# Revit family: CAVP
name_source: partatom
category: Mechanical Equipment
units: mm (PartAtom-declared; Revit-internal decimal feet)

## family parameters
Always vertical = Yes
Cut with Voids When Loaded = No
Part Type = Normal
Room Calculation Point = No
Round Connector Dimension = Use Radius
Shared = No
Work Plane-Based = No

## types (227) — shared parameters
0 = 0"
1" = 1"
1.5 = 1 1/2"
2" = 2"
2' = 24"
3" = 3"
4" = 4"
60 = 60.00°
85 = 85.00°
F-H = 2"
Manufacturer = Loren Cook Company
Model = CAVP
ONE EIGTH = 1/8"
Q = 1"
Q/2 = 1/2"
URL = www.lorencook.com

## per-type parameters (varying)
- 120_CAVP-9L_CLASS_1: ((M - (2 * (D - L - K - J))) / 2) + (TRANSITION / 2)=9 7/32"; (B/2)+1.5"=9 9/16"; (B/2)-.125"=7 15/16"; (D-J-K-L)*2=2 1/16"; (F-((F-H)/2))/2=8 3/4"; (M - (2 * (D - L - K - J)))/2=4 11/16"; (NOZZLE_HEIGHT - (NOZZLE_HEIGHT / 8 * 2)) / 2=10 1/2"; (NOZZLE_WB_OD - NOZZLE_TOP_OD) / 4=2 3/8"; -(F-((F-H)/2))/2=-8 3/4"; A=71"; A/2=35 1/2"; B=16 1/8"; B/2=8 1/16"; B/4=4 1/32"; C=43"; C/2=21 1/2"; CLASS=1"; D=32 13/16"; D-L-K-J=1 1/32"; D-M=21 3/8"; E=26 11/16"; E/2=13 11/32"; E/52*15=7 11/16"; F=21 1/2"; F/2=10 3/4"; H=19 1/2"; H/2=9 3/4"; HEIGHT=33 21/32"; J=6 1/2"; J+K+L=31 25/32"; K=11 7/8"; L=13 13/32"; M=11 7/16"; M-(2*(D-L-K-J))=9 3/8"; N=60"; N+(H/2)=69 3/4"; NOZZLE_BOTTOM_ID=12 13/16"; NOZZLE_BOTTOM_RAD=6 13/32"; NOZZLE_BOTTOM_RAD-3*2=13/32"; NOZZLE_HEIGHT=28"; NOZZLE_HEIGHT/7*2=7"; NOZZLE_SIZE=9"; NOZZLE_TOP_OD=13 1/2"; NOZZLE_TOP_RAD=6 3/4"; NOZZLE_WB/4=4 19/32"; NOZZLE_WB_OD=23"; NOZZLE_WB_RAD=11 1/2"; NOZZLE_WB_RAD-2"=9 1/2"; P=60"; R=22"; R*1.1=24 3/16"; R+((B/2)+1.5")=31 9/16"; R-((B/2)+1.5")=12 7/16"; TRANSITION=9 1/16"; TRANSITION/2=4 17/32"; Type Comments=Vari-Plume Laboratory Exhaust Centrifugal Airfoil Class 1 Arr 10
- 120_CAVP-9H_CLASS_1: ((M - (2 * (D - L - K - J))) / 2) + (TRANSITION / 2)=9 7/32"; (B/2)+1.5"=9 9/16"; (B/2)-.125"=7 15/16"; (D-J-K-L)*2=2 1/16"; (F-((F-H)/2))/2=8 3/4"; (M - (2 * (D - L - K - J)))/2=4 11/16"; (NOZZLE_HEIGHT - (NOZZLE_HEIGHT / 8 * 2)) / 2=10 1/2"; (NOZZLE_WB_OD - NOZZLE_TOP_OD) / 4=2 3/8"; -(F-((F-H)/2))/2=-8 3/4"; A=71"; A/2=35 1/2"; B=16 1/8"; B/2=8 1/16"; B/4=4 1/32"; C=43"; C/2=21 1/2"; CLASS=1"; D=32 13/16"; D-L-K-J=1 1/32"; D-M=21 3/8"; E=26 11/16"; E/2=13 11/32"; E/52*15=7 11/16"; F=21 1/2"; F/2=10 3/4"; H=19 1/2"; H/2=9 3/4"; HEIGHT=33 21/32"; J=6 1/2"; J+K+L=31 25/32"; K=11 7/8"; L=13 13/32"; M=11 7/16"; M-(2*(D-L-K-J))=9 3/8"; N=60"; N+(H/2)=69 3/4"; NOZZLE_BOTTOM_ID=12 13/16"; NOZZLE_BOTTOM_RAD=6 13/32"; NOZZLE_BOTTOM_RAD-3*2=13/32"; NOZZLE_HEIGHT=28"; NOZZLE_HEIGHT/7*2=7"; NOZZLE_SIZE=9"; NOZZLE_TOP_OD=13 1/2"; NOZZLE_TOP_RAD=6 3/4"; NOZZLE_WB/4=4 19/32"; NOZZLE_WB_OD=23"; NOZZLE_WB_RAD=11 1/2"; NOZZLE_WB_RAD-2"=9 1/2"; P=60"; R=22"; R*1.1=24 3/16"; R+((B/2)+1.5")=31 9/16"; R-((B/2)+1.5")=12 7/16"; TRANSITION=9 1/16"; TRANSITION/2=4 17/32"; Type Comments=Vari-Plume Laboratory Exhaust Centrifugal Airfoil Class 1 Arr 10
- 120_CAVP-9L_CLASS_2: ((M - (2 * (D - L - K - J))) / 2) + (TRANSITION / 2)=8 15/32"; (B/2)+1.5"=9 9/16"; (B/2)-.125"=7 15/16"; (D-J-K-L)*2=3 9/16"; (F-((F-H)/2))/2=8 3/4"; (M - (2 * (D - L - K - J)))/2=3 15/16"; (NOZZLE_HEIGHT - (NOZZLE_HEIGHT / 8 * 2)) / 2=10 1/2"; (NOZZLE_WB_OD - NOZZLE_TOP_OD) / 4=2 3/8"; -(F-((F-H)/2))/2=-8 3/4"; A=71"; A/2=35 1/2"; B=16 1/8"; B/2=8 1/16"; B/4=4 1/32"; C=43"; C/2=21 1/2"; CLASS=2"; D=36 13/16"; D-L-K-J=1 25/32"; D-M=25 3/8"; E=26 11/16"; E/2=13 11/32"; E/52*15=7 11/16"; F=21 1/2"; F/2=10 3/4"; H=19 1/2"; H/2=9 3/4"; HEIGHT=33 21/32"; J=6 1/4"; J+K+L=35 1/32"; K=15 3/8"; L=13 13/32"; M=11 7/16"; M-(2*(D-L-K-J))=7 7/8"; N=60"; N+(H/2)=69 3/4"; NOZZLE_BOTTOM_ID=12 13/16"; NOZZLE_BOTTOM_RAD=6 13/32"; NOZZLE_BOTTOM_RAD-3*2=13/32"; NOZZLE_HEIGHT=28"; NOZZLE_HEIGHT/7*2=7"; NOZZLE_SIZE=9"; NOZZLE_TOP_OD=13 1/2"; NOZZLE_TOP_RAD=6 3/4"; NOZZLE_WB/4=4 19/32"; NOZZLE_WB_OD=23"; NOZZLE_WB_RAD=11 1/2"; NOZZLE_WB_RAD-2"=9 1/2"; P=60"; R=22"; R*1.1=24 3/16"; R+((B/2)+1.5")=31 9/16"; R-((B/2)+1.5")=12 7/16"; TRANSITION=9 1/16"; TRANSITION/2=4 17/32"; Type Comments=Vari-Plume Laboratory Exhaust Centrifugal Airfoil Class 2 Arr 10
- 120_CAVP-9H_CLASS_2: ((M - (2 * (D - L - K - J))) / 2) + (TRANSITION / 2)=8 15/32"; (B/2)+1.5"=9 9/16"; (B/2)-.125"=7 15/16"; (D-J-K-L)*2=3 9/16"; (F-((F-H)/2))/2=8 3/4"; (M - (2 * (D - L - K - J)))/2=3 15/16"; (NOZZLE_HEIGHT - (NOZZLE_HEIGHT / 8 * 2)) / 2=10 1/2"; (NOZZLE_WB_OD - NOZZLE_TOP_OD) / 4=2 3/8"; -(F-((F-H)/2))/2=-8 3/4"; A=71"; A/2=35 1/2"; B=16 1/8"; B/2=8 1/16"; B/4=4 1/32"; C=43"; C/2=21 1/2"; CLASS=2"; D=36 13/16"; D-L-K-J=1 25/32"; D-M=25 3/8"; E=26 11/16"; E/2=13 11/32"; E/52*15=7 11/16"; F=21 1/2"; F/2=10 3/4"; H=19 1/2"; H/2=9 3/4"; HEIGHT=33 21/32"; J=6 1/4"; J+K+L=35 1/32"; K=15 3/8"; L=13 13/32"; M=11 7/16"; M-(2*(D-L-K-J))=7 7/8"; N=60"; N+(H/2)=69 3/4"; NOZZLE_BOTTOM_ID=12 13/16"; NOZZLE_BOTTOM_RAD=6 13/32"; NOZZLE_BOTTOM_RAD-3*2=13/32"; NOZZLE_HEIGHT=28"; NOZZLE_HEIGHT/7*2=7"; NOZZLE_SIZE=9"; NOZZLE_TOP_OD=13 1/2"; NOZZLE_TOP_RAD=6 3/4"; NOZZLE_WB/4=4 19/32"; NOZZLE_WB_OD=23"; NOZZLE_WB_RAD=11 1/2"; NOZZLE_WB_RAD-2"=9 1/2"; P=60"; R=22"; R*1.1=24 3/16"; R+((B/2)+1.5")=31 9/16"; R-((B/2)+1.5")=12 7/16"; TRANSITION=9 1/16"; TRANSITION/2=4 17/32"; Type Comments=Vari-Plume Laboratory Exhaust Centrifugal Airfoil Class 2 Arr 10
- 135_CAVP-9L_CLASS_1: ((M - (2 * (D - L - K - J))) / 2) + (TRANSITION / 2)=9 25/32"; (B/2)+1.5"=10 5/16"; (B/2)-.125"=8 11/16"; (D-J-K-L)*2=2 1/16"; (F-((F-H)/2))/2=8 3/4"; (M - (2 * (D - L - K - J)))/2=5 1/4"; (NOZZLE_HEIGHT - (NOZZLE_HEIGHT / 8 * 2)) / 2=10 1/2"; (NOZZLE_WB_OD - NOZZLE_TOP_OD) / 4=2 3/8"; -(F-((F-H)/2))/2=-8 3/4"; A=73 11/16"; A/2=36 27/32"; B=17 5/8"; B/2=8 13/16"; B/4=4 13/32"; C=45 11/16"; C/2=22 27/32"; CLASS=1"; D=34 5/16"; D-L-K-J=1 1/32"; D-M=21 3/4"; E=29 13/16"; E/2=14 29/32"; E/52*15=8 19/32"; F=21 1/2"; F/2=10 3/4"; H=19 1/2"; H/2=9 3/4"; HEIGHT=35 1/32"; J=6 1/2"; J+K+L=33 9/32"; K=12 1/4"; L=14 17/32"; M=12 9/16"; M-(2*(D-L-K-J))=10 1/2"; N=60"; N+(H/2)=69 3/4"; NOZZLE_BOTTOM_ID=12 13/16"; NOZZLE_BOTTOM_RAD=6 13/32"; NOZZLE_BOTTOM_RAD-3*2=13/32"; NOZZLE_HEIGHT=28"; NOZZLE_HEIGHT/7*2=7"; NOZZLE_SIZE=9"; NOZZLE_TOP_OD=13 1/2"; NOZZLE_TOP_RAD=6 3/4"; NOZZLE_WB/4=4 19/32"; NOZZLE_WB_OD=23"; NOZZLE_WB_RAD=11 1/2"; NOZZLE_WB_RAD-2"=9 1/2"; P=60"; R=22"; R*1.1=24 3/16"; R+((B/2)+1.5")=32 5/16"; R-((B/2)+1.5")=11 11/16"; TRANSITION=9 1/16"; TRANSITION/2=4 17/32"; Type Comments=Vari-Plume Laboratory Exhaust Centrifugal Airfoil Class 1 Arr 10
- 135_CAVP-9H_CLASS_1: ((M - (2 * (D - L - K - J))) / 2) + (TRANSITION / 2)=9 25/32"; (B/2)+1.5"=10 5/16"; (B/2)-.125"=8 11/16"; (D-J-K-L)*2=2 1/16"; (F-((F-H)/2))/2=8 3/4"; (M - (2 * (D - L - K - J)))/2=5 1/4"; (NOZZLE_HEIGHT - (NOZZLE_HEIGHT / 8 * 2)) / 2=10 1/2"; (NOZZLE_WB_OD - NOZZLE_TOP_OD) / 4=2 3/8"; -(F-((F-H)/2))/2=-8 3/4"; A=73 11/16"; A/2=36 27/32"; B=17 5/8"; B/2=8 13/16"; B/4=4 13/32"; C=45 11/16"; C/2=22 27/32"; CLASS=1"; D=34 5/16"; D-L-K-J=1 1/32"; D-M=21 3/4"; E=29 13/16"; E/2=14 29/32"; E/52*15=8 19/32"; F=21 1/2"; F/2=10 3/4"; H=19 1/2"; H/2=9 3/4"; HEIGHT=35 1/32"; J=6 1/2"; J+K+L=33 9/32"; K=12 1/4"; L=14 17/32"; M=12 9/16"; M-(2*(D-L-K-J))=10 1/2"; N=60"; N+(H/2)=69 3/4"; NOZZLE_BOTTOM_ID=12 13/16"; NOZZLE_BOTTOM_RAD=6 13/32"; NOZZLE_BOTTOM_RAD-3*2=13/32"; NOZZLE_HEIGHT=28"; NOZZLE_HEIGHT/7*2=7"; NOZZLE_SIZE=9"; NOZZLE_TOP_OD=13 1/2"; NOZZLE_TOP_RAD=6 3/4"; NOZZLE_WB/4=4 19/32"; NOZZLE_WB_OD=23"; NOZZLE_WB_RAD=11 1/2"; NOZZLE_WB_RAD-2"=9 1/2"; P=60"; R=22"; R*1.1=24 3/16"; R+((B/2)+1.5")=32 5/16"; R-((B/2)+1.5")=11 11/16"; TRANSITION=9 1/16"; TRANSITION/2=4 17/32"; Type Comments=Vari-Plume Laboratory Exhaust Centrifugal Airfoil Class 1 Arr 10
- 135_CAVP-9L_CLASS_2: ((M - (2 * (D - L - K - J))) / 2) + (TRANSITION / 2)=9 25/32"; (B/2)+1.5"=10 5/16"; (B/2)-.125"=8 11/16"; (D-J-K-L)*2=2 1/16"; (F-((F-H)/2))/2=8 3/4"; (M - (2 * (D - L - K - J)))/2=5 1/4"; (NOZZLE_HEIGHT - (NOZZLE_HEIGHT / 8 * 2)) / 2=10 1/2"; (NOZZLE_WB_OD - NOZZLE_TOP_OD) / 4=2 3/8"; -(F-((F-H)/2))/2=-8 3/4"; A=73 11/16"; A/2=36 27/32"; B=17 5/8"; B/2=8 13/16"; B/4=4 13/32"; C=45 11/16"; C/2=22 27/32"; CLASS=2"; D=37 3/16"; D-L-K-J=1 1/32"; D-M=24 5/8"; E=29 13/16"; E/2=14 29/32"; E/52*15=8 19/32"; F=21 1/2"; F/2=10 3/4"; H=19 1/2"; H/2=9 3/4"; HEIGHT=35 1/32"; J=6 1/4"; J+K+L=36 5/32"; K=15 3/8"; L=14 17/32"; M=12 9/16"; M-(2*(D-L-K-J))=10 1/2"; N=60"; N+(H/2)=69 3/4"; NOZZLE_BOTTOM_ID=12 13/16"; NOZZLE_BOTTOM_RAD=6 13/32"; NOZZLE_BOTTOM_RAD-3*2=13/32"; NOZZLE_HEIGHT=28"; NOZZLE_HEIGHT/7*2=7"; NOZZLE_SIZE=9"; NOZZLE_TOP_OD=13 1/2"; NOZZLE_TOP_RAD=6 3/4"; NOZZLE_WB/4=4 19/32"; NOZZLE_WB_OD=23"; NOZZLE_WB_RAD=11 1/2"; NOZZLE_WB_RAD-2"=9 1/2"; P=60"; R=22"; R*1.1=24 3/16"; R+((B/2)+1.5")=32 5/16"; R-((B/2)+1.5")=11 11/16"; TRANSITION=9 1/16"; TRANSITION/2=4 17/32"; Type Comments=Vari-Plume Laboratory Exhaust Centrifugal Airfoil Class 2 Arr 10
- 135_CAVP-9H_CLASS_2: ((M - (2 * (D - L - K - J))) / 2) + (TRANSITION / 2)=9 25/32"; (B/2)+1.5"=10 5/16"; (B/2)-.125"=8 11/16"; (D-J-K-L)*2=2 1/16"; (F-((F-H)/2))/2=8 3/4"; (M - (2 * (D - L - K - J)))/2=5 1/4"; (NOZZLE_HEIGHT - (NOZZLE_HEIGHT / 8 * 2)) / 2=10 1/2"; (NOZZLE_WB_OD - NOZZLE_TOP_OD) / 4=2 3/8"; -(F-((F-H)/2))/2=-8 3/4"; A=73 11/16"; A/2=36 27/32"; B=17 5/8"; B/2=8 13/16"; B/4=4 13/32"; C=45 11/16"; C/2=22 27/32"; CLASS=2"; D=37 3/16"; D-L-K-J=1 1/32"; D-M=24 5/8"; E=29 13/16"; E/2=14 29/32"; E/52*15=8 19/32"; F=21 1/2"; F/2=10 3/4"; H=19 1/2"; H/2=9 3/4"; HEIGHT=35 1/32"; J=6 1/4"; J+K+L=36 5/32"; K=15 3/8"; L=14 17/32"; M=12 9/16"; M-(2*(D-L-K-J))=10 1/2"; N=60"; N+(H/2)=69 3/4"; NOZZLE_BOTTOM_ID=12 13/16"; NOZZLE_BOTTOM_RAD=6 13/32"; NOZZLE_BOTTOM_RAD-3*2=13/32"; NOZZLE_HEIGHT=28"; NOZZLE_HEIGHT/7*2=7"; NOZZLE_SIZE=9"; NOZZLE_TOP_OD=13 1/2"; NOZZLE_TOP_RAD=6 3/4"; NOZZLE_WB/4=4 19/32"; NOZZLE_WB_OD=23"; NOZZLE_WB_RAD=11 1/2"; NOZZLE_WB_RAD-2"=9 1/2"; P=60"; R=22"; R*1.1=24 3/16"; R+((B/2)+1.5")=32 5/16"; R-((B/2)+1.5")=11 11/16"; TRANSITION=9 1/16"; TRANSITION/2=4 17/32"; Type Comments=Vari-Plume Laboratory Exhaust Centrifugal Airfoil Class 2 Arr 10
- 150_CAVP-9L_CLASS_1: ((M - (2 * (D - L - K - J))) / 2) + (TRANSITION / 2)=10 11/32"; (B/2)+1.5"=11 1/16"; (B/2)-.125"=9 7/16"; (D-J-K-L)*2=2 1/16"; (F-((F-H)/2))/2=8 3/4"; (M - (2 * (D - L - K - J)))/2=5 13/16"; (NOZZLE_HEIGHT - (NOZZLE_HEIGHT / 8 * 2)) / 2=10 1/2"; (NOZZLE_WB_OD - NOZZLE_TOP_OD) / 4=2 3/8"; -(F-((F-H)/2))/2=-8 3/4"; A=78"; A/2=39"; B=19 1/8"; B/2=9 9/16"; B/4=4 25/32"; C=46 3/4"; C/2=23 3/8"; CLASS=1"; D=35 7/16"; D-L-K-J=1 1/32"; D-M=21 3/4"; E=32 7/8"; E/2=16 7/16"; E/52*15=9 15/32"; F=21 1/2"; F/2=10 3/4"; H=19 1/2"; H/2=9 3/4"; HEIGHT=36 11/32"; J=6 1/2"; J+K+L=34 13/32"; K=12 1/4"; L=15 21/32"; M=13 11/16"; M-(2*(D-L-K-J))=11 5/8"; N=60"; N+(H/2)=69 3/4"; NOZZLE_BOTTOM_ID=12 13/16"; NOZZLE_BOTTOM_RAD=6 13/32"; NOZZLE_BOTTOM_RAD-3*2=13/32"; NOZZLE_HEIGHT=28"; NOZZLE_HEIGHT/7*2=7"; NOZZLE_SIZE=9"; NOZZLE_TOP_OD=13 1/2"; NOZZLE_TOP_RAD=6 3/4"; NOZZLE_WB/4=4 19/32"; NOZZLE_WB_OD=23"; NOZZLE_WB_RAD=11 1/2"; NOZZLE_WB_RAD-2"=9 1/2"; P=60"; R=22"; R*1.1=24 3/16"; R+((B/2)+1.5")=33 1/16"; R-((B/2)+1.5")=10 15/16"; TRANSITION=9 1/16"; TRANSITION/2=4 17/32"; Type Comments=Vari-Plume Laboratory Exhaust Centrifugal Airfoil Class 1 Arr 10
- 150_CAVP-9H_CLASS_1: ((M - (2 * (D - L - K - J))) / 2) + (TRANSITION / 2)=10 11/32"; (B/2)+1.5"=11 1/16"; (B/2)-.125"=9 7/16"; (D-J-K-L)*2=2 1/16"; (F-((F-H)/2))/2=8 3/4"; (M - (2 * (D - L - K - J)))/2=5 13/16"; (NOZZLE_HEIGHT - (NOZZLE_HEIGHT / 8 * 2)) / 2=10 1/2"; (NOZZLE_WB_OD - NOZZLE_TOP_OD) / 4=2 3/8"; -(F-((F-H)/2))/2=-8 3/4"; A=78"; A/2=39"; B=19 1/8"; B/2=9 9/16"; B/4=4 25/32"; C=46 3/4"; C/2=23 3/8"; CLASS=1"; D=35 7/16"; D-L-K-J=1 1/32"; D-M=21 3/4"; E=32 7/8"; E/2=16 7/16"; E/52*15=9 15/32"; F=21 1/2"; F/2=10 3/4"; H=19 1/2"; H/2=9 3/4"; HEIGHT=36 11/32"; J=6 1/2"; J+K+L=34 13/32"; K=12 1/4"; L=15 21/32"; M=13 11/16"; M-(2*(D-L-K-J))=11 5/8"; N=60"; N+(H/2)=69 3/4"; NOZZLE_BOTTOM_ID=12 13/16"; NOZZLE_BOTTOM_RAD=6 13/32"; NOZZLE_BOTTOM_RAD-3*2=13/32"; NOZZLE_HEIGHT=28"; NOZZLE_HEIGHT/7*2=7"; NOZZLE_SIZE=9"; NOZZLE_TOP_OD=13 1/2"; NOZZLE_TOP_RAD=6 3/4"; NOZZLE_WB/4=4 19/32"; NOZZLE_WB_OD=23"; NOZZLE_WB_RAD=11 1/2"; NOZZLE_WB_RAD-2"=9 1/2"; P=60"; R=22"; R*1.1=24 3/16"; R+((B/2)+1.5")=33 1/16"; R-((B/2)+1.5")=10 15/16"; TRANSITION=9 1/16"; TRANSITION/2=4 17/32"; Type Comments=Vari-Plume Laboratory Exhaust Centrifugal Airfoil Class 1 Arr 10
- 150_CAVP-9L_CLASS_2: ((M - (2 * (D - L - K - J))) / 2) + (TRANSITION / 2)=10 11/32"; (B/2)+1.5"=11 1/16"; (B/2)-.125"=9 7/16"; (D-J-K-L)*2=2 1/16"; (F-((F-H)/2))/2=8 3/4"; (M - (2 * (D - L - K - J)))/2=5 13/16"; (NOZZLE_HEIGHT - (NOZZLE_HEIGHT / 8 * 2)) / 2=10 1/2"; (NOZZLE_WB_OD - NOZZLE_TOP_OD) / 4=2 3/8"; -(F-((F-H)/2))/2=-8 3/4"; A=78"; A/2=39"; B=19 1/8"; B/2=9 9/16"; B/4=4 25/32"; C=46 3/4"; C/2=23 3/8"; CLASS=2"; D=38 5/16"; D-L-K-J=1 1/32"; D-M=24 5/8"; E=32 7/8"; E/2=16 7/16"; E/52*15=9 15/32"; F=21 1/2"; F/2=10 3/4"; H=19 1/2"; H/2=9 3/4"; HEIGHT=36 11/32"; J=6 1/4"; J+K+L=37 9/32"; K=15 3/8"; L=15 21/32"; M=13 11/16"; M-(2*(D-L-K-J))=11 5/8"; N=60"; N+(H/2)=69 3/4"; NOZZLE_BOTTOM_ID=12 13/16"; NOZZLE_BOTTOM_RAD=6 13/32"; NOZZLE_BOTTOM_RAD-3*2=13/32"; NOZZLE_HEIGHT=28"; NOZZLE_HEIGHT/7*2=7"; NOZZLE_SIZE=9"; NOZZLE_TOP_OD=13 1/2"; NOZZLE_TOP_RAD=6 3/4"; NOZZLE_WB/4=4 19/32"; NOZZLE_WB_OD=23"; NOZZLE_WB_RAD=11 1/2"; NOZZLE_WB_RAD-2"=9 1/2"; P=60"; R=22"; R*1.1=24 3/16"; R+((B/2)+1.5")=33 1/16"; R-((B/2)+1.5")=10 15/16"; TRANSITION=9 1/16"; TRANSITION/2=4 17/32"; Type Comments=Vari-Plume Laboratory Exhaust Centrifugal Airfoil Class 2 Arr 10
- 150_CAVP-9H_CLASS_2: ((M - (2 * (D - L - K - J))) / 2) + (TRANSITION / 2)=10 11/32"; (B/2)+1.5"=11 1/16"; (B/2)-.125"=9 7/16"; (D-J-K-L)*2=2 1/16"; (F-((F-H)/2))/2=8 3/4"; (M - (2 * (D - L - K - J)))/2=5 13/16"; (NOZZLE_HEIGHT - (NOZZLE_HEIGHT / 8 * 2)) / 2=10 1/2"; (NOZZLE_WB_OD - NOZZLE_TOP_OD) / 4=2 3/8"; -(F-((F-H)/2))/2=-8 3/4"; A=78"; A/2=39"; B=19 1/8"; B/2=9 9/16"; B/4=4 25/32"; C=46 3/4"; C/2=23 3/8"; CLASS=2"; D=38 5/16"; D-L-K-J=1 1/32"; D-M=24 5/8"; E=32 7/8"; E/2=16 7/16"; E/52*15=9 15/32"; F=21 1/2"; F/2=10 3/4"; H=19 1/2"; H/2=9 3/4"; HEIGHT=36 11/32"; J=6 1/4"; J+K+L=37 9/32"; K=15 3/8"; L=15 21/32"; M=13 11/16"; M-(2*(D-L-K-J))=11 5/8"; N=60"; N+(H/2)=69 3/4"; NOZZLE_BOTTOM_ID=12 13/16"; NOZZLE_BOTTOM_RAD=6 13/32"; NOZZLE_BOTTOM_RAD-3*2=13/32"; NOZZLE_HEIGHT=28"; NOZZLE_HEIGHT/7*2=7"; NOZZLE_SIZE=9"; NOZZLE_TOP_OD=13 1/2"; NOZZLE_TOP_RAD=6 3/4"; NOZZLE_WB/4=4 19/32"; NOZZLE_WB_OD=23"; NOZZLE_WB_RAD=11 1/2"; NOZZLE_WB_RAD-2"=9 1/2"; P=60"; R=22"; R*1.1=24 3/16"; R+((B/2)+1.5")=33 1/16"; R-((B/2)+1.5")=10 15/16"; TRANSITION=9 1/16"; TRANSITION/2=4 17/32"; Type Comments=Vari-Plume Laboratory Exhaust Centrifugal Airfoil Class 2 Arr 10
- 150_CAVP-12H_CLASS_2: ((M - (2 * (D - L - K - J))) / 2) + (TRANSITION / 2)=11 27/32"; (B/2)+1.5"=11 1/16"; (B/2)-.125"=9 7/16"; (D-J-K-L)*2=2 1/16"; (F-((F-H)/2))/2=8 3/4"; (M - (2 * (D - L - K - J)))/2=5 13/16"; (NOZZLE_HEIGHT - (NOZZLE_HEIGHT / 8 * 2)) / 2=12"; (NOZZLE_WB_OD - NOZZLE_TOP_OD) / 4=2 1/8"; -(F-((F-H)/2))/2=-8 3/4"; A=78"; A/2=39"; B=19 1/8"; B/2=9 9/16"; B/4=4 25/32"; C=46 3/4"; C/2=23 3/8"; CLASS=2"; D=38 5/16"; D-L-K-J=1 1/32"; D-M=24 5/8"; E=32 7/8"; E/2=16 7/16"; E/52*15=9 15/32"; F=21 1/2"; F/2=10 3/4"; H=19 1/2"; H/2=9 3/4"; HEIGHT=36 11/32"; J=6 1/4"; J+K+L=37 9/32"; K=15 3/8"; L=15 21/32"; M=13 11/16"; M-(2*(D-L-K-J))=11 5/8"; N=60"; N+(H/2)=69 3/4"; NOZZLE_BOTTOM_ID=17 1/16"; NOZZLE_BOTTOM_RAD=8 17/32"; NOZZLE_BOTTOM_RAD-3*2=2 17/32"; NOZZLE_HEIGHT=32"; NOZZLE_HEIGHT/7*2=8"; NOZZLE_SIZE=12"; NOZZLE_TOP_OD=19 1/2"; NOZZLE_TOP_RAD=9 3/4"; NOZZLE_WB/4=5 19/32"; NOZZLE_WB_OD=28"; NOZZLE_WB_RAD=14"; NOZZLE_WB_RAD-2"=12"; P=60"; R=22"; R*1.1=24 3/16"; R+((B/2)+1.5")=33 1/16"; R-((B/2)+1.5")=10 15/16"; TRANSITION=12 1/16"; TRANSITION/2=6 1/32"; Type Comments=Vari-Plume Laboratory Exhaust Centrifugal Airfoil Class 2 Arr 10
- 150_CAVP-12L_CLASS_2: ((M - (2 * (D - L - K - J))) / 2) + (TRANSITION / 2)=11 27/32"; (B/2)+1.5"=11 1/16"; (B/2)-.125"=9 7/16"; (D-J-K-L)*2=2 1/16"; (F-((F-H)/2))/2=8 3/4"; (M - (2 * (D - L - K - J)))/2=5 13/16"; (NOZZLE_HEIGHT - (NOZZLE_HEIGHT / 8 * 2)) / 2=12"; (NOZZLE_WB_OD - NOZZLE_TOP_OD) / 4=2 1/8"; -(F-((F-H)/2))/2=-8 3/4"; A=78"; A/2=39"; B=19 1/8"; B/2=9 9/16"; B/4=4 25/32"; C=46 3/4"; C/2=23 3/8"; CLASS=2"; D=38 5/16"; D-L-K-J=1 1/32"; D-M=24 5/8"; E=32 7/8"; E/2=16 7/16"; E/52*15=9 15/32"; F=21 1/2"; F/2=10 3/4"; H=19 1/2"; H/2=9 3/4"; HEIGHT=36 11/32"; J=6 1/4"; J+K+L=37 9/32"; K=15 3/8"; L=15 21/32"; M=13 11/16"; M-(2*(D-L-K-J))=11 5/8"; N=60"; N+(H/2)=69 3/4"; NOZZLE_BOTTOM_ID=17 1/16"; NOZZLE_BOTTOM_RAD=8 17/32"; NOZZLE_BOTTOM_RAD-3*2=2 17/32"; NOZZLE_HEIGHT=32"; NOZZLE_HEIGHT/7*2=8"; NOZZLE_SIZE=12"; NOZZLE_TOP_OD=19 1/2"; NOZZLE_TOP_RAD=9 3/4"; NOZZLE_WB/4=5 19/32"; NOZZLE_WB_OD=28"; NOZZLE_WB_RAD=14"; NOZZLE_WB_RAD-2"=12"; P=60"; R=22"; R*1.1=24 3/16"; R+((B/2)+1.5")=33 1/16"; R-((B/2)+1.5")=10 15/16"; TRANSITION=12 1/16"; TRANSITION/2=6 1/32"; Type Comments=Vari-Plume Laboratory Exhaust Centrifugal Airfoil Class 2 Arr 10
- 150_CAVP-12H_CLASS_1: ((M - (2 * (D - L - K - J))) / 2) + (TRANSITION / 2)=11 27/32"; (B/2)+1.5"=11 1/16"; (B/2)-.125"=9 7/16"; (D-J-K-L)*2=2 1/16"; (F-((F-H)/2))/2=8 3/4"; (M - (2 * (D - L - K - J)))/2=5 13/16"; (NOZZLE_HEIGHT - (NOZZLE_HEIGHT / 8 * 2)) / 2=12"; (NOZZLE_WB_OD - NOZZLE_TOP_OD) / 4=2 1/8"; -(F-((F-H)/2))/2=-8 3/4"; A=78"; A/2=39"; B=19 1/8"; B/2=9 9/16"; B/4=4 25/32"; C=46 3/4"; C/2=23 3/8"; CLASS=1"; D=35 7/16"; D-L-K-J=1 1/32"; D-M=21 3/4"; E=32 7/8"; E/2=16 7/16"; E/52*15=9 15/32"; F=21 1/2"; F/2=10 3/4"; H=19 1/2"; H/2=9 3/4"; HEIGHT=36 11/32"; J=6 1/2"; J+K+L=34 13/32"; K=12 1/4"; L=15 21/32"; M=13 11/16"; M-(2*(D-L-K-J))=11 5/8"; N=60"; N+(H/2)=69 3/4"; NOZZLE_BOTTOM_ID=17 1/16"; NOZZLE_BOTTOM_RAD=8 17/32"; NOZZLE_BOTTOM_RAD-3*2=2 17/32"; NOZZLE_HEIGHT=32"; NOZZLE_HEIGHT/7*2=8"; NOZZLE_SIZE=12"; NOZZLE_TOP_OD=19 1/2"; NOZZLE_TOP_RAD=9 3/4"; NOZZLE_WB/4=5 19/32"; NOZZLE_WB_OD=28"; NOZZLE_WB_RAD=14"; NOZZLE_WB_RAD-2"=12"; P=60"; R=22"; R*1.1=24 3/16"; R+((B/2)+1.5")=33 1/16"; R-((B/2)+1.5")=10 15/16"; TRANSITION=12 1/16"; TRANSITION/2=6 1/32"; Type Comments=Vari-Plume Laboratory Exhaust Centrifugal Airfoil Class 1 Arr 10
- 150_CAVP-12L_CLASS_1: ((M - (2 * (D - L - K - J))) / 2) + (TRANSITION / 2)=11 27/32"; (B/2)+1.5"=11 1/16"; (B/2)-.125"=9 7/16"; (D-J-K-L)*2=2 1/16"; (F-((F-H)/2))/2=8 3/4"; (M - (2 * (D - L - K - J)))/2=5 13/16"; (NOZZLE_HEIGHT - (NOZZLE_HEIGHT / 8 * 2)) / 2=12"; (NOZZLE_WB_OD - NOZZLE_TOP_OD) / 4=2 1/8"; -(F-((F-H)/2))/2=-8 3/4"; A=78"; A/2=39"; B=19 1/8"; B/2=9 9/16"; B/4=4 25/32"; C=46 3/4"; C/2=23 3/8"; CLASS=1"; D=35 7/16"; D-L-K-J=1 1/32"; D-M=21 3/4"; E=32 7/8"; E/2=16 7/16"; E/52*15=9 15/32"; F=21 1/2"; F/2=10 3/4"; H=19 1/2"; H/2=9 3/4"; HEIGHT=36 11/32"; J=6 1/2"; J+K+L=34 13/32"; K=12 1/4"; L=15 21/32"; M=13 11/16"; M-(2*(D-L-K-J))=11 5/8"; N=60"; N+(H/2)=69 3/4"; NOZZLE_BOTTOM_ID=17 1/16"; NOZZLE_BOTTOM_RAD=8 17/32"; NOZZLE_BOTTOM_RAD-3*2=2 17/32"; NOZZLE_HEIGHT=32"; NOZZLE_HEIGHT/7*2=8"; NOZZLE_SIZE=12"; NOZZLE_TOP_OD=19 1/2"; NOZZLE_TOP_RAD=9 3/4"; NOZZLE_WB/4=5 19/32"; NOZZLE_WB_OD=28"; NOZZLE_WB_RAD=14"; NOZZLE_WB_RAD-2"=12"; P=60"; R=22"; R*1.1=24 3/16"; R+((B/2)+1.5")=33 1/16"; R-((B/2)+1.5")=10 15/16"; TRANSITION=12 1/16"; TRANSITION/2=6 1/32"; Type Comments=Vari-Plume Laboratory Exhaust Centrifugal Airfoil Class 1 Arr 10
- 165_CAVP-9L_CLASS_1: ((M - (2 * (D - L - K - J))) / 2) + (TRANSITION / 2)=10 15/16"; (B/2)+1.5"=12 3/32"; (B/2)-.125"=10 15/32"; (D-J-K-L)*2=2 1/16"; (F-((F-H)/2))/2=11 1/16"; (M - (2 * (D - L - K - J)))/2=6 13/32"; (NOZZLE_HEIGHT - (NOZZLE_HEIGHT / 8 * 2)) / 2=10 1/2"; (NOZZLE_WB_OD - NOZZLE_TOP_OD) / 4=2 3/8"; -(F-((F-H)/2))/2=-11 1/16"; A=82 1/16"; A/2=41 1/32"; B=21 3/16"; B/2=10 19/32"; B/4=5 5/16"; C=50 13/16"; C/2=25 13/32"; CLASS=1"; D=37 5/8"; D-L-K-J=1 1/32"; D-M=22 3/4"; E=36"; E/2=18"; E/52*15=10 3/8"; F=26 1/8"; F/2=13 1/16"; H=24 1/8"; H/2=12 1/16"; HEIGHT=39 31/32"; J=7 1/2"; J+K+L=36 19/32"; K=12 1/4"; L=16 27/32"; M=14 7/8"; M-(2*(D-L-K-J))=12 13/16"; N=60"; N+(H/2)=72 1/16"; NOZZLE_BOTTOM_ID=12 13/16"; NOZZLE_BOTTOM_RAD=6 13/32"; NOZZLE_BOTTOM_RAD-3*2=13/32"; NOZZLE_HEIGHT=28"; NOZZLE_HEIGHT/7*2=7"; NOZZLE_SIZE=9"; NOZZLE_TOP_OD=13 1/2"; NOZZLE_TOP_RAD=6 3/4"; NOZZLE_WB/4=4 19/32"; NOZZLE_WB_OD=23"; NOZZLE_WB_RAD=11 1/2"; NOZZLE_WB_RAD-2"=9 1/2"; P=60"; R=24 1/4"; R*1.1=26 11/16"; R+((B/2)+1.5")=36 11/32"; R-((B/2)+1.5")=12 5/32"; TRANSITION=9 1/16"; TRANSITION/2=4 17/32"; Type Comments=Vari-Plume Laboratory Exhaust Centrifugal Airfoil Class 1 Arr 10
- 165_CAVP-9H_CLASS_1: ((M - (2 * (D - L - K - J))) / 2) + (TRANSITION / 2)=10 15/16"; (B/2)+1.5"=12 3/32"; (B/2)-.125"=10 15/32"; (D-J-K-L)*2=2 1/16"; (F-((F-H)/2))/2=11 1/16"; (M - (2 * (D - L - K - J)))/2=6 13/32"; (NOZZLE_HEIGHT - (NOZZLE_HEIGHT / 8 * 2)) / 2=10 1/2"; (NOZZLE_WB_OD - NOZZLE_TOP_OD) / 4=2 3/8"; -(F-((F-H)/2))/2=-11 1/16"; A=82 1/16"; A/2=41 1/32"; B=21 3/16"; B/2=10 19/32"; B/4=5 5/16"; C=50 13/16"; C/2=25 13/32"; CLASS=1"; D=37 5/8"; D-L-K-J=1 1/32"; D-M=22 3/4"; E=36"; E/2=18"; E/52*15=10 3/8"; F=26 1/8"; F/2=13 1/16"; H=24 1/8"; H/2=12 1/16"; HEIGHT=39 31/32"; J=7 1/2"; J+K+L=36 19/32"; K=12 1/4"; L=16 27/32"; M=14 7/8"; M-(2*(D-L-K-J))=12 13/16"; N=60"; N+(H/2)=72 1/16"; NOZZLE_BOTTOM_ID=12 13/16"; NOZZLE_BOTTOM_RAD=6 13/32"; NOZZLE_BOTTOM_RAD-3*2=13/32"; NOZZLE_HEIGHT=28"; NOZZLE_HEIGHT/7*2=7"; NOZZLE_SIZE=9"; NOZZLE_TOP_OD=13 1/2"; NOZZLE_TOP_RAD=6 3/4"; NOZZLE_WB/4=4 19/32"; NOZZLE_WB_OD=23"; NOZZLE_WB_RAD=11 1/2"; NOZZLE_WB_RAD-2"=9 1/2"; P=60"; R=24 1/4"; R*1.1=26 11/16"; R+((B/2)+1.5")=36 11/32"; R-((B/2)+1.5")=12 5/32"; TRANSITION=9 1/16"; TRANSITION/2=4 17/32"; Type Comments=Vari-Plume Laboratory Exhaust Centrifugal Airfoil Class 1 Arr 10
- 165_CAVP-12L_CLASS_1: ((M - (2 * (D - L - K - J))) / 2) + (TRANSITION / 2)=12 7/16"; (B/2)+1.5"=12 3/32"; (B/2)-.125"=10 15/32"; (D-J-K-L)*2=2 1/16"; (F-((F-H)/2))/2=11 1/16"; (M - (2 * (D - L - K - J)))/2=6 13/32"; (NOZZLE_HEIGHT - (NOZZLE_HEIGHT / 8 * 2)) / 2=12"; (NOZZLE_WB_OD - NOZZLE_TOP_OD) / 4=2 1/8"; -(F-((F-H)/2))/2=-11 1/16"; A=82 1/16"; A/2=41 1/32"; B=21 3/16"; B/2=10 19/32"; B/4=5 5/16"; C=50 13/16"; C/2=25 13/32"; CLASS=1"; D=37 5/8"; D-L-K-J=1 1/32"; D-M=22 3/4"; E=36"; E/2=18"; E/52*15=10 3/8"; F=26 1/8"; F/2=13 1/16"; H=24 1/8"; H/2=12 1/16"; HEIGHT=39 31/32"; J=7 1/2"; J+K+L=36 19/32"; K=12 1/4"; L=16 27/32"; M=14 7/8"; M-(2*(D-L-K-J))=12 13/16"; N=60"; N+(H/2)=72 1/16"; NOZZLE_BOTTOM_ID=17 1/16"; NOZZLE_BOTTOM_RAD=8 17/32"; NOZZLE_BOTTOM_RAD-3*2=2 17/32"; NOZZLE_HEIGHT=32"; NOZZLE_HEIGHT/7*2=8"; NOZZLE_SIZE=12"; NOZZLE_TOP_OD=19 1/2"; NOZZLE_TOP_RAD=9 3/4"; NOZZLE_WB/4=5 19/32"; NOZZLE_WB_OD=28"; NOZZLE_WB_RAD=14"; NOZZLE_WB_RAD-2"=12"; P=60"; R=24 1/4"; R*1.1=26 11/16"; R+((B/2)+1.5")=36 11/32"; R-((B/2)+1.5")=12 5/32"; TRANSITION=12 1/16"; TRANSITION/2=6 1/32"; Type Comments=Vari-Plume Laboratory Exhaust Centrifugal Airfoil Class 1 Arr 10
- 165_CAVP-12H_CLASS_1: ((M - (2 * (D - L - K - J))) / 2) + (TRANSITION / 2)=12 7/16"; (B/2)+1.5"=12 3/32"; (B/2)-.125"=10 15/32"; (D-J-K-L)*2=2 1/16"; (F-((F-H)/2))/2=11 1/16"; (M - (2 * (D - L - K - J)))/2=6 13/32"; (NOZZLE_HEIGHT - (NOZZLE_HEIGHT / 8 * 2)) / 2=12"; (NOZZLE_WB_OD - NOZZLE_TOP_OD) / 4=2 1/8"; -(F-((F-H)/2))/2=-11 1/16"; A=82 1/16"; A/2=41 1/32"; B=21 3/16"; B/2=10 19/32"; B/4=5 5/16"; C=50 13/16"; C/2=25 13/32"; CLASS=1"; D=37 5/8"; D-L-K-J=1 1/32"; D-M=22 3/4"; E=36"; E/2=18"; E/52*15=10 3/8"; F=26 1/8"; F/2=13 1/16"; H=24 1/8"; H/2=12 1/16"; HEIGHT=39 31/32"; J=7 1/2"; J+K+L=36 19/32"; K=12 1/4"; L=16 27/32"; M=14 7/8"; M-(2*(D-L-K-J))=12 13/16"; N=60"; N+(H/2)=72 1/16"; NOZZLE_BOTTOM_ID=17 1/16"; NOZZLE_BOTTOM_RAD=8 17/32"; NOZZLE_BOTTOM_RAD-3*2=2 17/32"; NOZZLE_HEIGHT=32"; NOZZLE_HEIGHT/7*2=8"; NOZZLE_SIZE=12"; NOZZLE_TOP_OD=19 1/2"; NOZZLE_TOP_RAD=9 3/4"; NOZZLE_WB/4=5 19/32"; NOZZLE_WB_OD=28"; NOZZLE_WB_RAD=14"; NOZZLE_WB_RAD-2"=12"; P=60"; R=24 1/4"; R*1.1=26 11/16"; R+((B/2)+1.5")=36 11/32"; R-((B/2)+1.5")=12 5/32"; TRANSITION=12 1/16"; TRANSITION/2=6 1/32"; Type Comments=Vari-Plume Laboratory Exhaust Centrifugal Airfoil Class 1 Arr 10
- 165_CAVP-9L_CLASS_2: ((M - (2 * (D - L - K - J))) / 2) + (TRANSITION / 2)=10 15/16"; (B/2)+1.5"=12 3/32"; (B/2)-.125"=10 15/32"; (D-J-K-L)*2=2 1/16"; (F-((F-H)/2))/2=11 1/16"; (M - (2 * (D - L - K - J)))/2=6 13/32"; (NOZZLE_HEIGHT - (NOZZLE_HEIGHT / 8 * 2)) / 2=10 1/2"; (NOZZLE_WB_OD - NOZZLE_TOP_OD) / 4=2 3/8"; -(F-((F-H)/2))/2=-11 1/16"; A=82 1/16"; A/2=41 1/32"; B=21 3/16"; B/2=10 19/32"; B/4=5 5/16"; C=50 13/16"; C/2=25 13/32"; CLASS=2"; D=44 1/2"; D-L-K-J=1 1/32"; D-M=29 5/8"; E=36"; E/2=18"; E/52*15=10 3/8"; F=26 1/8"; F/2=13 1/16"; H=24 1/8"; H/2=12 1/16"; HEIGHT=39 31/32"; J=7 1/4"; J+K+L=43 15/32"; K=19 3/8"; L=16 27/32"; M=14 7/8"; M-(2*(D-L-K-J))=12 13/16"; N=60"; N+(H/2)=72 1/16"; NOZZLE_BOTTOM_ID=12 13/16"; NOZZLE_BOTTOM_RAD=6 13/32"; NOZZLE_BOTTOM_RAD-3*2=13/32"; NOZZLE_HEIGHT=28"; NOZZLE_HEIGHT/7*2=7"; NOZZLE_SIZE=9"; NOZZLE_TOP_OD=13 1/2"; NOZZLE_TOP_RAD=6 3/4"; NOZZLE_WB/4=4 19/32"; NOZZLE_WB_OD=23"; NOZZLE_WB_RAD=11 1/2"; NOZZLE_WB_RAD-2"=9 1/2"; P=60"; R=24 1/4"; R*1.1=26 11/16"; R+((B/2)+1.5")=36 11/32"; R-((B/2)+1.5")=12 5/32"; TRANSITION=9 1/16"; TRANSITION/2=4 17/32"; Type Comments=Vari-Plume Laboratory Exhaust Centrifugal Airfoil Class 2 Arr 10
- 165_CAVP-9H_CLASS_2: ((M - (2 * (D - L - K - J))) / 2) + (TRANSITION / 2)=10 15/16"; (B/2)+1.5"=12 3/32"; (B/2)-.125"=10 15/32"; (D-J-K-L)*2=2 1/16"; (F-((F-H)/2))/2=11 1/16"; (M - (2 * (D - L - K - J)))/2=6 13/32"; (NOZZLE_HEIGHT - (NOZZLE_HEIGHT / 8 * 2)) / 2=10 1/2"; (NOZZLE_WB_OD - NOZZLE_TOP_OD) / 4=2 3/8"; -(F-((F-H)/2))/2=-11 1/16"; A=82 1/16"; A/2=41 1/32"; B=21 3/16"; B/2=10 19/32"; B/4=5 5/16"; C=50 13/16"; C/2=25 13/32"; CLASS=2"; D=44 1/2"; D-L-K-J=1 1/32"; D-M=29 5/8"; E=36"; E/2=18"; E/52*15=10 3/8"; F=26 1/8"; F/2=13 1/16"; H=24 1/8"; H/2=12 1/16"; HEIGHT=39 31/32"; J=7 1/4"; J+K+L=43 15/32"; K=19 3/8"; L=16 27/32"; M=14 7/8"; M-(2*(D-L-K-J))=12 13/16"; N=60"; N+(H/2)=72 1/16"; NOZZLE_BOTTOM_ID=12 13/16"; NOZZLE_BOTTOM_RAD=6 13/32"; NOZZLE_BOTTOM_RAD-3*2=13/32"; NOZZLE_HEIGHT=28"; NOZZLE_HEIGHT/7*2=7"; NOZZLE_SIZE=9"; NOZZLE_TOP_OD=13 1/2"; NOZZLE_TOP_RAD=6 3/4"; NOZZLE_WB/4=4 19/32"; NOZZLE_WB_OD=23"; NOZZLE_WB_RAD=11 1/2"; NOZZLE_WB_RAD-2"=9 1/2"; P=60"; R=24 1/4"; R*1.1=26 11/16"; R+((B/2)+1.5")=36 11/32"; R-((B/2)+1.5")=12 5/32"; TRANSITION=9 1/16"; TRANSITION/2=4 17/32"; Type Comments=Vari-Plume Laboratory Exhaust Centrifugal Airfoil Class 2 Arr 10
- 165_CAVP-12L_CLASS_2: ((M - (2 * (D - L - K - J))) / 2) + (TRANSITION / 2)=12 7/16"; (B/2)+1.5"=12 3/32"; (B/2)-.125"=10 15/32"; (D-J-K-L)*2=2 1/16"; (F-((F-H)/2))/2=11 1/16"; (M - (2 * (D - L - K - J)))/2=6 13/32"; (NOZZLE_HEIGHT - (NOZZLE_HEIGHT / 8 * 2)) / 2=12"; (NOZZLE_WB_OD - NOZZLE_TOP_OD) / 4=2 1/8"; -(F-((F-H)/2))/2=-11 1/16"; A=82 1/16"; A/2=41 1/32"; B=21 3/16"; B/2=10 19/32"; B/4=5 5/16"; C=50 13/16"; C/2=25 13/32"; CLASS=2"; D=44 1/2"; D-L-K-J=1 1/32"; D-M=29 5/8"; E=36"; E/2=18"; E/52*15=10 3/8"; F=26 1/8"; F/2=13 1/16"; H=24 1/8"; H/2=12 1/16"; HEIGHT=39 31/32"; J=7 1/4"; J+K+L=43 15/32"; K=19 3/8"; L=16 27/32"; M=14 7/8"; M-(2*(D-L-K-J))=12 13/16"; N=60"; N+(H/2)=72 1/16"; NOZZLE_BOTTOM_ID=17 1/16"; NOZZLE_BOTTOM_RAD=8 17/32"; NOZZLE_BOTTOM_RAD-3*2=2 17/32"; NOZZLE_HEIGHT=32"; NOZZLE_HEIGHT/7*2=8"; NOZZLE_SIZE=12"; NOZZLE_TOP_OD=19 1/2"; NOZZLE_TOP_RAD=9 3/4"; NOZZLE_WB/4=5 19/32"; NOZZLE_WB_OD=28"; NOZZLE_WB_RAD=14"; NOZZLE_WB_RAD-2"=12"; P=60"; R=24 1/4"; R*1.1=26 11/16"; R+((B/2)+1.5")=36 11/32"; R-((B/2)+1.5")=12 5/32"; TRANSITION=12 1/16"; TRANSITION/2=6 1/32"; Type Comments=Vari-Plume Laboratory Exhaust Centrifugal Airfoil Class 2 Arr 10
- 165_CAVP-12H_CLASS_2: ((M - (2 * (D - L - K - J))) / 2) + (TRANSITION / 2)=12 7/16"; (B/2)+1.5"=12 3/32"; (B/2)-.125"=10 15/32"; (D-J-K-L)*2=2 1/16"; (F-((F-H)/2))/2=11 1/16"; (M - (2 * (D - L - K - J)))/2=6 13/32"; (NOZZLE_HEIGHT - (NOZZLE_HEIGHT / 8 * 2)) / 2=12"; (NOZZLE_WB_OD - NOZZLE_TOP_OD) / 4=2 1/8"; -(F-((F-H)/2))/2=-11 1/16"; A=82 1/16"; A/2=41 1/32"; B=21 3/16"; B/2=10 19/32"; B/4=5 5/16"; C=50 13/16"; C/2=25 13/32"; CLASS=2"; D=44 1/2"; D-L-K-J=1 1/32"; D-M=29 5/8"; E=36"; E/2=18"; E/52*15=10 3/8"; F=26 1/8"; F/2=13 1/16"; H=24 1/8"; H/2=12 1/16"; HEIGHT=39 31/32"; J=7 1/4"; J+K+L=43 15/32"; K=19 3/8"; L=16 27/32"; M=14 7/8"; M-(2*(D-L-K-J))=12 13/16"; N=60"; N+(H/2)=72 1/16"; NOZZLE_BOTTOM_ID=17 1/16"; NOZZLE_BOTTOM_RAD=8 17/32"; NOZZLE_BOTTOM_RAD-3*2=2 17/32"; NOZZLE_HEIGHT=32"; NOZZLE_HEIGHT/7*2=8"; NOZZLE_SIZE=12"; NOZZLE_TOP_OD=19 1/2"; NOZZLE_TOP_RAD=9 3/4"; NOZZLE_WB/4=5 19/32"; NOZZLE_WB_OD=28"; NOZZLE_WB_RAD=14"; NOZZLE_WB_RAD-2"=12"; P=60"; R=24 1/4"; R*1.1=26 11/16"; R+((B/2)+1.5")=36 11/32"; R-((B/2)+1.5")=12 5/32"; TRANSITION=12 1/16"; TRANSITION/2=6 1/32"; Type Comments=Vari-Plume Laboratory Exhaust Centrifugal Airfoil Class 2 Arr 10
- 180_CAVP-9H_CLASS_1: ((M - (2 * (D - L - K - J))) / 2) + (TRANSITION / 2)=11 1/2"; (B/2)+1.5"=12 27/32"; (B/2)-.125"=11 7/32"; (D-J-K-L)*2=2 1/16"; (F-((F-H)/2))/2=11 1/16"; (M - (2 * (D - L - K - J)))/2=6 31/32"; (NOZZLE_HEIGHT - (NOZZLE_HEIGHT / 8 * 2)) / 2=10 1/2"; (NOZZLE_WB_OD - NOZZLE_TOP_OD) / 4=2 3/8"; -(F-((F-H)/2))/2=-11 1/16"; A=84 1/16"; A/2=42 1/32"; B=22 11/16"; B/2=11 11/32"; B/4=5 11/16"; C=52 13/16"; C/2=26 13/32"; CLASS=1"; D=42 1/8"; D-L-K-J=1 1/32"; D-M=26 1/8"; E=39 1/16"; E/2=19 17/32"; E/52*15=11 9/32"; F=26 1/8"; F/2=13 1/16"; H=24 1/8"; H/2=12 1/16"; HEIGHT=41 5/16"; J=8"; J+K+L=41 3/32"; K=15 1/8"; L=17 31/32"; M=16"; M-(2*(D-L-K-J))=13 15/16"; N=60"; N+(H/2)=72 1/16"; NOZZLE_BOTTOM_ID=12 13/16"; NOZZLE_BOTTOM_RAD=6 13/32"; NOZZLE_BOTTOM_RAD-3*2=13/32"; NOZZLE_HEIGHT=28"; NOZZLE_HEIGHT/7*2=7"; NOZZLE_SIZE=9"; NOZZLE_TOP_OD=13 1/2"; NOZZLE_TOP_RAD=6 3/4"; NOZZLE_WB/4=4 19/32"; NOZZLE_WB_OD=23"; NOZZLE_WB_RAD=11 1/2"; NOZZLE_WB_RAD-2"=9 1/2"; P=60"; R=24 1/4"; R*1.1=26 11/16"; R+((B/2)+1.5")=37 3/32"; R-((B/2)+1.5")=11 13/32"; TRANSITION=9 1/16"; TRANSITION/2=4 17/32"; Type Comments=Vari-Plume Laboratory Exhaust Centrifugal Airfoil Class 1 Arr 10
- 180_CAVP-9L_CLASS_1: ((M - (2 * (D - L - K - J))) / 2) + (TRANSITION / 2)=11 1/2"; (B/2)+1.5"=12 27/32"; (B/2)-.125"=11 7/32"; (D-J-K-L)*2=2 1/16"; (F-((F-H)/2))/2=11 1/16"; (M - (2 * (D - L - K - J)))/2=6 31/32"; (NOZZLE_HEIGHT - (NOZZLE_HEIGHT / 8 * 2)) / 2=10 1/2"; (NOZZLE_WB_OD - NOZZLE_TOP_OD) / 4=2 3/8"; -(F-((F-H)/2))/2=-11 1/16"; A=84 1/16"; A/2=42 1/32"; B=22 11/16"; B/2=11 11/32"; B/4=5 11/16"; C=52 13/16"; C/2=26 13/32"; CLASS=1"; D=42 1/8"; D-L-K-J=1 1/32"; D-M=26 1/8"; E=39 1/16"; E/2=19 17/32"; E/52*15=11 9/32"; F=26 1/8"; F/2=13 1/16"; H=24 1/8"; H/2=12 1/16"; HEIGHT=41 5/16"; J=8"; J+K+L=41 3/32"; K=15 1/8"; L=17 31/32"; M=16"; M-(2*(D-L-K-J))=13 15/16"; N=60"; N+(H/2)=72 1/16"; NOZZLE_BOTTOM_ID=12 13/16"; NOZZLE_BOTTOM_RAD=6 13/32"; NOZZLE_BOTTOM_RAD-3*2=13/32"; NOZZLE_HEIGHT=28"; NOZZLE_HEIGHT/7*2=7"; NOZZLE_SIZE=9"; NOZZLE_TOP_OD=13 1/2"; NOZZLE_TOP_RAD=6 3/4"; NOZZLE_WB/4=4 19/32"; NOZZLE_WB_OD=23"; NOZZLE_WB_RAD=11 1/2"; NOZZLE_WB_RAD-2"=9 1/2"; P=60"; R=24 1/4"; R*1.1=26 11/16"; R+((B/2)+1.5")=37 3/32"; R-((B/2)+1.5")=11 13/32"; TRANSITION=9 1/16"; TRANSITION/2=4 17/32"; Type Comments=Vari-Plume Laboratory Exhaust Centrifugal Airfoil Class 1 Arr 10
- 180_CAVP-12H_CLASS_1: ((M - (2 * (D - L - K - J))) / 2) + (TRANSITION / 2)=13"; (B/2)+1.5"=12 27/32"; (B/2)-.125"=11 7/32"; (D-J-K-L)*2=2 1/16"; (F-((F-H)/2))/2=11 1/16"; (M - (2 * (D - L - K - J)))/2=6 31/32"; (NOZZLE_HEIGHT - (NOZZLE_HEIGHT / 8 * 2)) / 2=12"; (NOZZLE_WB_OD - NOZZLE_TOP_OD) / 4=2 1/8"; -(F-((F-H)/2))/2=-11 1/16"; A=84 1/16"; A/2=42 1/32"; B=22 11/16"; B/2=11 11/32"; B/4=5 11/16"; C=52 13/16"; C/2=26 13/32"; CLASS=1"; D=42 1/8"; D-L-K-J=1 1/32"; D-M=26 1/8"; E=39 1/16"; E/2=19 17/32"; E/52*15=11 9/32"; F=26 1/8"; F/2=13 1/16"; H=24 1/8"; H/2=12 1/16"; HEIGHT=41 5/16"; J=8"; J+K+L=41 3/32"; K=15 1/8"; L=17 31/32"; M=16"; M-(2*(D-L-K-J))=13 15/16"; N=60"; N+(H/2)=72 1/16"; NOZZLE_BOTTOM_ID=17 1/16"; NOZZLE_BOTTOM_RAD=8 17/32"; NOZZLE_BOTTOM_RAD-3*2=2 17/32"; NOZZLE_HEIGHT=32"; NOZZLE_HEIGHT/7*2=8"; NOZZLE_SIZE=12"; NOZZLE_TOP_OD=19 1/2"; NOZZLE_TOP_RAD=9 3/4"; NOZZLE_WB/4=5 19/32"; NOZZLE_WB_OD=28"; NOZZLE_WB_RAD=14"; NOZZLE_WB_RAD-2"=12"; P=60"; R=24 1/4"; R*1.1=26 11/16"; R+((B/2)+1.5")=37 3/32"; R-((B/2)+1.5")=11 13/32"; TRANSITION=12 1/16"; TRANSITION/2=6 1/32"; Type Comments=Vari-Plume Laboratory Exhaust Centrifugal Airfoil Class 1 Arr 10
- 180_CAVP-12L_CLASS_1: ((M - (2 * (D - L - K - J))) / 2) + (TRANSITION / 2)=13"; (B/2)+1.5"=12 27/32"; (B/2)-.125"=11 7/32"; (D-J-K-L)*2=2 1/16"; (F-((F-H)/2))/2=11 1/16"; (M - (2 * (D - L - K - J)))/2=6 31/32"; (NOZZLE_HEIGHT - (NOZZLE_HEIGHT / 8 * 2)) / 2=12"; (NOZZLE_WB_OD - NOZZLE_TOP_OD) / 4=2 1/8"; -(F-((F-H)/2))/2=-11 1/16"; A=84 1/16"; A/2=42 1/32"; B=22 11/16"; B/2=11 11/32"; B/4=5 11/16"; C=52 13/16"; C/2=26 13/32"; CLASS=1"; D=42 1/8"; D-L-K-J=1 1/32"; D-M=26 1/8"; E=39 1/16"; E/2=19 17/32"; E/52*15=11 9/32"; F=26 1/8"; F/2=13 1/16"; H=24 1/8"; H/2=12 1/16"; HEIGHT=41 5/16"; J=8"; J+K+L=41 3/32"; K=15 1/8"; L=17 31/32"; M=16"; M-(2*(D-L-K-J))=13 15/16"; N=60"; N+(H/2)=72 1/16"; NOZZLE_BOTTOM_ID=17 1/16"; NOZZLE_BOTTOM_RAD=8 17/32"; NOZZLE_BOTTOM_RAD-3*2=2 17/32"; NOZZLE_HEIGHT=32"; NOZZLE_HEIGHT/7*2=8"; NOZZLE_SIZE=12"; NOZZLE_TOP_OD=19 1/2"; NOZZLE_TOP_RAD=9 3/4"; NOZZLE_WB/4=5 19/32"; NOZZLE_WB_OD=28"; NOZZLE_WB_RAD=14"; NOZZLE_WB_RAD-2"=12"; P=60"; R=24 1/4"; R*1.1=26 11/16"; R+((B/2)+1.5")=37 3/32"; R-((B/2)+1.5")=11 13/32"; TRANSITION=12 1/16"; TRANSITION/2=6 1/32"; Type Comments=Vari-Plume Laboratory Exhaust Centrifugal Airfoil Class 1 Arr 10
- 180_CAVP-9H_CLASS_2: ((M - (2 * (D - L - K - J))) / 2) + (TRANSITION / 2)=11 1/2"; (B/2)+1.5"=12 27/32"; (B/2)-.125"=11 7/32"; (D-J-K-L)*2=2 1/16"; (F-((F-H)/2))/2=11 1/16"; (M - (2 * (D - L - K - J)))/2=6 31/32"; (NOZZLE_HEIGHT - (NOZZLE_HEIGHT / 8 * 2)) / 2=10 1/2"; (NOZZLE_WB_OD - NOZZLE_TOP_OD) / 4=2 3/8"; -(F-((F-H)/2))/2=-11 1/16"; A=84 1/16"; A/2=42 1/32"; B=22 11/16"; B/2=11 11/32"; B/4=5 11/16"; C=52 13/16"; C/2=26 13/32"; CLASS=2"; D=46 1/8"; D-L-K-J=1 1/32"; D-M=30 1/8"; E=39 1/16"; E/2=19 17/32"; E/52*15=11 9/32"; F=26 1/8"; F/2=13 1/16"; H=24 1/8"; H/2=12 1/16"; HEIGHT=41 5/16"; J=7 3/4"; J+K+L=45 3/32"; K=19 3/8"; L=17 31/32"; M=16"; M-(2*(D-L-K-J))=13 15/16"; N=60"; N+(H/2)=72 1/16"; NOZZLE_BOTTOM_ID=12 13/16"; NOZZLE_BOTTOM_RAD=6 13/32"; NOZZLE_BOTTOM_RAD-3*2=13/32"; NOZZLE_HEIGHT=28"; NOZZLE_HEIGHT/7*2=7"; NOZZLE_SIZE=9"; NOZZLE_TOP_OD=13 1/2"; NOZZLE_TOP_RAD=6 3/4"; NOZZLE_WB/4=4 19/32"; NOZZLE_WB_OD=23"; NOZZLE_WB_RAD=11 1/2"; NOZZLE_WB_RAD-2"=9 1/2"; P=60"; R=24 1/4"; R*1.1=26 11/16"; R+((B/2)+1.5")=37 3/32"; R-((B/2)+1.5")=11 13/32"; TRANSITION=9 1/16"; TRANSITION/2=4 17/32"; Type Comments=Vari-Plume Laboratory Exhaust Centrifugal Airfoil Class 2 Arr 10
- 180_CAVP-9L_CLASS_2: ((M - (2 * (D - L - K - J))) / 2) + (TRANSITION / 2)=11 1/2"; (B/2)+1.5"=12 27/32"; (B/2)-.125"=11 7/32"; (D-J-K-L)*2=2 1/16"; (F-((F-H)/2))/2=11 1/16"; (M - (2 * (D - L - K - J)))/2=6 31/32"; (NOZZLE_HEIGHT - (NOZZLE_HEIGHT / 8 * 2)) / 2=10 1/2"; (NOZZLE_WB_OD - NOZZLE_TOP_OD) / 4=2 3/8"; -(F-((F-H)/2))/2=-11 1/16"; A=84 1/16"; A/2=42 1/32"; B=22 11/16"; B/2=11 11/32"; B/4=5 11/16"; C=52 13/16"; C/2=26 13/32"; CLASS=2"; D=46 1/8"; D-L-K-J=1 1/32"; D-M=30 1/8"; E=39 1/16"; E/2=19 17/32"; E/52*15=11 9/32"; F=26 1/8"; F/2=13 1/16"; H=24 1/8"; H/2=12 1/16"; HEIGHT=41 5/16"; J=7 3/4"; J+K+L=45 3/32"; K=19 3/8"; L=17 31/32"; M=16"; M-(2*(D-L-K-J))=13 15/16"; N=60"; N+(H/2)=72 1/16"; NOZZLE_BOTTOM_ID=12 13/16"; NOZZLE_BOTTOM_RAD=6 13/32"; NOZZLE_BOTTOM_RAD-3*2=13/32"; NOZZLE_HEIGHT=28"; NOZZLE_HEIGHT/7*2=7"; NOZZLE_SIZE=9"; NOZZLE_TOP_OD=13 1/2"; NOZZLE_TOP_RAD=6 3/4"; NOZZLE_WB/4=4 19/32"; NOZZLE_WB_OD=23"; NOZZLE_WB_RAD=11 1/2"; NOZZLE_WB_RAD-2"=9 1/2"; P=60"; R=24 1/4"; R*1.1=26 11/16"; R+((B/2)+1.5")=37 3/32"; R-((B/2)+1.5")=11 13/32"; TRANSITION=9 1/16"; TRANSITION/2=4 17/32"; Type Comments=Vari-Plume Laboratory Exhaust Centrifugal Airfoil Class 2 Arr 10
- 180_CAVP-12H_CLASS_2: ((M - (2 * (D - L - K - J))) / 2) + (TRANSITION / 2)=13"; (B/2)+1.5"=12 27/32"; (B/2)-.125"=11 7/32"; (D-J-K-L)*2=2 1/16"; (F-((F-H)/2))/2=11 1/16"; (M - (2 * (D - L - K - J)))/2=6 31/32"; (NOZZLE_HEIGHT - (NOZZLE_HEIGHT / 8 * 2)) / 2=12"; (NOZZLE_WB_OD - NOZZLE_TOP_OD) / 4=2 1/8"; -(F-((F-H)/2))/2=-11 1/16"; A=84 1/16"; A/2=42 1/32"; B=22 11/16"; B/2=11 11/32"; B/4=5 11/16"; C=52 13/16"; C/2=26 13/32"; CLASS=2"; D=46 1/8"; D-L-K-J=1 1/32"; D-M=30 1/8"; E=39 1/16"; E/2=19 17/32"; E/52*15=11 9/32"; F=26 1/8"; F/2=13 1/16"; H=24 1/8"; H/2=12 1/16"; HEIGHT=41 5/16"; J=7 3/4"; J+K+L=45 3/32"; K=19 3/8"; L=17 31/32"; M=16"; M-(2*(D-L-K-J))=13 15/16"; N=60"; N+(H/2)=72 1/16"; NOZZLE_BOTTOM_ID=17 1/16"; NOZZLE_BOTTOM_RAD=8 17/32"; NOZZLE_BOTTOM_RAD-3*2=2 17/32"; NOZZLE_HEIGHT=32"; NOZZLE_HEIGHT/7*2=8"; NOZZLE_SIZE=12"; NOZZLE_TOP_OD=19 1/2"; NOZZLE_TOP_RAD=9 3/4"; NOZZLE_WB/4=5 19/32"; NOZZLE_WB_OD=28"; NOZZLE_WB_RAD=14"; NOZZLE_WB_RAD-2"=12"; P=60"; R=24 1/4"; R*1.1=26 11/16"; R+((B/2)+1.5")=37 3/32"; R-((B/2)+1.5")=11 13/32"; TRANSITION=12 1/16"; TRANSITION/2=6 1/32"; Type Comments=Vari-Plume Laboratory Exhaust Centrifugal Airfoil Class 2 Arr 10
- 180_CAVP-12L_CLASS_2: ((M - (2 * (D - L - K - J))) / 2) + (TRANSITION / 2)=13"; (B/2)+1.5"=12 27/32"; (B/2)-.125"=11 7/32"; (D-J-K-L)*2=2 1/16"; (F-((F-H)/2))/2=11 1/16"; (M - (2 * (D - L - K - J)))/2=6 31/32"; (NOZZLE_HEIGHT - (NOZZLE_HEIGHT / 8 * 2)) / 2=12"; (NOZZLE_WB_OD - NOZZLE_TOP_OD) / 4=2 1/8"; -(F-((F-H)/2))/2=-11 1/16"; A=84 1/16"; A/2=42 1/32"; B=22 11/16"; B/2=11 11/32"; B/4=5 11/16"; C=52 13/16"; C/2=26 13/32"; CLASS=2"; D=46 1/8"; D-L-K-J=1 1/32"; D-M=30 1/8"; E=39 1/16"; E/2=19 17/32"; E/52*15=11 9/32"; F=26 1/8"; F/2=13 1/16"; H=24 1/8"; H/2=12 1/16"; HEIGHT=41 5/16"; J=7 3/4"; J+K+L=45 3/32"; K=19 3/8"; L=17 31/32"; M=16"; M-(2*(D-L-K-J))=13 15/16"; N=60"; N+(H/2)=72 1/16"; NOZZLE_BOTTOM_ID=17 1/16"; NOZZLE_BOTTOM_RAD=8 17/32"; NOZZLE_BOTTOM_RAD-3*2=2 17/32"; NOZZLE_HEIGHT=32"; NOZZLE_HEIGHT/7*2=8"; NOZZLE_SIZE=12"; NOZZLE_TOP_OD=19 1/2"; NOZZLE_TOP_RAD=9 3/4"; NOZZLE_WB/4=5 19/32"; NOZZLE_WB_OD=28"; NOZZLE_WB_RAD=14"; NOZZLE_WB_RAD-2"=12"; P=60"; R=24 1/4"; R*1.1=26 11/16"; R+((B/2)+1.5")=37 3/32"; R-((B/2)+1.5")=11 13/32"; TRANSITION=12 1/16"; TRANSITION/2=6 1/32"; Type Comments=Vari-Plume Laboratory Exhaust Centrifugal Airfoil Class 2 Arr 10
- 195_CAVP-9L_CLASS_1: ((M - (2 * (D - L - K - J))) / 2) + (TRANSITION / 2)=12 1/8"; (B/2)+1.5"=13 19/32"; (B/2)-.125"=11 31/32"; (D-J-K-L)*2=2"; (F-((F-H)/2))/2=11 3/4"; (M - (2 * (D - L - K - J)))/2=7 19/32"; (NOZZLE_HEIGHT - (NOZZLE_HEIGHT / 8 * 2)) / 2=10 1/2"; (NOZZLE_WB_OD - NOZZLE_TOP_OD) / 4=2 3/8"; -(F-((F-H)/2))/2=-11 3/4"; A=96 3/4"; A/2=48 3/8"; B=24 3/16"; B/2=12 3/32"; B/4=6 1/16"; C=54 1/4"; C/2=27 1/8"; CLASS=1"; D=43 5/16"; D-L-K-J=1"; D-M=26 1/8"; E=42 3/16"; E/2=21 3/32"; E/52*15=12 5/32"; F=27 1/2"; F/2=13 3/4"; H=25 1/2"; H/2=12 3/4"; HEIGHT=42 11/16"; J=8"; J+K+L=42 5/16"; K=15 1/8"; L=19 3/16"; M=17 3/16"; M-(2*(D-L-K-J))=15 3/16"; N=6 11/32"; N+(H/2)=19 3/32"; NOZZLE_BOTTOM_ID=12 13/16"; NOZZLE_BOTTOM_RAD=6 13/32"; NOZZLE_BOTTOM_RAD-3*2=13/32"; NOZZLE_HEIGHT=28"; NOZZLE_HEIGHT/7*2=7"; NOZZLE_SIZE=9"; NOZZLE_TOP_OD=13 1/2"; NOZZLE_TOP_RAD=6 3/4"; NOZZLE_WB/4=4 19/32"; NOZZLE_WB_OD=23"; NOZZLE_WB_RAD=11 1/2"; NOZZLE_WB_RAD-2"=9 1/2"; P=60"; R=24 1/4"; R*1.1=26 11/16"; R+((B/2)+1.5")=37 27/32"; R-((B/2)+1.5")=10 21/32"; TRANSITION=9 1/16"; TRANSITION/2=4 17/32"; Type Comments=Vari-Plume Laboratory Exhaust Centrifugal Airfoil Class 1 Arr 10
- 195_CAVP-9H_CLASS_1: ((M - (2 * (D - L - K - J))) / 2) + (TRANSITION / 2)=12 1/8"; (B/2)+1.5"=13 19/32"; (B/2)-.125"=11 31/32"; (D-J-K-L)*2=2"; (F-((F-H)/2))/2=11 3/4"; (M - (2 * (D - L - K - J)))/2=7 19/32"; (NOZZLE_HEIGHT - (NOZZLE_HEIGHT / 8 * 2)) / 2=10 1/2"; (NOZZLE_WB_OD - NOZZLE_TOP_OD) / 4=2 3/8"; -(F-((F-H)/2))/2=-11 3/4"; A=96 3/4"; A/2=48 3/8"; B=24 3/16"; B/2=12 3/32"; B/4=6 1/16"; C=54 1/4"; C/2=27 1/8"; CLASS=1"; D=43 5/16"; D-L-K-J=1"; D-M=26 1/8"; E=42 3/16"; E/2=21 3/32"; E/52*15=12 5/32"; F=27 1/2"; F/2=13 3/4"; H=25 1/2"; H/2=12 3/4"; HEIGHT=42 11/16"; J=8"; J+K+L=42 5/16"; K=15 1/8"; L=19 3/16"; M=17 3/16"; M-(2*(D-L-K-J))=15 3/16"; N=6 11/32"; N+(H/2)=19 3/32"; NOZZLE_BOTTOM_ID=12 13/16"; NOZZLE_BOTTOM_RAD=6 13/32"; NOZZLE_BOTTOM_RAD-3*2=13/32"; NOZZLE_HEIGHT=28"; NOZZLE_HEIGHT/7*2=7"; NOZZLE_SIZE=9"; NOZZLE_TOP_OD=13 1/2"; NOZZLE_TOP_RAD=6 3/4"; NOZZLE_WB/4=4 19/32"; NOZZLE_WB_OD=23"; NOZZLE_WB_RAD=11 1/2"; NOZZLE_WB_RAD-2"=9 1/2"; P=60"; R=24 1/4"; R*1.1=26 11/16"; R+((B/2)+1.5")=37 27/32"; R-((B/2)+1.5")=10 21/32"; TRANSITION=9 1/16"; TRANSITION/2=4 17/32"; Type Comments=Vari-Plume Laboratory Exhaust Centrifugal Airfoil Class 1 Arr 10
- 195_CAVP-12L_CLASS_1: ((M - (2 * (D - L - K - J))) / 2) + (TRANSITION / 2)=13 5/8"; (B/2)+1.5"=13 19/32"; (B/2)-.125"=11 31/32"; (D-J-K-L)*2=2"; (F-((F-H)/2))/2=11 3/4"; (M - (2 * (D - L - K - J)))/2=7 19/32"; (NOZZLE_HEIGHT - (NOZZLE_HEIGHT / 8 * 2)) / 2=12"; (NOZZLE_WB_OD - NOZZLE_TOP_OD) / 4=2 1/8"; -(F-((F-H)/2))/2=-11 3/4"; A=96 3/4"; A/2=48 3/8"; B=24 3/16"; B/2=12 3/32"; B/4=6 1/16"; C=54 1/4"; C/2=27 1/8"; CLASS=1"; D=43 5/16"; D-L-K-J=1"; D-M=26 1/8"; E=42 3/16"; E/2=21 3/32"; E/52*15=12 5/32"; F=27 1/2"; F/2=13 3/4"; H=25 1/2"; H/2=12 3/4"; HEIGHT=42 11/16"; J=8"; J+K+L=42 5/16"; K=15 1/8"; L=19 3/16"; M=17 3/16"; M-(2*(D-L-K-J))=15 3/16"; N=6 11/32"; N+(H/2)=19 3/32"; NOZZLE_BOTTOM_ID=17 1/16"; NOZZLE_BOTTOM_RAD=8 17/32"; NOZZLE_BOTTOM_RAD-3*2=2 17/32"; NOZZLE_HEIGHT=32"; NOZZLE_HEIGHT/7*2=8"; NOZZLE_SIZE=12"; NOZZLE_TOP_OD=19 1/2"; NOZZLE_TOP_RAD=9 3/4"; NOZZLE_WB/4=5 19/32"; NOZZLE_WB_OD=28"; NOZZLE_WB_RAD=14"; NOZZLE_WB_RAD-2"=12"; P=60"; R=24 1/4"; R*1.1=26 11/16"; R+((B/2)+1.5")=37 27/32"; R-((B/2)+1.5")=10 21/32"; TRANSITION=12 1/16"; TRANSITION/2=6 1/32"; Type Comments=Vari-Plume Laboratory Exhaust Centrifugal Airfoil Class 1 Arr 10
- 195_CAVP-12H_CLASS_1: ((M - (2 * (D - L - K - J))) / 2) + (TRANSITION / 2)=13 5/8"; (B/2)+1.5"=13 19/32"; (B/2)-.125"=11 31/32"; (D-J-K-L)*2=2"; (F-((F-H)/2))/2=11 3/4"; (M - (2 * (D - L - K - J)))/2=7 19/32"; (NOZZLE_HEIGHT - (NOZZLE_HEIGHT / 8 * 2)) / 2=12"; (NOZZLE_WB_OD - NOZZLE_TOP_OD) / 4=2 1/8"; -(F-((F-H)/2))/2=-11 3/4"; A=96 3/4"; A/2=48 3/8"; B=24 3/16"; B/2=12 3/32"; B/4=6 1/16"; C=54 1/4"; C/2=27 1/8"; CLASS=1"; D=43 5/16"; D-L-K-J=1"; D-M=26 1/8"; E=42 3/16"; E/2=21 3/32"; E/52*15=12 5/32"; F=27 1/2"; F/2=13 3/4"; H=25 1/2"; H/2=12 3/4"; HEIGHT=42 11/16"; J=8"; J+K+L=42 5/16"; K=15 1/8"; L=19 3/16"; M=17 3/16"; M-(2*(D-L-K-J))=15 3/16"; N=6 11/32"; N+(H/2)=19 3/32"; NOZZLE_BOTTOM_ID=17 1/16"; NOZZLE_BOTTOM_RAD=8 17/32"; NOZZLE_BOTTOM_RAD-3*2=2 17/32"; NOZZLE_HEIGHT=32"; NOZZLE_HEIGHT/7*2=8"; NOZZLE_SIZE=12"; NOZZLE_TOP_OD=19 1/2"; NOZZLE_TOP_RAD=9 3/4"; NOZZLE_WB/4=5 19/32"; NOZZLE_WB_OD=28"; NOZZLE_WB_RAD=14"; NOZZLE_WB_RAD-2"=12"; P=60"; R=24 1/4"; R*1.1=26 11/16"; R+((B/2)+1.5")=37 27/32"; R-((B/2)+1.5")=10 21/32"; TRANSITION=12 1/16"; TRANSITION/2=6 1/32"; Type Comments=Vari-Plume Laboratory Exhaust Centrifugal Airfoil Class 1 Arr 10
- 195_CAVP-15L_CLASS_1: ((M - (2 * (D - L - K - J))) / 2) + (TRANSITION / 2)=15 5/32"; (B/2)+1.5"=13 19/32"; (B/2)-.125"=11 31/32"; (D-J-K-L)*2=2"; (F-((F-H)/2))/2=11 3/4"; (M - (2 * (D - L - K - J)))/2=7 19/32"; (NOZZLE_HEIGHT - (NOZZLE_HEIGHT / 8 * 2)) / 2=16 1/8"; (NOZZLE_WB_OD - NOZZLE_TOP_OD) / 4=3 1/4"; -(F-((F-H)/2))/2=-11 3/4"; A=96 3/4"; A/2=48 3/8"; B=24 3/16"; B/2=12 3/32"; B/4=6 1/16"; C=54 1/4"; C/2=27 1/8"; CLASS=1"; D=43 5/16"; D-L-K-J=1"; D-M=26 1/8"; E=42 3/16"; E/2=21 3/32"; E/52*15=12 5/32"; F=27 1/2"; F/2=13 3/4"; H=25 1/2"; H/2=12 3/4"; HEIGHT=42 11/16"; J=8"; J+K+L=42 5/16"; K=15 1/8"; L=19 3/16"; M=17 3/16"; M-(2*(D-L-K-J))=15 3/16"; N=6 11/32"; N+(H/2)=19 3/32"; NOZZLE_BOTTOM_ID=21 3/8"; NOZZLE_BOTTOM_RAD=10 11/16"; NOZZLE_BOTTOM_RAD-3*2=4 11/16"; NOZZLE_HEIGHT=43"; NOZZLE_HEIGHT/7*2=10 3/4"; NOZZLE_SIZE=15"; NOZZLE_TOP_OD=23"; NOZZLE_TOP_RAD=11 1/2"; NOZZLE_WB/4=7 3/16"; NOZZLE_WB_OD=36"; NOZZLE_WB_RAD=18"; NOZZLE_WB_RAD-2"=16"; P=60"; R=24 1/4"; R*1.1=26 11/16"; R+((B/2)+1.5")=37 27/32"; R-((B/2)+1.5")=10 21/32"; TRANSITION=15 1/8"; TRANSITION/2=7 9/16"; Type Comments=Vari-Plume Laboratory Exhaust Centrifugal Airfoil Class 1 Arr 10
- 195_CAVP-15H_CLASS_1: ((M - (2 * (D - L - K - J))) / 2) + (TRANSITION / 2)=15 5/32"; (B/2)+1.5"=13 19/32"; (B/2)-.125"=11 31/32"; (D-J-K-L)*2=2"; (F-((F-H)/2))/2=11 3/4"; (M - (2 * (D - L - K - J)))/2=7 19/32"; (NOZZLE_HEIGHT - (NOZZLE_HEIGHT / 8 * 2)) / 2=16 1/8"; (NOZZLE_WB_OD - NOZZLE_TOP_OD) / 4=3 1/4"; -(F-((F-H)/2))/2=-11 3/4"; A=96 3/4"; A/2=48 3/8"; B=24 3/16"; B/2=12 3/32"; B/4=6 1/16"; C=54 1/4"; C/2=27 1/8"; CLASS=1"; D=43 5/16"; D-L-K-J=1"; D-M=26 1/8"; E=42 3/16"; E/2=21 3/32"; E/52*15=12 5/32"; F=27 1/2"; F/2=13 3/4"; H=25 1/2"; H/2=12 3/4"; HEIGHT=42 11/16"; J=8"; J+K+L=42 5/16"; K=15 1/8"; L=19 3/16"; M=17 3/16"; M-(2*(D-L-K-J))=15 3/16"; N=6 11/32"; N+(H/2)=19 3/32"; NOZZLE_BOTTOM_ID=21 3/8"; NOZZLE_BOTTOM_RAD=10 11/16"; NOZZLE_BOTTOM_RAD-3*2=4 11/16"; NOZZLE_HEIGHT=43"; NOZZLE_HEIGHT/7*2=10 3/4"; NOZZLE_SIZE=15"; NOZZLE_TOP_OD=23"; NOZZLE_TOP_RAD=11 1/2"; NOZZLE_WB/4=7 3/16"; NOZZLE_WB_OD=36"; NOZZLE_WB_RAD=18"; NOZZLE_WB_RAD-2"=16"; P=60"; R=24 1/4"; R*1.1=26 11/16"; R+((B/2)+1.5")=37 27/32"; R-((B/2)+1.5")=10 21/32"; TRANSITION=15 1/8"; TRANSITION/2=7 9/16"; Type Comments=Vari-Plume Laboratory Exhaust Centrifugal Airfoil Class 1 Arr 10
- 195_CAVP-9L_CLASS_2: ((M - (2 * (D - L - K - J))) / 2) + (TRANSITION / 2)=12 1/8"; (B/2)+1.5"=13 19/32"; (B/2)-.125"=11 31/32"; (D-J-K-L)*2=2"; (F-((F-H)/2))/2=11 3/4"; (M - (2 * (D - L - K - J)))/2=7 19/32"; (NOZZLE_HEIGHT - (NOZZLE_HEIGHT / 8 * 2)) / 2=10 1/2"; (NOZZLE_WB_OD - NOZZLE_TOP_OD) / 4=2 3/8"; -(F-((F-H)/2))/2=-11 3/4"; A=96 3/4"; A/2=48 3/8"; B=24 3/16"; B/2=12 3/32"; B/4=6 1/16"; C=54 1/4"; C/2=27 1/8"; CLASS=2"; D=47 5/16"; D-L-K-J=1"; D-M=30 1/8"; E=42 3/16"; E/2=21 3/32"; E/52*15=12 5/32"; F=27 1/2"; F/2=13 3/4"; H=25 1/2"; H/2=12 3/4"; HEIGHT=42 11/16"; J=7 3/4"; J+K+L=46 5/16"; K=19 3/8"; L=19 3/16"; M=17 3/16"; M-(2*(D-L-K-J))=15 3/16"; N=6 1/2"; N+(H/2)=19 1/4"; NOZZLE_BOTTOM_ID=12 13/16"; NOZZLE_BOTTOM_RAD=6 13/32"; NOZZLE_BOTTOM_RAD-3*2=13/32"; NOZZLE_HEIGHT=28"; NOZZLE_HEIGHT/7*2=7"; NOZZLE_SIZE=9"; NOZZLE_TOP_OD=13 1/2"; NOZZLE_TOP_RAD=6 3/4"; NOZZLE_WB/4=4 19/32"; NOZZLE_WB_OD=23"; NOZZLE_WB_RAD=11 1/2"; NOZZLE_WB_RAD-2"=9 1/2"; P=60"; R=24 1/4"; R*1.1=26 11/16"; R+((B/2)+1.5")=37 27/32"; R-((B/2)+1.5")=10 21/32"; TRANSITION=9 1/16"; TRANSITION/2=4 17/32"; Type Comments=Vari-Plume Laboratory Exhaust Centrifugal Airfoil Class 2 Arr 10
- 195_CAVP-9H_CLASS_2: ((M - (2 * (D - L - K - J))) / 2) + (TRANSITION / 2)=12 1/8"; (B/2)+1.5"=13 19/32"; (B/2)-.125"=11 31/32"; (D-J-K-L)*2=2"; (F-((F-H)/2))/2=11 3/4"; (M - (2 * (D - L - K - J)))/2=7 19/32"; (NOZZLE_HEIGHT - (NOZZLE_HEIGHT / 8 * 2)) / 2=10 1/2"; (NOZZLE_WB_OD - NOZZLE_TOP_OD) / 4=2 3/8"; -(F-((F-H)/2))/2=-11 3/4"; A=96 3/4"; A/2=48 3/8"; B=24 3/16"; B/2=12 3/32"; B/4=6 1/16"; C=54 1/4"; C/2=27 1/8"; CLASS=2"; D=47 5/16"; D-L-K-J=1"; D-M=30 1/8"; E=42 3/16"; E/2=21 3/32"; E/52*15=12 5/32"; F=27 1/2"; F/2=13 3/4"; H=25 1/2"; H/2=12 3/4"; HEIGHT=42 11/16"; J=7 3/4"; J+K+L=46 5/16"; K=19 3/8"; L=19 3/16"; M=17 3/16"; M-(2*(D-L-K-J))=15 3/16"; N=6 1/2"; N+(H/2)=19 1/4"; NOZZLE_BOTTOM_ID=12 13/16"; NOZZLE_BOTTOM_RAD=6 13/32"; NOZZLE_BOTTOM_RAD-3*2=13/32"; NOZZLE_HEIGHT=28"; NOZZLE_HEIGHT/7*2=7"; NOZZLE_SIZE=9"; NOZZLE_TOP_OD=13 1/2"; NOZZLE_TOP_RAD=6 3/4"; NOZZLE_WB/4=4 19/32"; NOZZLE_WB_OD=23"; NOZZLE_WB_RAD=11 1/2"; NOZZLE_WB_RAD-2"=9 1/2"; P=60"; R=24 1/4"; R*1.1=26 11/16"; R+((B/2)+1.5")=37 27/32"; R-((B/2)+1.5")=10 21/32"; TRANSITION=9 1/16"; TRANSITION/2=4 17/32"; Type Comments=Vari-Plume Laboratory Exhaust Centrifugal Airfoil Class 2 Arr 10
- 195_CAVP-12L_CLASS_2: ((M - (2 * (D - L - K - J))) / 2) + (TRANSITION / 2)=13 5/8"; (B/2)+1.5"=13 19/32"; (B/2)-.125"=11 31/32"; (D-J-K-L)*2=2"; (F-((F-H)/2))/2=11 3/4"; (M - (2 * (D - L - K - J)))/2=7 19/32"; (NOZZLE_HEIGHT - (NOZZLE_HEIGHT / 8 * 2)) / 2=12"; (NOZZLE_WB_OD - NOZZLE_TOP_OD) / 4=2 1/8"; -(F-((F-H)/2))/2=-11 3/4"; A=96 3/4"; A/2=48 3/8"; B=24 3/16"; B/2=12 3/32"; B/4=6 1/16"; C=54 1/4"; C/2=27 1/8"; CLASS=2"; D=47 5/16"; D-L-K-J=1"; D-M=30 1/8"; E=42 3/16"; E/2=21 3/32"; E/52*15=12 5/32"; F=27 1/2"; F/2=13 3/4"; H=25 1/2"; H/2=12 3/4"; HEIGHT=42 11/16"; J=7 3/4"; J+K+L=46 5/16"; K=19 3/8"; L=19 3/16"; M=17 3/16"; M-(2*(D-L-K-J))=15 3/16"; N=6 1/2"; N+(H/2)=19 1/4"; NOZZLE_BOTTOM_ID=17 1/16"; NOZZLE_BOTTOM_RAD=8 17/32"; NOZZLE_BOTTOM_RAD-3*2=2 17/32"; NOZZLE_HEIGHT=32"; NOZZLE_HEIGHT/7*2=8"; NOZZLE_SIZE=12"; NOZZLE_TOP_OD=19 1/2"; NOZZLE_TOP_RAD=9 3/4"; NOZZLE_WB/4=5 19/32"; NOZZLE_WB_OD=28"; NOZZLE_WB_RAD=14"; NOZZLE_WB_RAD-2"=12"; P=60"; R=24 1/4"; R*1.1=26 11/16"; R+((B/2)+1.5")=37 27/32"; R-((B/2)+1.5")=10 21/32"; TRANSITION=12 1/16"; TRANSITION/2=6 1/32"; Type Comments=Vari-Plume Laboratory Exhaust Centrifugal Airfoil Class 2 Arr 10
- 195_CAVP-12H_CLASS_2: ((M - (2 * (D - L - K - J))) / 2) + (TRANSITION / 2)=13 5/8"; (B/2)+1.5"=13 19/32"; (B/2)-.125"=11 31/32"; (D-J-K-L)*2=2"; (F-((F-H)/2))/2=11 3/4"; (M - (2 * (D - L - K - J)))/2=7 19/32"; (NOZZLE_HEIGHT - (NOZZLE_HEIGHT / 8 * 2)) / 2=12"; (NOZZLE_WB_OD - NOZZLE_TOP_OD) / 4=2 1/8"; -(F-((F-H)/2))/2=-11 3/4"; A=96 3/4"; A/2=48 3/8"; B=24 3/16"; B/2=12 3/32"; B/4=6 1/16"; C=54 1/4"; C/2=27 1/8"; CLASS=2"; D=47 5/16"; D-L-K-J=1"; D-M=30 1/8"; E=42 3/16"; E/2=21 3/32"; E/52*15=12 5/32"; F=27 1/2"; F/2=13 3/4"; H=25 1/2"; H/2=12 3/4"; HEIGHT=42 11/16"; J=7 3/4"; J+K+L=46 5/16"; K=19 3/8"; L=19 3/16"; M=17 3/16"; M-(2*(D-L-K-J))=15 3/16"; N=6 1/2"; N+(H/2)=19 1/4"; NOZZLE_BOTTOM_ID=17 1/16"; NOZZLE_BOTTOM_RAD=8 17/32"; NOZZLE_BOTTOM_RAD-3*2=2 17/32"; NOZZLE_HEIGHT=32"; NOZZLE_HEIGHT/7*2=8"; NOZZLE_SIZE=12"; NOZZLE_TOP_OD=19 1/2"; NOZZLE_TOP_RAD=9 3/4"; NOZZLE_WB/4=5 19/32"; NOZZLE_WB_OD=28"; NOZZLE_WB_RAD=14"; NOZZLE_WB_RAD-2"=12"; P=60"; R=24 1/4"; R*1.1=26 11/16"; R+((B/2)+1.5")=37 27/32"; R-((B/2)+1.5")=10 21/32"; TRANSITION=12 1/16"; TRANSITION/2=6 1/32"; Type Comments=Vari-Plume Laboratory Exhaust Centrifugal Airfoil Class 2 Arr 10
- 195_CAVP-15L_CLASS_2: ((M - (2 * (D - L - K - J))) / 2) + (TRANSITION / 2)=15 5/32"; (B/2)+1.5"=13 19/32"; (B/2)-.125"=11 31/32"; (D-J-K-L)*2=2"; (F-((F-H)/2))/2=11 3/4"; (M - (2 * (D - L - K - J)))/2=7 19/32"; (NOZZLE_HEIGHT - (NOZZLE_HEIGHT / 8 * 2)) / 2=16 1/8"; (NOZZLE_WB_OD - NOZZLE_TOP_OD) / 4=3 1/4"; -(F-((F-H)/2))/2=-11 3/4"; A=96 3/4"; A/2=48 3/8"; B=24 3/16"; B/2=12 3/32"; B/4=6 1/16"; C=54 1/4"; C/2=27 1/8"; CLASS=2"; D=47 5/16"; D-L-K-J=1"; D-M=30 1/8"; E=42 3/16"; E/2=21 3/32"; E/52*15=12 5/32"; F=27 1/2"; F/2=13 3/4"; H=25 1/2"; H/2=12 3/4"; HEIGHT=42 11/16"; J=7 3/4"; J+K+L=46 5/16"; K=19 3/8"; L=19 3/16"; M=17 3/16"; M-(2*(D-L-K-J))=15 3/16"; N=6 1/2"; N+(H/2)=19 1/4"; NOZZLE_BOTTOM_ID=21 3/8"; NOZZLE_BOTTOM_RAD=10 11/16"; NOZZLE_BOTTOM_RAD-3*2=4 11/16"; NOZZLE_HEIGHT=43"; NOZZLE_HEIGHT/7*2=10 3/4"; NOZZLE_SIZE=15"; NOZZLE_TOP_OD=23"; NOZZLE_TOP_RAD=11 1/2"; NOZZLE_WB/4=7 3/16"; NOZZLE_WB_OD=36"; NOZZLE_WB_RAD=18"; NOZZLE_WB_RAD-2"=16"; P=60"; R=24 1/4"; R*1.1=26 11/16"; R+((B/2)+1.5")=37 27/32"; R-((B/2)+1.5")=10 21/32"; TRANSITION=15 1/8"; TRANSITION/2=7 9/16"; Type Comments=Vari-Plume Laboratory Exhaust Centrifugal Airfoil Class 2 Arr 10
- 195_CAVP-15H_CLASS_2: ((M - (2 * (D - L - K - J))) / 2) + (TRANSITION / 2)=15 5/32"; (B/2)+1.5"=13 19/32"; (B/2)-.125"=11 31/32"; (D-J-K-L)*2=2"; (F-((F-H)/2))/2=11 3/4"; (M - (2 * (D - L - K - J)))/2=7 19/32"; (NOZZLE_HEIGHT - (NOZZLE_HEIGHT / 8 * 2)) / 2=16 1/8"; (NOZZLE_WB_OD - NOZZLE_TOP_OD) / 4=3 1/4"; -(F-((F-H)/2))/2=-11 3/4"; A=96 3/4"; A/2=48 3/8"; B=24 3/16"; B/2=12 3/32"; B/4=6 1/16"; C=54 1/4"; C/2=27 1/8"; CLASS=2"; D=47 5/16"; D-L-K-J=1"; D-M=30 1/8"; E=42 3/16"; E/2=21 3/32"; E/52*15=12 5/32"; F=27 1/2"; F/2=13 3/4"; H=25 1/2"; H/2=12 3/4"; HEIGHT=42 11/16"; J=7 3/4"; J+K+L=46 5/16"; K=19 3/8"; L=19 3/16"; M=17 3/16"; M-(2*(D-L-K-J))=15 3/16"; N=6 1/2"; N+(H/2)=19 1/4"; NOZZLE_BOTTOM_ID=21 3/8"; NOZZLE_BOTTOM_RAD=10 11/16"; NOZZLE_BOTTOM_RAD-3*2=4 11/16"; NOZZLE_HEIGHT=43"; NOZZLE_HEIGHT/7*2=10 3/4"; NOZZLE_SIZE=15"; NOZZLE_TOP_OD=23"; NOZZLE_TOP_RAD=11 1/2"; NOZZLE_WB/4=7 3/16"; NOZZLE_WB_OD=36"; NOZZLE_WB_RAD=18"; NOZZLE_WB_RAD-2"=16"; P=60"; R=24 1/4"; R*1.1=26 11/16"; R+((B/2)+1.5")=37 27/32"; R-((B/2)+1.5")=10 21/32"; TRANSITION=15 1/8"; TRANSITION/2=7 9/16"; Type Comments=Vari-Plume Laboratory Exhaust Centrifugal Airfoil Class 2 Arr 10
- 210_CAVP-12H_CLASS_1: ((M - (2 * (D - L - K - J))) / 2) + (TRANSITION / 2)=14 3/16"; (B/2)+1.5"=14 15/32"; (B/2)-.125"=12 27/32"; (D-J-K-L)*2=2"; (F-((F-H)/2))/2=12 1/16"; (M - (2 * (D - L - K - J)))/2=8 5/32"; (NOZZLE_HEIGHT - (NOZZLE_HEIGHT / 8 * 2)) / 2=12"; (NOZZLE_WB_OD - NOZZLE_TOP_OD) / 4=2 1/8"; -(F-((F-H)/2))/2=-12 1/16"; A=99 1/4"; A/2=49 5/8"; B=25 15/16"; B/2=12 31/32"; B/4=6 1/2"; C=56 3/4"; C/2=28 3/8"; CLASS=1"; D=44 15/16"; D-L-K-J=1"; D-M=26 5/8"; E=45 1/4"; E/2=22 5/8"; E/52*15=13 1/16"; F=28 1/8"; F/2=14 1/16"; H=26 1/8"; H/2=13 1/16"; HEIGHT=44"; J=8 1/2"; J+K+L=43 15/16"; K=15 1/8"; L=20 5/16"; M=18 5/16"; M-(2*(D-L-K-J))=16 5/16"; N=7 9/16"; N+(H/2)=20 5/8"; NOZZLE_BOTTOM_ID=17 1/16"; NOZZLE_BOTTOM_RAD=8 17/32"; NOZZLE_BOTTOM_RAD-3*2=2 17/32"; NOZZLE_HEIGHT=32"; NOZZLE_HEIGHT/7*2=8"; NOZZLE_SIZE=12"; NOZZLE_TOP_OD=19 1/2"; NOZZLE_TOP_RAD=9 3/4"; NOZZLE_WB/4=5 19/32"; NOZZLE_WB_OD=28"; NOZZLE_WB_RAD=14"; NOZZLE_WB_RAD-2"=12"; P=60"; R=24 1/4"; R*1.1=26 11/16"; R+((B/2)+1.5")=38 23/32"; R-((B/2)+1.5")=9 25/32"; TRANSITION=12 1/16"; TRANSITION/2=6 1/32"; Type Comments=Vari-Plume Laboratory Exhaust Centrifugal Airfoil Class 1 Arr 10
- 210_CAVP-12L_CLASS_1: ((M - (2 * (D - L - K - J))) / 2) + (TRANSITION / 2)=14 3/16"; (B/2)+1.5"=14 15/32"; (B/2)-.125"=12 27/32"; (D-J-K-L)*2=2"; (F-((F-H)/2))/2=12 1/16"; (M - (2 * (D - L - K - J)))/2=8 5/32"; (NOZZLE_HEIGHT - (NOZZLE_HEIGHT / 8 * 2)) / 2=12"; (NOZZLE_WB_OD - NOZZLE_TOP_OD) / 4=2 1/8"; -(F-((F-H)/2))/2=-12 1/16"; A=99 1/4"; A/2=49 5/8"; B=25 15/16"; B/2=12 31/32"; B/4=6 1/2"; C=56 3/4"; C/2=28 3/8"; CLASS=1"; D=44 15/16"; D-L-K-J=1"; D-M=26 5/8"; E=45 1/4"; E/2=22 5/8"; E/52*15=13 1/16"; F=28 1/8"; F/2=14 1/16"; H=26 1/8"; H/2=13 1/16"; HEIGHT=44"; J=8 1/2"; J+K+L=43 15/16"; K=15 1/8"; L=20 5/16"; M=18 5/16"; M-(2*(D-L-K-J))=16 5/16"; N=7 9/16"; N+(H/2)=20 5/8"; NOZZLE_BOTTOM_ID=17 1/16"; NOZZLE_BOTTOM_RAD=8 17/32"; NOZZLE_BOTTOM_RAD-3*2=2 17/32"; NOZZLE_HEIGHT=32"; NOZZLE_HEIGHT/7*2=8"; NOZZLE_SIZE=12"; NOZZLE_TOP_OD=19 1/2"; NOZZLE_TOP_RAD=9 3/4"; NOZZLE_WB/4=5 19/32"; NOZZLE_WB_OD=28"; NOZZLE_WB_RAD=14"; NOZZLE_WB_RAD-2"=12"; P=60"; R=24 1/4"; R*1.1=26 11/16"; R+((B/2)+1.5")=38 23/32"; R-((B/2)+1.5")=9 25/32"; TRANSITION=12 1/16"; TRANSITION/2=6 1/32"; Type Comments=Vari-Plume Laboratory Exhaust Centrifugal Airfoil Class 1 Arr 10
- 210_CAVP-15H_CLASS_1: ((M - (2 * (D - L - K - J))) / 2) + (TRANSITION / 2)=15 23/32"; (B/2)+1.5"=14 15/32"; (B/2)-.125"=12 27/32"; (D-J-K-L)*2=2"; (F-((F-H)/2))/2=12 1/16"; (M - (2 * (D - L - K - J)))/2=8 5/32"; (NOZZLE_HEIGHT - (NOZZLE_HEIGHT / 8 * 2)) / 2=16 1/8"; (NOZZLE_WB_OD - NOZZLE_TOP_OD) / 4=3 1/4"; -(F-((F-H)/2))/2=-12 1/16"; A=99 1/4"; A/2=49 5/8"; B=25 15/16"; B/2=12 31/32"; B/4=6 1/2"; C=56 3/4"; C/2=28 3/8"; CLASS=1"; D=44 15/16"; D-L-K-J=1"; D-M=26 5/8"; E=45 1/4"; E/2=22 5/8"; E/52*15=13 1/16"; F=28 1/8"; F/2=14 1/16"; H=26 1/8"; H/2=13 1/16"; HEIGHT=44"; J=8 1/2"; J+K+L=43 15/16"; K=15 1/8"; L=20 5/16"; M=18 5/16"; M-(2*(D-L-K-J))=16 5/16"; N=7 9/16"; N+(H/2)=20 5/8"; NOZZLE_BOTTOM_ID=21 3/8"; NOZZLE_BOTTOM_RAD=10 11/16"; NOZZLE_BOTTOM_RAD-3*2=4 11/16"; NOZZLE_HEIGHT=43"; NOZZLE_HEIGHT/7*2=10 3/4"; NOZZLE_SIZE=15"; NOZZLE_TOP_OD=23"; NOZZLE_TOP_RAD=11 1/2"; NOZZLE_WB/4=7 3/16"; NOZZLE_WB_OD=36"; NOZZLE_WB_RAD=18"; NOZZLE_WB_RAD-2"=16"; P=60"; R=24 1/4"; R*1.1=26 11/16"; R+((B/2)+1.5")=38 23/32"; R-((B/2)+1.5")=9 25/32"; TRANSITION=15 1/8"; TRANSITION/2=7 9/16"; Type Comments=Vari-Plume Laboratory Exhaust Centrifugal Airfoil Class 1 Arr 10
- 210_CAVP-15L_CLASS_1: ((M - (2 * (D - L - K - J))) / 2) + (TRANSITION / 2)=15 23/32"; (B/2)+1.5"=14 15/32"; (B/2)-.125"=12 27/32"; (D-J-K-L)*2=2"; (F-((F-H)/2))/2=12 1/16"; (M - (2 * (D - L - K - J)))/2=8 5/32"; (NOZZLE_HEIGHT - (NOZZLE_HEIGHT / 8 * 2)) / 2=16 1/8"; (NOZZLE_WB_OD - NOZZLE_TOP_OD) / 4=3 1/4"; -(F-((F-H)/2))/2=-12 1/16"; A=99 1/4"; A/2=49 5/8"; B=25 15/16"; B/2=12 31/32"; B/4=6 1/2"; C=56 3/4"; C/2=28 3/8"; CLASS=1"; D=44 15/16"; D-L-K-J=1"; D-M=26 5/8"; E=45 1/4"; E/2=22 5/8"; E/52*15=13 1/16"; F=28 1/8"; F/2=14 1/16"; H=26 1/8"; H/2=13 1/16"; HEIGHT=44"; J=8 1/2"; J+K+L=43 15/16"; K=15 1/8"; L=20 5/16"; M=18 5/16"; M-(2*(D-L-K-J))=16 5/16"; N=7 9/16"; N+(H/2)=20 5/8"; NOZZLE_BOTTOM_ID=21 3/8"; NOZZLE_BOTTOM_RAD=10 11/16"; NOZZLE_BOTTOM_RAD-3*2=4 11/16"; NOZZLE_HEIGHT=43"; NOZZLE_HEIGHT/7*2=10 3/4"; NOZZLE_SIZE=15"; NOZZLE_TOP_OD=23"; NOZZLE_TOP_RAD=11 1/2"; NOZZLE_WB/4=7 3/16"; NOZZLE_WB_OD=36"; NOZZLE_WB_RAD=18"; NOZZLE_WB_RAD-2"=16"; P=60"; R=24 1/4"; R*1.1=26 11/16"; R+((B/2)+1.5")=38 23/32"; R-((B/2)+1.5")=9 25/32"; TRANSITION=15 1/8"; TRANSITION/2=7 9/16"; Type Comments=Vari-Plume Laboratory Exhaust Centrifugal Airfoil Class 1 Arr 10
- 210_CAVP-15L_CLASS_2: ((M - (2 * (D - L - K - J))) / 2) + (TRANSITION / 2)=15 23/32"; (B/2)+1.5"=14 15/32"; (B/2)-.125"=12 27/32"; (D-J-K-L)*2=2"; (F-((F-H)/2))/2=12 1/16"; (M - (2 * (D - L - K - J)))/2=8 5/32"; (NOZZLE_HEIGHT - (NOZZLE_HEIGHT / 8 * 2)) / 2=16 1/8"; (NOZZLE_WB_OD - NOZZLE_TOP_OD) / 4=3 1/4"; -(F-((F-H)/2))/2=-12 1/16"; A=99 1/4"; A/2=49 5/8"; B=25 15/16"; B/2=12 31/32"; B/4=6 1/2"; C=56 3/4"; C/2=28 3/8"; CLASS=2"; D=44 15/16"; D-L-K-J=1"; D-M=26 5/8"; E=45 1/4"; E/2=22 5/8"; E/52*15=13 1/16"; F=28 1/8"; F/2=14 1/16"; H=26 1/8"; H/2=13 1/16"; HEIGHT=44"; J=8 1/2"; J+K+L=43 15/16"; K=15 1/8"; L=20 5/16"; M=18 5/16"; M-(2*(D-L-K-J))=16 5/16"; N=7 9/16"; N+(H/2)=20 5/8"; NOZZLE_BOTTOM_ID=21 3/8"; NOZZLE_BOTTOM_RAD=10 11/16"; NOZZLE_BOTTOM_RAD-3*2=4 11/16"; NOZZLE_HEIGHT=43"; NOZZLE_HEIGHT/7*2=10 3/4"; NOZZLE_SIZE=15"; NOZZLE_TOP_OD=23"; NOZZLE_TOP_RAD=11 1/2"; NOZZLE_WB/4=7 3/16"; NOZZLE_WB_OD=36"; NOZZLE_WB_RAD=18"; NOZZLE_WB_RAD-2"=16"; P=60"; R=24 1/4"; R*1.1=26 11/16"; R+((B/2)+1.5")=38 23/32"; R-((B/2)+1.5")=9 25/32"; TRANSITION=15 1/8"; TRANSITION/2=7 9/16"; Type Comments=Vari-Plume Laboratory Exhaust Centrifugal Airfoil Class 2 Arr 10
- 210_CAVP-15H_CLASS_2: ((M - (2 * (D - L - K - J))) / 2) + (TRANSITION / 2)=15 23/32"; (B/2)+1.5"=14 15/32"; (B/2)-.125"=12 27/32"; (D-J-K-L)*2=2"; (F-((F-H)/2))/2=12 1/16"; (M - (2 * (D - L - K - J)))/2=8 5/32"; (NOZZLE_HEIGHT - (NOZZLE_HEIGHT / 8 * 2)) / 2=16 1/8"; (NOZZLE_WB_OD - NOZZLE_TOP_OD) / 4=3 1/4"; -(F-((F-H)/2))/2=-12 1/16"; A=99 1/4"; A/2=49 5/8"; B=25 15/16"; B/2=12 31/32"; B/4=6 1/2"; C=56 3/4"; C/2=28 3/8"; CLASS=2"; D=44 15/16"; D-L-K-J=1"; D-M=26 5/8"; E=45 1/4"; E/2=22 5/8"; E/52*15=13 1/16"; F=28 1/8"; F/2=14 1/16"; H=26 1/8"; H/2=13 1/16"; HEIGHT=44"; J=8 1/2"; J+K+L=43 15/16"; K=15 1/8"; L=20 5/16"; M=18 5/16"; M-(2*(D-L-K-J))=16 5/16"; N=7 9/16"; N+(H/2)=20 5/8"; NOZZLE_BOTTOM_ID=21 3/8"; NOZZLE_BOTTOM_RAD=10 11/16"; NOZZLE_BOTTOM_RAD-3*2=4 11/16"; NOZZLE_HEIGHT=43"; NOZZLE_HEIGHT/7*2=10 3/4"; NOZZLE_SIZE=15"; NOZZLE_TOP_OD=23"; NOZZLE_TOP_RAD=11 1/2"; NOZZLE_WB/4=7 3/16"; NOZZLE_WB_OD=36"; NOZZLE_WB_RAD=18"; NOZZLE_WB_RAD-2"=16"; P=60"; R=24 1/4"; R*1.1=26 11/16"; R+((B/2)+1.5")=38 23/32"; R-((B/2)+1.5")=9 25/32"; TRANSITION=15 1/8"; TRANSITION/2=7 9/16"; Type Comments=Vari-Plume Laboratory Exhaust Centrifugal Airfoil Class 2 Arr 10
- 210_CAVP-12L_CLASS_2: ((M - (2 * (D - L - K - J))) / 2) + (TRANSITION / 2)=14 3/16"; (B/2)+1.5"=14 15/32"; (B/2)-.125"=12 27/32"; (D-J-K-L)*2=2"; (F-((F-H)/2))/2=12 1/16"; (M - (2 * (D - L - K - J)))/2=8 5/32"; (NOZZLE_HEIGHT - (NOZZLE_HEIGHT / 8 * 2)) / 2=12"; (NOZZLE_WB_OD - NOZZLE_TOP_OD) / 4=2 1/8"; -(F-((F-H)/2))/2=-12 1/16"; A=99 1/4"; A/2=49 5/8"; B=25 15/16"; B/2=12 31/32"; B/4=6 1/2"; C=56 3/4"; C/2=28 3/8"; CLASS=2"; D=44 15/16"; D-L-K-J=1"; D-M=26 5/8"; E=45 1/4"; E/2=22 5/8"; E/52*15=13 1/16"; F=28 1/8"; F/2=14 1/16"; H=26 1/8"; H/2=13 1/16"; HEIGHT=44"; J=8 1/2"; J+K+L=43 15/16"; K=15 1/8"; L=20 5/16"; M=18 5/16"; M-(2*(D-L-K-J))=16 5/16"; N=7 9/16"; N+(H/2)=20 5/8"; NOZZLE_BOTTOM_ID=17 1/16"; NOZZLE_BOTTOM_RAD=8 17/32"; NOZZLE_BOTTOM_RAD-3*2=2 17/32"; NOZZLE_HEIGHT=32"; NOZZLE_HEIGHT/7*2=8"; NOZZLE_SIZE=12"; NOZZLE_TOP_OD=19 1/2"; NOZZLE_TOP_RAD=9 3/4"; NOZZLE_WB/4=5 19/32"; NOZZLE_WB_OD=28"; NOZZLE_WB_RAD=14"; NOZZLE_WB_RAD-2"=12"; P=60"; R=24 1/4"; R*1.1=26 11/16"; R+((B/2)+1.5")=38 23/32"; R-((B/2)+1.5")=9 25/32"; TRANSITION=12 1/16"; TRANSITION/2=6 1/32"; Type Comments=Vari-Plume Laboratory Exhaust Centrifugal Airfoil Class 2 Arr 10
- 210_CAVP-12H_CLASS_2: ((M - (2 * (D - L - K - J))) / 2) + (TRANSITION / 2)=14 3/16"; (B/2)+1.5"=14 15/32"; (B/2)-.125"=12 27/32"; (D-J-K-L)*2=2"; (F-((F-H)/2))/2=12 1/16"; (M - (2 * (D - L - K - J)))/2=8 5/32"; (NOZZLE_HEIGHT - (NOZZLE_HEIGHT / 8 * 2)) / 2=12"; (NOZZLE_WB_OD - NOZZLE_TOP_OD) / 4=2 1/8"; -(F-((F-H)/2))/2=-12 1/16"; A=99 1/4"; A/2=49 5/8"; B=25 15/16"; B/2=12 31/32"; B/4=6 1/2"; C=56 3/4"; C/2=28 3/8"; CLASS=2"; D=44 15/16"; D-L-K-J=1"; D-M=26 5/8"; E=45 1/4"; E/2=22 5/8"; E/52*15=13 1/16"; F=28 1/8"; F/2=14 1/16"; H=26 1/8"; H/2=13 1/16"; HEIGHT=44"; J=8 1/2"; J+K+L=43 15/16"; K=15 1/8"; L=20 5/16"; M=18 5/16"; M-(2*(D-L-K-J))=16 5/16"; N=7 9/16"; N+(H/2)=20 5/8"; NOZZLE_BOTTOM_ID=17 1/16"; NOZZLE_BOTTOM_RAD=8 17/32"; NOZZLE_BOTTOM_RAD-3*2=2 17/32"; NOZZLE_HEIGHT=32"; NOZZLE_HEIGHT/7*2=8"; NOZZLE_SIZE=12"; NOZZLE_TOP_OD=19 1/2"; NOZZLE_TOP_RAD=9 3/4"; NOZZLE_WB/4=5 19/32"; NOZZLE_WB_OD=28"; NOZZLE_WB_RAD=14"; NOZZLE_WB_RAD-2"=12"; P=60"; R=24 1/4"; R*1.1=26 11/16"; R+((B/2)+1.5")=38 23/32"; R-((B/2)+1.5")=9 25/32"; TRANSITION=12 1/16"; TRANSITION/2=6 1/32"; Type Comments=Vari-Plume Laboratory Exhaust Centrifugal Airfoil Class 2 Arr 10
- 225_CAVP-12H_CLASS_1: ((M - (2 * (D - L - K - J))) / 2) + (TRANSITION / 2)=14 3/4"; (B/2)+1.5"=15 7/32"; (B/2)-.125"=13 19/32"; (D-J-K-L)*2=2"; (F-((F-H)/2))/2=12 13/16"; (M - (2 * (D - L - K - J)))/2=8 23/32"; (NOZZLE_HEIGHT - (NOZZLE_HEIGHT / 8 * 2)) / 2=12"; (NOZZLE_WB_OD - NOZZLE_TOP_OD) / 4=2 1/8"; -(F-((F-H)/2))/2=-12 13/16"; A=106 11/16"; A/2=53 11/32"; B=27 7/16"; B/2=13 23/32"; B/4=6 7/8"; C=59 3/16"; C/2=29 19/32"; CLASS=1"; D=46 1/16"; D-L-K-J=1"; D-M=26 5/8"; E=48 5/16"; E/2=24 5/32"; E/52*15=13 15/16"; F=29 5/8"; F/2=14 13/16"; H=27 5/8"; H/2=13 13/16"; HEIGHT=45 11/32"; J=8 1/2"; J+K+L=45 1/16"; K=15 1/8"; L=21 7/16"; M=19 7/16"; M-(2*(D-L-K-J))=17 7/16"; N=8 11/32"; N+(H/2)=22 5/32"; NOZZLE_BOTTOM_ID=17 1/16"; NOZZLE_BOTTOM_RAD=8 17/32"; NOZZLE_BOTTOM_RAD-3*2=2 17/32"; NOZZLE_HEIGHT=32"; NOZZLE_HEIGHT/7*2=8"; NOZZLE_SIZE=12"; NOZZLE_TOP_OD=19 1/2"; NOZZLE_TOP_RAD=9 3/4"; NOZZLE_WB/4=5 19/32"; NOZZLE_WB_OD=28"; NOZZLE_WB_RAD=14"; NOZZLE_WB_RAD-2"=12"; P=60"; R=24 1/4"; R*1.1=26 11/16"; R+((B/2)+1.5")=39 15/32"; R-((B/2)+1.5")=9 1/32"; TRANSITION=12 1/16"; TRANSITION/2=6 1/32"; Type Comments=Vari-Plume Laboratory Exhaust Centrifugal Airfoil Class 1 Arr 10
- 225_CAVP-12L_CLASS_1: ((M - (2 * (D - L - K - J))) / 2) + (TRANSITION / 2)=14 3/4"; (B/2)+1.5"=15 7/32"; (B/2)-.125"=13 19/32"; (D-J-K-L)*2=2"; (F-((F-H)/2))/2=12 13/16"; (M - (2 * (D - L - K - J)))/2=8 23/32"; (NOZZLE_HEIGHT - (NOZZLE_HEIGHT / 8 * 2)) / 2=12"; (NOZZLE_WB_OD - NOZZLE_TOP_OD) / 4=2 1/8"; -(F-((F-H)/2))/2=-12 13/16"; A=106 11/16"; A/2=53 11/32"; B=27 7/16"; B/2=13 23/32"; B/4=6 7/8"; C=59 3/16"; C/2=29 19/32"; CLASS=1"; D=46 1/16"; D-L-K-J=1"; D-M=26 5/8"; E=48 5/16"; E/2=24 5/32"; E/52*15=13 15/16"; F=29 5/8"; F/2=14 13/16"; H=27 5/8"; H/2=13 13/16"; HEIGHT=45 11/32"; J=8 1/2"; J+K+L=45 1/16"; K=15 1/8"; L=21 7/16"; M=19 7/16"; M-(2*(D-L-K-J))=17 7/16"; N=8 11/32"; N+(H/2)=22 5/32"; NOZZLE_BOTTOM_ID=17 1/16"; NOZZLE_BOTTOM_RAD=8 17/32"; NOZZLE_BOTTOM_RAD-3*2=2 17/32"; NOZZLE_HEIGHT=32"; NOZZLE_HEIGHT/7*2=8"; NOZZLE_SIZE=12"; NOZZLE_TOP_OD=19 1/2"; NOZZLE_TOP_RAD=9 3/4"; NOZZLE_WB/4=5 19/32"; NOZZLE_WB_OD=28"; NOZZLE_WB_RAD=14"; NOZZLE_WB_RAD-2"=12"; P=60"; R=24 1/4"; R*1.1=26 11/16"; R+((B/2)+1.5")=39 15/32"; R-((B/2)+1.5")=9 1/32"; TRANSITION=12 1/16"; TRANSITION/2=6 1/32"; Type Comments=Vari-Plume Laboratory Exhaust Centrifugal Airfoil Class 1 Arr 10
- 225_CAVP-15L_CLASS_1: ((M - (2 * (D - L - K - J))) / 2) + (TRANSITION / 2)=16 9/32"; (B/2)+1.5"=15 7/32"; (B/2)-.125"=13 19/32"; (D-J-K-L)*2=2"; (F-((F-H)/2))/2=12 13/16"; (M - (2 * (D - L - K - J)))/2=8 23/32"; (NOZZLE_HEIGHT - (NOZZLE_HEIGHT / 8 * 2)) / 2=16 1/8"; (NOZZLE_WB_OD - NOZZLE_TOP_OD) / 4=3 1/4"; -(F-((F-H)/2))/2=-12 13/16"; A=106 11/16"; A/2=53 11/32"; B=27 7/16"; B/2=13 23/32"; B/4=6 7/8"; C=59 3/16"; C/2=29 19/32"; CLASS=1"; D=46 1/16"; D-L-K-J=1"; D-M=26 5/8"; E=48 5/16"; E/2=24 5/32"; E/52*15=13 15/16"; F=29 5/8"; F/2=14 13/16"; H=27 5/8"; H/2=13 13/16"; HEIGHT=45 11/32"; J=8 1/2"; J+K+L=45 1/16"; K=15 1/8"; L=21 7/16"; M=19 7/16"; M-(2*(D-L-K-J))=17 7/16"; N=8 11/32"; N+(H/2)=22 5/32"; NOZZLE_BOTTOM_ID=21 3/8"; NOZZLE_BOTTOM_RAD=10 11/16"; NOZZLE_BOTTOM_RAD-3*2=4 11/16"; NOZZLE_HEIGHT=43"; NOZZLE_HEIGHT/7*2=10 3/4"; NOZZLE_SIZE=15"; NOZZLE_TOP_OD=23"; NOZZLE_TOP_RAD=11 1/2"; NOZZLE_WB/4=7 3/16"; NOZZLE_WB_OD=36"; NOZZLE_WB_RAD=18"; NOZZLE_WB_RAD-2"=16"; P=60"; R=24 1/4"; R*1.1=26 11/16"; R+((B/2)+1.5")=39 15/32"; R-((B/2)+1.5")=9 1/32"; TRANSITION=15 1/8"; TRANSITION/2=7 9/16"; Type Comments=Vari-Plume Laboratory Exhaust Centrifugal Airfoil Class 1 Arr 10
- 225_CAVP-18H_CLASS_1: ((M - (2 * (D - L - K - J))) / 2) + (TRANSITION / 2)=17 25/32"; (B/2)+1.5"=15 7/32"; (B/2)-.125"=13 19/32"; (D-J-K-L)*2=2"; (F-((F-H)/2))/2=12 13/16"; (M - (2 * (D - L - K - J)))/2=8 23/32"; (NOZZLE_HEIGHT - (NOZZLE_HEIGHT / 8 * 2)) / 2=18"; (NOZZLE_WB_OD - NOZZLE_TOP_OD) / 4=3 7/8"; -(F-((F-H)/2))/2=-12 13/16"; A=106 11/16"; A/2=53 11/32"; B=27 7/16"; B/2=13 23/32"; B/4=6 7/8"; C=59 3/16"; C/2=29 19/32"; CLASS=1"; D=46 1/16"; D-L-K-J=1"; D-M=26 5/8"; E=48 5/16"; E/2=24 5/32"; E/52*15=13 15/16"; F=29 5/8"; F/2=14 13/16"; H=27 5/8"; H/2=13 13/16"; HEIGHT=45 11/32"; J=8 1/2"; J+K+L=45 1/16"; K=15 1/8"; L=21 7/16"; M=19 7/16"; M-(2*(D-L-K-J))=17 7/16"; N=8 11/32"; N+(H/2)=22 5/32"; NOZZLE_BOTTOM_ID=25 5/8"; NOZZLE_BOTTOM_RAD=12 13/16"; NOZZLE_BOTTOM_RAD-3*2=6 13/16"; NOZZLE_HEIGHT=48"; NOZZLE_HEIGHT/7*2=12"; NOZZLE_SIZE=18"; NOZZLE_TOP_OD=27 1/2"; NOZZLE_TOP_RAD=13 3/4"; NOZZLE_WB/4=8 19/32"; NOZZLE_WB_OD=43"; NOZZLE_WB_RAD=21 1/2"; NOZZLE_WB_RAD-2"=19 1/2"; P=60"; R=24 1/4"; R*1.1=26 11/16"; R+((B/2)+1.5")=39 15/32"; R-((B/2)+1.5")=9 1/32"; TRANSITION=18 1/8"; TRANSITION/2=9 1/16"; Type Comments=Vari-Plume Laboratory Exhaust Centrifugal Airfoil Class 1 Arr 10
- 225_CAVP-18L_CLASS_1: ((M - (2 * (D - L - K - J))) / 2) + (TRANSITION / 2)=17 25/32"; (B/2)+1.5"=15 7/32"; (B/2)-.125"=13 19/32"; (D-J-K-L)*2=2"; (F-((F-H)/2))/2=12 13/16"; (M - (2 * (D - L - K - J)))/2=8 23/32"; (NOZZLE_HEIGHT - (NOZZLE_HEIGHT / 8 * 2)) / 2=18"; (NOZZLE_WB_OD - NOZZLE_TOP_OD) / 4=3 7/8"; -(F-((F-H)/2))/2=-12 13/16"; A=106 11/16"; A/2=53 11/32"; B=27 7/16"; B/2=13 23/32"; B/4=6 7/8"; C=59 3/16"; C/2=29 19/32"; CLASS=1"; D=46 1/16"; D-L-K-J=1"; D-M=26 5/8"; E=48 5/16"; E/2=24 5/32"; E/52*15=13 15/16"; F=29 5/8"; F/2=14 13/16"; H=27 5/8"; H/2=13 13/16"; HEIGHT=45 11/32"; J=8 1/2"; J+K+L=45 1/16"; K=15 1/8"; L=21 7/16"; M=19 7/16"; M-(2*(D-L-K-J))=17 7/16"; N=8 11/32"; N+(H/2)=22 5/32"; NOZZLE_BOTTOM_ID=25 5/8"; NOZZLE_BOTTOM_RAD=12 13/16"; NOZZLE_BOTTOM_RAD-3*2=6 13/16"; NOZZLE_HEIGHT=48"; NOZZLE_HEIGHT/7*2=12"; NOZZLE_SIZE=18"; NOZZLE_TOP_OD=27 1/2"; NOZZLE_TOP_RAD=13 3/4"; NOZZLE_WB/4=8 19/32"; NOZZLE_WB_OD=43"; NOZZLE_WB_RAD=21 1/2"; NOZZLE_WB_RAD-2"=19 1/2"; P=60"; R=24 1/4"; R*1.1=26 11/16"; R+((B/2)+1.5")=39 15/32"; R-((B/2)+1.5")=9 1/32"; TRANSITION=18 1/8"; TRANSITION/2=9 1/16"; Type Comments=Vari-Plume Laboratory Exhaust Centrifugal Airfoil Class 1 Arr 10
- 225_CAVP-18H_CLASS_2: ((M - (2 * (D - L - K - J))) / 2) + (TRANSITION / 2)=17 25/32"; (B/2)+1.5"=15 7/32"; (B/2)-.125"=13 19/32"; (D-J-K-L)*2=2"; (F-((F-H)/2))/2=12 13/16"; (M - (2 * (D - L - K - J)))/2=8 23/32"; (NOZZLE_HEIGHT - (NOZZLE_HEIGHT / 8 * 2)) / 2=18"; (NOZZLE_WB_OD - NOZZLE_TOP_OD) / 4=3 7/8"; -(F-((F-H)/2))/2=-12 13/16"; A=106 11/16"; A/2=53 11/32"; B=27 7/16"; B/2=13 23/32"; B/4=6 7/8"; C=59 3/16"; C/2=29 19/32"; CLASS=2"; D=50 1/16"; D-L-K-J=1"; D-M=30 5/8"; E=48 5/16"; E/2=24 5/32"; E/52*15=13 15/16"; F=29 5/8"; F/2=14 13/16"; H=27 5/8"; H/2=13 13/16"; HEIGHT=45 11/32"; J=8 1/4"; J+K+L=49 1/16"; K=19 3/8"; L=21 7/16"; M=19 7/16"; M-(2*(D-L-K-J))=17 7/16"; N=8 1/2"; N+(H/2)=22 5/16"; NOZZLE_BOTTOM_ID=25 5/8"; NOZZLE_BOTTOM_RAD=12 13/16"; NOZZLE_BOTTOM_RAD-3*2=6 13/16"; NOZZLE_HEIGHT=48"; NOZZLE_HEIGHT/7*2=12"; NOZZLE_SIZE=18"; NOZZLE_TOP_OD=27 1/2"; NOZZLE_TOP_RAD=13 3/4"; NOZZLE_WB/4=8 19/32"; NOZZLE_WB_OD=43"; NOZZLE_WB_RAD=21 1/2"; NOZZLE_WB_RAD-2"=19 1/2"; P=60"; R=24 1/4"; R*1.1=26 11/16"; R+((B/2)+1.5")=39 15/32"; R-((B/2)+1.5")=9 1/32"; TRANSITION=18 1/8"; TRANSITION/2=9 1/16"; Type Comments=Vari-Plume Laboratory Exhaust Centrifugal Airfoil Class 2 Arr 10
- 225_CAVP-18L_CLASS_2: ((M - (2 * (D - L - K - J))) / 2) + (TRANSITION / 2)=17 25/32"; (B/2)+1.5"=15 7/32"; (B/2)-.125"=13 19/32"; (D-J-K-L)*2=2"; (F-((F-H)/2))/2=12 13/16"; (M - (2 * (D - L - K - J)))/2=8 23/32"; (NOZZLE_HEIGHT - (NOZZLE_HEIGHT / 8 * 2)) / 2=18"; (NOZZLE_WB_OD - NOZZLE_TOP_OD) / 4=3 7/8"; -(F-((F-H)/2))/2=-12 13/16"; A=106 11/16"; A/2=53 11/32"; B=27 7/16"; B/2=13 23/32"; B/4=6 7/8"; C=59 3/16"; C/2=29 19/32"; CLASS=2"; D=50 1/16"; D-L-K-J=1"; D-M=30 5/8"; E=48 5/16"; E/2=24 5/32"; E/52*15=13 15/16"; F=29 5/8"; F/2=14 13/16"; H=27 5/8"; H/2=13 13/16"; HEIGHT=45 11/32"; J=8 1/4"; J+K+L=49 1/16"; K=19 3/8"; L=21 7/16"; M=19 7/16"; M-(2*(D-L-K-J))=17 7/16"; N=8 1/2"; N+(H/2)=22 5/16"; NOZZLE_BOTTOM_ID=25 5/8"; NOZZLE_BOTTOM_RAD=12 13/16"; NOZZLE_BOTTOM_RAD-3*2=6 13/16"; NOZZLE_HEIGHT=48"; NOZZLE_HEIGHT/7*2=12"; NOZZLE_SIZE=18"; NOZZLE_TOP_OD=27 1/2"; NOZZLE_TOP_RAD=13 3/4"; NOZZLE_WB/4=8 19/32"; NOZZLE_WB_OD=43"; NOZZLE_WB_RAD=21 1/2"; NOZZLE_WB_RAD-2"=19 1/2"; P=60"; R=24 1/4"; R*1.1=26 11/16"; R+((B/2)+1.5")=39 15/32"; R-((B/2)+1.5")=9 1/32"; TRANSITION=18 1/8"; TRANSITION/2=9 1/16"; Type Comments=Vari-Plume Laboratory Exhaust Centrifugal Airfoil Class 2 Arr 10
- 225_CAVP-15H_CLASS_2: ((M - (2 * (D - L - K - J))) / 2) + (TRANSITION / 2)=16 9/32"; (B/2)+1.5"=15 7/32"; (B/2)-.125"=13 19/32"; (D-J-K-L)*2=2"; (F-((F-H)/2))/2=12 13/16"; (M - (2 * (D - L - K - J)))/2=8 23/32"; (NOZZLE_HEIGHT - (NOZZLE_HEIGHT / 8 * 2)) / 2=16 1/8"; (NOZZLE_WB_OD - NOZZLE_TOP_OD) / 4=3 1/4"; -(F-((F-H)/2))/2=-12 13/16"; A=106 11/16"; A/2=53 11/32"; B=27 7/16"; B/2=13 23/32"; B/4=6 7/8"; C=59 3/16"; C/2=29 19/32"; CLASS=2"; D=50 1/16"; D-L-K-J=1"; D-M=30 5/8"; E=48 5/16"; E/2=24 5/32"; E/52*15=13 15/16"; F=29 5/8"; F/2=14 13/16"; H=27 5/8"; H/2=13 13/16"; HEIGHT=45 11/32"; J=8 1/4"; J+K+L=49 1/16"; K=19 3/8"; L=21 7/16"; M=19 7/16"; M-(2*(D-L-K-J))=17 7/16"; N=8 1/2"; N+(H/2)=22 5/16"; NOZZLE_BOTTOM_ID=21 3/8"; NOZZLE_BOTTOM_RAD=10 11/16"; NOZZLE_BOTTOM_RAD-3*2=4 11/16"; NOZZLE_HEIGHT=43"; NOZZLE_HEIGHT/7*2=10 3/4"; NOZZLE_SIZE=15"; NOZZLE_TOP_OD=23"; NOZZLE_TOP_RAD=11 1/2"; NOZZLE_WB/4=7 3/16"; NOZZLE_WB_OD=36"; NOZZLE_WB_RAD=18"; NOZZLE_WB_RAD-2"=16"; P=60"; R=24 1/4"; R*1.1=26 11/16"; R+((B/2)+1.5")=39 15/32"; R-((B/2)+1.5")=9 1/32"; TRANSITION=15 1/8"; TRANSITION/2=7 9/16"; Type Comments=Vari-Plume Laboratory Exhaust Centrifugal Airfoil Class 2 Arr 10
- 225_CAVP-15L_CLASS_2: ((M - (2 * (D - L - K - J))) / 2) + (TRANSITION / 2)=16 9/32"; (B/2)+1.5"=15 7/32"; (B/2)-.125"=13 19/32"; (D-J-K-L)*2=2"; (F-((F-H)/2))/2=12 13/16"; (M - (2 * (D - L - K - J)))/2=8 23/32"; (NOZZLE_HEIGHT - (NOZZLE_HEIGHT / 8 * 2)) / 2=16 1/8"; (NOZZLE_WB_OD - NOZZLE_TOP_OD) / 4=3 1/4"; -(F-((F-H)/2))/2=-12 13/16"; A=106 11/16"; A/2=53 11/32"; B=27 7/16"; B/2=13 23/32"; B/4=6 7/8"; C=59 3/16"; C/2=29 19/32"; CLASS=2"; D=50 1/16"; D-L-K-J=1"; D-M=30 5/8"; E=48 5/16"; E/2=24 5/32"; E/52*15=13 15/16"; F=29 5/8"; F/2=14 13/16"; H=27 5/8"; H/2=13 13/16"; HEIGHT=45 11/32"; J=8 1/4"; J+K+L=49 1/16"; K=19 3/8"; L=21 7/16"; M=19 7/16"; M-(2*(D-L-K-J))=17 7/16"; N=8 1/2"; N+(H/2)=22 5/16"; NOZZLE_BOTTOM_ID=21 3/8"; NOZZLE_BOTTOM_RAD=10 11/16"; NOZZLE_BOTTOM_RAD-3*2=4 11/16"; NOZZLE_HEIGHT=43"; NOZZLE_HEIGHT/7*2=10 3/4"; NOZZLE_SIZE=15"; NOZZLE_TOP_OD=23"; NOZZLE_TOP_RAD=11 1/2"; NOZZLE_WB/4=7 3/16"; NOZZLE_WB_OD=36"; NOZZLE_WB_RAD=18"; NOZZLE_WB_RAD-2"=16"; P=60"; R=24 1/4"; R*1.1=26 11/16"; R+((B/2)+1.5")=39 15/32"; R-((B/2)+1.5")=9 1/32"; TRANSITION=15 1/8"; TRANSITION/2=7 9/16"; Type Comments=Vari-Plume Laboratory Exhaust Centrifugal Airfoil Class 2 Arr 10
- 225_CAVP-12H_CLASS_2: ((M - (2 * (D - L - K - J))) / 2) + (TRANSITION / 2)=14 3/4"; (B/2)+1.5"=15 7/32"; (B/2)-.125"=13 19/32"; (D-J-K-L)*2=2"; (F-((F-H)/2))/2=12 13/16"; (M - (2 * (D - L - K - J)))/2=8 23/32"; (NOZZLE_HEIGHT - (NOZZLE_HEIGHT / 8 * 2)) / 2=12"; (NOZZLE_WB_OD - NOZZLE_TOP_OD) / 4=2 1/8"; -(F-((F-H)/2))/2=-12 13/16"; A=106 11/16"; A/2=53 11/32"; B=27 7/16"; B/2=13 23/32"; B/4=6 7/8"; C=59 3/16"; C/2=29 19/32"; CLASS=2"; D=50 1/16"; D-L-K-J=1"; D-M=30 5/8"; E=48 5/16"; E/2=24 5/32"; E/52*15=13 15/16"; F=29 5/8"; F/2=14 13/16"; H=27 5/8"; H/2=13 13/16"; HEIGHT=45 11/32"; J=8 1/4"; J+K+L=49 1/16"; K=19 3/8"; L=21 7/16"; M=19 7/16"; M-(2*(D-L-K-J))=17 7/16"; N=8 1/2"; N+(H/2)=22 5/16"; NOZZLE_BOTTOM_ID=17 1/16"; NOZZLE_BOTTOM_RAD=8 17/32"; NOZZLE_BOTTOM_RAD-3*2=2 17/32"; NOZZLE_HEIGHT=32"; NOZZLE_HEIGHT/7*2=8"; NOZZLE_SIZE=12"; NOZZLE_TOP_OD=19 1/2"; NOZZLE_TOP_RAD=9 3/4"; NOZZLE_WB/4=5 19/32"; NOZZLE_WB_OD=28"; NOZZLE_WB_RAD=14"; NOZZLE_WB_RAD-2"=12"; P=60"; R=24 1/4"; R*1.1=26 11/16"; R+((B/2)+1.5")=39 15/32"; R-((B/2)+1.5")=9 1/32"; TRANSITION=12 1/16"; TRANSITION/2=6 1/32"; Type Comments=Vari-Plume Laboratory Exhaust Centrifugal Airfoil Class 2 Arr 10
- 225_CAVP-12L_CLASS_2: ((M - (2 * (D - L - K - J))) / 2) + (TRANSITION / 2)=14 3/4"; (B/2)+1.5"=15 7/32"; (B/2)-.125"=13 19/32"; (D-J-K-L)*2=2"; (F-((F-H)/2))/2=12 13/16"; (M - (2 * (D - L - K - J)))/2=8 23/32"; (NOZZLE_HEIGHT - (NOZZLE_HEIGHT / 8 * 2)) / 2=12"; (NOZZLE_WB_OD - NOZZLE_TOP_OD) / 4=2 1/8"; -(F-((F-H)/2))/2=-12 13/16"; A=106 11/16"; A/2=53 11/32"; B=27 7/16"; B/2=13 23/32"; B/4=6 7/8"; C=59 3/16"; C/2=29 19/32"; CLASS=2"; D=50 1/16"; D-L-K-J=1"; D-M=30 5/8"; E=48 5/16"; E/2=24 5/32"; E/52*15=13 15/16"; F=29 5/8"; F/2=14 13/16"; H=27 5/8"; H/2=13 13/16"; HEIGHT=45 11/32"; J=8 1/4"; J+K+L=49 1/16"; K=19 3/8"; L=21 7/16"; M=19 7/16"; M-(2*(D-L-K-J))=17 7/16"; N=8 1/2"; N+(H/2)=22 5/16"; NOZZLE_BOTTOM_ID=17 1/16"; NOZZLE_BOTTOM_RAD=8 17/32"; NOZZLE_BOTTOM_RAD-3*2=2 17/32"; NOZZLE_HEIGHT=32"; NOZZLE_HEIGHT/7*2=8"; NOZZLE_SIZE=12"; NOZZLE_TOP_OD=19 1/2"; NOZZLE_TOP_RAD=9 3/4"; NOZZLE_WB/4=5 19/32"; NOZZLE_WB_OD=28"; NOZZLE_WB_RAD=14"; NOZZLE_WB_RAD-2"=12"; P=60"; R=24 1/4"; R*1.1=26 11/16"; R+((B/2)+1.5")=39 15/32"; R-((B/2)+1.5")=9 1/32"; TRANSITION=12 1/16"; TRANSITION/2=6 1/32"; Type Comments=Vari-Plume Laboratory Exhaust Centrifugal Airfoil Class 2 Arr 10
- 245_CAVP-12L_CLASS_1: ((M - (2 * (D - L - K - J))) / 2) + (TRANSITION / 2)=15 17/32"; (B/2)+1.5"=16 7/32"; (B/2)-.125"=14 19/32"; (D-J-K-L)*2=2"; (F-((F-H)/2))/2=13 13/16"; (M - (2 * (D - L - K - J)))/2=9 1/2"; (NOZZLE_HEIGHT - (NOZZLE_HEIGHT / 8 * 2)) / 2=12"; (NOZZLE_WB_OD - NOZZLE_TOP_OD) / 4=2 1/8"; -(F-((F-H)/2))/2=-13 13/16"; A=112 1/4"; A/2=56 1/8"; B=29 7/16"; B/2=14 23/32"; B/4=7 3/8"; C=64 3/4"; C/2=32 3/8"; CLASS=1"; D=49 7/8"; D-L-K-J=1"; D-M=28 7/8"; E=52 7/16"; E/2=26 7/32"; E/52*15=15 1/8"; F=31 5/8"; F/2=15 13/16"; H=29 5/8"; H/2=14 13/16"; HEIGHT=49 29/32"; J=9"; J+K+L=48 7/8"; K=16 7/8"; L=23"; M=21"; M-(2*(D-L-K-J))=19"; N=9 13/32"; N+(H/2)=24 7/32"; NOZZLE_BOTTOM_ID=17 1/16"; NOZZLE_BOTTOM_RAD=8 17/32"; NOZZLE_BOTTOM_RAD-3*2=2 17/32"; NOZZLE_HEIGHT=32"; NOZZLE_HEIGHT/7*2=8"; NOZZLE_SIZE=12"; NOZZLE_TOP_OD=19 1/2"; NOZZLE_TOP_RAD=9 3/4"; NOZZLE_WB/4=5 19/32"; NOZZLE_WB_OD=28"; NOZZLE_WB_RAD=14"; NOZZLE_WB_RAD-2"=12"; P=60"; R=27"; R*1.1=29 11/16"; R+((B/2)+1.5")=43 7/32"; R-((B/2)+1.5")=10 25/32"; TRANSITION=12 1/16"; TRANSITION/2=6 1/32"; Type Comments=Vari-Plume Laboratory Exhaust Centrifugal Airfoil Class 1 Arr 10
- 245_CAVP-12H_CLASS_1: ((M - (2 * (D - L - K - J))) / 2) + (TRANSITION / 2)=15 17/32"; (B/2)+1.5"=16 7/32"; (B/2)-.125"=14 19/32"; (D-J-K-L)*2=2"; (F-((F-H)/2))/2=13 13/16"; (M - (2 * (D - L - K - J)))/2=9 1/2"; (NOZZLE_HEIGHT - (NOZZLE_HEIGHT / 8 * 2)) / 2=12"; (NOZZLE_WB_OD - NOZZLE_TOP_OD) / 4=2 1/8"; -(F-((F-H)/2))/2=-13 13/16"; A=112 1/4"; A/2=56 1/8"; B=29 7/16"; B/2=14 23/32"; B/4=7 3/8"; C=64 3/4"; C/2=32 3/8"; CLASS=1"; D=49 7/8"; D-L-K-J=1"; D-M=28 7/8"; E=52 7/16"; E/2=26 7/32"; E/52*15=15 1/8"; F=31 5/8"; F/2=15 13/16"; H=29 5/8"; H/2=14 13/16"; HEIGHT=49 29/32"; J=9"; J+K+L=48 7/8"; K=16 7/8"; L=23"; M=21"; M-(2*(D-L-K-J))=19"; N=9 13/32"; N+(H/2)=24 7/32"; NOZZLE_BOTTOM_ID=17 1/16"; NOZZLE_BOTTOM_RAD=8 17/32"; NOZZLE_BOTTOM_RAD-3*2=2 17/32"; NOZZLE_HEIGHT=32"; NOZZLE_HEIGHT/7*2=8"; NOZZLE_SIZE=12"; NOZZLE_TOP_OD=19 1/2"; NOZZLE_TOP_RAD=9 3/4"; NOZZLE_WB/4=5 19/32"; NOZZLE_WB_OD=28"; NOZZLE_WB_RAD=14"; NOZZLE_WB_RAD-2"=12"; P=60"; R=27"; R*1.1=29 11/16"; R+((B/2)+1.5")=43 7/32"; R-((B/2)+1.5")=10 25/32"; TRANSITION=12 1/16"; TRANSITION/2=6 1/32"; Type Comments=Vari-Plume Laboratory Exhaust Centrifugal Airfoil Class 1 Arr 10
- 245_CAVP-15L_CLASS_1: ((M - (2 * (D - L - K - J))) / 2) + (TRANSITION / 2)=17 1/16"; (B/2)+1.5"=16 7/32"; (B/2)-.125"=14 19/32"; (D-J-K-L)*2=2"; (F-((F-H)/2))/2=13 13/16"; (M - (2 * (D - L - K - J)))/2=9 1/2"; (NOZZLE_HEIGHT - (NOZZLE_HEIGHT / 8 * 2)) / 2=16 1/8"; (NOZZLE_WB_OD - NOZZLE_TOP_OD) / 4=3 1/4"; -(F-((F-H)/2))/2=-13 13/16"; A=112 1/4"; A/2=56 1/8"; B=29 7/16"; B/2=14 23/32"; B/4=7 3/8"; C=64 3/4"; C/2=32 3/8"; CLASS=1"; D=49 7/8"; D-L-K-J=1"; D-M=28 7/8"; E=52 7/16"; E/2=26 7/32"; E/52*15=15 1/8"; F=31 5/8"; F/2=15 13/16"; H=29 5/8"; H/2=14 13/16"; HEIGHT=49 29/32"; J=9"; J+K+L=48 7/8"; K=16 7/8"; L=23"; M=21"; M-(2*(D-L-K-J))=19"; N=9 13/32"; N+(H/2)=24 7/32"; NOZZLE_BOTTOM_ID=21 3/8"; NOZZLE_BOTTOM_RAD=10 11/16"; NOZZLE_BOTTOM_RAD-3*2=4 11/16"; NOZZLE_HEIGHT=43"; NOZZLE_HEIGHT/7*2=10 3/4"; NOZZLE_SIZE=15"; NOZZLE_TOP_OD=23"; NOZZLE_TOP_RAD=11 1/2"; NOZZLE_WB/4=7 3/16"; NOZZLE_WB_OD=36"; NOZZLE_WB_RAD=18"; NOZZLE_WB_RAD-2"=16"; P=60"; R=27"; R*1.1=29 11/16"; R+((B/2)+1.5")=43 7/32"; R-((B/2)+1.5")=10 25/32"; TRANSITION=15 1/8"; TRANSITION/2=7 9/16"; Type Comments=Vari-Plume Laboratory Exhaust Centrifugal Airfoil Class 1 Arr 10
- 245_CAVP-15H_CLASS_1: ((M - (2 * (D - L - K - J))) / 2) + (TRANSITION / 2)=17 1/16"; (B/2)+1.5"=16 7/32"; (B/2)-.125"=14 19/32"; (D-J-K-L)*2=2"; (F-((F-H)/2))/2=13 13/16"; (M - (2 * (D - L - K - J)))/2=9 1/2"; (NOZZLE_HEIGHT - (NOZZLE_HEIGHT / 8 * 2)) / 2=16 1/8"; (NOZZLE_WB_OD - NOZZLE_TOP_OD) / 4=3 1/4"; -(F-((F-H)/2))/2=-13 13/16"; A=112 1/4"; A/2=56 1/8"; B=29 7/16"; B/2=14 23/32"; B/4=7 3/8"; C=64 3/4"; C/2=32 3/8"; CLASS=1"; D=49 7/8"; D-L-K-J=1"; D-M=28 7/8"; E=52 7/16"; E/2=26 7/32"; E/52*15=15 1/8"; F=31 5/8"; F/2=15 13/16"; H=29 5/8"; H/2=14 13/16"; HEIGHT=49 29/32"; J=9"; J+K+L=48 7/8"; K=16 7/8"; L=23"; M=21"; M-(2*(D-L-K-J))=19"; N=9 13/32"; N+(H/2)=24 7/32"; NOZZLE_BOTTOM_ID=21 3/8"; NOZZLE_BOTTOM_RAD=10 11/16"; NOZZLE_BOTTOM_RAD-3*2=4 11/16"; NOZZLE_HEIGHT=43"; NOZZLE_HEIGHT/7*2=10 3/4"; NOZZLE_SIZE=15"; NOZZLE_TOP_OD=23"; NOZZLE_TOP_RAD=11 1/2"; NOZZLE_WB/4=7 3/16"; NOZZLE_WB_OD=36"; NOZZLE_WB_RAD=18"; NOZZLE_WB_RAD-2"=16"; P=60"; R=27"; R*1.1=29 11/16"; R+((B/2)+1.5")=43 7/32"; R-((B/2)+1.5")=10 25/32"; TRANSITION=15 1/8"; TRANSITION/2=7 9/16"; Type Comments=Vari-Plume Laboratory Exhaust Centrifugal Airfoil Class 1 Arr 10
- 245_CAVP-18L_CLASS_1: ((M - (2 * (D - L - K - J))) / 2) + (TRANSITION / 2)=18 9/16"; (B/2)+1.5"=16 7/32"; (B/2)-.125"=14 19/32"; (D-J-K-L)*2=2"; (F-((F-H)/2))/2=13 13/16"; (M - (2 * (D - L - K - J)))/2=9 1/2"; (NOZZLE_HEIGHT - (NOZZLE_HEIGHT / 8 * 2)) / 2=18"; (NOZZLE_WB_OD - NOZZLE_TOP_OD) / 4=3 7/8"; -(F-((F-H)/2))/2=-13 13/16"; A=112 1/4"; A/2=56 1/8"; B=29 7/16"; B/2=14 23/32"; B/4=7 3/8"; C=64 3/4"; C/2=32 3/8"; CLASS=1"; D=49 7/8"; D-L-K-J=1"; D-M=28 7/8"; E=52 7/16"; E/2=26 7/32"; E/52*15=15 1/8"; F=31 5/8"; F/2=15 13/16"; H=29 5/8"; H/2=14 13/16"; HEIGHT=49 29/32"; J=9"; J+K+L=48 7/8"; K=16 7/8"; L=23"; M=21"; M-(2*(D-L-K-J))=19"; N=9 13/32"; N+(H/2)=24 7/32"; NOZZLE_BOTTOM_ID=25 5/8"; NOZZLE_BOTTOM_RAD=12 13/16"; NOZZLE_BOTTOM_RAD-3*2=6 13/16"; NOZZLE_HEIGHT=48"; NOZZLE_HEIGHT/7*2=12"; NOZZLE_SIZE=18"; NOZZLE_TOP_OD=27 1/2"; NOZZLE_TOP_RAD=13 3/4"; NOZZLE_WB/4=8 19/32"; NOZZLE_WB_OD=43"; NOZZLE_WB_RAD=21 1/2"; NOZZLE_WB_RAD-2"=19 1/2"; P=60"; R=27"; R*1.1=29 11/16"; R+((B/2)+1.5")=43 7/32"; R-((B/2)+1.5")=10 25/32"; TRANSITION=18 1/8"; TRANSITION/2=9 1/16"; Type Comments=Vari-Plume Laboratory Exhaust Centrifugal Airfoil Class 1 Arr 10
- 245_CAVP-18H_CLASS_1: ((M - (2 * (D - L - K - J))) / 2) + (TRANSITION / 2)=18 9/16"; (B/2)+1.5"=16 7/32"; (B/2)-.125"=14 19/32"; (D-J-K-L)*2=2"; (F-((F-H)/2))/2=13 13/16"; (M - (2 * (D - L - K - J)))/2=9 1/2"; (NOZZLE_HEIGHT - (NOZZLE_HEIGHT / 8 * 2)) / 2=18"; (NOZZLE_WB_OD - NOZZLE_TOP_OD) / 4=3 7/8"; -(F-((F-H)/2))/2=-13 13/16"; A=112 1/4"; A/2=56 1/8"; B=29 7/16"; B/2=14 23/32"; B/4=7 3/8"; C=64 3/4"; C/2=32 3/8"; CLASS=1"; D=49 7/8"; D-L-K-J=1"; D-M=28 7/8"; E=52 7/16"; E/2=26 7/32"; E/52*15=15 1/8"; F=31 5/8"; F/2=15 13/16"; H=29 5/8"; H/2=14 13/16"; HEIGHT=49 29/32"; J=9"; J+K+L=48 7/8"; K=16 7/8"; L=23"; M=21"; M-(2*(D-L-K-J))=19"; N=9 13/32"; N+(H/2)=24 7/32"; NOZZLE_BOTTOM_ID=25 5/8"; NOZZLE_BOTTOM_RAD=12 13/16"; NOZZLE_BOTTOM_RAD-3*2=6 13/16"; NOZZLE_HEIGHT=48"; NOZZLE_HEIGHT/7*2=12"; NOZZLE_SIZE=18"; NOZZLE_TOP_OD=27 1/2"; NOZZLE_TOP_RAD=13 3/4"; NOZZLE_WB/4=8 19/32"; NOZZLE_WB_OD=43"; NOZZLE_WB_RAD=21 1/2"; NOZZLE_WB_RAD-2"=19 1/2"; P=60"; R=27"; R*1.1=29 11/16"; R+((B/2)+1.5")=43 7/32"; R-((B/2)+1.5")=10 25/32"; TRANSITION=18 1/8"; TRANSITION/2=9 1/16"; Type Comments=Vari-Plume Laboratory Exhaust Centrifugal Airfoil Class 1 Arr 10
- 245_CAVP-12L_CLASS_2: ((M - (2 * (D - L - K - J))) / 2) + (TRANSITION / 2)=15 17/32"; (B/2)+1.5"=16 7/32"; (B/2)-.125"=14 19/32"; (D-J-K-L)*2=2"; (F-((F-H)/2))/2=13 13/16"; (M - (2 * (D - L - K - J)))/2=9 1/2"; (NOZZLE_HEIGHT - (NOZZLE_HEIGHT / 8 * 2)) / 2=12"; (NOZZLE_WB_OD - NOZZLE_TOP_OD) / 4=2 1/8"; -(F-((F-H)/2))/2=-13 13/16"; A=112 1/4"; A/2=56 1/8"; B=29 7/16"; B/2=14 23/32"; B/4=7 3/8"; C=64 3/4"; C/2=32 3/8"; CLASS=2"; D=54 1/8"; D-L-K-J=1"; D-M=33 1/8"; E=52 7/16"; E/2=26 7/32"; E/52*15=15 1/8"; F=31 5/8"; F/2=15 13/16"; H=29 5/8"; H/2=14 13/16"; HEIGHT=49 29/32"; J=9"; J+K+L=53 1/8"; K=21 1/8"; L=23"; M=21"; M-(2*(D-L-K-J))=19"; N=9 13/32"; N+(H/2)=24 7/32"; NOZZLE_BOTTOM_ID=17 1/16"; NOZZLE_BOTTOM_RAD=8 17/32"; NOZZLE_BOTTOM_RAD-3*2=2 17/32"; NOZZLE_HEIGHT=32"; NOZZLE_HEIGHT/7*2=8"; NOZZLE_SIZE=12"; NOZZLE_TOP_OD=19 1/2"; NOZZLE_TOP_RAD=9 3/4"; NOZZLE_WB/4=5 19/32"; NOZZLE_WB_OD=28"; NOZZLE_WB_RAD=14"; NOZZLE_WB_RAD-2"=12"; P=60"; R=27"; R*1.1=29 11/16"; R+((B/2)+1.5")=43 7/32"; R-((B/2)+1.5")=10 25/32"; TRANSITION=12 1/16"; TRANSITION/2=6 1/32"; Type Comments=Vari-Plume Laboratory Exhaust Centrifugal Airfoil Class 2 Arr 10
- 245_CAVP-12H_CLASS_2: ((M - (2 * (D - L - K - J))) / 2) + (TRANSITION / 2)=15 17/32"; (B/2)+1.5"=16 7/32"; (B/2)-.125"=14 19/32"; (D-J-K-L)*2=2"; (F-((F-H)/2))/2=13 13/16"; (M - (2 * (D - L - K - J)))/2=9 1/2"; (NOZZLE_HEIGHT - (NOZZLE_HEIGHT / 8 * 2)) / 2=12"; (NOZZLE_WB_OD - NOZZLE_TOP_OD) / 4=2 1/8"; -(F-((F-H)/2))/2=-13 13/16"; A=112 1/4"; A/2=56 1/8"; B=29 7/16"; B/2=14 23/32"; B/4=7 3/8"; C=64 3/4"; C/2=32 3/8"; CLASS=2"; D=54 1/8"; D-L-K-J=1"; D-M=33 1/8"; E=52 7/16"; E/2=26 7/32"; E/52*15=15 1/8"; F=31 5/8"; F/2=15 13/16"; H=29 5/8"; H/2=14 13/16"; HEIGHT=49 29/32"; J=9"; J+K+L=53 1/8"; K=21 1/8"; L=23"; M=21"; M-(2*(D-L-K-J))=19"; N=9 13/32"; N+(H/2)=24 7/32"; NOZZLE_BOTTOM_ID=17 1/16"; NOZZLE_BOTTOM_RAD=8 17/32"; NOZZLE_BOTTOM_RAD-3*2=2 17/32"; NOZZLE_HEIGHT=32"; NOZZLE_HEIGHT/7*2=8"; NOZZLE_SIZE=12"; NOZZLE_TOP_OD=19 1/2"; NOZZLE_TOP_RAD=9 3/4"; NOZZLE_WB/4=5 19/32"; NOZZLE_WB_OD=28"; NOZZLE_WB_RAD=14"; NOZZLE_WB_RAD-2"=12"; P=60"; R=27"; R*1.1=29 11/16"; R+((B/2)+1.5")=43 7/32"; R-((B/2)+1.5")=10 25/32"; TRANSITION=12 1/16"; TRANSITION/2=6 1/32"; Type Comments=Vari-Plume Laboratory Exhaust Centrifugal Airfoil Class 2 Arr 10
- 245_CAVP-15L_CLASS_2: ((M - (2 * (D - L - K - J))) / 2) + (TRANSITION / 2)=17 1/16"; (B/2)+1.5"=16 7/32"; (B/2)-.125"=14 19/32"; (D-J-K-L)*2=2"; (F-((F-H)/2))/2=13 13/16"; (M - (2 * (D - L - K - J)))/2=9 1/2"; (NOZZLE_HEIGHT - (NOZZLE_HEIGHT / 8 * 2)) / 2=16 1/8"; (NOZZLE_WB_OD - NOZZLE_TOP_OD) / 4=3 1/4"; -(F-((F-H)/2))/2=-13 13/16"; A=112 1/4"; A/2=56 1/8"; B=29 7/16"; B/2=14 23/32"; B/4=7 3/8"; C=64 3/4"; C/2=32 3/8"; CLASS=2"; D=54 1/8"; D-L-K-J=1"; D-M=33 1/8"; E=52 7/16"; E/2=26 7/32"; E/52*15=15 1/8"; F=31 5/8"; F/2=15 13/16"; H=29 5/8"; H/2=14 13/16"; HEIGHT=49 29/32"; J=9"; J+K+L=53 1/8"; K=21 1/8"; L=23"; M=21"; M-(2*(D-L-K-J))=19"; N=9 13/32"; N+(H/2)=24 7/32"; NOZZLE_BOTTOM_ID=21 3/8"; NOZZLE_BOTTOM_RAD=10 11/16"; NOZZLE_BOTTOM_RAD-3*2=4 11/16"; NOZZLE_HEIGHT=43"; NOZZLE_HEIGHT/7*2=10 3/4"; NOZZLE_SIZE=15"; NOZZLE_TOP_OD=23"; NOZZLE_TOP_RAD=11 1/2"; NOZZLE_WB/4=7 3/16"; NOZZLE_WB_OD=36"; NOZZLE_WB_RAD=18"; NOZZLE_WB_RAD-2"=16"; P=60"; R=27"; R*1.1=29 11/16"; R+((B/2)+1.5")=43 7/32"; R-((B/2)+1.5")=10 25/32"; TRANSITION=15 1/8"; TRANSITION/2=7 9/16"; Type Comments=Vari-Plume Laboratory Exhaust Centrifugal Airfoil Class 2 Arr 10
- 245_CAVP-15H_CLASS_2: ((M - (2 * (D - L - K - J))) / 2) + (TRANSITION / 2)=17 1/16"; (B/2)+1.5"=16 7/32"; (B/2)-.125"=14 19/32"; (D-J-K-L)*2=2"; (F-((F-H)/2))/2=13 13/16"; (M - (2 * (D - L - K - J)))/2=9 1/2"; (NOZZLE_HEIGHT - (NOZZLE_HEIGHT / 8 * 2)) / 2=16 1/8"; (NOZZLE_WB_OD - NOZZLE_TOP_OD) / 4=3 1/4"; -(F-((F-H)/2))/2=-13 13/16"; A=112 1/4"; A/2=56 1/8"; B=29 7/16"; B/2=14 23/32"; B/4=7 3/8"; C=64 3/4"; C/2=32 3/8"; CLASS=2"; D=54 1/8"; D-L-K-J=1"; D-M=33 1/8"; E=52 7/16"; E/2=26 7/32"; E/52*15=15 1/8"; F=31 5/8"; F/2=15 13/16"; H=29 5/8"; H/2=14 13/16"; HEIGHT=49 29/32"; J=9"; J+K+L=53 1/8"; K=21 1/8"; L=23"; M=21"; M-(2*(D-L-K-J))=19"; N=9 13/32"; N+(H/2)=24 7/32"; NOZZLE_BOTTOM_ID=21 3/8"; NOZZLE_BOTTOM_RAD=10 11/16"; NOZZLE_BOTTOM_RAD-3*2=4 11/16"; NOZZLE_HEIGHT=43"; NOZZLE_HEIGHT/7*2=10 3/4"; NOZZLE_SIZE=15"; NOZZLE_TOP_OD=23"; NOZZLE_TOP_RAD=11 1/2"; NOZZLE_WB/4=7 3/16"; NOZZLE_WB_OD=36"; NOZZLE_WB_RAD=18"; NOZZLE_WB_RAD-2"=16"; P=60"; R=27"; R*1.1=29 11/16"; R+((B/2)+1.5")=43 7/32"; R-((B/2)+1.5")=10 25/32"; TRANSITION=15 1/8"; TRANSITION/2=7 9/16"; Type Comments=Vari-Plume Laboratory Exhaust Centrifugal Airfoil Class 2 Arr 10
- 245_CAVP-18L_CLASS_2: ((M - (2 * (D - L - K - J))) / 2) + (TRANSITION / 2)=18 9/16"; (B/2)+1.5"=16 7/32"; (B/2)-.125"=14 19/32"; (D-J-K-L)*2=2"; (F-((F-H)/2))/2=13 13/16"; (M - (2 * (D - L - K - J)))/2=9 1/2"; (NOZZLE_HEIGHT - (NOZZLE_HEIGHT / 8 * 2)) / 2=18"; (NOZZLE_WB_OD - NOZZLE_TOP_OD) / 4=3 7/8"; -(F-((F-H)/2))/2=-13 13/16"; A=112 1/4"; A/2=56 1/8"; B=29 7/16"; B/2=14 23/32"; B/4=7 3/8"; C=64 3/4"; C/2=32 3/8"; CLASS=2"; D=54 1/8"; D-L-K-J=1"; D-M=33 1/8"; E=52 7/16"; E/2=26 7/32"; E/52*15=15 1/8"; F=31 5/8"; F/2=15 13/16"; H=29 5/8"; H/2=14 13/16"; HEIGHT=49 29/32"; J=9"; J+K+L=53 1/8"; K=21 1/8"; L=23"; M=21"; M-(2*(D-L-K-J))=19"; N=9 13/32"; N+(H/2)=24 7/32"; NOZZLE_BOTTOM_ID=25 5/8"; NOZZLE_BOTTOM_RAD=12 13/16"; NOZZLE_BOTTOM_RAD-3*2=6 13/16"; NOZZLE_HEIGHT=48"; NOZZLE_HEIGHT/7*2=12"; NOZZLE_SIZE=18"; NOZZLE_TOP_OD=27 1/2"; NOZZLE_TOP_RAD=13 3/4"; NOZZLE_WB/4=8 19/32"; NOZZLE_WB_OD=43"; NOZZLE_WB_RAD=21 1/2"; NOZZLE_WB_RAD-2"=19 1/2"; P=60"; R=27"; R*1.1=29 11/16"; R+((B/2)+1.5")=43 7/32"; R-((B/2)+1.5")=10 25/32"; TRANSITION=18 1/8"; TRANSITION/2=9 1/16"; Type Comments=Vari-Plume Laboratory Exhaust Centrifugal Airfoil Class 2 Arr 10
- 245_CAVP-18H_CLASS_2: ((M - (2 * (D - L - K - J))) / 2) + (TRANSITION / 2)=18 9/16"; (B/2)+1.5"=16 7/32"; (B/2)-.125"=14 19/32"; (D-J-K-L)*2=2"; (F-((F-H)/2))/2=13 13/16"; (M - (2 * (D - L - K - J)))/2=9 1/2"; (NOZZLE_HEIGHT - (NOZZLE_HEIGHT / 8 * 2)) / 2=18"; (NOZZLE_WB_OD - NOZZLE_TOP_OD) / 4=3 7/8"; -(F-((F-H)/2))/2=-13 13/16"; A=112 1/4"; A/2=56 1/8"; B=29 7/16"; B/2=14 23/32"; B/4=7 3/8"; C=64 3/4"; C/2=32 3/8"; CLASS=2"; D=54 1/8"; D-L-K-J=1"; D-M=33 1/8"; E=52 7/16"; E/2=26 7/32"; E/52*15=15 1/8"; F=31 5/8"; F/2=15 13/16"; H=29 5/8"; H/2=14 13/16"; HEIGHT=49 29/32"; J=9"; J+K+L=53 1/8"; K=21 1/8"; L=23"; M=21"; M-(2*(D-L-K-J))=19"; N=9 13/32"; N+(H/2)=24 7/32"; NOZZLE_BOTTOM_ID=25 5/8"; NOZZLE_BOTTOM_RAD=12 13/16"; NOZZLE_BOTTOM_RAD-3*2=6 13/16"; NOZZLE_HEIGHT=48"; NOZZLE_HEIGHT/7*2=12"; NOZZLE_SIZE=18"; NOZZLE_TOP_OD=27 1/2"; NOZZLE_TOP_RAD=13 3/4"; NOZZLE_WB/4=8 19/32"; NOZZLE_WB_OD=43"; NOZZLE_WB_RAD=21 1/2"; NOZZLE_WB_RAD-2"=19 1/2"; P=60"; R=27"; R*1.1=29 11/16"; R+((B/2)+1.5")=43 7/32"; R-((B/2)+1.5")=10 25/32"; TRANSITION=18 1/8"; TRANSITION/2=9 1/16"; Type Comments=Vari-Plume Laboratory Exhaust Centrifugal Airfoil Class 2 Arr 10
- 270_CAVP-12L_CLASS_1: ((M - (2 * (D - L - K - J))) / 2) + (TRANSITION / 2)=16 15/32"; (B/2)+1.5"=17 15/32"; (B/2)-.125"=15 27/32"; (D-J-K-L)*2=2"; (F-((F-H)/2))/2=15 3/16"; (M - (2 * (D - L - K - J)))/2=10 7/16"; (NOZZLE_HEIGHT - (NOZZLE_HEIGHT / 8 * 2)) / 2=12"; (NOZZLE_WB_OD - NOZZLE_TOP_OD) / 4=2 1/8"; -(F-((F-H)/2))/2=-15 3/16"; A=116 7/16"; A/2=58 7/32"; B=31 15/16"; B/2=15 31/32"; B/4=8"; C=68 15/16"; C/2=34 15/32"; CLASS=1"; D=54 1/2"; D-L-K-J=1"; D-M=31 5/8"; E=57 9/16"; E/2=28 25/32"; E/52*15=16 19/32"; F=34 3/8"; F/2=17 3/16"; H=32 3/8"; H/2=16 3/16"; HEIGHT=52 1/8"; J=9 1/2"; J+K+L=53 1/2"; K=19 1/8"; L=24 7/8"; M=22 7/8"; M-(2*(D-L-K-J))=20 7/8"; N=10 19/32"; N+(H/2)=26 25/32"; NOZZLE_BOTTOM_ID=17 1/16"; NOZZLE_BOTTOM_RAD=8 17/32"; NOZZLE_BOTTOM_RAD-3*2=2 17/32"; NOZZLE_HEIGHT=32"; NOZZLE_HEIGHT/7*2=8"; NOZZLE_SIZE=12"; NOZZLE_TOP_OD=19 1/2"; NOZZLE_TOP_RAD=9 3/4"; NOZZLE_WB/4=5 19/32"; NOZZLE_WB_OD=28"; NOZZLE_WB_RAD=14"; NOZZLE_WB_RAD-2"=12"; P=60"; R=27"; R*1.1=29 11/16"; R+((B/2)+1.5")=44 15/32"; R-((B/2)+1.5")=9 17/32"; TRANSITION=12 1/16"; TRANSITION/2=6 1/32"; Type Comments=Vari-Plume Laboratory Exhaust Centrifugal Airfoil Class 1 Arr 10
- 270_CAVP-12H_CLASS_1: ((M - (2 * (D - L - K - J))) / 2) + (TRANSITION / 2)=16 15/32"; (B/2)+1.5"=17 15/32"; (B/2)-.125"=15 27/32"; (D-J-K-L)*2=2"; (F-((F-H)/2))/2=15 3/16"; (M - (2 * (D - L - K - J)))/2=10 7/16"; (NOZZLE_HEIGHT - (NOZZLE_HEIGHT / 8 * 2)) / 2=12"; (NOZZLE_WB_OD - NOZZLE_TOP_OD) / 4=2 1/8"; -(F-((F-H)/2))/2=-15 3/16"; A=116 7/16"; A/2=58 7/32"; B=31 15/16"; B/2=15 31/32"; B/4=8"; C=68 15/16"; C/2=34 15/32"; CLASS=1"; D=54 1/2"; D-L-K-J=1"; D-M=31 5/8"; E=57 9/16"; E/2=28 25/32"; E/52*15=16 19/32"; F=34 3/8"; F/2=17 3/16"; H=32 3/8"; H/2=16 3/16"; HEIGHT=52 1/8"; J=9 1/2"; J+K+L=53 1/2"; K=19 1/8"; L=24 7/8"; M=22 7/8"; M-(2*(D-L-K-J))=20 7/8"; N=10 19/32"; N+(H/2)=26 25/32"; NOZZLE_BOTTOM_ID=17 1/16"; NOZZLE_BOTTOM_RAD=8 17/32"; NOZZLE_BOTTOM_RAD-3*2=2 17/32"; NOZZLE_HEIGHT=32"; NOZZLE_HEIGHT/7*2=8"; NOZZLE_SIZE=12"; NOZZLE_TOP_OD=19 1/2"; NOZZLE_TOP_RAD=9 3/4"; NOZZLE_WB/4=5 19/32"; NOZZLE_WB_OD=28"; NOZZLE_WB_RAD=14"; NOZZLE_WB_RAD-2"=12"; P=60"; R=27"; R*1.1=29 11/16"; R+((B/2)+1.5")=44 15/32"; R-((B/2)+1.5")=9 17/32"; TRANSITION=12 1/16"; TRANSITION/2=6 1/32"; Type Comments=Vari-Plume Laboratory Exhaust Centrifugal Airfoil Class 1 Arr 10
- 270_CAVP-15L_CLASS_1: ((M - (2 * (D - L - K - J))) / 2) + (TRANSITION / 2)=18"; (B/2)+1.5"=17 15/32"; (B/2)-.125"=15 27/32"; (D-J-K-L)*2=2"; (F-((F-H)/2))/2=15 3/16"; (M - (2 * (D - L - K - J)))/2=10 7/16"; (NOZZLE_HEIGHT - (NOZZLE_HEIGHT / 8 * 2)) / 2=16 1/8"; (NOZZLE_WB_OD - NOZZLE_TOP_OD) / 4=3 1/4"; -(F-((F-H)/2))/2=-15 3/16"; A=116 7/16"; A/2=58 7/32"; B=31 15/16"; B/2=15 31/32"; B/4=8"; C=68 15/16"; C/2=34 15/32"; CLASS=1"; D=54 1/2"; D-L-K-J=1"; D-M=31 5/8"; E=57 9/16"; E/2=28 25/32"; E/52*15=16 19/32"; F=34 3/8"; F/2=17 3/16"; H=32 3/8"; H/2=16 3/16"; HEIGHT=52 1/8"; J=9 1/2"; J+K+L=53 1/2"; K=19 1/8"; L=24 7/8"; M=22 7/8"; M-(2*(D-L-K-J))=20 7/8"; N=10 19/32"; N+(H/2)=26 25/32"; NOZZLE_BOTTOM_ID=21 3/8"; NOZZLE_BOTTOM_RAD=10 11/16"; NOZZLE_BOTTOM_RAD-3*2=4 11/16"; NOZZLE_HEIGHT=43"; NOZZLE_HEIGHT/7*2=10 3/4"; NOZZLE_SIZE=15"; NOZZLE_TOP_OD=23"; NOZZLE_TOP_RAD=11 1/2"; NOZZLE_WB/4=7 3/16"; NOZZLE_WB_OD=36"; NOZZLE_WB_RAD=18"; NOZZLE_WB_RAD-2"=16"; P=60"; R=27"; R*1.1=29 11/16"; R+((B/2)+1.5")=44 15/32"; R-((B/2)+1.5")=9 17/32"; TRANSITION=15 1/8"; TRANSITION/2=7 9/16"; Type Comments=Vari-Plume Laboratory Exhaust Centrifugal Airfoil Class 1 Arr 10
- 270_CAVP-15H_CLASS_1: ((M - (2 * (D - L - K - J))) / 2) + (TRANSITION / 2)=18"; (B/2)+1.5"=17 15/32"; (B/2)-.125"=15 27/32"; (D-J-K-L)*2=2"; (F-((F-H)/2))/2=15 3/16"; (M - (2 * (D - L - K - J)))/2=10 7/16"; (NOZZLE_HEIGHT - (NOZZLE_HEIGHT / 8 * 2)) / 2=16 1/8"; (NOZZLE_WB_OD - NOZZLE_TOP_OD) / 4=3 1/4"; -(F-((F-H)/2))/2=-15 3/16"; A=116 7/16"; A/2=58 7/32"; B=31 15/16"; B/2=15 31/32"; B/4=8"; C=68 15/16"; C/2=34 15/32"; CLASS=1"; D=54 1/2"; D-L-K-J=1"; D-M=31 5/8"; E=57 9/16"; E/2=28 25/32"; E/52*15=16 19/32"; F=34 3/8"; F/2=17 3/16"; H=32 3/8"; H/2=16 3/16"; HEIGHT=52 1/8"; J=9 1/2"; J+K+L=53 1/2"; K=19 1/8"; L=24 7/8"; M=22 7/8"; M-(2*(D-L-K-J))=20 7/8"; N=10 19/32"; N+(H/2)=26 25/32"; NOZZLE_BOTTOM_ID=21 3/8"; NOZZLE_BOTTOM_RAD=10 11/16"; NOZZLE_BOTTOM_RAD-3*2=4 11/16"; NOZZLE_HEIGHT=43"; NOZZLE_HEIGHT/7*2=10 3/4"; NOZZLE_SIZE=15"; NOZZLE_TOP_OD=23"; NOZZLE_TOP_RAD=11 1/2"; NOZZLE_WB/4=7 3/16"; NOZZLE_WB_OD=36"; NOZZLE_WB_RAD=18"; NOZZLE_WB_RAD-2"=16"; P=60"; R=27"; R*1.1=29 11/16"; R+((B/2)+1.5")=44 15/32"; R-((B/2)+1.5")=9 17/32"; TRANSITION=15 1/8"; TRANSITION/2=7 9/16"; Type Comments=Vari-Plume Laboratory Exhaust Centrifugal Airfoil Class 1 Arr 10
- 270_CAVP-18L_CLASS_1: ((M - (2 * (D - L - K - J))) / 2) + (TRANSITION / 2)=19 1/2"; (B/2)+1.5"=17 15/32"; (B/2)-.125"=15 27/32"; (D-J-K-L)*2=2"; (F-((F-H)/2))/2=15 3/16"; (M - (2 * (D - L - K - J)))/2=10 7/16"; (NOZZLE_HEIGHT - (NOZZLE_HEIGHT / 8 * 2)) / 2=18"; (NOZZLE_WB_OD - NOZZLE_TOP_OD) / 4=3 7/8"; -(F-((F-H)/2))/2=-15 3/16"; A=116 7/16"; A/2=58 7/32"; B=31 15/16"; B/2=15 31/32"; B/4=8"; C=68 15/16"; C/2=34 15/32"; CLASS=1"; D=54 1/2"; D-L-K-J=1"; D-M=31 5/8"; E=57 9/16"; E/2=28 25/32"; E/52*15=16 19/32"; F=34 3/8"; F/2=17 3/16"; H=32 3/8"; H/2=16 3/16"; HEIGHT=52 1/8"; J=9 1/2"; J+K+L=53 1/2"; K=19 1/8"; L=24 7/8"; M=22 7/8"; M-(2*(D-L-K-J))=20 7/8"; N=10 19/32"; N+(H/2)=26 25/32"; NOZZLE_BOTTOM_ID=25 5/8"; NOZZLE_BOTTOM_RAD=12 13/16"; NOZZLE_BOTTOM_RAD-3*2=6 13/16"; NOZZLE_HEIGHT=48"; NOZZLE_HEIGHT/7*2=12"; NOZZLE_SIZE=18"; NOZZLE_TOP_OD=27 1/2"; NOZZLE_TOP_RAD=13 3/4"; NOZZLE_WB/4=8 19/32"; NOZZLE_WB_OD=43"; NOZZLE_WB_RAD=21 1/2"; NOZZLE_WB_RAD-2"=19 1/2"; P=60"; R=27"; R*1.1=29 11/16"; R+((B/2)+1.5")=44 15/32"; R-((B/2)+1.5")=9 17/32"; TRANSITION=18 1/8"; TRANSITION/2=9 1/16"; Type Comments=Vari-Plume Laboratory Exhaust Centrifugal Airfoil Class 1 Arr 10
- 270_CAVP-18H_CLASS_1: ((M - (2 * (D - L - K - J))) / 2) + (TRANSITION / 2)=19 1/2"; (B/2)+1.5"=17 15/32"; (B/2)-.125"=15 27/32"; (D-J-K-L)*2=2"; (F-((F-H)/2))/2=15 3/16"; (M - (2 * (D - L - K - J)))/2=10 7/16"; (NOZZLE_HEIGHT - (NOZZLE_HEIGHT / 8 * 2)) / 2=18"; (NOZZLE_WB_OD - NOZZLE_TOP_OD) / 4=3 7/8"; -(F-((F-H)/2))/2=-15 3/16"; A=116 7/16"; A/2=58 7/32"; B=31 15/16"; B/2=15 31/32"; B/4=8"; C=68 15/16"; C/2=34 15/32"; CLASS=1"; D=54 1/2"; D-L-K-J=1"; D-M=31 5/8"; E=57 9/16"; E/2=28 25/32"; E/52*15=16 19/32"; F=34 3/8"; F/2=17 3/16"; H=32 3/8"; H/2=16 3/16"; HEIGHT=52 1/8"; J=9 1/2"; J+K+L=53 1/2"; K=19 1/8"; L=24 7/8"; M=22 7/8"; M-(2*(D-L-K-J))=20 7/8"; N=10 19/32"; N+(H/2)=26 25/32"; NOZZLE_BOTTOM_ID=25 5/8"; NOZZLE_BOTTOM_RAD=12 13/16"; NOZZLE_BOTTOM_RAD-3*2=6 13/16"; NOZZLE_HEIGHT=48"; NOZZLE_HEIGHT/7*2=12"; NOZZLE_SIZE=18"; NOZZLE_TOP_OD=27 1/2"; NOZZLE_TOP_RAD=13 3/4"; NOZZLE_WB/4=8 19/32"; NOZZLE_WB_OD=43"; NOZZLE_WB_RAD=21 1/2"; NOZZLE_WB_RAD-2"=19 1/2"; P=60"; R=27"; R*1.1=29 11/16"; R+((B/2)+1.5")=44 15/32"; R-((B/2)+1.5")=9 17/32"; TRANSITION=18 1/8"; TRANSITION/2=9 1/16"; Type Comments=Vari-Plume Laboratory Exhaust Centrifugal Airfoil Class 1 Arr 10
- 270_CAVP-12L_CLASS_2: ((M - (2 * (D - L - K - J))) / 2) + (TRANSITION / 2)=16 15/32"; (B/2)+1.5"=17 15/32"; (B/2)-.125"=15 27/32"; (D-J-K-L)*2=2"; (F-((F-H)/2))/2=15 3/16"; (M - (2 * (D - L - K - J)))/2=10 7/16"; (NOZZLE_HEIGHT - (NOZZLE_HEIGHT / 8 * 2)) / 2=12"; (NOZZLE_WB_OD - NOZZLE_TOP_OD) / 4=2 1/8"; -(F-((F-H)/2))/2=-15 3/16"; A=116 7/16"; A/2=58 7/32"; B=31 15/16"; B/2=15 31/32"; B/4=8"; C=68 15/16"; C/2=34 15/32"; CLASS=2"; D=56 1/2"; D-L-K-J=1"; D-M=33 5/8"; E=57 9/16"; E/2=28 25/32"; E/52*15=16 19/32"; F=34 3/8"; F/2=17 3/16"; H=32 3/8"; H/2=16 3/16"; HEIGHT=52 1/8"; J=9 1/4"; J+K+L=55 1/2"; K=21 3/8"; L=24 7/8"; M=22 7/8"; M-(2*(D-L-K-J))=20 7/8"; N=10"; N+(H/2)=26 3/16"; NOZZLE_BOTTOM_ID=17 1/16"; NOZZLE_BOTTOM_RAD=8 17/32"; NOZZLE_BOTTOM_RAD-3*2=2 17/32"; NOZZLE_HEIGHT=32"; NOZZLE_HEIGHT/7*2=8"; NOZZLE_SIZE=12"; NOZZLE_TOP_OD=19 1/2"; NOZZLE_TOP_RAD=9 3/4"; NOZZLE_WB/4=5 19/32"; NOZZLE_WB_OD=28"; NOZZLE_WB_RAD=14"; NOZZLE_WB_RAD-2"=12"; P=60"; R=27"; R*1.1=29 11/16"; R+((B/2)+1.5")=44 15/32"; R-((B/2)+1.5")=9 17/32"; TRANSITION=12 1/16"; TRANSITION/2=6 1/32"; Type Comments=Vari-Plume Laboratory Exhaust Centrifugal Airfoil Class 2 Arr 10
- 270_CAVP-12H_CLASS_2: ((M - (2 * (D - L - K - J))) / 2) + (TRANSITION / 2)=16 15/32"; (B/2)+1.5"=17 15/32"; (B/2)-.125"=15 27/32"; (D-J-K-L)*2=2"; (F-((F-H)/2))/2=15 3/16"; (M - (2 * (D - L - K - J)))/2=10 7/16"; (NOZZLE_HEIGHT - (NOZZLE_HEIGHT / 8 * 2)) / 2=12"; (NOZZLE_WB_OD - NOZZLE_TOP_OD) / 4=2 1/8"; -(F-((F-H)/2))/2=-15 3/16"; A=116 7/16"; A/2=58 7/32"; B=31 15/16"; B/2=15 31/32"; B/4=8"; C=68 15/16"; C/2=34 15/32"; CLASS=2"; D=56 1/2"; D-L-K-J=1"; D-M=33 5/8"; E=57 9/16"; E/2=28 25/32"; E/52*15=16 19/32"; F=34 3/8"; F/2=17 3/16"; H=32 3/8"; H/2=16 3/16"; HEIGHT=52 1/8"; J=9 1/4"; J+K+L=55 1/2"; K=21 3/8"; L=24 7/8"; M=22 7/8"; M-(2*(D-L-K-J))=20 7/8"; N=10"; N+(H/2)=26 3/16"; NOZZLE_BOTTOM_ID=17 1/16"; NOZZLE_BOTTOM_RAD=8 17/32"; NOZZLE_BOTTOM_RAD-3*2=2 17/32"; NOZZLE_HEIGHT=32"; NOZZLE_HEIGHT/7*2=8"; NOZZLE_SIZE=12"; NOZZLE_TOP_OD=19 1/2"; NOZZLE_TOP_RAD=9 3/4"; NOZZLE_WB/4=5 19/32"; NOZZLE_WB_OD=28"; NOZZLE_WB_RAD=14"; NOZZLE_WB_RAD-2"=12"; P=60"; R=27"; R*1.1=29 11/16"; R+((B/2)+1.5")=44 15/32"; R-((B/2)+1.5")=9 17/32"; TRANSITION=12 1/16"; TRANSITION/2=6 1/32"; Type Comments=Vari-Plume Laboratory Exhaust Centrifugal Airfoil Class 2 Arr 10
- 270_CAVP-15L_CLASS_2: ((M - (2 * (D - L - K - J))) / 2) + (TRANSITION / 2)=18"; (B/2)+1.5"=17 15/32"; (B/2)-.125"=15 27/32"; (D-J-K-L)*2=2"; (F-((F-H)/2))/2=15 3/16"; (M - (2 * (D - L - K - J)))/2=10 7/16"; (NOZZLE_HEIGHT - (NOZZLE_HEIGHT / 8 * 2)) / 2=16 1/8"; (NOZZLE_WB_OD - NOZZLE_TOP_OD) / 4=3 1/4"; -(F-((F-H)/2))/2=-15 3/16"; A=116 7/16"; A/2=58 7/32"; B=31 15/16"; B/2=15 31/32"; B/4=8"; C=68 15/16"; C/2=34 15/32"; CLASS=2"; D=56 1/2"; D-L-K-J=1"; D-M=33 5/8"; E=57 9/16"; E/2=28 25/32"; E/52*15=16 19/32"; F=34 3/8"; F/2=17 3/16"; H=32 3/8"; H/2=16 3/16"; HEIGHT=52 1/8"; J=9 1/4"; J+K+L=55 1/2"; K=21 3/8"; L=24 7/8"; M=22 7/8"; M-(2*(D-L-K-J))=20 7/8"; N=10"; N+(H/2)=26 3/16"; NOZZLE_BOTTOM_ID=21 3/8"; NOZZLE_BOTTOM_RAD=10 11/16"; NOZZLE_BOTTOM_RAD-3*2=4 11/16"; NOZZLE_HEIGHT=43"; NOZZLE_HEIGHT/7*2=10 3/4"; NOZZLE_SIZE=15"; NOZZLE_TOP_OD=23"; NOZZLE_TOP_RAD=11 1/2"; NOZZLE_WB/4=7 3/16"; NOZZLE_WB_OD=36"; NOZZLE_WB_RAD=18"; NOZZLE_WB_RAD-2"=16"; P=60"; R=27"; R*1.1=29 11/16"; R+((B/2)+1.5")=44 15/32"; R-((B/2)+1.5")=9 17/32"; TRANSITION=15 1/8"; TRANSITION/2=7 9/16"; Type Comments=Vari-Plume Laboratory Exhaust Centrifugal Airfoil Class 2 Arr 10
- 270_CAVP-15H_CLASS_2: ((M - (2 * (D - L - K - J))) / 2) + (TRANSITION / 2)=18"; (B/2)+1.5"=17 15/32"; (B/2)-.125"=15 27/32"; (D-J-K-L)*2=2"; (F-((F-H)/2))/2=15 3/16"; (M - (2 * (D - L - K - J)))/2=10 7/16"; (NOZZLE_HEIGHT - (NOZZLE_HEIGHT / 8 * 2)) / 2=16 1/8"; (NOZZLE_WB_OD - NOZZLE_TOP_OD) / 4=3 1/4"; -(F-((F-H)/2))/2=-15 3/16"; A=116 7/16"; A/2=58 7/32"; B=31 15/16"; B/2=15 31/32"; B/4=8"; C=68 15/16"; C/2=34 15/32"; CLASS=2"; D=56 1/2"; D-L-K-J=1"; D-M=33 5/8"; E=57 9/16"; E/2=28 25/32"; E/52*15=16 19/32"; F=34 3/8"; F/2=17 3/16"; H=32 3/8"; H/2=16 3/16"; HEIGHT=52 1/8"; J=9 1/4"; J+K+L=55 1/2"; K=21 3/8"; L=24 7/8"; M=22 7/8"; M-(2*(D-L-K-J))=20 7/8"; N=10"; N+(H/2)=26 3/16"; NOZZLE_BOTTOM_ID=21 3/8"; NOZZLE_BOTTOM_RAD=10 11/16"; NOZZLE_BOTTOM_RAD-3*2=4 11/16"; NOZZLE_HEIGHT=43"; NOZZLE_HEIGHT/7*2=10 3/4"; NOZZLE_SIZE=15"; NOZZLE_TOP_OD=23"; NOZZLE_TOP_RAD=11 1/2"; NOZZLE_WB/4=7 3/16"; NOZZLE_WB_OD=36"; NOZZLE_WB_RAD=18"; NOZZLE_WB_RAD-2"=16"; P=60"; R=27"; R*1.1=29 11/16"; R+((B/2)+1.5")=44 15/32"; R-((B/2)+1.5")=9 17/32"; TRANSITION=15 1/8"; TRANSITION/2=7 9/16"; Type Comments=Vari-Plume Laboratory Exhaust Centrifugal Airfoil Class 2 Arr 10
- 270_CAVP-18L_CLASS_2: ((M - (2 * (D - L - K - J))) / 2) + (TRANSITION / 2)=19 1/2"; (B/2)+1.5"=17 15/32"; (B/2)-.125"=15 27/32"; (D-J-K-L)*2=2"; (F-((F-H)/2))/2=15 3/16"; (M - (2 * (D - L - K - J)))/2=10 7/16"; (NOZZLE_HEIGHT - (NOZZLE_HEIGHT / 8 * 2)) / 2=18"; (NOZZLE_WB_OD - NOZZLE_TOP_OD) / 4=3 7/8"; -(F-((F-H)/2))/2=-15 3/16"; A=116 7/16"; A/2=58 7/32"; B=31 15/16"; B/2=15 31/32"; B/4=8"; C=68 15/16"; C/2=34 15/32"; CLASS=2"; D=56 1/2"; D-L-K-J=1"; D-M=33 5/8"; E=57 9/16"; E/2=28 25/32"; E/52*15=16 19/32"; F=34 3/8"; F/2=17 3/16"; H=32 3/8"; H/2=16 3/16"; HEIGHT=52 1/8"; J=9 1/4"; J+K+L=55 1/2"; K=21 3/8"; L=24 7/8"; M=22 7/8"; M-(2*(D-L-K-J))=20 7/8"; N=10"; N+(H/2)=26 3/16"; NOZZLE_BOTTOM_ID=25 5/8"; NOZZLE_BOTTOM_RAD=12 13/16"; NOZZLE_BOTTOM_RAD-3*2=6 13/16"; NOZZLE_HEIGHT=48"; NOZZLE_HEIGHT/7*2=12"; NOZZLE_SIZE=18"; NOZZLE_TOP_OD=27 1/2"; NOZZLE_TOP_RAD=13 3/4"; NOZZLE_WB/4=8 19/32"; NOZZLE_WB_OD=43"; NOZZLE_WB_RAD=21 1/2"; NOZZLE_WB_RAD-2"=19 1/2"; P=60"; R=27"; R*1.1=29 11/16"; R+((B/2)+1.5")=44 15/32"; R-((B/2)+1.5")=9 17/32"; TRANSITION=18 1/8"; TRANSITION/2=9 1/16"; Type Comments=Vari-Plume Laboratory Exhaust Centrifugal Airfoil Class 2 Arr 10
- 270_CAVP-18H_CLASS_2: ((M - (2 * (D - L - K - J))) / 2) + (TRANSITION / 2)=19 1/2"; (B/2)+1.5"=17 15/32"; (B/2)-.125"=15 27/32"; (D-J-K-L)*2=2"; (F-((F-H)/2))/2=15 3/16"; (M - (2 * (D - L - K - J)))/2=10 7/16"; (NOZZLE_HEIGHT - (NOZZLE_HEIGHT / 8 * 2)) / 2=18"; (NOZZLE_WB_OD - NOZZLE_TOP_OD) / 4=3 7/8"; -(F-((F-H)/2))/2=-15 3/16"; A=116 7/16"; A/2=58 7/32"; B=31 15/16"; B/2=15 31/32"; B/4=8"; C=68 15/16"; C/2=34 15/32"; CLASS=2"; D=56 1/2"; D-L-K-J=1"; D-M=33 5/8"; E=57 9/16"; E/2=28 25/32"; E/52*15=16 19/32"; F=34 3/8"; F/2=17 3/16"; H=32 3/8"; H/2=16 3/16"; HEIGHT=52 1/8"; J=9 1/4"; J+K+L=55 1/2"; K=21 3/8"; L=24 7/8"; M=22 7/8"; M-(2*(D-L-K-J))=20 7/8"; N=10"; N+(H/2)=26 3/16"; NOZZLE_BOTTOM_ID=25 5/8"; NOZZLE_BOTTOM_RAD=12 13/16"; NOZZLE_BOTTOM_RAD-3*2=6 13/16"; NOZZLE_HEIGHT=48"; NOZZLE_HEIGHT/7*2=12"; NOZZLE_SIZE=18"; NOZZLE_TOP_OD=27 1/2"; NOZZLE_TOP_RAD=13 3/4"; NOZZLE_WB/4=8 19/32"; NOZZLE_WB_OD=43"; NOZZLE_WB_RAD=21 1/2"; NOZZLE_WB_RAD-2"=19 1/2"; P=60"; R=27"; R*1.1=29 11/16"; R+((B/2)+1.5")=44 15/32"; R-((B/2)+1.5")=9 17/32"; TRANSITION=18 1/8"; TRANSITION/2=9 1/16"; Type Comments=Vari-Plume Laboratory Exhaust Centrifugal Airfoil Class 2 Arr 10
- 300_CAVP-12L_CLASS_1: ((M - (2 * (D - L - K - J))) / 2) + (TRANSITION / 2)=17 5/8"; (B/2)+1.5"=18 31/32"; (B/2)-.125"=17 11/32"; (D-J-K-L)*2=2"; (F-((F-H)/2))/2=16 11/16"; (M - (2 * (D - L - K - J)))/2=11 19/32"; (NOZZLE_HEIGHT - (NOZZLE_HEIGHT / 8 * 2)) / 2=12"; (NOZZLE_WB_OD - NOZZLE_TOP_OD) / 4=2 1/8"; -(F-((F-H)/2))/2=-16 11/16"; A=122 7/16"; A/2=61 7/32"; B=34 15/16"; B/2=17 15/32"; B/4=8 3/4"; C=74 15/16"; C/2=37 15/32"; CLASS=1"; D=57 5/16"; D-L-K-J=1"; D-M=32 1/8"; E=63 3/4"; E/2=31 7/8"; E/52*15=18 3/8"; F=37 3/8"; F/2=18 11/16"; H=35 3/8"; H/2=17 11/16"; HEIGHT=57 27/32"; J=10"; J+K+L=56 5/16"; K=19 1/8"; L=27 3/16"; M=25 3/16"; M-(2*(D-L-K-J))=23 3/16"; N=12 3/16"; N+(H/2)=29 7/8"; NOZZLE_BOTTOM_ID=17 1/16"; NOZZLE_BOTTOM_RAD=8 17/32"; NOZZLE_BOTTOM_RAD-3*2=2 17/32"; NOZZLE_HEIGHT=32"; NOZZLE_HEIGHT/7*2=8"; NOZZLE_SIZE=12"; NOZZLE_TOP_OD=19 1/2"; NOZZLE_TOP_RAD=9 3/4"; NOZZLE_WB/4=5 19/32"; NOZZLE_WB_OD=28"; NOZZLE_WB_RAD=14"; NOZZLE_WB_RAD-2"=12"; P=60"; R=30"; R*1.1=33"; R+((B/2)+1.5")=48 31/32"; R-((B/2)+1.5")=11 1/32"; TRANSITION=12 1/16"; TRANSITION/2=6 1/32"; Type Comments=Vari-Plume Laboratory Exhaust Centrifugal Airfoil Class 1 Arr 10
- 300_CAVP-12H_CLASS_1: ((M - (2 * (D - L - K - J))) / 2) + (TRANSITION / 2)=17 5/8"; (B/2)+1.5"=18 31/32"; (B/2)-.125"=17 11/32"; (D-J-K-L)*2=2"; (F-((F-H)/2))/2=16 11/16"; (M - (2 * (D - L - K - J)))/2=11 19/32"; (NOZZLE_HEIGHT - (NOZZLE_HEIGHT / 8 * 2)) / 2=12"; (NOZZLE_WB_OD - NOZZLE_TOP_OD) / 4=2 1/8"; -(F-((F-H)/2))/2=-16 11/16"; A=122 7/16"; A/2=61 7/32"; B=34 15/16"; B/2=17 15/32"; B/4=8 3/4"; C=74 15/16"; C/2=37 15/32"; CLASS=1"; D=57 5/16"; D-L-K-J=1"; D-M=32 1/8"; E=63 3/4"; E/2=31 7/8"; E/52*15=18 3/8"; F=37 3/8"; F/2=18 11/16"; H=35 3/8"; H/2=17 11/16"; HEIGHT=57 27/32"; J=10"; J+K+L=56 5/16"; K=19 1/8"; L=27 3/16"; M=25 3/16"; M-(2*(D-L-K-J))=23 3/16"; N=12 3/16"; N+(H/2)=29 7/8"; NOZZLE_BOTTOM_ID=17 1/16"; NOZZLE_BOTTOM_RAD=8 17/32"; NOZZLE_BOTTOM_RAD-3*2=2 17/32"; NOZZLE_HEIGHT=32"; NOZZLE_HEIGHT/7*2=8"; NOZZLE_SIZE=12"; NOZZLE_TOP_OD=19 1/2"; NOZZLE_TOP_RAD=9 3/4"; NOZZLE_WB/4=5 19/32"; NOZZLE_WB_OD=28"; NOZZLE_WB_RAD=14"; NOZZLE_WB_RAD-2"=12"; P=60"; R=30"; R*1.1=33"; R+((B/2)+1.5")=48 31/32"; R-((B/2)+1.5")=11 1/32"; TRANSITION=12 1/16"; TRANSITION/2=6 1/32"; Type Comments=Vari-Plume Laboratory Exhaust Centrifugal Airfoil Class 1 Arr 10
- 300_CAVP-15L_CLASS_1: ((M - (2 * (D - L - K - J))) / 2) + (TRANSITION / 2)=19 5/32"; (B/2)+1.5"=18 31/32"; (B/2)-.125"=17 11/32"; (D-J-K-L)*2=2"; (F-((F-H)/2))/2=16 11/16"; (M - (2 * (D - L - K - J)))/2=11 19/32"; (NOZZLE_HEIGHT - (NOZZLE_HEIGHT / 8 * 2)) / 2=16 1/8"; (NOZZLE_WB_OD - NOZZLE_TOP_OD) / 4=3 1/4"; -(F-((F-H)/2))/2=-16 11/16"; A=122 7/16"; A/2=61 7/32"; B=34 15/16"; B/2=17 15/32"; B/4=8 3/4"; C=74 15/16"; C/2=37 15/32"; CLASS=1"; D=57 5/16"; D-L-K-J=1"; D-M=32 1/8"; E=63 3/4"; E/2=31 7/8"; E/52*15=18 3/8"; F=37 3/8"; F/2=18 11/16"; H=35 3/8"; H/2=17 11/16"; HEIGHT=57 27/32"; J=10"; J+K+L=56 5/16"; K=19 1/8"; L=27 3/16"; M=25 3/16"; M-(2*(D-L-K-J))=23 3/16"; N=12 3/16"; N+(H/2)=29 7/8"; NOZZLE_BOTTOM_ID=21 3/8"; NOZZLE_BOTTOM_RAD=10 11/16"; NOZZLE_BOTTOM_RAD-3*2=4 11/16"; NOZZLE_HEIGHT=43"; NOZZLE_HEIGHT/7*2=10 3/4"; NOZZLE_SIZE=15"; NOZZLE_TOP_OD=23"; NOZZLE_TOP_RAD=11 1/2"; NOZZLE_WB/4=7 3/16"; NOZZLE_WB_OD=36"; NOZZLE_WB_RAD=18"; NOZZLE_WB_RAD-2"=16"; P=60"; R=30"; R*1.1=33"; R+((B/2)+1.5")=48 31/32"; R-((B/2)+1.5")=11 1/32"; TRANSITION=15 1/8"; TRANSITION/2=7 9/16"; Type Comments=Vari-Plume Laboratory Exhaust Centrifugal Airfoil Class 1 Arr 10
- 300_CAVP-15H_CLASS_1: ((M - (2 * (D - L - K - J))) / 2) + (TRANSITION / 2)=19 5/32"; (B/2)+1.5"=18 31/32"; (B/2)-.125"=17 11/32"; (D-J-K-L)*2=2"; (F-((F-H)/2))/2=16 11/16"; (M - (2 * (D - L - K - J)))/2=11 19/32"; (NOZZLE_HEIGHT - (NOZZLE_HEIGHT / 8 * 2)) / 2=16 1/8"; (NOZZLE_WB_OD - NOZZLE_TOP_OD) / 4=3 1/4"; -(F-((F-H)/2))/2=-16 11/16"; A=122 7/16"; A/2=61 7/32"; B=34 15/16"; B/2=17 15/32"; B/4=8 3/4"; C=74 15/16"; C/2=37 15/32"; CLASS=1"; D=57 5/16"; D-L-K-J=1"; D-M=32 1/8"; E=63 3/4"; E/2=31 7/8"; E/52*15=18 3/8"; F=37 3/8"; F/2=18 11/16"; H=35 3/8"; H/2=17 11/16"; HEIGHT=57 27/32"; J=10"; J+K+L=56 5/16"; K=19 1/8"; L=27 3/16"; M=25 3/16"; M-(2*(D-L-K-J))=23 3/16"; N=12 3/16"; N+(H/2)=29 7/8"; NOZZLE_BOTTOM_ID=21 3/8"; NOZZLE_BOTTOM_RAD=10 11/16"; NOZZLE_BOTTOM_RAD-3*2=4 11/16"; NOZZLE_HEIGHT=43"; NOZZLE_HEIGHT/7*2=10 3/4"; NOZZLE_SIZE=15"; NOZZLE_TOP_OD=23"; NOZZLE_TOP_RAD=11 1/2"; NOZZLE_WB/4=7 3/16"; NOZZLE_WB_OD=36"; NOZZLE_WB_RAD=18"; NOZZLE_WB_RAD-2"=16"; P=60"; R=30"; R*1.1=33"; R+((B/2)+1.5")=48 31/32"; R-((B/2)+1.5")=11 1/32"; TRANSITION=15 1/8"; TRANSITION/2=7 9/16"; Type Comments=Vari-Plume Laboratory Exhaust Centrifugal Airfoil Class 1 Arr 10
- 300_CAVP-18L_CLASS_1: ((M - (2 * (D - L - K - J))) / 2) + (TRANSITION / 2)=20 21/32"; (B/2)+1.5"=18 31/32"; (B/2)-.125"=17 11/32"; (D-J-K-L)*2=2"; (F-((F-H)/2))/2=16 11/16"; (M - (2 * (D - L - K - J)))/2=11 19/32"; (NOZZLE_HEIGHT - (NOZZLE_HEIGHT / 8 * 2)) / 2=18"; (NOZZLE_WB_OD - NOZZLE_TOP_OD) / 4=3 7/8"; -(F-((F-H)/2))/2=-16 11/16"; A=122 7/16"; A/2=61 7/32"; B=34 15/16"; B/2=17 15/32"; B/4=8 3/4"; C=74 15/16"; C/2=37 15/32"; CLASS=1"; D=57 5/16"; D-L-K-J=1"; D-M=32 1/8"; E=63 3/4"; E/2=31 7/8"; E/52*15=18 3/8"; F=37 3/8"; F/2=18 11/16"; H=35 3/8"; H/2=17 11/16"; HEIGHT=57 27/32"; J=10"; J+K+L=56 5/16"; K=19 1/8"; L=27 3/16"; M=25 3/16"; M-(2*(D-L-K-J))=23 3/16"; N=12 3/16"; N+(H/2)=29 7/8"; NOZZLE_BOTTOM_ID=25 5/8"; NOZZLE_BOTTOM_RAD=12 13/16"; NOZZLE_BOTTOM_RAD-3*2=6 13/16"; NOZZLE_HEIGHT=48"; NOZZLE_HEIGHT/7*2=12"; NOZZLE_SIZE=18"; NOZZLE_TOP_OD=27 1/2"; NOZZLE_TOP_RAD=13 3/4"; NOZZLE_WB/4=8 19/32"; NOZZLE_WB_OD=43"; NOZZLE_WB_RAD=21 1/2"; NOZZLE_WB_RAD-2"=19 1/2"; P=60"; R=30"; R*1.1=33"; R+((B/2)+1.5")=48 31/32"; R-((B/2)+1.5")=11 1/32"; TRANSITION=18 1/8"; TRANSITION/2=9 1/16"; Type Comments=Vari-Plume Laboratory Exhaust Centrifugal Airfoil Class 1 Arr 10
- 300_CAVP-18H_CLASS_1: ((M - (2 * (D - L - K - J))) / 2) + (TRANSITION / 2)=20 21/32"; (B/2)+1.5"=18 31/32"; (B/2)-.125"=17 11/32"; (D-J-K-L)*2=2"; (F-((F-H)/2))/2=16 11/16"; (M - (2 * (D - L - K - J)))/2=11 19/32"; (NOZZLE_HEIGHT - (NOZZLE_HEIGHT / 8 * 2)) / 2=18"; (NOZZLE_WB_OD - NOZZLE_TOP_OD) / 4=3 7/8"; -(F-((F-H)/2))/2=-16 11/16"; A=122 7/16"; A/2=61 7/32"; B=34 15/16"; B/2=17 15/32"; B/4=8 3/4"; C=74 15/16"; C/2=37 15/32"; CLASS=1"; D=57 5/16"; D-L-K-J=1"; D-M=32 1/8"; E=63 3/4"; E/2=31 7/8"; E/52*15=18 3/8"; F=37 3/8"; F/2=18 11/16"; H=35 3/8"; H/2=17 11/16"; HEIGHT=57 27/32"; J=10"; J+K+L=56 5/16"; K=19 1/8"; L=27 3/16"; M=25 3/16"; M-(2*(D-L-K-J))=23 3/16"; N=12 3/16"; N+(H/2)=29 7/8"; NOZZLE_BOTTOM_ID=25 5/8"; NOZZLE_BOTTOM_RAD=12 13/16"; NOZZLE_BOTTOM_RAD-3*2=6 13/16"; NOZZLE_HEIGHT=48"; NOZZLE_HEIGHT/7*2=12"; NOZZLE_SIZE=18"; NOZZLE_TOP_OD=27 1/2"; NOZZLE_TOP_RAD=13 3/4"; NOZZLE_WB/4=8 19/32"; NOZZLE_WB_OD=43"; NOZZLE_WB_RAD=21 1/2"; NOZZLE_WB_RAD-2"=19 1/2"; P=60"; R=30"; R*1.1=33"; R+((B/2)+1.5")=48 31/32"; R-((B/2)+1.5")=11 1/32"; TRANSITION=18 1/8"; TRANSITION/2=9 1/16"; Type Comments=Vari-Plume Laboratory Exhaust Centrifugal Airfoil Class 1 Arr 10
- 300_CAVP-12L_CLASS_2: ((M - (2 * (D - L - K - J))) / 2) + (TRANSITION / 2)=17 5/8"; (B/2)+1.5"=18 31/32"; (B/2)-.125"=17 11/32"; (D-J-K-L)*2=2"; (F-((F-H)/2))/2=16 11/16"; (M - (2 * (D - L - K - J)))/2=11 19/32"; (NOZZLE_HEIGHT - (NOZZLE_HEIGHT / 8 * 2)) / 2=12"; (NOZZLE_WB_OD - NOZZLE_TOP_OD) / 4=2 1/8"; -(F-((F-H)/2))/2=-16 11/16"; A=122 7/16"; A/2=61 7/32"; B=34 15/16"; B/2=17 15/32"; B/4=8 3/4"; C=74 15/16"; C/2=37 15/32"; CLASS=2"; D=61 3/16"; D-L-K-J=1"; D-M=36"; E=63 3/4"; E/2=31 7/8"; E/52*15=18 3/8"; F=37 3/8"; F/2=18 11/16"; H=35 3/8"; H/2=17 11/16"; HEIGHT=57 27/32"; J=10"; J+K+L=60 3/16"; K=23"; L=27 3/16"; M=25 3/16"; M-(2*(D-L-K-J))=23 3/16"; N=12 3/16"; N+(H/2)=29 7/8"; NOZZLE_BOTTOM_ID=17 1/16"; NOZZLE_BOTTOM_RAD=8 17/32"; NOZZLE_BOTTOM_RAD-3*2=2 17/32"; NOZZLE_HEIGHT=32"; NOZZLE_HEIGHT/7*2=8"; NOZZLE_SIZE=12"; NOZZLE_TOP_OD=19 1/2"; NOZZLE_TOP_RAD=9 3/4"; NOZZLE_WB/4=5 19/32"; NOZZLE_WB_OD=28"; NOZZLE_WB_RAD=14"; NOZZLE_WB_RAD-2"=12"; P=18 1/4"; R=30"; R*1.1=33"; R+((B/2)+1.5")=48 31/32"; R-((B/2)+1.5")=11 1/32"; TRANSITION=12 1/16"; TRANSITION/2=6 1/32"; Type Comments=Vari-Plume Laboratory Exhaust Centrifugal Airfoil Class 2 Arr 10
- 300_CAVP-12H_CLASS_2: ((M - (2 * (D - L - K - J))) / 2) + (TRANSITION / 2)=17 5/8"; (B/2)+1.5"=18 31/32"; (B/2)-.125"=17 11/32"; (D-J-K-L)*2=2"; (F-((F-H)/2))/2=16 11/16"; (M - (2 * (D - L - K - J)))/2=11 19/32"; (NOZZLE_HEIGHT - (NOZZLE_HEIGHT / 8 * 2)) / 2=12"; (NOZZLE_WB_OD - NOZZLE_TOP_OD) / 4=2 1/8"; -(F-((F-H)/2))/2=-16 11/16"; A=122 7/16"; A/2=61 7/32"; B=34 15/16"; B/2=17 15/32"; B/4=8 3/4"; C=74 15/16"; C/2=37 15/32"; CLASS=2"; D=61 3/16"; D-L-K-J=1"; D-M=36"; E=63 3/4"; E/2=31 7/8"; E/52*15=18 3/8"; F=37 3/8"; F/2=18 11/16"; H=35 3/8"; H/2=17 11/16"; HEIGHT=57 27/32"; J=10"; J+K+L=60 3/16"; K=23"; L=27 3/16"; M=25 3/16"; M-(2*(D-L-K-J))=23 3/16"; N=12 3/16"; N+(H/2)=29 7/8"; NOZZLE_BOTTOM_ID=17 1/16"; NOZZLE_BOTTOM_RAD=8 17/32"; NOZZLE_BOTTOM_RAD-3*2=2 17/32"; NOZZLE_HEIGHT=32"; NOZZLE_HEIGHT/7*2=8"; NOZZLE_SIZE=12"; NOZZLE_TOP_OD=19 1/2"; NOZZLE_TOP_RAD=9 3/4"; NOZZLE_WB/4=5 19/32"; NOZZLE_WB_OD=28"; NOZZLE_WB_RAD=14"; NOZZLE_WB_RAD-2"=12"; P=18 1/4"; R=30"; R*1.1=33"; R+((B/2)+1.5")=48 31/32"; R-((B/2)+1.5")=11 1/32"; TRANSITION=12 1/16"; TRANSITION/2=6 1/32"; Type Comments=Vari-Plume Laboratory Exhaust Centrifugal Airfoil Class 2 Arr 10
- 300_CAVP-15L_CLASS_2: ((M - (2 * (D - L - K - J))) / 2) + (TRANSITION / 2)=19 5/32"; (B/2)+1.5"=18 31/32"; (B/2)-.125"=17 11/32"; (D-J-K-L)*2=2"; (F-((F-H)/2))/2=16 11/16"; (M - (2 * (D - L - K - J)))/2=11 19/32"; (NOZZLE_HEIGHT - (NOZZLE_HEIGHT / 8 * 2)) / 2=16 1/8"; (NOZZLE_WB_OD - NOZZLE_TOP_OD) / 4=3 1/4"; -(F-((F-H)/2))/2=-16 11/16"; A=122 7/16"; A/2=61 7/32"; B=34 15/16"; B/2=17 15/32"; B/4=8 3/4"; C=74 15/16"; C/2=37 15/32"; CLASS=2"; D=61 3/16"; D-L-K-J=1"; D-M=36"; E=63 3/4"; E/2=31 7/8"; E/52*15=18 3/8"; F=37 3/8"; F/2=18 11/16"; H=35 3/8"; H/2=17 11/16"; HEIGHT=57 27/32"; J=10"; J+K+L=60 3/16"; K=23"; L=27 3/16"; M=25 3/16"; M-(2*(D-L-K-J))=23 3/16"; N=12 3/16"; N+(H/2)=29 7/8"; NOZZLE_BOTTOM_ID=21 3/8"; NOZZLE_BOTTOM_RAD=10 11/16"; NOZZLE_BOTTOM_RAD-3*2=4 11/16"; NOZZLE_HEIGHT=43"; NOZZLE_HEIGHT/7*2=10 3/4"; NOZZLE_SIZE=15"; NOZZLE_TOP_OD=23"; NOZZLE_TOP_RAD=11 1/2"; NOZZLE_WB/4=7 3/16"; NOZZLE_WB_OD=36"; NOZZLE_WB_RAD=18"; NOZZLE_WB_RAD-2"=16"; P=18 1/4"; R=30"; R*1.1=33"; R+((B/2)+1.5")=48 31/32"; R-((B/2)+1.5")=11 1/32"; TRANSITION=15 1/8"; TRANSITION/2=7 9/16"; Type Comments=Vari-Plume Laboratory Exhaust Centrifugal Airfoil Class 2 Arr 10
- 300_CAVP-15H_CLASS_2: ((M - (2 * (D - L - K - J))) / 2) + (TRANSITION / 2)=19 5/32"; (B/2)+1.5"=18 31/32"; (B/2)-.125"=17 11/32"; (D-J-K-L)*2=2"; (F-((F-H)/2))/2=16 11/16"; (M - (2 * (D - L - K - J)))/2=11 19/32"; (NOZZLE_HEIGHT - (NOZZLE_HEIGHT / 8 * 2)) / 2=16 1/8"; (NOZZLE_WB_OD - NOZZLE_TOP_OD) / 4=3 1/4"; -(F-((F-H)/2))/2=-16 11/16"; A=122 7/16"; A/2=61 7/32"; B=34 15/16"; B/2=17 15/32"; B/4=8 3/4"; C=74 15/16"; C/2=37 15/32"; CLASS=2"; D=61 3/16"; D-L-K-J=1"; D-M=36"; E=63 3/4"; E/2=31 7/8"; E/52*15=18 3/8"; F=37 3/8"; F/2=18 11/16"; H=35 3/8"; H/2=17 11/16"; HEIGHT=57 27/32"; J=10"; J+K+L=60 3/16"; K=23"; L=27 3/16"; M=25 3/16"; M-(2*(D-L-K-J))=23 3/16"; N=12 3/16"; N+(H/2)=29 7/8"; NOZZLE_BOTTOM_ID=21 3/8"; NOZZLE_BOTTOM_RAD=10 11/16"; NOZZLE_BOTTOM_RAD-3*2=4 11/16"; NOZZLE_HEIGHT=43"; NOZZLE_HEIGHT/7*2=10 3/4"; NOZZLE_SIZE=15"; NOZZLE_TOP_OD=23"; NOZZLE_TOP_RAD=11 1/2"; NOZZLE_WB/4=7 3/16"; NOZZLE_WB_OD=36"; NOZZLE_WB_RAD=18"; NOZZLE_WB_RAD-2"=16"; P=18 1/4"; R=30"; R*1.1=33"; R+((B/2)+1.5")=48 31/32"; R-((B/2)+1.5")=11 1/32"; TRANSITION=15 1/8"; TRANSITION/2=7 9/16"; Type Comments=Vari-Plume Laboratory Exhaust Centrifugal Airfoil Class 2 Arr 10
- 300_CAVP-18L_CLASS_2: ((M - (2 * (D - L - K - J))) / 2) + (TRANSITION / 2)=20 21/32"; (B/2)+1.5"=18 31/32"; (B/2)-.125"=17 11/32"; (D-J-K-L)*2=2"; (F-((F-H)/2))/2=16 11/16"; (M - (2 * (D - L - K - J)))/2=11 19/32"; (NOZZLE_HEIGHT - (NOZZLE_HEIGHT / 8 * 2)) / 2=18"; (NOZZLE_WB_OD - NOZZLE_TOP_OD) / 4=3 7/8"; -(F-((F-H)/2))/2=-16 11/16"; A=122 7/16"; A/2=61 7/32"; B=34 15/16"; B/2=17 15/32"; B/4=8 3/4"; C=74 15/16"; C/2=37 15/32"; CLASS=2"; D=61 3/16"; D-L-K-J=1"; D-M=36"; E=63 3/4"; E/2=31 7/8"; E/52*15=18 3/8"; F=37 3/8"; F/2=18 11/16"; H=35 3/8"; H/2=17 11/16"; HEIGHT=57 27/32"; J=10"; J+K+L=60 3/16"; K=23"; L=27 3/16"; M=25 3/16"; M-(2*(D-L-K-J))=23 3/16"; N=12 3/16"; N+(H/2)=29 7/8"; NOZZLE_BOTTOM_ID=25 5/8"; NOZZLE_BOTTOM_RAD=12 13/16"; NOZZLE_BOTTOM_RAD-3*2=6 13/16"; NOZZLE_HEIGHT=48"; NOZZLE_HEIGHT/7*2=12"; NOZZLE_SIZE=18"; NOZZLE_TOP_OD=27 1/2"; NOZZLE_TOP_RAD=13 3/4"; NOZZLE_WB/4=8 19/32"; NOZZLE_WB_OD=43"; NOZZLE_WB_RAD=21 1/2"; NOZZLE_WB_RAD-2"=19 1/2"; P=18 1/4"; R=30"; R*1.1=33"; R+((B/2)+1.5")=48 31/32"; R-((B/2)+1.5")=11 1/32"; TRANSITION=18 1/8"; TRANSITION/2=9 1/16"; Type Comments=Vari-Plume Laboratory Exhaust Centrifugal Airfoil Class 2 Arr 10
- 300_CAVP-18H_CLASS_2: ((M - (2 * (D - L - K - J))) / 2) + (TRANSITION / 2)=20 21/32"; (B/2)+1.5"=18 31/32"; (B/2)-.125"=17 11/32"; (D-J-K-L)*2=2"; (F-((F-H)/2))/2=16 11/16"; (M - (2 * (D - L - K - J)))/2=11 19/32"; (NOZZLE_HEIGHT - (NOZZLE_HEIGHT / 8 * 2)) / 2=18"; (NOZZLE_WB_OD - NOZZLE_TOP_OD) / 4=3 7/8"; -(F-((F-H)/2))/2=-16 11/16"; A=122 7/16"; A/2=61 7/32"; B=34 15/16"; B/2=17 15/32"; B/4=8 3/4"; C=74 15/16"; C/2=37 15/32"; CLASS=2"; D=61 3/16"; D-L-K-J=1"; D-M=36"; E=63 3/4"; E/2=31 7/8"; E/52*15=18 3/8"; F=37 3/8"; F/2=18 11/16"; H=35 3/8"; H/2=17 11/16"; HEIGHT=57 27/32"; J=10"; J+K+L=60 3/16"; K=23"; L=27 3/16"; M=25 3/16"; M-(2*(D-L-K-J))=23 3/16"; N=12 3/16"; N+(H/2)=29 7/8"; NOZZLE_BOTTOM_ID=25 5/8"; NOZZLE_BOTTOM_RAD=12 13/16"; NOZZLE_BOTTOM_RAD-3*2=6 13/16"; NOZZLE_HEIGHT=48"; NOZZLE_HEIGHT/7*2=12"; NOZZLE_SIZE=18"; NOZZLE_TOP_OD=27 1/2"; NOZZLE_TOP_RAD=13 3/4"; NOZZLE_WB/4=8 19/32"; NOZZLE_WB_OD=43"; NOZZLE_WB_RAD=21 1/2"; NOZZLE_WB_RAD-2"=19 1/2"; P=18 1/4"; R=30"; R*1.1=33"; R+((B/2)+1.5")=48 31/32"; R-((B/2)+1.5")=11 1/32"; TRANSITION=18 1/8"; TRANSITION/2=9 1/16"; Type Comments=Vari-Plume Laboratory Exhaust Centrifugal Airfoil Class 2 Arr 10
- 330_CAVP-15L_CLASS_1: ((M - (2 * (D - L - K - J))) / 2) + (TRANSITION / 2)=20 5/16"; (B/2)+1.5"=20 15/32"; (B/2)-.125"=18 27/32"; (D-J-K-L)*2=2"; (F-((F-H)/2))/2=18 3/16"; (M - (2 * (D - L - K - J)))/2=12 3/4"; (NOZZLE_HEIGHT - (NOZZLE_HEIGHT / 8 * 2)) / 2=16 1/8"; (NOZZLE_WB_OD - NOZZLE_TOP_OD) / 4=3 1/4"; -(F-((F-H)/2))/2=-18 3/16"; A=144 7/16"; A/2=72 7/32"; B=37 15/16"; B/2=18 31/32"; B/4=9 1/2"; C=82 13/16"; C/2=41 13/32"; CLASS=1"; D=60 1/4"; D-L-K-J=1"; D-M=32 3/4"; E=69 15/16"; E/2=34 31/32"; E/52*15=20 3/16"; F=40 3/8"; F/2=20 3/16"; H=38 3/8"; H/2=19 3/16"; HEIGHT=63 17/32"; J=10 1/2"; J+K+L=59 1/4"; K=19 1/4"; L=29 1/2"; M=27 1/2"; M-(2*(D-L-K-J))=25 1/2"; N=13 25/32"; N+(H/2)=32 31/32"; NOZZLE_BOTTOM_ID=21 3/8"; NOZZLE_BOTTOM_RAD=10 11/16"; NOZZLE_BOTTOM_RAD-3*2=4 11/16"; NOZZLE_HEIGHT=43"; NOZZLE_HEIGHT/7*2=10 3/4"; NOZZLE_SIZE=15"; NOZZLE_TOP_OD=23"; NOZZLE_TOP_RAD=11 1/2"; NOZZLE_WB/4=7 3/16"; NOZZLE_WB_OD=36"; NOZZLE_WB_RAD=18"; NOZZLE_WB_RAD-2"=16"; P=60"; R=33"; R*1.1=36 5/16"; R+((B/2)+1.5")=53 15/32"; R-((B/2)+1.5")=12 17/32"; TRANSITION=15 1/8"; TRANSITION/2=7 9/16"; Type Comments=Vari-Plume Laboratory Exhaust Centrifugal Airfoil Class 1 Arr 10
- 330_CAVP-15H_CLASS_1: ((M - (2 * (D - L - K - J))) / 2) + (TRANSITION / 2)=20 5/16"; (B/2)+1.5"=20 15/32"; (B/2)-.125"=18 27/32"; (D-J-K-L)*2=2"; (F-((F-H)/2))/2=18 3/16"; (M - (2 * (D - L - K - J)))/2=12 3/4"; (NOZZLE_HEIGHT - (NOZZLE_HEIGHT / 8 * 2)) / 2=16 1/8"; (NOZZLE_WB_OD - NOZZLE_TOP_OD) / 4=3 1/4"; -(F-((F-H)/2))/2=-18 3/16"; A=144 7/16"; A/2=72 7/32"; B=37 15/16"; B/2=18 31/32"; B/4=9 1/2"; C=82 13/16"; C/2=41 13/32"; CLASS=1"; D=60 1/4"; D-L-K-J=1"; D-M=32 3/4"; E=69 15/16"; E/2=34 31/32"; E/52*15=20 3/16"; F=40 3/8"; F/2=20 3/16"; H=38 3/8"; H/2=19 3/16"; HEIGHT=63 17/32"; J=10 1/2"; J+K+L=59 1/4"; K=19 1/4"; L=29 1/2"; M=27 1/2"; M-(2*(D-L-K-J))=25 1/2"; N=13 25/32"; N+(H/2)=32 31/32"; NOZZLE_BOTTOM_ID=21 3/8"; NOZZLE_BOTTOM_RAD=10 11/16"; NOZZLE_BOTTOM_RAD-3*2=4 11/16"; NOZZLE_HEIGHT=43"; NOZZLE_HEIGHT/7*2=10 3/4"; NOZZLE_SIZE=15"; NOZZLE_TOP_OD=23"; NOZZLE_TOP_RAD=11 1/2"; NOZZLE_WB/4=7 3/16"; NOZZLE_WB_OD=36"; NOZZLE_WB_RAD=18"; NOZZLE_WB_RAD-2"=16"; P=60"; R=33"; R*1.1=36 5/16"; R+((B/2)+1.5")=53 15/32"; R-((B/2)+1.5")=12 17/32"; TRANSITION=15 1/8"; TRANSITION/2=7 9/16"; Type Comments=Vari-Plume Laboratory Exhaust Centrifugal Airfoil Class 1 Arr 10
- 330_CAVP-18L_CLASS_1: ((M - (2 * (D - L - K - J))) / 2) + (TRANSITION / 2)=21 13/16"; (B/2)+1.5"=20 15/32"; (B/2)-.125"=18 27/32"; (D-J-K-L)*2=2"; (F-((F-H)/2))/2=18 3/16"; (M - (2 * (D - L - K - J)))/2=12 3/4"; (NOZZLE_HEIGHT - (NOZZLE_HEIGHT / 8 * 2)) / 2=18"; (NOZZLE_WB_OD - NOZZLE_TOP_OD) / 4=3 7/8"; -(F-((F-H)/2))/2=-18 3/16"; A=144 7/16"; A/2=72 7/32"; B=37 15/16"; B/2=18 31/32"; B/4=9 1/2"; C=82 13/16"; C/2=41 13/32"; CLASS=1"; D=60 1/4"; D-L-K-J=1"; D-M=32 3/4"; E=69 15/16"; E/2=34 31/32"; E/52*15=20 3/16"; F=40 3/8"; F/2=20 3/16"; H=38 3/8"; H/2=19 3/16"; HEIGHT=63 17/32"; J=10 1/2"; J+K+L=59 1/4"; K=19 1/4"; L=29 1/2"; M=27 1/2"; M-(2*(D-L-K-J))=25 1/2"; N=13 25/32"; N+(H/2)=32 31/32"; NOZZLE_BOTTOM_ID=25 5/8"; NOZZLE_BOTTOM_RAD=12 13/16"; NOZZLE_BOTTOM_RAD-3*2=6 13/16"; NOZZLE_HEIGHT=48"; NOZZLE_HEIGHT/7*2=12"; NOZZLE_SIZE=18"; NOZZLE_TOP_OD=27 1/2"; NOZZLE_TOP_RAD=13 3/4"; NOZZLE_WB/4=8 19/32"; NOZZLE_WB_OD=43"; NOZZLE_WB_RAD=21 1/2"; NOZZLE_WB_RAD-2"=19 1/2"; P=60"; R=33"; R*1.1=36 5/16"; R+((B/2)+1.5")=53 15/32"; R-((B/2)+1.5")=12 17/32"; TRANSITION=18 1/8"; TRANSITION/2=9 1/16"; Type Comments=Vari-Plume Laboratory Exhaust Centrifugal Airfoil Class 1 Arr 10
- 330_CAVP-18H_CLASS_1: ((M - (2 * (D - L - K - J))) / 2) + (TRANSITION / 2)=21 13/16"; (B/2)+1.5"=20 15/32"; (B/2)-.125"=18 27/32"; (D-J-K-L)*2=2"; (F-((F-H)/2))/2=18 3/16"; (M - (2 * (D - L - K - J)))/2=12 3/4"; (NOZZLE_HEIGHT - (NOZZLE_HEIGHT / 8 * 2)) / 2=18"; (NOZZLE_WB_OD - NOZZLE_TOP_OD) / 4=3 7/8"; -(F-((F-H)/2))/2=-18 3/16"; A=144 7/16"; A/2=72 7/32"; B=37 15/16"; B/2=18 31/32"; B/4=9 1/2"; C=82 13/16"; C/2=41 13/32"; CLASS=1"; D=60 1/4"; D-L-K-J=1"; D-M=32 3/4"; E=69 15/16"; E/2=34 31/32"; E/52*15=20 3/16"; F=40 3/8"; F/2=20 3/16"; H=38 3/8"; H/2=19 3/16"; HEIGHT=63 17/32"; J=10 1/2"; J+K+L=59 1/4"; K=19 1/4"; L=29 1/2"; M=27 1/2"; M-(2*(D-L-K-J))=25 1/2"; N=13 25/32"; N+(H/2)=32 31/32"; NOZZLE_BOTTOM_ID=25 5/8"; NOZZLE_BOTTOM_RAD=12 13/16"; NOZZLE_BOTTOM_RAD-3*2=6 13/16"; NOZZLE_HEIGHT=48"; NOZZLE_HEIGHT/7*2=12"; NOZZLE_SIZE=18"; NOZZLE_TOP_OD=27 1/2"; NOZZLE_TOP_RAD=13 3/4"; NOZZLE_WB/4=8 19/32"; NOZZLE_WB_OD=43"; NOZZLE_WB_RAD=21 1/2"; NOZZLE_WB_RAD-2"=19 1/2"; P=60"; R=33"; R*1.1=36 5/16"; R+((B/2)+1.5")=53 15/32"; R-((B/2)+1.5")=12 17/32"; TRANSITION=18 1/8"; TRANSITION/2=9 1/16"; Type Comments=Vari-Plume Laboratory Exhaust Centrifugal Airfoil Class 1 Arr 10
- 330_CAVP-24L_CLASS_1: ((M - (2 * (D - L - K - J))) / 2) + (TRANSITION / 2)=25 1/32"; (B/2)+1.5"=20 15/32"; (B/2)-.125"=18 27/32"; (D-J-K-L)*2=2"; (F-((F-H)/2))/2=18 3/16"; (M - (2 * (D - L - K - J)))/2=12 3/4"; (NOZZLE_HEIGHT - (NOZZLE_HEIGHT / 8 * 2)) / 2=23 1/4"; (NOZZLE_WB_OD - NOZZLE_TOP_OD) / 4=6 1/8"; -(F-((F-H)/2))/2=-18 3/16"; A=144 7/16"; A/2=72 7/32"; B=37 15/16"; B/2=18 31/32"; B/4=9 1/2"; C=82 13/16"; C/2=41 13/32"; CLASS=1"; D=60 1/4"; D-L-K-J=1"; D-M=32 3/4"; E=69 15/16"; E/2=34 31/32"; E/52*15=20 3/16"; F=40 3/8"; F/2=20 3/16"; H=38 3/8"; H/2=19 3/16"; HEIGHT=63 17/32"; J=10 1/2"; J+K+L=59 1/4"; K=19 1/4"; L=29 1/2"; M=27 1/2"; M-(2*(D-L-K-J))=25 1/2"; N=13 25/32"; N+(H/2)=32 31/32"; NOZZLE_BOTTOM_ID=34 3/4"; NOZZLE_BOTTOM_RAD=17 3/8"; NOZZLE_BOTTOM_RAD-3*2=11 3/8"; NOZZLE_HEIGHT=62"; NOZZLE_HEIGHT/7*2=15 1/2"; NOZZLE_SIZE=24"; NOZZLE_TOP_OD=36 1/2"; NOZZLE_TOP_RAD=18 1/4"; NOZZLE_WB/4=12 3/16"; NOZZLE_WB_OD=61"; NOZZLE_WB_RAD=30 1/2"; NOZZLE_WB_RAD-2"=28 1/2"; P=60"; R=33"; R*1.1=36 5/16"; R+((B/2)+1.5")=53 15/32"; R-((B/2)+1.5")=12 17/32"; TRANSITION=24 9/16"; TRANSITION/2=12 9/32"; Type Comments=Vari-Plume Laboratory Exhaust Centrifugal Airfoil Class 1 Arr 10
- 330_CAVP-24H_CLASS_1: ((M - (2 * (D - L - K - J))) / 2) + (TRANSITION / 2)=25 1/32"; (B/2)+1.5"=20 15/32"; (B/2)-.125"=18 27/32"; (D-J-K-L)*2=2"; (F-((F-H)/2))/2=18 3/16"; (M - (2 * (D - L - K - J)))/2=12 3/4"; (NOZZLE_HEIGHT - (NOZZLE_HEIGHT / 8 * 2)) / 2=23 1/4"; (NOZZLE_WB_OD - NOZZLE_TOP_OD) / 4=6 1/8"; -(F-((F-H)/2))/2=-18 3/16"; A=144 7/16"; A/2=72 7/32"; B=37 15/16"; B/2=18 31/32"; B/4=9 1/2"; C=82 13/16"; C/2=41 13/32"; CLASS=1"; D=60 1/4"; D-L-K-J=1"; D-M=32 3/4"; E=69 15/16"; E/2=34 31/32"; E/52*15=20 3/16"; F=40 3/8"; F/2=20 3/16"; H=38 3/8"; H/2=19 3/16"; HEIGHT=63 17/32"; J=10 1/2"; J+K+L=59 1/4"; K=19 1/4"; L=29 1/2"; M=27 1/2"; M-(2*(D-L-K-J))=25 1/2"; N=13 25/32"; N+(H/2)=32 31/32"; NOZZLE_BOTTOM_ID=34 3/4"; NOZZLE_BOTTOM_RAD=17 3/8"; NOZZLE_BOTTOM_RAD-3*2=11 3/8"; NOZZLE_HEIGHT=62"; NOZZLE_HEIGHT/7*2=15 1/2"; NOZZLE_SIZE=24"; NOZZLE_TOP_OD=36 1/2"; NOZZLE_TOP_RAD=18 1/4"; NOZZLE_WB/4=12 3/16"; NOZZLE_WB_OD=61"; NOZZLE_WB_RAD=30 1/2"; NOZZLE_WB_RAD-2"=28 1/2"; P=60"; R=33"; R*1.1=36 5/16"; R+((B/2)+1.5")=53 15/32"; R-((B/2)+1.5")=12 17/32"; TRANSITION=24 9/16"; TRANSITION/2=12 9/32"; Type Comments=Vari-Plume Laboratory Exhaust Centrifugal Airfoil Class 1 Arr 10
- 330_CAVP-15L_CLASS_2: ((M - (2 * (D - L - K - J))) / 2) + (TRANSITION / 2)=20 5/16"; (B/2)+1.5"=20 15/32"; (B/2)-.125"=18 27/32"; (D-J-K-L)*2=2"; (F-((F-H)/2))/2=18 3/16"; (M - (2 * (D - L - K - J)))/2=12 3/4"; (NOZZLE_HEIGHT - (NOZZLE_HEIGHT / 8 * 2)) / 2=16 1/8"; (NOZZLE_WB_OD - NOZZLE_TOP_OD) / 4=3 1/4"; -(F-((F-H)/2))/2=-18 3/16"; A=144 7/16"; A/2=72 7/32"; B=37 15/16"; B/2=18 31/32"; B/4=9 1/2"; C=82 13/16"; C/2=41 13/32"; CLASS=2"; D=64"; D-L-K-J=1"; D-M=36 1/2"; E=69 15/16"; E/2=34 31/32"; E/52*15=20 3/16"; F=40 3/8"; F/2=20 3/16"; H=38 3/8"; H/2=19 3/16"; HEIGHT=63 17/32"; J=10 1/2"; J+K+L=63"; K=23"; L=29 1/2"; M=27 1/2"; M-(2*(D-L-K-J))=25 1/2"; N=13 25/32"; N+(H/2)=32 31/32"; NOZZLE_BOTTOM_ID=21 3/8"; NOZZLE_BOTTOM_RAD=10 11/16"; NOZZLE_BOTTOM_RAD-3*2=4 11/16"; NOZZLE_HEIGHT=43"; NOZZLE_HEIGHT/7*2=10 3/4"; NOZZLE_SIZE=15"; NOZZLE_TOP_OD=23"; NOZZLE_TOP_RAD=11 1/2"; NOZZLE_WB/4=7 3/16"; NOZZLE_WB_OD=36"; NOZZLE_WB_RAD=18"; NOZZLE_WB_RAD-2"=16"; P=60"; R=33"; R*1.1=36 5/16"; R+((B/2)+1.5")=53 15/32"; R-((B/2)+1.5")=12 17/32"; TRANSITION=15 1/8"; TRANSITION/2=7 9/16"; Type Comments=Vari-Plume Laboratory Exhaust Centrifugal Airfoil Class 2 Arr 10
- 330_CAVP-15H_CLASS_2: ((M - (2 * (D - L - K - J))) / 2) + (TRANSITION / 2)=20 5/16"; (B/2)+1.5"=20 15/32"; (B/2)-.125"=18 27/32"; (D-J-K-L)*2=2"; (F-((F-H)/2))/2=18 3/16"; (M - (2 * (D - L - K - J)))/2=12 3/4"; (NOZZLE_HEIGHT - (NOZZLE_HEIGHT / 8 * 2)) / 2=16 1/8"; (NOZZLE_WB_OD - NOZZLE_TOP_OD) / 4=3 1/4"; -(F-((F-H)/2))/2=-18 3/16"; A=144 7/16"; A/2=72 7/32"; B=37 15/16"; B/2=18 31/32"; B/4=9 1/2"; C=82 13/16"; C/2=41 13/32"; CLASS=2"; D=64"; D-L-K-J=1"; D-M=36 1/2"; E=69 15/16"; E/2=34 31/32"; E/52*15=20 3/16"; F=40 3/8"; F/2=20 3/16"; H=38 3/8"; H/2=19 3/16"; HEIGHT=63 17/32"; J=10 1/2"; J+K+L=63"; K=23"; L=29 1/2"; M=27 1/2"; M-(2*(D-L-K-J))=25 1/2"; N=13 25/32"; N+(H/2)=32 31/32"; NOZZLE_BOTTOM_ID=21 3/8"; NOZZLE_BOTTOM_RAD=10 11/16"; NOZZLE_BOTTOM_RAD-3*2=4 11/16"; NOZZLE_HEIGHT=43"; NOZZLE_HEIGHT/7*2=10 3/4"; NOZZLE_SIZE=15"; NOZZLE_TOP_OD=23"; NOZZLE_TOP_RAD=11 1/2"; NOZZLE_WB/4=7 3/16"; NOZZLE_WB_OD=36"; NOZZLE_WB_RAD=18"; NOZZLE_WB_RAD-2"=16"; P=60"; R=33"; R*1.1=36 5/16"; R+((B/2)+1.5")=53 15/32"; R-((B/2)+1.5")=12 17/32"; TRANSITION=15 1/8"; TRANSITION/2=7 9/16"; Type Comments=Vari-Plume Laboratory Exhaust Centrifugal Airfoil Class 2 Arr 10
- 330_CAVP-18L_CLASS_2: ((M - (2 * (D - L - K - J))) / 2) + (TRANSITION / 2)=21 13/16"; (B/2)+1.5"=20 15/32"; (B/2)-.125"=18 27/32"; (D-J-K-L)*2=2"; (F-((F-H)/2))/2=18 3/16"; (M - (2 * (D - L - K - J)))/2=12 3/4"; (NOZZLE_HEIGHT - (NOZZLE_HEIGHT / 8 * 2)) / 2=18"; (NOZZLE_WB_OD - NOZZLE_TOP_OD) / 4=3 7/8"; -(F-((F-H)/2))/2=-18 3/16"; A=144 7/16"; A/2=72 7/32"; B=37 15/16"; B/2=18 31/32"; B/4=9 1/2"; C=82 13/16"; C/2=41 13/32"; CLASS=2"; D=64"; D-L-K-J=1"; D-M=36 1/2"; E=69 15/16"; E/2=34 31/32"; E/52*15=20 3/16"; F=40 3/8"; F/2=20 3/16"; H=38 3/8"; H/2=19 3/16"; HEIGHT=63 17/32"; J=10 1/2"; J+K+L=63"; K=23"; L=29 1/2"; M=27 1/2"; M-(2*(D-L-K-J))=25 1/2"; N=13 25/32"; N+(H/2)=32 31/32"; NOZZLE_BOTTOM_ID=25 5/8"; NOZZLE_BOTTOM_RAD=12 13/16"; NOZZLE_BOTTOM_RAD-3*2=6 13/16"; NOZZLE_HEIGHT=48"; NOZZLE_HEIGHT/7*2=12"; NOZZLE_SIZE=18"; NOZZLE_TOP_OD=27 1/2"; NOZZLE_TOP_RAD=13 3/4"; NOZZLE_WB/4=8 19/32"; NOZZLE_WB_OD=43"; NOZZLE_WB_RAD=21 1/2"; NOZZLE_WB_RAD-2"=19 1/2"; P=60"; R=33"; R*1.1=36 5/16"; R+((B/2)+1.5")=53 15/32"; R-((B/2)+1.5")=12 17/32"; TRANSITION=18 1/8"; TRANSITION/2=9 1/16"; Type Comments=Vari-Plume Laboratory Exhaust Centrifugal Airfoil Class 2 Arr 10
- 330_CAVP-18H_CLASS_2: ((M - (2 * (D - L - K - J))) / 2) + (TRANSITION / 2)=21 13/16"; (B/2)+1.5"=20 15/32"; (B/2)-.125"=18 27/32"; (D-J-K-L)*2=2"; (F-((F-H)/2))/2=18 3/16"; (M - (2 * (D - L - K - J)))/2=12 3/4"; (NOZZLE_HEIGHT - (NOZZLE_HEIGHT / 8 * 2)) / 2=18"; (NOZZLE_WB_OD - NOZZLE_TOP_OD) / 4=3 7/8"; -(F-((F-H)/2))/2=-18 3/16"; A=144 7/16"; A/2=72 7/32"; B=37 15/16"; B/2=18 31/32"; B/4=9 1/2"; C=82 13/16"; C/2=41 13/32"; CLASS=2"; D=64"; D-L-K-J=1"; D-M=36 1/2"; E=69 15/16"; E/2=34 31/32"; E/52*15=20 3/16"; F=40 3/8"; F/2=20 3/16"; H=38 3/8"; H/2=19 3/16"; HEIGHT=63 17/32"; J=10 1/2"; J+K+L=63"; K=23"; L=29 1/2"; M=27 1/2"; M-(2*(D-L-K-J))=25 1/2"; N=13 25/32"; N+(H/2)=32 31/32"; NOZZLE_BOTTOM_ID=25 5/8"; NOZZLE_BOTTOM_RAD=12 13/16"; NOZZLE_BOTTOM_RAD-3*2=6 13/16"; NOZZLE_HEIGHT=48"; NOZZLE_HEIGHT/7*2=12"; NOZZLE_SIZE=18"; NOZZLE_TOP_OD=27 1/2"; NOZZLE_TOP_RAD=13 3/4"; NOZZLE_WB/4=8 19/32"; NOZZLE_WB_OD=43"; NOZZLE_WB_RAD=21 1/2"; NOZZLE_WB_RAD-2"=19 1/2"; P=60"; R=33"; R*1.1=36 5/16"; R+((B/2)+1.5")=53 15/32"; R-((B/2)+1.5")=12 17/32"; TRANSITION=18 1/8"; TRANSITION/2=9 1/16"; Type Comments=Vari-Plume Laboratory Exhaust Centrifugal Airfoil Class 2 Arr 10
- 330_CAVP-24L_CLASS_2: ((M - (2 * (D - L - K - J))) / 2) + (TRANSITION / 2)=25 1/32"; (B/2)+1.5"=20 15/32"; (B/2)-.125"=18 27/32"; (D-J-K-L)*2=2"; (F-((F-H)/2))/2=18 3/16"; (M - (2 * (D - L - K - J)))/2=12 3/4"; (NOZZLE_HEIGHT - (NOZZLE_HEIGHT / 8 * 2)) / 2=23 1/4"; (NOZZLE_WB_OD - NOZZLE_TOP_OD) / 4=6 1/8"; -(F-((F-H)/2))/2=-18 3/16"; A=144 7/16"; A/2=72 7/32"; B=37 15/16"; B/2=18 31/32"; B/4=9 1/2"; C=82 13/16"; C/2=41 13/32"; CLASS=2"; D=64"; D-L-K-J=1"; D-M=36 1/2"; E=69 15/16"; E/2=34 31/32"; E/52*15=20 3/16"; F=40 3/8"; F/2=20 3/16"; H=38 3/8"; H/2=19 3/16"; HEIGHT=63 17/32"; J=10 1/2"; J+K+L=63"; K=23"; L=29 1/2"; M=27 1/2"; M-(2*(D-L-K-J))=25 1/2"; N=13 25/32"; N+(H/2)=32 31/32"; NOZZLE_BOTTOM_ID=34 3/4"; NOZZLE_BOTTOM_RAD=17 3/8"; NOZZLE_BOTTOM_RAD-3*2=11 3/8"; NOZZLE_HEIGHT=62"; NOZZLE_HEIGHT/7*2=15 1/2"; NOZZLE_SIZE=24"; NOZZLE_TOP_OD=36 1/2"; NOZZLE_TOP_RAD=18 1/4"; NOZZLE_WB/4=12 3/16"; NOZZLE_WB_OD=61"; NOZZLE_WB_RAD=30 1/2"; NOZZLE_WB_RAD-2"=28 1/2"; P=60"; R=33"; R*1.1=36 5/16"; R+((B/2)+1.5")=53 15/32"; R-((B/2)+1.5")=12 17/32"; TRANSITION=24 9/16"; TRANSITION/2=12 9/32"; Type Comments=Vari-Plume Laboratory Exhaust Centrifugal Airfoil Class 2 Arr 10
- 330_CAVP-24H_CLASS_2: ((M - (2 * (D - L - K - J))) / 2) + (TRANSITION / 2)=25 1/32"; (B/2)+1.5"=20 15/32"; (B/2)-.125"=18 27/32"; (D-J-K-L)*2=2"; (F-((F-H)/2))/2=18 3/16"; (M - (2 * (D - L - K - J)))/2=12 3/4"; (NOZZLE_HEIGHT - (NOZZLE_HEIGHT / 8 * 2)) / 2=23 1/4"; (NOZZLE_WB_OD - NOZZLE_TOP_OD) / 4=6 1/8"; -(F-((F-H)/2))/2=-18 3/16"; A=144 7/16"; A/2=72 7/32"; B=37 15/16"; B/2=18 31/32"; B/4=9 1/2"; C=82 13/16"; C/2=41 13/32"; CLASS=2"; D=64"; D-L-K-J=1"; D-M=36 1/2"; E=69 15/16"; E/2=34 31/32"; E/52*15=20 3/16"; F=40 3/8"; F/2=20 3/16"; H=38 3/8"; H/2=19 3/16"; HEIGHT=63 17/32"; J=10 1/2"; J+K+L=63"; K=23"; L=29 1/2"; M=27 1/2"; M-(2*(D-L-K-J))=25 1/2"; N=13 25/32"; N+(H/2)=32 31/32"; NOZZLE_BOTTOM_ID=34 3/4"; NOZZLE_BOTTOM_RAD=17 3/8"; NOZZLE_BOTTOM_RAD-3*2=11 3/8"; NOZZLE_HEIGHT=62"; NOZZLE_HEIGHT/7*2=15 1/2"; NOZZLE_SIZE=24"; NOZZLE_TOP_OD=36 1/2"; NOZZLE_TOP_RAD=18 1/4"; NOZZLE_WB/4=12 3/16"; NOZZLE_WB_OD=61"; NOZZLE_WB_RAD=30 1/2"; NOZZLE_WB_RAD-2"=28 1/2"; P=60"; R=33"; R*1.1=36 5/16"; R+((B/2)+1.5")=53 15/32"; R-((B/2)+1.5")=12 17/32"; TRANSITION=24 9/16"; TRANSITION/2=12 9/32"; Type Comments=Vari-Plume Laboratory Exhaust Centrifugal Airfoil Class 2 Arr 10
- 365_CAVP-15L_CLASS_1: ((M - (2 * (D - L - K - J))) / 2) + (TRANSITION / 2)=21 5/8"; (B/2)+1.5"=22 23/32"; (B/2)-.125"=21 3/32"; (D-J-K-L)*2=2"; (F-((F-H)/2))/2=20 7/16"; (M - (2 * (D - L - K - J)))/2=14 1/16"; (NOZZLE_HEIGHT - (NOZZLE_HEIGHT / 8 * 2)) / 2=16 1/8"; (NOZZLE_WB_OD - NOZZLE_TOP_OD) / 4=3 1/4"; -(F-((F-H)/2))/2=-20 7/16"; A=153 13/16"; A/2=76 29/32"; B=42 7/16"; B/2=21 7/32"; B/4=10 5/8"; C=92 3/16"; C/2=46 3/32"; CLASS=1"; D=66 7/8"; D-L-K-J=1"; D-M=36 3/4"; E=77 5/16"; E/2=38 21/32"; E/52*15=22 5/16"; F=44 7/8"; F/2=22 7/16"; H=42 7/8"; H/2=21 7/16"; HEIGHT=69 3/4"; J=11"; J+K+L=65 7/8"; K=22 3/4"; L=32 1/8"; M=30 1/8"; M-(2*(D-L-K-J))=28 1/8"; N=15 7/32"; N+(H/2)=36 21/32"; NOZZLE_BOTTOM_ID=21 3/8"; NOZZLE_BOTTOM_RAD=10 11/16"; NOZZLE_BOTTOM_RAD-3*2=4 11/16"; NOZZLE_HEIGHT=43"; NOZZLE_HEIGHT/7*2=10 3/4"; NOZZLE_SIZE=15"; NOZZLE_TOP_OD=23"; NOZZLE_TOP_RAD=11 1/2"; NOZZLE_WB/4=7 3/16"; NOZZLE_WB_OD=36"; NOZZLE_WB_RAD=18"; NOZZLE_WB_RAD-2"=16"; P=18 1/4"; R=36"; R*1.1=39 19/32"; R+((B/2)+1.5")=58 23/32"; R-((B/2)+1.5")=13 9/32"; TRANSITION=15 1/8"; TRANSITION/2=7 9/16"; Type Comments=Vari-Plume Laboratory Exhaust Centrifugal Airfoil Class 1 Arr 10
- 365_CAVP-15H_CLASS_1: ((M - (2 * (D - L - K - J))) / 2) + (TRANSITION / 2)=21 5/8"; (B/2)+1.5"=22 23/32"; (B/2)-.125"=21 3/32"; (D-J-K-L)*2=2"; (F-((F-H)/2))/2=20 7/16"; (M - (2 * (D - L - K - J)))/2=14 1/16"; (NOZZLE_HEIGHT - (NOZZLE_HEIGHT / 8 * 2)) / 2=16 1/8"; (NOZZLE_WB_OD - NOZZLE_TOP_OD) / 4=3 1/4"; -(F-((F-H)/2))/2=-20 7/16"; A=153 13/16"; A/2=76 29/32"; B=42 7/16"; B/2=21 7/32"; B/4=10 5/8"; C=92 3/16"; C/2=46 3/32"; CLASS=1"; D=66 7/8"; D-L-K-J=1"; D-M=36 3/4"; E=77 5/16"; E/2=38 21/32"; E/52*15=22 5/16"; F=44 7/8"; F/2=22 7/16"; H=42 7/8"; H/2=21 7/16"; HEIGHT=69 3/4"; J=11"; J+K+L=65 7/8"; K=22 3/4"; L=32 1/8"; M=30 1/8"; M-(2*(D-L-K-J))=28 1/8"; N=15 7/32"; N+(H/2)=36 21/32"; NOZZLE_BOTTOM_ID=21 3/8"; NOZZLE_BOTTOM_RAD=10 11/16"; NOZZLE_BOTTOM_RAD-3*2=4 11/16"; NOZZLE_HEIGHT=43"; NOZZLE_HEIGHT/7*2=10 3/4"; NOZZLE_SIZE=15"; NOZZLE_TOP_OD=23"; NOZZLE_TOP_RAD=11 1/2"; NOZZLE_WB/4=7 3/16"; NOZZLE_WB_OD=36"; NOZZLE_WB_RAD=18"; NOZZLE_WB_RAD-2"=16"; P=18 1/4"; R=36"; R*1.1=39 19/32"; R+((B/2)+1.5")=58 23/32"; R-((B/2)+1.5")=13 9/32"; TRANSITION=15 1/8"; TRANSITION/2=7 9/16"; Type Comments=Vari-Plume Laboratory Exhaust Centrifugal Airfoil Class 1 Arr 10
- 365_CAVP-18L_CLASS_1: ((M - (2 * (D - L - K - J))) / 2) + (TRANSITION / 2)=23 1/8"; (B/2)+1.5"=22 23/32"; (B/2)-.125"=21 3/32"; (D-J-K-L)*2=2"; (F-((F-H)/2))/2=20 7/16"; (M - (2 * (D - L - K - J)))/2=14 1/16"; (NOZZLE_HEIGHT - (NOZZLE_HEIGHT / 8 * 2)) / 2=18"; (NOZZLE_WB_OD - NOZZLE_TOP_OD) / 4=3 7/8"; -(F-((F-H)/2))/2=-20 7/16"; A=153 13/16"; A/2=76 29/32"; B=42 7/16"; B/2=21 7/32"; B/4=10 5/8"; C=92 3/16"; C/2=46 3/32"; CLASS=1"; D=66 7/8"; D-L-K-J=1"; D-M=36 3/4"; E=77 5/16"; E/2=38 21/32"; E/52*15=22 5/16"; F=44 7/8"; F/2=22 7/16"; H=42 7/8"; H/2=21 7/16"; HEIGHT=69 3/4"; J=11"; J+K+L=65 7/8"; K=22 3/4"; L=32 1/8"; M=30 1/8"; M-(2*(D-L-K-J))=28 1/8"; N=15 7/32"; N+(H/2)=36 21/32"; NOZZLE_BOTTOM_ID=25 5/8"; NOZZLE_BOTTOM_RAD=12 13/16"; NOZZLE_BOTTOM_RAD-3*2=6 13/16"; NOZZLE_HEIGHT=48"; NOZZLE_HEIGHT/7*2=12"; NOZZLE_SIZE=18"; NOZZLE_TOP_OD=27 1/2"; NOZZLE_TOP_RAD=13 3/4"; NOZZLE_WB/4=8 19/32"; NOZZLE_WB_OD=43"; NOZZLE_WB_RAD=21 1/2"; NOZZLE_WB_RAD-2"=19 1/2"; P=18 1/4"; R=36"; R*1.1=39 19/32"; R+((B/2)+1.5")=58 23/32"; R-((B/2)+1.5")=13 9/32"; TRANSITION=18 1/8"; TRANSITION/2=9 1/16"; Type Comments=Vari-Plume Laboratory Exhaust Centrifugal Airfoil Class 1 Arr 10
- 365_CAVP-18H_CLASS_1: ((M - (2 * (D - L - K - J))) / 2) + (TRANSITION / 2)=23 1/8"; (B/2)+1.5"=22 23/32"; (B/2)-.125"=21 3/32"; (D-J-K-L)*2=2"; (F-((F-H)/2))/2=20 7/16"; (M - (2 * (D - L - K - J)))/2=14 1/16"; (NOZZLE_HEIGHT - (NOZZLE_HEIGHT / 8 * 2)) / 2=18"; (NOZZLE_WB_OD - NOZZLE_TOP_OD) / 4=3 7/8"; -(F-((F-H)/2))/2=-20 7/16"; A=153 13/16"; A/2=76 29/32"; B=42 7/16"; B/2=21 7/32"; B/4=10 5/8"; C=92 3/16"; C/2=46 3/32"; CLASS=1"; D=66 7/8"; D-L-K-J=1"; D-M=36 3/4"; E=77 5/16"; E/2=38 21/32"; E/52*15=22 5/16"; F=44 7/8"; F/2=22 7/16"; H=42 7/8"; H/2=21 7/16"; HEIGHT=69 3/4"; J=11"; J+K+L=65 7/8"; K=22 3/4"; L=32 1/8"; M=30 1/8"; M-(2*(D-L-K-J))=28 1/8"; N=15 7/32"; N+(H/2)=36 21/32"; NOZZLE_BOTTOM_ID=25 5/8"; NOZZLE_BOTTOM_RAD=12 13/16"; NOZZLE_BOTTOM_RAD-3*2=6 13/16"; NOZZLE_HEIGHT=48"; NOZZLE_HEIGHT/7*2=12"; NOZZLE_SIZE=18"; NOZZLE_TOP_OD=27 1/2"; NOZZLE_TOP_RAD=13 3/4"; NOZZLE_WB/4=8 19/32"; NOZZLE_WB_OD=43"; NOZZLE_WB_RAD=21 1/2"; NOZZLE_WB_RAD-2"=19 1/2"; P=18 1/4"; R=36"; R*1.1=39 19/32"; R+((B/2)+1.5")=58 23/32"; R-((B/2)+1.5")=13 9/32"; TRANSITION=18 1/8"; TRANSITION/2=9 1/16"; Type Comments=Vari-Plume Laboratory Exhaust Centrifugal Airfoil Class 1 Arr 10
- 365_CAVP-24L_CLASS_1: ((M - (2 * (D - L - K - J))) / 2) + (TRANSITION / 2)=26 11/32"; (B/2)+1.5"=22 23/32"; (B/2)-.125"=21 3/32"; (D-J-K-L)*2=2"; (F-((F-H)/2))/2=20 7/16"; (M - (2 * (D - L - K - J)))/2=14 1/16"; (NOZZLE_HEIGHT - (NOZZLE_HEIGHT / 8 * 2)) / 2=23 1/4"; (NOZZLE_WB_OD - NOZZLE_TOP_OD) / 4=6 1/8"; -(F-((F-H)/2))/2=-20 7/16"; A=153 13/16"; A/2=76 29/32"; B=42 7/16"; B/2=21 7/32"; B/4=10 5/8"; C=92 3/16"; C/2=46 3/32"; CLASS=1"; D=66 7/8"; D-L-K-J=1"; D-M=36 3/4"; E=77 5/16"; E/2=38 21/32"; E/52*15=22 5/16"; F=44 7/8"; F/2=22 7/16"; H=42 7/8"; H/2=21 7/16"; HEIGHT=69 3/4"; J=11"; J+K+L=65 7/8"; K=22 3/4"; L=32 1/8"; M=30 1/8"; M-(2*(D-L-K-J))=28 1/8"; N=15 7/32"; N+(H/2)=36 21/32"; NOZZLE_BOTTOM_ID=34 3/4"; NOZZLE_BOTTOM_RAD=17 3/8"; NOZZLE_BOTTOM_RAD-3*2=11 3/8"; NOZZLE_HEIGHT=62"; NOZZLE_HEIGHT/7*2=15 1/2"; NOZZLE_SIZE=24"; NOZZLE_TOP_OD=36 1/2"; NOZZLE_TOP_RAD=18 1/4"; NOZZLE_WB/4=12 3/16"; NOZZLE_WB_OD=61"; NOZZLE_WB_RAD=30 1/2"; NOZZLE_WB_RAD-2"=28 1/2"; P=18 1/4"; R=36"; R*1.1=39 19/32"; R+((B/2)+1.5")=58 23/32"; R-((B/2)+1.5")=13 9/32"; TRANSITION=24 9/16"; TRANSITION/2=12 9/32"; Type Comments=Vari-Plume Laboratory Exhaust Centrifugal Airfoil Class 1 Arr 10
- 365_CAVP-24H_CLASS_1: ((M - (2 * (D - L - K - J))) / 2) + (TRANSITION / 2)=26 11/32"; (B/2)+1.5"=22 23/32"; (B/2)-.125"=21 3/32"; (D-J-K-L)*2=2"; (F-((F-H)/2))/2=20 7/16"; (M - (2 * (D - L - K - J)))/2=14 1/16"; (NOZZLE_HEIGHT - (NOZZLE_HEIGHT / 8 * 2)) / 2=23 1/4"; (NOZZLE_WB_OD - NOZZLE_TOP_OD) / 4=6 1/8"; -(F-((F-H)/2))/2=-20 7/16"; A=153 13/16"; A/2=76 29/32"; B=42 7/16"; B/2=21 7/32"; B/4=10 5/8"; C=92 3/16"; C/2=46 3/32"; CLASS=1"; D=66 7/8"; D-L-K-J=1"; D-M=36 3/4"; E=77 5/16"; E/2=38 21/32"; E/52*15=22 5/16"; F=44 7/8"; F/2=22 7/16"; H=42 7/8"; H/2=21 7/16"; HEIGHT=69 3/4"; J=11"; J+K+L=65 7/8"; K=22 3/4"; L=32 1/8"; M=30 1/8"; M-(2*(D-L-K-J))=28 1/8"; N=15 7/32"; N+(H/2)=36 21/32"; NOZZLE_BOTTOM_ID=34 3/4"; NOZZLE_BOTTOM_RAD=17 3/8"; NOZZLE_BOTTOM_RAD-3*2=11 3/8"; NOZZLE_HEIGHT=62"; NOZZLE_HEIGHT/7*2=15 1/2"; NOZZLE_SIZE=24"; NOZZLE_TOP_OD=36 1/2"; NOZZLE_TOP_RAD=18 1/4"; NOZZLE_WB/4=12 3/16"; NOZZLE_WB_OD=61"; NOZZLE_WB_RAD=30 1/2"; NOZZLE_WB_RAD-2"=28 1/2"; P=18 1/4"; R=36"; R*1.1=39 19/32"; R+((B/2)+1.5")=58 23/32"; R-((B/2)+1.5")=13 9/32"; TRANSITION=24 9/16"; TRANSITION/2=12 9/32"; Type Comments=Vari-Plume Laboratory Exhaust Centrifugal Airfoil Class 1 Arr 10
- 365_CAVP-15L_CLASS_2: ((M - (2 * (D - L - K - J))) / 2) + (TRANSITION / 2)=21 5/8"; (B/2)+1.5"=22 23/32"; (B/2)-.125"=21 3/32"; (D-J-K-L)*2=2"; (F-((F-H)/2))/2=20 7/16"; (M - (2 * (D - L - K - J)))/2=14 1/16"; (NOZZLE_HEIGHT - (NOZZLE_HEIGHT / 8 * 2)) / 2=16 1/8"; (NOZZLE_WB_OD - NOZZLE_TOP_OD) / 4=3 1/4"; -(F-((F-H)/2))/2=-20 7/16"; A=153 13/16"; A/2=76 29/32"; B=42 7/16"; B/2=21 7/32"; B/4=10 5/8"; C=92 3/16"; C/2=46 3/32"; CLASS=2"; D=67 1/8"; D-L-K-J=1"; D-M=37"; E=77 5/16"; E/2=38 21/32"; E/52*15=22 5/16"; F=44 7/8"; F/2=22 7/16"; H=42 7/8"; H/2=21 7/16"; HEIGHT=69 3/4"; J=11"; J+K+L=66 1/8"; K=23"; L=32 1/8"; M=30 1/8"; M-(2*(D-L-K-J))=28 1/8"; N=15 7/32"; N+(H/2)=36 21/32"; NOZZLE_BOTTOM_ID=21 3/8"; NOZZLE_BOTTOM_RAD=10 11/16"; NOZZLE_BOTTOM_RAD-3*2=4 11/16"; NOZZLE_HEIGHT=43"; NOZZLE_HEIGHT/7*2=10 3/4"; NOZZLE_SIZE=15"; NOZZLE_TOP_OD=23"; NOZZLE_TOP_RAD=11 1/2"; NOZZLE_WB/4=7 3/16"; NOZZLE_WB_OD=36"; NOZZLE_WB_RAD=18"; NOZZLE_WB_RAD-2"=16"; P=18 1/2"; R=36"; R*1.1=39 19/32"; R+((B/2)+1.5")=58 23/32"; R-((B/2)+1.5")=13 9/32"; TRANSITION=15 1/8"; TRANSITION/2=7 9/16"; Type Comments=Vari-Plume Laboratory Exhaust Centrifugal Airfoil Class 2 Arr 10
- 365_CAVP-15H_CLASS_2: ((M - (2 * (D - L - K - J))) / 2) + (TRANSITION / 2)=21 5/8"; (B/2)+1.5"=22 23/32"; (B/2)-.125"=21 3/32"; (D-J-K-L)*2=2"; (F-((F-H)/2))/2=20 7/16"; (M - (2 * (D - L - K - J)))/2=14 1/16"; (NOZZLE_HEIGHT - (NOZZLE_HEIGHT / 8 * 2)) / 2=16 1/8"; (NOZZLE_WB_OD - NOZZLE_TOP_OD) / 4=3 1/4"; -(F-((F-H)/2))/2=-20 7/16"; A=153 13/16"; A/2=76 29/32"; B=42 7/16"; B/2=21 7/32"; B/4=10 5/8"; C=92 3/16"; C/2=46 3/32"; CLASS=2"; D=67 1/8"; D-L-K-J=1"; D-M=37"; E=77 5/16"; E/2=38 21/32"; E/52*15=22 5/16"; F=44 7/8"; F/2=22 7/16"; H=42 7/8"; H/2=21 7/16"; HEIGHT=69 3/4"; J=11"; J+K+L=66 1/8"; K=23"; L=32 1/8"; M=30 1/8"; M-(2*(D-L-K-J))=28 1/8"; N=15 7/32"; N+(H/2)=36 21/32"; NOZZLE_BOTTOM_ID=21 3/8"; NOZZLE_BOTTOM_RAD=10 11/16"; NOZZLE_BOTTOM_RAD-3*2=4 11/16"; NOZZLE_HEIGHT=43"; NOZZLE_HEIGHT/7*2=10 3/4"; NOZZLE_SIZE=15"; NOZZLE_TOP_OD=23"; NOZZLE_TOP_RAD=11 1/2"; NOZZLE_WB/4=7 3/16"; NOZZLE_WB_OD=36"; NOZZLE_WB_RAD=18"; NOZZLE_WB_RAD-2"=16"; P=18 1/2"; R=36"; R*1.1=39 19/32"; R+((B/2)+1.5")=58 23/32"; R-((B/2)+1.5")=13 9/32"; TRANSITION=15 1/8"; TRANSITION/2=7 9/16"; Type Comments=Vari-Plume Laboratory Exhaust Centrifugal Airfoil Class 2 Arr 10
- 365_CAVP-18L_CLASS_2: ((M - (2 * (D - L - K - J))) / 2) + (TRANSITION / 2)=23 1/8"; (B/2)+1.5"=22 23/32"; (B/2)-.125"=21 3/32"; (D-J-K-L)*2=2"; (F-((F-H)/2))/2=20 7/16"; (M - (2 * (D - L - K - J)))/2=14 1/16"; (NOZZLE_HEIGHT - (NOZZLE_HEIGHT / 8 * 2)) / 2=18"; (NOZZLE_WB_OD - NOZZLE_TOP_OD) / 4=3 7/8"; -(F-((F-H)/2))/2=-20 7/16"; A=153 13/16"; A/2=76 29/32"; B=42 7/16"; B/2=21 7/32"; B/4=10 5/8"; C=92 3/16"; C/2=46 3/32"; CLASS=2"; D=67 1/8"; D-L-K-J=1"; D-M=37"; E=77 5/16"; E/2=38 21/32"; E/52*15=22 5/16"; F=44 7/8"; F/2=22 7/16"; H=42 7/8"; H/2=21 7/16"; HEIGHT=69 3/4"; J=11"; J+K+L=66 1/8"; K=23"; L=32 1/8"; M=30 1/8"; M-(2*(D-L-K-J))=28 1/8"; N=15 7/32"; N+(H/2)=36 21/32"; NOZZLE_BOTTOM_ID=25 5/8"; NOZZLE_BOTTOM_RAD=12 13/16"; NOZZLE_BOTTOM_RAD-3*2=6 13/16"; NOZZLE_HEIGHT=48"; NOZZLE_HEIGHT/7*2=12"; NOZZLE_SIZE=18"; NOZZLE_TOP_OD=27 1/2"; NOZZLE_TOP_RAD=13 3/4"; NOZZLE_WB/4=8 19/32"; NOZZLE_WB_OD=43"; NOZZLE_WB_RAD=21 1/2"; NOZZLE_WB_RAD-2"=19 1/2"; P=18 1/2"; R=36"; R*1.1=39 19/32"; R+((B/2)+1.5")=58 23/32"; R-((B/2)+1.5")=13 9/32"; TRANSITION=18 1/8"; TRANSITION/2=9 1/16"; Type Comments=Vari-Plume Laboratory Exhaust Centrifugal Airfoil Class 2 Arr 10
- 365_CAVP-18H_CLASS_2: ((M - (2 * (D - L - K - J))) / 2) + (TRANSITION / 2)=23 1/8"; (B/2)+1.5"=22 23/32"; (B/2)-.125"=21 3/32"; (D-J-K-L)*2=2"; (F-((F-H)/2))/2=20 7/16"; (M - (2 * (D - L - K - J)))/2=14 1/16"; (NOZZLE_HEIGHT - (NOZZLE_HEIGHT / 8 * 2)) / 2=18"; (NOZZLE_WB_OD - NOZZLE_TOP_OD) / 4=3 7/8"; -(F-((F-H)/2))/2=-20 7/16"; A=153 13/16"; A/2=76 29/32"; B=42 7/16"; B/2=21 7/32"; B/4=10 5/8"; C=92 3/16"; C/2=46 3/32"; CLASS=2"; D=67 1/8"; D-L-K-J=1"; D-M=37"; E=77 5/16"; E/2=38 21/32"; E/52*15=22 5/16"; F=44 7/8"; F/2=22 7/16"; H=42 7/8"; H/2=21 7/16"; HEIGHT=69 3/4"; J=11"; J+K+L=66 1/8"; K=23"; L=32 1/8"; M=30 1/8"; M-(2*(D-L-K-J))=28 1/8"; N=15 7/32"; N+(H/2)=36 21/32"; NOZZLE_BOTTOM_ID=25 5/8"; NOZZLE_BOTTOM_RAD=12 13/16"; NOZZLE_BOTTOM_RAD-3*2=6 13/16"; NOZZLE_HEIGHT=48"; NOZZLE_HEIGHT/7*2=12"; NOZZLE_SIZE=18"; NOZZLE_TOP_OD=27 1/2"; NOZZLE_TOP_RAD=13 3/4"; NOZZLE_WB/4=8 19/32"; NOZZLE_WB_OD=43"; NOZZLE_WB_RAD=21 1/2"; NOZZLE_WB_RAD-2"=19 1/2"; P=18 1/2"; R=36"; R*1.1=39 19/32"; R+((B/2)+1.5")=58 23/32"; R-((B/2)+1.5")=13 9/32"; TRANSITION=18 1/8"; TRANSITION/2=9 1/16"; Type Comments=Vari-Plume Laboratory Exhaust Centrifugal Airfoil Class 2 Arr 10
- 365_CAVP-24L_CLASS_2: ((M - (2 * (D - L - K - J))) / 2) + (TRANSITION / 2)=26 11/32"; (B/2)+1.5"=22 23/32"; (B/2)-.125"=21 3/32"; (D-J-K-L)*2=2"; (F-((F-H)/2))/2=20 7/16"; (M - (2 * (D - L - K - J)))/2=14 1/16"; (NOZZLE_HEIGHT - (NOZZLE_HEIGHT / 8 * 2)) / 2=23 1/4"; (NOZZLE_WB_OD - NOZZLE_TOP_OD) / 4=6 1/8"; -(F-((F-H)/2))/2=-20 7/16"; A=153 13/16"; A/2=76 29/32"; B=42 7/16"; B/2=21 7/32"; B/4=10 5/8"; C=92 3/16"; C/2=46 3/32"; CLASS=2"; D=67 1/8"; D-L-K-J=1"; D-M=37"; E=77 5/16"; E/2=38 21/32"; E/52*15=22 5/16"; F=44 7/8"; F/2=22 7/16"; H=42 7/8"; H/2=21 7/16"; HEIGHT=69 3/4"; J=11"; J+K+L=66 1/8"; K=23"; L=32 1/8"; M=30 1/8"; M-(2*(D-L-K-J))=28 1/8"; N=15 7/32"; N+(H/2)=36 21/32"; NOZZLE_BOTTOM_ID=34 3/4"; NOZZLE_BOTTOM_RAD=17 3/8"; NOZZLE_BOTTOM_RAD-3*2=11 3/8"; NOZZLE_HEIGHT=62"; NOZZLE_HEIGHT/7*2=15 1/2"; NOZZLE_SIZE=24"; NOZZLE_TOP_OD=36 1/2"; NOZZLE_TOP_RAD=18 1/4"; NOZZLE_WB/4=12 3/16"; NOZZLE_WB_OD=61"; NOZZLE_WB_RAD=30 1/2"; NOZZLE_WB_RAD-2"=28 1/2"; P=18 1/2"; R=36"; R*1.1=39 19/32"; R+((B/2)+1.5")=58 23/32"; R-((B/2)+1.5")=13 9/32"; TRANSITION=24 9/16"; TRANSITION/2=12 9/32"; Type Comments=Vari-Plume Laboratory Exhaust Centrifugal Airfoil Class 2 Arr 10
- 365_CAVP-24H_CLASS_2: ((M - (2 * (D - L - K - J))) / 2) + (TRANSITION / 2)=26 11/32"; (B/2)+1.5"=22 23/32"; (B/2)-.125"=21 3/32"; (D-J-K-L)*2=2"; (F-((F-H)/2))/2=20 7/16"; (M - (2 * (D - L - K - J)))/2=14 1/16"; (NOZZLE_HEIGHT - (NOZZLE_HEIGHT / 8 * 2)) / 2=23 1/4"; (NOZZLE_WB_OD - NOZZLE_TOP_OD) / 4=6 1/8"; -(F-((F-H)/2))/2=-20 7/16"; A=153 13/16"; A/2=76 29/32"; B=42 7/16"; B/2=21 7/32"; B/4=10 5/8"; C=92 3/16"; C/2=46 3/32"; CLASS=2"; D=67 1/8"; D-L-K-J=1"; D-M=37"; E=77 5/16"; E/2=38 21/32"; E/52*15=22 5/16"; F=44 7/8"; F/2=22 7/16"; H=42 7/8"; H/2=21 7/16"; HEIGHT=69 3/4"; J=11"; J+K+L=66 1/8"; K=23"; L=32 1/8"; M=30 1/8"; M-(2*(D-L-K-J))=28 1/8"; N=15 7/32"; N+(H/2)=36 21/32"; NOZZLE_BOTTOM_ID=34 3/4"; NOZZLE_BOTTOM_RAD=17 3/8"; NOZZLE_BOTTOM_RAD-3*2=11 3/8"; NOZZLE_HEIGHT=62"; NOZZLE_HEIGHT/7*2=15 1/2"; NOZZLE_SIZE=24"; NOZZLE_TOP_OD=36 1/2"; NOZZLE_TOP_RAD=18 1/4"; NOZZLE_WB/4=12 3/16"; NOZZLE_WB_OD=61"; NOZZLE_WB_RAD=30 1/2"; NOZZLE_WB_RAD-2"=28 1/2"; P=18 1/2"; R=36"; R*1.1=39 19/32"; R+((B/2)+1.5")=58 23/32"; R-((B/2)+1.5")=13 9/32"; TRANSITION=24 9/16"; TRANSITION/2=12 9/32"; Type Comments=Vari-Plume Laboratory Exhaust Centrifugal Airfoil Class 2 Arr 10
- 402_CAVP-18L_CLASS_1: ((M - (2 * (D - L - K - J))) / 2) + (TRANSITION / 2)=24 13/16"; (B/2)+1.5"=24 3/32"; (B/2)-.125"=22 15/32"; (D-J-K-L)*2=2 3/4"; (F-((F-H)/2))/2=22 3/8"; (M - (2 * (D - L - K - J)))/2=15 3/4"; (NOZZLE_HEIGHT - (NOZZLE_HEIGHT / 8 * 2)) / 2=18"; (NOZZLE_WB_OD - NOZZLE_TOP_OD) / 4=3 7/8"; -(F-((F-H)/2))/2=-22 3/8"; A=178 3/4"; A/2=89 3/8"; B=45 3/16"; B/2=22 19/32"; B/4=11 5/16"; C=100 3/4"; C/2=50 3/8"; CLASS=1"; D=72 1/4"; D-L-K-J=1 3/8"; D-M=38"; E=84 15/16"; E/2=42 15/32"; E/52*15=24 1/2"; F=48 3/4"; F/2=24 3/8"; H=46 3/4"; H/2=23 3/8"; HEIGHT=77 3/32"; J=12 1/2"; J+K+L=70 7/8"; K=21 7/8"; L=36 1/2"; M=34 1/4"; M-(2*(D-L-K-J))=31 1/2"; N=17 3/32"; N+(H/2)=40 15/32"; NOZZLE_BOTTOM_ID=25 5/8"; NOZZLE_BOTTOM_RAD=12 13/16"; NOZZLE_BOTTOM_RAD-3*2=6 13/16"; NOZZLE_HEIGHT=48"; NOZZLE_HEIGHT/7*2=12"; NOZZLE_SIZE=18"; NOZZLE_TOP_OD=27 1/2"; NOZZLE_TOP_RAD=13 3/4"; NOZZLE_WB/4=8 19/32"; NOZZLE_WB_OD=43"; NOZZLE_WB_RAD=21 1/2"; NOZZLE_WB_RAD-2"=19 1/2"; P=18 1/4"; R=40"; R*1.1=44"; R+((B/2)+1.5")=64 3/32"; R-((B/2)+1.5")=15 29/32"; TRANSITION=18 1/8"; TRANSITION/2=9 1/16"; Type Comments=Vari-Plume Laboratory Exhaust Centrifugal Airfoil Class 1 Arr 10
- 402_CAVP-18H_CLASS_1: ((M - (2 * (D - L - K - J))) / 2) + (TRANSITION / 2)=24 13/16"; (B/2)+1.5"=24 3/32"; (B/2)-.125"=22 15/32"; (D-J-K-L)*2=2 3/4"; (F-((F-H)/2))/2=22 3/8"; (M - (2 * (D - L - K - J)))/2=15 3/4"; (NOZZLE_HEIGHT - (NOZZLE_HEIGHT / 8 * 2)) / 2=18"; (NOZZLE_WB_OD - NOZZLE_TOP_OD) / 4=3 7/8"; -(F-((F-H)/2))/2=-22 3/8"; A=178 3/4"; A/2=89 3/8"; B=45 3/16"; B/2=22 19/32"; B/4=11 5/16"; C=100 3/4"; C/2=50 3/8"; CLASS=1"; D=72 1/4"; D-L-K-J=1 3/8"; D-M=38"; E=84 15/16"; E/2=42 15/32"; E/52*15=24 1/2"; F=48 3/4"; F/2=24 3/8"; H=46 3/4"; H/2=23 3/8"; HEIGHT=77 3/32"; J=12 1/2"; J+K+L=70 7/8"; K=21 7/8"; L=36 1/2"; M=34 1/4"; M-(2*(D-L-K-J))=31 1/2"; N=17 3/32"; N+(H/2)=40 15/32"; NOZZLE_BOTTOM_ID=25 5/8"; NOZZLE_BOTTOM_RAD=12 13/16"; NOZZLE_BOTTOM_RAD-3*2=6 13/16"; NOZZLE_HEIGHT=48"; NOZZLE_HEIGHT/7*2=12"; NOZZLE_SIZE=18"; NOZZLE_TOP_OD=27 1/2"; NOZZLE_TOP_RAD=13 3/4"; NOZZLE_WB/4=8 19/32"; NOZZLE_WB_OD=43"; NOZZLE_WB_RAD=21 1/2"; NOZZLE_WB_RAD-2"=19 1/2"; P=18 1/4"; R=40"; R*1.1=44"; R+((B/2)+1.5")=64 3/32"; R-((B/2)+1.5")=15 29/32"; TRANSITION=18 1/8"; TRANSITION/2=9 1/16"; Type Comments=Vari-Plume Laboratory Exhaust Centrifugal Airfoil Class 1 Arr 10
- 402_CAVP-24L_CLASS_1: ((M - (2 * (D - L - K - J))) / 2) + (TRANSITION / 2)=28 1/32"; (B/2)+1.5"=24 3/32"; (B/2)-.125"=22 15/32"; (D-J-K-L)*2=2 3/4"; (F-((F-H)/2))/2=22 3/8"; (M - (2 * (D - L - K - J)))/2=15 3/4"; (NOZZLE_HEIGHT - (NOZZLE_HEIGHT / 8 * 2)) / 2=23 1/4"; (NOZZLE_WB_OD - NOZZLE_TOP_OD) / 4=6 1/8"; -(F-((F-H)/2))/2=-22 3/8"; A=178 3/4"; A/2=89 3/8"; B=45 3/16"; B/2=22 19/32"; B/4=11 5/16"; C=100 3/4"; C/2=50 3/8"; CLASS=1"; D=72 1/4"; D-L-K-J=1 3/8"; D-M=38"; E=84 15/16"; E/2=42 15/32"; E/52*15=24 1/2"; F=48 3/4"; F/2=24 3/8"; H=46 3/4"; H/2=23 3/8"; HEIGHT=77 3/32"; J=12 1/2"; J+K+L=70 7/8"; K=21 7/8"; L=36 1/2"; M=34 1/4"; M-(2*(D-L-K-J))=31 1/2"; N=17 3/32"; N+(H/2)=40 15/32"; NOZZLE_BOTTOM_ID=34 3/4"; NOZZLE_BOTTOM_RAD=17 3/8"; NOZZLE_BOTTOM_RAD-3*2=11 3/8"; NOZZLE_HEIGHT=62"; NOZZLE_HEIGHT/7*2=15 1/2"; NOZZLE_SIZE=24"; NOZZLE_TOP_OD=36 1/2"; NOZZLE_TOP_RAD=18 1/4"; NOZZLE_WB/4=12 3/16"; NOZZLE_WB_OD=61"; NOZZLE_WB_RAD=30 1/2"; NOZZLE_WB_RAD-2"=28 1/2"; P=18 1/4"; R=40"; R*1.1=44"; R+((B/2)+1.5")=64 3/32"; R-((B/2)+1.5")=15 29/32"; TRANSITION=24 9/16"; TRANSITION/2=12 9/32"; Type Comments=Vari-Plume Laboratory Exhaust Centrifugal Airfoil Class 1 Arr 10
- 402_CAVP-24H_CLASS_1: ((M - (2 * (D - L - K - J))) / 2) + (TRANSITION / 2)=28 1/32"; (B/2)+1.5"=24 3/32"; (B/2)-.125"=22 15/32"; (D-J-K-L)*2=2 3/4"; (F-((F-H)/2))/2=22 3/8"; (M - (2 * (D - L - K - J)))/2=15 3/4"; (NOZZLE_HEIGHT - (NOZZLE_HEIGHT / 8 * 2)) / 2=23 1/4"; (NOZZLE_WB_OD - NOZZLE_TOP_OD) / 4=6 1/8"; -(F-((F-H)/2))/2=-22 3/8"; A=178 3/4"; A/2=89 3/8"; B=45 3/16"; B/2=22 19/32"; B/4=11 5/16"; C=100 3/4"; C/2=50 3/8"; CLASS=1"; D=72 1/4"; D-L-K-J=1 3/8"; D-M=38"; E=84 15/16"; E/2=42 15/32"; E/52*15=24 1/2"; F=48 3/4"; F/2=24 3/8"; H=46 3/4"; H/2=23 3/8"; HEIGHT=77 3/32"; J=12 1/2"; J+K+L=70 7/8"; K=21 7/8"; L=36 1/2"; M=34 1/4"; M-(2*(D-L-K-J))=31 1/2"; N=17 3/32"; N+(H/2)=40 15/32"; NOZZLE_BOTTOM_ID=34 3/4"; NOZZLE_BOTTOM_RAD=17 3/8"; NOZZLE_BOTTOM_RAD-3*2=11 3/8"; NOZZLE_HEIGHT=62"; NOZZLE_HEIGHT/7*2=15 1/2"; NOZZLE_SIZE=24"; NOZZLE_TOP_OD=36 1/2"; NOZZLE_TOP_RAD=18 1/4"; NOZZLE_WB/4=12 3/16"; NOZZLE_WB_OD=61"; NOZZLE_WB_RAD=30 1/2"; NOZZLE_WB_RAD-2"=28 1/2"; P=18 1/4"; R=40"; R*1.1=44"; R+((B/2)+1.5")=64 3/32"; R-((B/2)+1.5")=15 29/32"; TRANSITION=24 9/16"; TRANSITION/2=12 9/32"; Type Comments=Vari-Plume Laboratory Exhaust Centrifugal Airfoil Class 1 Arr 10
- 402_CAVP-30L_CLASS_1: ((M - (2 * (D - L - K - J))) / 2) + (TRANSITION / 2)=30 25/32"; (B/2)+1.5"=24 3/32"; (B/2)-.125"=22 15/32"; (D-J-K-L)*2=2 3/4"; (F-((F-H)/2))/2=22 3/8"; (M - (2 * (D - L - K - J)))/2=15 3/4"; (NOZZLE_HEIGHT - (NOZZLE_HEIGHT / 8 * 2)) / 2=29 1/4"; (NOZZLE_WB_OD - NOZZLE_TOP_OD) / 4=7 1/8"; -(F-((F-H)/2))/2=-22 3/8"; A=178 3/4"; A/2=89 3/8"; B=45 3/16"; B/2=22 19/32"; B/4=11 5/16"; C=100 3/4"; C/2=50 3/8"; CLASS=1"; D=72 1/4"; D-L-K-J=1 3/8"; D-M=38"; E=84 15/16"; E/2=42 15/32"; E/52*15=24 1/2"; F=48 3/4"; F/2=24 3/8"; H=46 3/4"; H/2=23 3/8"; HEIGHT=77 3/32"; J=12 1/2"; J+K+L=70 7/8"; K=21 7/8"; L=36 1/2"; M=34 1/4"; M-(2*(D-L-K-J))=31 1/2"; N=17 3/32"; N+(H/2)=40 15/32"; NOZZLE_BOTTOM_ID=42 1/2"; NOZZLE_BOTTOM_RAD=21 1/4"; NOZZLE_BOTTOM_RAD-3*2=15 1/4"; NOZZLE_HEIGHT=78"; NOZZLE_HEIGHT/7*2=19 1/2"; NOZZLE_SIZE=30"; NOZZLE_TOP_OD=45 1/2"; NOZZLE_TOP_RAD=22 3/4"; NOZZLE_WB/4=14 13/16"; NOZZLE_WB_OD=74"; NOZZLE_WB_RAD=37"; NOZZLE_WB_RAD-2"=35"; P=18 1/4"; R=40"; R*1.1=44"; R+((B/2)+1.5")=64 3/32"; R-((B/2)+1.5")=15 29/32"; TRANSITION=30 1/16"; TRANSITION/2=15 1/32"; Type Comments=Vari-Plume Laboratory Exhaust Centrifugal Airfoil Class 1 Arr 10
- 402_CAVP-30H_CLASS_1: ((M - (2 * (D - L - K - J))) / 2) + (TRANSITION / 2)=30 25/32"; (B/2)+1.5"=24 3/32"; (B/2)-.125"=22 15/32"; (D-J-K-L)*2=2 3/4"; (F-((F-H)/2))/2=22 3/8"; (M - (2 * (D - L - K - J)))/2=15 3/4"; (NOZZLE_HEIGHT - (NOZZLE_HEIGHT / 8 * 2)) / 2=29 1/4"; (NOZZLE_WB_OD - NOZZLE_TOP_OD) / 4=7 1/8"; -(F-((F-H)/2))/2=-22 3/8"; A=178 3/4"; A/2=89 3/8"; B=45 3/16"; B/2=22 19/32"; B/4=11 5/16"; C=100 3/4"; C/2=50 3/8"; CLASS=1"; D=72 1/4"; D-L-K-J=1 3/8"; D-M=38"; E=84 15/16"; E/2=42 15/32"; E/52*15=24 1/2"; F=48 3/4"; F/2=24 3/8"; H=46 3/4"; H/2=23 3/8"; HEIGHT=77 3/32"; J=12 1/2"; J+K+L=70 7/8"; K=21 7/8"; L=36 1/2"; M=34 1/4"; M-(2*(D-L-K-J))=31 1/2"; N=17 3/32"; N+(H/2)=40 15/32"; NOZZLE_BOTTOM_ID=42 1/2"; NOZZLE_BOTTOM_RAD=21 1/4"; NOZZLE_BOTTOM_RAD-3*2=15 1/4"; NOZZLE_HEIGHT=78"; NOZZLE_HEIGHT/7*2=19 1/2"; NOZZLE_SIZE=30"; NOZZLE_TOP_OD=45 1/2"; NOZZLE_TOP_RAD=22 3/4"; NOZZLE_WB/4=14 13/16"; NOZZLE_WB_OD=74"; NOZZLE_WB_RAD=37"; NOZZLE_WB_RAD-2"=35"; P=18 1/4"; R=40"; R*1.1=44"; R+((B/2)+1.5")=64 3/32"; R-((B/2)+1.5")=15 29/32"; TRANSITION=30 1/16"; TRANSITION/2=15 1/32"; Type Comments=Vari-Plume Laboratory Exhaust Centrifugal Airfoil Class 1 Arr 10
- 402_CAVP-18L_CLASS_2: ((M - (2 * (D - L - K - J))) / 2) + (TRANSITION / 2)=24 13/16"; (B/2)+1.5"=24 3/32"; (B/2)-.125"=22 15/32"; (D-J-K-L)*2=2 3/4"; (F-((F-H)/2))/2=22 3/8"; (M - (2 * (D - L - K - J)))/2=15 3/4"; (NOZZLE_HEIGHT - (NOZZLE_HEIGHT / 8 * 2)) / 2=18"; (NOZZLE_WB_OD - NOZZLE_TOP_OD) / 4=3 7/8"; -(F-((F-H)/2))/2=-22 3/8"; A=178 3/4"; A/2=89 3/8"; B=45 3/16"; B/2=22 19/32"; B/4=11 5/16"; C=100 3/4"; C/2=50 3/8"; CLASS=2"; D=72 1/4"; D-L-K-J=1 3/8"; D-M=38"; E=84 15/16"; E/2=42 15/32"; E/52*15=24 1/2"; F=48 3/4"; F/2=24 3/8"; H=46 3/4"; H/2=23 3/8"; HEIGHT=77 3/32"; J=12 1/2"; J+K+L=70 7/8"; K=21 7/8"; L=36 1/2"; M=34 1/4"; M-(2*(D-L-K-J))=31 1/2"; N=17 3/32"; N+(H/2)=40 15/32"; NOZZLE_BOTTOM_ID=25 5/8"; NOZZLE_BOTTOM_RAD=12 13/16"; NOZZLE_BOTTOM_RAD-3*2=6 13/16"; NOZZLE_HEIGHT=48"; NOZZLE_HEIGHT/7*2=12"; NOZZLE_SIZE=18"; NOZZLE_TOP_OD=27 1/2"; NOZZLE_TOP_RAD=13 3/4"; NOZZLE_WB/4=8 19/32"; NOZZLE_WB_OD=43"; NOZZLE_WB_RAD=21 1/2"; NOZZLE_WB_RAD-2"=19 1/2"; P=19 1/2"; R=40"; R*1.1=44"; R+((B/2)+1.5")=64 3/32"; R-((B/2)+1.5")=15 29/32"; TRANSITION=18 1/8"; TRANSITION/2=9 1/16"; Type Comments=Vari-Plume Laboratory Exhaust Centrifugal Airfoil Class 2 Arr 10
- 402_CAVP-18H_CLASS_2: ((M - (2 * (D - L - K - J))) / 2) + (TRANSITION / 2)=24 13/16"; (B/2)+1.5"=24 3/32"; (B/2)-.125"=22 15/32"; (D-J-K-L)*2=2 3/4"; (F-((F-H)/2))/2=22 3/8"; (M - (2 * (D - L - K - J)))/2=15 3/4"; (NOZZLE_HEIGHT - (NOZZLE_HEIGHT / 8 * 2)) / 2=18"; (NOZZLE_WB_OD - NOZZLE_TOP_OD) / 4=3 7/8"; -(F-((F-H)/2))/2=-22 3/8"; A=178 3/4"; A/2=89 3/8"; B=45 3/16"; B/2=22 19/32"; B/4=11 5/16"; C=100 3/4"; C/2=50 3/8"; CLASS=2"; D=72 1/4"; D-L-K-J=1 3/8"; D-M=38"; E=84 15/16"; E/2=42 15/32"; E/52*15=24 1/2"; F=48 3/4"; F/2=24 3/8"; H=46 3/4"; H/2=23 3/8"; HEIGHT=77 3/32"; J=12 1/2"; J+K+L=70 7/8"; K=21 7/8"; L=36 1/2"; M=34 1/4"; M-(2*(D-L-K-J))=31 1/2"; N=17 3/32"; N+(H/2)=40 15/32"; NOZZLE_BOTTOM_ID=25 5/8"; NOZZLE_BOTTOM_RAD=12 13/16"; NOZZLE_BOTTOM_RAD-3*2=6 13/16"; NOZZLE_HEIGHT=48"; NOZZLE_HEIGHT/7*2=12"; NOZZLE_SIZE=18"; NOZZLE_TOP_OD=27 1/2"; NOZZLE_TOP_RAD=13 3/4"; NOZZLE_WB/4=8 19/32"; NOZZLE_WB_OD=43"; NOZZLE_WB_RAD=21 1/2"; NOZZLE_WB_RAD-2"=19 1/2"; P=19 1/2"; R=40"; R*1.1=44"; R+((B/2)+1.5")=64 3/32"; R-((B/2)+1.5")=15 29/32"; TRANSITION=18 1/8"; TRANSITION/2=9 1/16"; Type Comments=Vari-Plume Laboratory Exhaust Centrifugal Airfoil Class 2 Arr 10
- 402_CAVP-24L_CLASS_2: ((M - (2 * (D - L - K - J))) / 2) + (TRANSITION / 2)=28 1/32"; (B/2)+1.5"=24 3/32"; (B/2)-.125"=22 15/32"; (D-J-K-L)*2=2 3/4"; (F-((F-H)/2))/2=22 3/8"; (M - (2 * (D - L - K - J)))/2=15 3/4"; (NOZZLE_HEIGHT - (NOZZLE_HEIGHT / 8 * 2)) / 2=23 1/4"; (NOZZLE_WB_OD - NOZZLE_TOP_OD) / 4=6 1/8"; -(F-((F-H)/2))/2=-22 3/8"; A=178 3/4"; A/2=89 3/8"; B=45 3/16"; B/2=22 19/32"; B/4=11 5/16"; C=100 3/4"; C/2=50 3/8"; CLASS=2"; D=72 1/4"; D-L-K-J=1 3/8"; D-M=38"; E=84 15/16"; E/2=42 15/32"; E/52*15=24 1/2"; F=48 3/4"; F/2=24 3/8"; H=46 3/4"; H/2=23 3/8"; HEIGHT=77 3/32"; J=12 1/2"; J+K+L=70 7/8"; K=21 7/8"; L=36 1/2"; M=34 1/4"; M-(2*(D-L-K-J))=31 1/2"; N=17 3/32"; N+(H/2)=40 15/32"; NOZZLE_BOTTOM_ID=34 3/4"; NOZZLE_BOTTOM_RAD=17 3/8"; NOZZLE_BOTTOM_RAD-3*2=11 3/8"; NOZZLE_HEIGHT=62"; NOZZLE_HEIGHT/7*2=15 1/2"; NOZZLE_SIZE=24"; NOZZLE_TOP_OD=36 1/2"; NOZZLE_TOP_RAD=18 1/4"; NOZZLE_WB/4=12 3/16"; NOZZLE_WB_OD=61"; NOZZLE_WB_RAD=30 1/2"; NOZZLE_WB_RAD-2"=28 1/2"; P=19 1/2"; R=40"; R*1.1=44"; R+((B/2)+1.5")=64 3/32"; R-((B/2)+1.5")=15 29/32"; TRANSITION=24 9/16"; TRANSITION/2=12 9/32"; Type Comments=Vari-Plume Laboratory Exhaust Centrifugal Airfoil Class 2 Arr 10
- 402_CAVP-24H_CLASS_2: ((M - (2 * (D - L - K - J))) / 2) + (TRANSITION / 2)=28 1/32"; (B/2)+1.5"=24 3/32"; (B/2)-.125"=22 15/32"; (D-J-K-L)*2=2 3/4"; (F-((F-H)/2))/2=22 3/8"; (M - (2 * (D - L - K - J)))/2=15 3/4"; (NOZZLE_HEIGHT - (NOZZLE_HEIGHT / 8 * 2)) / 2=23 1/4"; (NOZZLE_WB_OD - NOZZLE_TOP_OD) / 4=6 1/8"; -(F-((F-H)/2))/2=-22 3/8"; A=178 3/4"; A/2=89 3/8"; B=45 3/16"; B/2=22 19/32"; B/4=11 5/16"; C=100 3/4"; C/2=50 3/8"; CLASS=2"; D=72 1/4"; D-L-K-J=1 3/8"; D-M=38"; E=84 15/16"; E/2=42 15/32"; E/52*15=24 1/2"; F=48 3/4"; F/2=24 3/8"; H=46 3/4"; H/2=23 3/8"; HEIGHT=77 3/32"; J=12 1/2"; J+K+L=70 7/8"; K=21 7/8"; L=36 1/2"; M=34 1/4"; M-(2*(D-L-K-J))=31 1/2"; N=17 3/32"; N+(H/2)=40 15/32"; NOZZLE_BOTTOM_ID=34 3/4"; NOZZLE_BOTTOM_RAD=17 3/8"; NOZZLE_BOTTOM_RAD-3*2=11 3/8"; NOZZLE_HEIGHT=62"; NOZZLE_HEIGHT/7*2=15 1/2"; NOZZLE_SIZE=24"; NOZZLE_TOP_OD=36 1/2"; NOZZLE_TOP_RAD=18 1/4"; NOZZLE_WB/4=12 3/16"; NOZZLE_WB_OD=61"; NOZZLE_WB_RAD=30 1/2"; NOZZLE_WB_RAD-2"=28 1/2"; P=19 1/2"; R=40"; R*1.1=44"; R+((B/2)+1.5")=64 3/32"; R-((B/2)+1.5")=15 29/32"; TRANSITION=24 9/16"; TRANSITION/2=12 9/32"; Type Comments=Vari-Plume Laboratory Exhaust Centrifugal Airfoil Class 2 Arr 10
- 402_CAVP-30L_CLASS_2: ((M - (2 * (D - L - K - J))) / 2) + (TRANSITION / 2)=30 25/32"; (B/2)+1.5"=24 3/32"; (B/2)-.125"=22 15/32"; (D-J-K-L)*2=2 3/4"; (F-((F-H)/2))/2=22 3/8"; (M - (2 * (D - L - K - J)))/2=15 3/4"; (NOZZLE_HEIGHT - (NOZZLE_HEIGHT / 8 * 2)) / 2=29 1/4"; (NOZZLE_WB_OD - NOZZLE_TOP_OD) / 4=7 1/8"; -(F-((F-H)/2))/2=-22 3/8"; A=178 3/4"; A/2=89 3/8"; B=45 3/16"; B/2=22 19/32"; B/4=11 5/16"; C=100 3/4"; C/2=50 3/8"; CLASS=2"; D=72 1/4"; D-L-K-J=1 3/8"; D-M=38"; E=84 15/16"; E/2=42 15/32"; E/52*15=24 1/2"; F=48 3/4"; F/2=24 3/8"; H=46 3/4"; H/2=23 3/8"; HEIGHT=77 3/32"; J=12 1/2"; J+K+L=70 7/8"; K=21 7/8"; L=36 1/2"; M=34 1/4"; M-(2*(D-L-K-J))=31 1/2"; N=17 3/32"; N+(H/2)=40 15/32"; NOZZLE_BOTTOM_ID=42 1/2"; NOZZLE_BOTTOM_RAD=21 1/4"; NOZZLE_BOTTOM_RAD-3*2=15 1/4"; NOZZLE_HEIGHT=78"; NOZZLE_HEIGHT/7*2=19 1/2"; NOZZLE_SIZE=30"; NOZZLE_TOP_OD=45 1/2"; NOZZLE_TOP_RAD=22 3/4"; NOZZLE_WB/4=14 13/16"; NOZZLE_WB_OD=74"; NOZZLE_WB_RAD=37"; NOZZLE_WB_RAD-2"=35"; P=19 1/2"; R=40"; R*1.1=44"; R+((B/2)+1.5")=64 3/32"; R-((B/2)+1.5")=15 29/32"; TRANSITION=30 1/16"; TRANSITION/2=15 1/32"; Type Comments=Vari-Plume Laboratory Exhaust Centrifugal Airfoil Class 2 Arr 10
- 402_CAVP-30H_CLASS_2: ((M - (2 * (D - L - K - J))) / 2) + (TRANSITION / 2)=30 25/32"; (B/2)+1.5"=24 3/32"; (B/2)-.125"=22 15/32"; (D-J-K-L)*2=2 3/4"; (F-((F-H)/2))/2=22 3/8"; (M - (2 * (D - L - K - J)))/2=15 3/4"; (NOZZLE_HEIGHT - (NOZZLE_HEIGHT / 8 * 2)) / 2=29 1/4"; (NOZZLE_WB_OD - NOZZLE_TOP_OD) / 4=7 1/8"; -(F-((F-H)/2))/2=-22 3/8"; A=178 3/4"; A/2=89 3/8"; B=45 3/16"; B/2=22 19/32"; B/4=11 5/16"; C=100 3/4"; C/2=50 3/8"; CLASS=2"; D=72 1/4"; D-L-K-J=1 3/8"; D-M=38"; E=84 15/16"; E/2=42 15/32"; E/52*15=24 1/2"; F=48 3/4"; F/2=24 3/8"; H=46 3/4"; H/2=23 3/8"; HEIGHT=77 3/32"; J=12 1/2"; J+K+L=70 7/8"; K=21 7/8"; L=36 1/2"; M=34 1/4"; M-(2*(D-L-K-J))=31 1/2"; N=17 3/32"; N+(H/2)=40 15/32"; NOZZLE_BOTTOM_ID=42 1/2"; NOZZLE_BOTTOM_RAD=21 1/4"; NOZZLE_BOTTOM_RAD-3*2=15 1/4"; NOZZLE_HEIGHT=78"; NOZZLE_HEIGHT/7*2=19 1/2"; NOZZLE_SIZE=30"; NOZZLE_TOP_OD=45 1/2"; NOZZLE_TOP_RAD=22 3/4"; NOZZLE_WB/4=14 13/16"; NOZZLE_WB_OD=74"; NOZZLE_WB_RAD=37"; NOZZLE_WB_RAD-2"=35"; P=19 1/2"; R=40"; R*1.1=44"; R+((B/2)+1.5")=64 3/32"; R-((B/2)+1.5")=15 29/32"; TRANSITION=30 1/16"; TRANSITION/2=15 1/32"; Type Comments=Vari-Plume Laboratory Exhaust Centrifugal Airfoil Class 2 Arr 10
- 445_CAVP-24H_CLASS_1: ((M - (2 * (D - L - K - J))) / 2) + (TRANSITION / 2)=29 21/32"; (B/2)+1.5"=26 7/32"; (B/2)-.125"=24 19/32"; (D-J-K-L)*2=2 3/4"; (F-((F-H)/2))/2=24 3/8"; (M - (2 * (D - L - K - J)))/2=17 3/8"; (NOZZLE_HEIGHT - (NOZZLE_HEIGHT / 8 * 2)) / 2=23 1/4"; (NOZZLE_WB_OD - NOZZLE_TOP_OD) / 4=6 1/8"; -(F-((F-H)/2))/2=-24 3/8"; A=190 7/8"; A/2=95 7/16"; B=49 7/16"; B/2=24 23/32"; B/4=12 3/8"; C=112 7/8"; C/2=56 7/16"; CLASS=1"; D=80"; D-L-K-J=1 3/8"; D-M=42 1/2"; E=93 11/16"; E/2=46 27/32"; E/52*15=27 1/32"; F=52 3/4"; F/2=26 3/8"; H=50 3/4"; H/2=25 3/8"; HEIGHT=84 29/32"; J=13"; J+K+L=78 5/8"; K=25 7/8"; L=39 3/4"; M=37 1/2"; M-(2*(D-L-K-J))=34 3/4"; N=19 15/32"; N+(H/2)=44 27/32"; NOZZLE_BOTTOM_ID=34 3/4"; NOZZLE_BOTTOM_RAD=17 3/8"; NOZZLE_BOTTOM_RAD-3*2=11 3/8"; NOZZLE_HEIGHT=62"; NOZZLE_HEIGHT/7*2=15 1/2"; NOZZLE_SIZE=24"; NOZZLE_TOP_OD=36 1/2"; NOZZLE_TOP_RAD=18 1/4"; NOZZLE_WB/4=12 3/16"; NOZZLE_WB_OD=61"; NOZZLE_WB_RAD=30 1/2"; NOZZLE_WB_RAD-2"=28 1/2"; P=18 1/4"; R=44"; R*1.1=48 13/32"; R+((B/2)+1.5")=70 7/32"; R-((B/2)+1.5")=17 25/32"; TRANSITION=24 9/16"; TRANSITION/2=12 9/32"; Type Comments=Vari-Plume Laboratory Exhaust Centrifugal Airfoil Class 1 Arr 10
- 445_CAVP-24L_CLASS_1: ((M - (2 * (D - L - K - J))) / 2) + (TRANSITION / 2)=29 21/32"; (B/2)+1.5"=26 7/32"; (B/2)-.125"=24 19/32"; (D-J-K-L)*2=2 3/4"; (F-((F-H)/2))/2=24 3/8"; (M - (2 * (D - L - K - J)))/2=17 3/8"; (NOZZLE_HEIGHT - (NOZZLE_HEIGHT / 8 * 2)) / 2=23 1/4"; (NOZZLE_WB_OD - NOZZLE_TOP_OD) / 4=6 1/8"; -(F-((F-H)/2))/2=-24 3/8"; A=190 7/8"; A/2=95 7/16"; B=49 7/16"; B/2=24 23/32"; B/4=12 3/8"; C=112 7/8"; C/2=56 7/16"; CLASS=1"; D=80"; D-L-K-J=1 3/8"; D-M=42 1/2"; E=93 11/16"; E/2=46 27/32"; E/52*15=27 1/32"; F=52 3/4"; F/2=26 3/8"; H=50 3/4"; H/2=25 3/8"; HEIGHT=84 29/32"; J=13"; J+K+L=78 5/8"; K=25 7/8"; L=39 3/4"; M=37 1/2"; M-(2*(D-L-K-J))=34 3/4"; N=19 15/32"; N+(H/2)=44 27/32"; NOZZLE_BOTTOM_ID=34 3/4"; NOZZLE_BOTTOM_RAD=17 3/8"; NOZZLE_BOTTOM_RAD-3*2=11 3/8"; NOZZLE_HEIGHT=62"; NOZZLE_HEIGHT/7*2=15 1/2"; NOZZLE_SIZE=24"; NOZZLE_TOP_OD=36 1/2"; NOZZLE_TOP_RAD=18 1/4"; NOZZLE_WB/4=12 3/16"; NOZZLE_WB_OD=61"; NOZZLE_WB_RAD=30 1/2"; NOZZLE_WB_RAD-2"=28 1/2"; P=18 1/4"; R=44"; R*1.1=48 13/32"; R+((B/2)+1.5")=70 7/32"; R-((B/2)+1.5")=17 25/32"; TRANSITION=24 9/16"; TRANSITION/2=12 9/32"; Type Comments=Vari-Plume Laboratory Exhaust Centrifugal Airfoil Class 1 Arr 10
- 445_CAVP-30H_CLASS_1: ((M - (2 * (D - L - K - J))) / 2) + (TRANSITION / 2)=32 13/32"; (B/2)+1.5"=26 7/32"; (B/2)-.125"=24 19/32"; (D-J-K-L)*2=2 3/4"; (F-((F-H)/2))/2=24 3/8"; (M - (2 * (D - L - K - J)))/2=17 3/8"; (NOZZLE_HEIGHT - (NOZZLE_HEIGHT / 8 * 2)) / 2=29 1/4"; (NOZZLE_WB_OD - NOZZLE_TOP_OD) / 4=7 1/8"; -(F-((F-H)/2))/2=-24 3/8"; A=190 7/8"; A/2=95 7/16"; B=49 7/16"; B/2=24 23/32"; B/4=12 3/8"; C=112 7/8"; C/2=56 7/16"; CLASS=1"; D=80"; D-L-K-J=1 3/8"; D-M=42 1/2"; E=93 11/16"; E/2=46 27/32"; E/52*15=27 1/32"; F=52 3/4"; F/2=26 3/8"; H=50 3/4"; H/2=25 3/8"; HEIGHT=84 29/32"; J=13"; J+K+L=78 5/8"; K=25 7/8"; L=39 3/4"; M=37 1/2"; M-(2*(D-L-K-J))=34 3/4"; N=19 15/32"; N+(H/2)=44 27/32"; NOZZLE_BOTTOM_ID=42 1/2"; NOZZLE_BOTTOM_RAD=21 1/4"; NOZZLE_BOTTOM_RAD-3*2=15 1/4"; NOZZLE_HEIGHT=78"; NOZZLE_HEIGHT/7*2=19 1/2"; NOZZLE_SIZE=30"; NOZZLE_TOP_OD=45 1/2"; NOZZLE_TOP_RAD=22 3/4"; NOZZLE_WB/4=14 13/16"; NOZZLE_WB_OD=74"; NOZZLE_WB_RAD=37"; NOZZLE_WB_RAD-2"=35"; P=18 1/4"; R=44"; R*1.1=48 13/32"; R+((B/2)+1.5")=70 7/32"; R-((B/2)+1.5")=17 25/32"; TRANSITION=30 1/16"; TRANSITION/2=15 1/32"; Type Comments=Vari-Plume Laboratory Exhaust Centrifugal Airfoil Class 1 Arr 10
- 445_CAVP-30L_CLASS_1: ((M - (2 * (D - L - K - J))) / 2) + (TRANSITION / 2)=32 13/32"; (B/2)+1.5"=26 7/32"; (B/2)-.125"=24 19/32"; (D-J-K-L)*2=2 3/4"; (F-((F-H)/2))/2=24 3/8"; (M - (2 * (D - L - K - J)))/2=17 3/8"; (NOZZLE_HEIGHT - (NOZZLE_HEIGHT / 8 * 2)) / 2=29 1/4"; (NOZZLE_WB_OD - NOZZLE_TOP_OD) / 4=7 1/8"; -(F-((F-H)/2))/2=-24 3/8"; A=190 7/8"; A/2=95 7/16"; B=49 7/16"; B/2=24 23/32"; B/4=12 3/8"; C=112 7/8"; C/2=56 7/16"; CLASS=1"; D=80"; D-L-K-J=1 3/8"; D-M=42 1/2"; E=93 11/16"; E/2=46 27/32"; E/52*15=27 1/32"; F=52 3/4"; F/2=26 3/8"; H=50 3/4"; H/2=25 3/8"; HEIGHT=84 29/32"; J=13"; J+K+L=78 5/8"; K=25 7/8"; L=39 3/4"; M=37 1/2"; M-(2*(D-L-K-J))=34 3/4"; N=19 15/32"; N+(H/2)=44 27/32"; NOZZLE_BOTTOM_ID=42 1/2"; NOZZLE_BOTTOM_RAD=21 1/4"; NOZZLE_BOTTOM_RAD-3*2=15 1/4"; NOZZLE_HEIGHT=78"; NOZZLE_HEIGHT/7*2=19 1/2"; NOZZLE_SIZE=30"; NOZZLE_TOP_OD=45 1/2"; NOZZLE_TOP_RAD=22 3/4"; NOZZLE_WB/4=14 13/16"; NOZZLE_WB_OD=74"; NOZZLE_WB_RAD=37"; NOZZLE_WB_RAD-2"=35"; P=18 1/4"; R=44"; R*1.1=48 13/32"; R+((B/2)+1.5")=70 7/32"; R-((B/2)+1.5")=17 25/32"; TRANSITION=30 1/16"; TRANSITION/2=15 1/32"; Type Comments=Vari-Plume Laboratory Exhaust Centrifugal Airfoil Class 1 Arr 10
- 445_CAVP-24H_CLASS_2: ((M - (2 * (D - L - K - J))) / 2) + (TRANSITION / 2)=29 21/32"; (B/2)+1.5"=26 7/32"; (B/2)-.125"=24 19/32"; (D-J-K-L)*2=2 3/4"; (F-((F-H)/2))/2=24 3/8"; (M - (2 * (D - L - K - J)))/2=17 3/8"; (NOZZLE_HEIGHT - (NOZZLE_HEIGHT / 8 * 2)) / 2=23 1/4"; (NOZZLE_WB_OD - NOZZLE_TOP_OD) / 4=6 1/8"; -(F-((F-H)/2))/2=-24 3/8"; A=190 7/8"; A/2=95 7/16"; B=49 7/16"; B/2=24 23/32"; B/4=12 3/8"; C=112 7/8"; C/2=56 7/16"; CLASS=2"; D=80"; D-L-K-J=1 3/8"; D-M=42 1/2"; E=93 11/16"; E/2=46 27/32"; E/52*15=27 1/32"; F=52 3/4"; F/2=26 3/8"; H=50 3/4"; H/2=25 3/8"; HEIGHT=84 29/32"; J=13"; J+K+L=78 5/8"; K=25 7/8"; L=39 3/4"; M=37 1/2"; M-(2*(D-L-K-J))=34 3/4"; N=19 15/32"; N+(H/2)=44 27/32"; NOZZLE_BOTTOM_ID=34 3/4"; NOZZLE_BOTTOM_RAD=17 3/8"; NOZZLE_BOTTOM_RAD-3*2=11 3/8"; NOZZLE_HEIGHT=62"; NOZZLE_HEIGHT/7*2=15 1/2"; NOZZLE_SIZE=24"; NOZZLE_TOP_OD=36 1/2"; NOZZLE_TOP_RAD=18 1/4"; NOZZLE_WB/4=12 3/16"; NOZZLE_WB_OD=61"; NOZZLE_WB_RAD=30 1/2"; NOZZLE_WB_RAD-2"=28 1/2"; P=19 1/2"; R=44"; R*1.1=48 13/32"; R+((B/2)+1.5")=70 7/32"; R-((B/2)+1.5")=17 25/32"; TRANSITION=24 9/16"; TRANSITION/2=12 9/32"; Type Comments=Vari-Plume Laboratory Exhaust Centrifugal Airfoil Class 2 Arr 10
- 445_CAVP-24L_CLASS_2: ((M - (2 * (D - L - K - J))) / 2) + (TRANSITION / 2)=29 21/32"; (B/2)+1.5"=26 7/32"; (B/2)-.125"=24 19/32"; (D-J-K-L)*2=2 3/4"; (F-((F-H)/2))/2=24 3/8"; (M - (2 * (D - L - K - J)))/2=17 3/8"; (NOZZLE_HEIGHT - (NOZZLE_HEIGHT / 8 * 2)) / 2=23 1/4"; (NOZZLE_WB_OD - NOZZLE_TOP_OD) / 4=6 1/8"; -(F-((F-H)/2))/2=-24 3/8"; A=190 7/8"; A/2=95 7/16"; B=49 7/16"; B/2=24 23/32"; B/4=12 3/8"; C=112 7/8"; C/2=56 7/16"; CLASS=2"; D=80"; D-L-K-J=1 3/8"; D-M=42 1/2"; E=93 11/16"; E/2=46 27/32"; E/52*15=27 1/32"; F=52 3/4"; F/2=26 3/8"; H=50 3/4"; H/2=25 3/8"; HEIGHT=84 29/32"; J=13"; J+K+L=78 5/8"; K=25 7/8"; L=39 3/4"; M=37 1/2"; M-(2*(D-L-K-J))=34 3/4"; N=19 15/32"; N+(H/2)=44 27/32"; NOZZLE_BOTTOM_ID=34 3/4"; NOZZLE_BOTTOM_RAD=17 3/8"; NOZZLE_BOTTOM_RAD-3*2=11 3/8"; NOZZLE_HEIGHT=62"; NOZZLE_HEIGHT/7*2=15 1/2"; NOZZLE_SIZE=24"; NOZZLE_TOP_OD=36 1/2"; NOZZLE_TOP_RAD=18 1/4"; NOZZLE_WB/4=12 3/16"; NOZZLE_WB_OD=61"; NOZZLE_WB_RAD=30 1/2"; NOZZLE_WB_RAD-2"=28 1/2"; P=19 1/2"; R=44"; R*1.1=48 13/32"; R+((B/2)+1.5")=70 7/32"; R-((B/2)+1.5")=17 25/32"; TRANSITION=24 9/16"; TRANSITION/2=12 9/32"; Type Comments=Vari-Plume Laboratory Exhaust Centrifugal Airfoil Class 2 Arr 10
- 445_CAVP-30H_CLASS_2: ((M - (2 * (D - L - K - J))) / 2) + (TRANSITION / 2)=32 13/32"; (B/2)+1.5"=26 7/32"; (B/2)-.125"=24 19/32"; (D-J-K-L)*2=2 3/4"; (F-((F-H)/2))/2=24 3/8"; (M - (2 * (D - L - K - J)))/2=17 3/8"; (NOZZLE_HEIGHT - (NOZZLE_HEIGHT / 8 * 2)) / 2=29 1/4"; (NOZZLE_WB_OD - NOZZLE_TOP_OD) / 4=7 1/8"; -(F-((F-H)/2))/2=-24 3/8"; A=190 7/8"; A/2=95 7/16"; B=49 7/16"; B/2=24 23/32"; B/4=12 3/8"; C=112 7/8"; C/2=56 7/16"; CLASS=2"; D=80"; D-L-K-J=1 3/8"; D-M=42 1/2"; E=93 11/16"; E/2=46 27/32"; E/52*15=27 1/32"; F=52 3/4"; F/2=26 3/8"; H=50 3/4"; H/2=25 3/8"; HEIGHT=84 29/32"; J=13"; J+K+L=78 5/8"; K=25 7/8"; L=39 3/4"; M=37 1/2"; M-(2*(D-L-K-J))=34 3/4"; N=19 15/32"; N+(H/2)=44 27/32"; NOZZLE_BOTTOM_ID=42 1/2"; NOZZLE_BOTTOM_RAD=21 1/4"; NOZZLE_BOTTOM_RAD-3*2=15 1/4"; NOZZLE_HEIGHT=78"; NOZZLE_HEIGHT/7*2=19 1/2"; NOZZLE_SIZE=30"; NOZZLE_TOP_OD=45 1/2"; NOZZLE_TOP_RAD=22 3/4"; NOZZLE_WB/4=14 13/16"; NOZZLE_WB_OD=74"; NOZZLE_WB_RAD=37"; NOZZLE_WB_RAD-2"=35"; P=19 1/2"; R=44"; R*1.1=48 13/32"; R+((B/2)+1.5")=70 7/32"; R-((B/2)+1.5")=17 25/32"; TRANSITION=30 1/16"; TRANSITION/2=15 1/32"; Type Comments=Vari-Plume Laboratory Exhaust Centrifugal Airfoil Class 2 Arr 10
- 445_CAVP-30L_CLASS_2: ((M - (2 * (D - L - K - J))) / 2) + (TRANSITION / 2)=32 13/32"; (B/2)+1.5"=26 7/32"; (B/2)-.125"=24 19/32"; (D-J-K-L)*2=2 3/4"; (F-((F-H)/2))/2=24 3/8"; (M - (2 * (D - L - K - J)))/2=17 3/8"; (NOZZLE_HEIGHT - (NOZZLE_HEIGHT / 8 * 2)) / 2=29 1/4"; (NOZZLE_WB_OD - NOZZLE_TOP_OD) / 4=7 1/8"; -(F-((F-H)/2))/2=-24 3/8"; A=190 7/8"; A/2=95 7/16"; B=49 7/16"; B/2=24 23/32"; B/4=12 3/8"; C=112 7/8"; C/2=56 7/16"; CLASS=2"; D=80"; D-L-K-J=1 3/8"; D-M=42 1/2"; E=93 11/16"; E/2=46 27/32"; E/52*15=27 1/32"; F=52 3/4"; F/2=26 3/8"; H=50 3/4"; H/2=25 3/8"; HEIGHT=84 29/32"; J=13"; J+K+L=78 5/8"; K=25 7/8"; L=39 3/4"; M=37 1/2"; M-(2*(D-L-K-J))=34 3/4"; N=19 15/32"; N+(H/2)=44 27/32"; NOZZLE_BOTTOM_ID=42 1/2"; NOZZLE_BOTTOM_RAD=21 1/4"; NOZZLE_BOTTOM_RAD-3*2=15 1/4"; NOZZLE_HEIGHT=78"; NOZZLE_HEIGHT/7*2=19 1/2"; NOZZLE_SIZE=30"; NOZZLE_TOP_OD=45 1/2"; NOZZLE_TOP_RAD=22 3/4"; NOZZLE_WB/4=14 13/16"; NOZZLE_WB_OD=74"; NOZZLE_WB_RAD=37"; NOZZLE_WB_RAD-2"=35"; P=19 1/2"; R=44"; R*1.1=48 13/32"; R+((B/2)+1.5")=70 7/32"; R-((B/2)+1.5")=17 25/32"; TRANSITION=30 1/16"; TRANSITION/2=15 1/32"; Type Comments=Vari-Plume Laboratory Exhaust Centrifugal Airfoil Class 2 Arr 10
- 490_CAVP-24H_CLASS_1: ((M - (2 * (D - L - K - J))) / 2) + (TRANSITION / 2)=31 3/8"; (B/2)+1.5"=29"; (B/2)-.125"=27 3/8"; (D-J-K-L)*2=2 3/4"; (F-((F-H)/2))/2=27 27/32"; (M - (2 * (D - L - K - J)))/2=19 3/32"; (NOZZLE_HEIGHT - (NOZZLE_HEIGHT / 8 * 2)) / 2=23 1/4"; (NOZZLE_WB_OD - NOZZLE_TOP_OD) / 4=6 1/8"; -(F-((F-H)/2))/2=-27 27/32"; A=217 13/16"; A/2=108 29/32"; B=55"; B/2=27 1/2"; B/4=13 3/4"; C=123 1/16"; C/2=61 17/32"; CLASS=1"; D=79 15/16"; D-L-K-J=1 3/8"; D-M=39"; E=102 15/16"; E/2=51 15/32"; E/52*15=29 11/16"; F=59 11/16"; F/2=29 27/32"; H=57 11/16"; H/2=28 27/32"; HEIGHT=92 15/16"; J=13 1/2"; J+K+L=78 9/16"; K=21 7/8"; L=43 3/16"; M=40 15/16"; M-(2*(D-L-K-J))=38 3/16"; N=20 5/8"; N+(H/2)=49 15/32"; NOZZLE_BOTTOM_ID=34 3/4"; NOZZLE_BOTTOM_RAD=17 3/8"; NOZZLE_BOTTOM_RAD-3*2=11 3/8"; NOZZLE_HEIGHT=62"; NOZZLE_HEIGHT/7*2=15 1/2"; NOZZLE_SIZE=24"; NOZZLE_TOP_OD=36 1/2"; NOZZLE_TOP_RAD=18 1/4"; NOZZLE_WB/4=12 3/16"; NOZZLE_WB_OD=61"; NOZZLE_WB_RAD=30 1/2"; NOZZLE_WB_RAD-2"=28 1/2"; P=18 1/2"; R=48"; R*1.1=52 13/16"; R+((B/2)+1.5")=77"; R-((B/2)+1.5")=19"; TRANSITION=24 9/16"; TRANSITION/2=12 9/32"; Type Comments=Vari-Plume Laboratory Exhaust Centrifugal Airfoil Class 1 Arr 10
- 490_CAVP-24L_CLASS_1: ((M - (2 * (D - L - K - J))) / 2) + (TRANSITION / 2)=31 3/8"; (B/2)+1.5"=29"; (B/2)-.125"=27 3/8"; (D-J-K-L)*2=2 3/4"; (F-((F-H)/2))/2=27 27/32"; (M - (2 * (D - L - K - J)))/2=19 3/32"; (NOZZLE_HEIGHT - (NOZZLE_HEIGHT / 8 * 2)) / 2=23 1/4"; (NOZZLE_WB_OD - NOZZLE_TOP_OD) / 4=6 1/8"; -(F-((F-H)/2))/2=-27 27/32"; A=217 13/16"; A/2=108 29/32"; B=55"; B/2=27 1/2"; B/4=13 3/4"; C=123 1/16"; C/2=61 17/32"; CLASS=1"; D=79 15/16"; D-L-K-J=1 3/8"; D-M=39"; E=102 15/16"; E/2=51 15/32"; E/52*15=29 11/16"; F=59 11/16"; F/2=29 27/32"; H=57 11/16"; H/2=28 27/32"; HEIGHT=92 15/16"; J=13 1/2"; J+K+L=78 9/16"; K=21 7/8"; L=43 3/16"; M=40 15/16"; M-(2*(D-L-K-J))=38 3/16"; N=20 5/8"; N+(H/2)=49 15/32"; NOZZLE_BOTTOM_ID=34 3/4"; NOZZLE_BOTTOM_RAD=17 3/8"; NOZZLE_BOTTOM_RAD-3*2=11 3/8"; NOZZLE_HEIGHT=62"; NOZZLE_HEIGHT/7*2=15 1/2"; NOZZLE_SIZE=24"; NOZZLE_TOP_OD=36 1/2"; NOZZLE_TOP_RAD=18 1/4"; NOZZLE_WB/4=12 3/16"; NOZZLE_WB_OD=61"; NOZZLE_WB_RAD=30 1/2"; NOZZLE_WB_RAD-2"=28 1/2"; P=18 1/2"; R=48"; R*1.1=52 13/16"; R+((B/2)+1.5")=77"; R-((B/2)+1.5")=19"; TRANSITION=24 9/16"; TRANSITION/2=12 9/32"; Type Comments=Vari-Plume Laboratory Exhaust Centrifugal Airfoil Class 1 Arr 10
- 490_CAVP-30H_CLASS_1: ((M - (2 * (D - L - K - J))) / 2) + (TRANSITION / 2)=34 1/8"; (B/2)+1.5"=29"; (B/2)-.125"=27 3/8"; (D-J-K-L)*2=2 3/4"; (F-((F-H)/2))/2=27 27/32"; (M - (2 * (D - L - K - J)))/2=19 3/32"; (NOZZLE_HEIGHT - (NOZZLE_HEIGHT / 8 * 2)) / 2=29 1/4"; (NOZZLE_WB_OD - NOZZLE_TOP_OD) / 4=7 1/8"; -(F-((F-H)/2))/2=-27 27/32"; A=217 13/16"; A/2=108 29/32"; B=55"; B/2=27 1/2"; B/4=13 3/4"; C=123 1/16"; C/2=61 17/32"; CLASS=1"; D=79 15/16"; D-L-K-J=1 3/8"; D-M=39"; E=102 15/16"; E/2=51 15/32"; E/52*15=29 11/16"; F=59 11/16"; F/2=29 27/32"; H=57 11/16"; H/2=28 27/32"; HEIGHT=92 15/16"; J=13 1/2"; J+K+L=78 9/16"; K=21 7/8"; L=43 3/16"; M=40 15/16"; M-(2*(D-L-K-J))=38 3/16"; N=20 5/8"; N+(H/2)=49 15/32"; NOZZLE_BOTTOM_ID=42 1/2"; NOZZLE_BOTTOM_RAD=21 1/4"; NOZZLE_BOTTOM_RAD-3*2=15 1/4"; NOZZLE_HEIGHT=78"; NOZZLE_HEIGHT/7*2=19 1/2"; NOZZLE_SIZE=30"; NOZZLE_TOP_OD=45 1/2"; NOZZLE_TOP_RAD=22 3/4"; NOZZLE_WB/4=14 13/16"; NOZZLE_WB_OD=74"; NOZZLE_WB_RAD=37"; NOZZLE_WB_RAD-2"=35"; P=18 1/2"; R=48"; R*1.1=52 13/16"; R+((B/2)+1.5")=77"; R-((B/2)+1.5")=19"; TRANSITION=30 1/16"; TRANSITION/2=15 1/32"; Type Comments=Vari-Plume Laboratory Exhaust Centrifugal Airfoil Class 1 Arr 10
- 490_CAVP-30L_CLASS_1: ((M - (2 * (D - L - K - J))) / 2) + (TRANSITION / 2)=34 1/8"; (B/2)+1.5"=29"; (B/2)-.125"=27 3/8"; (D-J-K-L)*2=2 3/4"; (F-((F-H)/2))/2=27 27/32"; (M - (2 * (D - L - K - J)))/2=19 3/32"; (NOZZLE_HEIGHT - (NOZZLE_HEIGHT / 8 * 2)) / 2=29 1/4"; (NOZZLE_WB_OD - NOZZLE_TOP_OD) / 4=7 1/8"; -(F-((F-H)/2))/2=-27 27/32"; A=217 13/16"; A/2=108 29/32"; B=55"; B/2=27 1/2"; B/4=13 3/4"; C=123 1/16"; C/2=61 17/32"; CLASS=1"; D=79 15/16"; D-L-K-J=1 3/8"; D-M=39"; E=102 15/16"; E/2=51 15/32"; E/52*15=29 11/16"; F=59 11/16"; F/2=29 27/32"; H=57 11/16"; H/2=28 27/32"; HEIGHT=92 15/16"; J=13 1/2"; J+K+L=78 9/16"; K=21 7/8"; L=43 3/16"; M=40 15/16"; M-(2*(D-L-K-J))=38 3/16"; N=20 5/8"; N+(H/2)=49 15/32"; NOZZLE_BOTTOM_ID=42 1/2"; NOZZLE_BOTTOM_RAD=21 1/4"; NOZZLE_BOTTOM_RAD-3*2=15 1/4"; NOZZLE_HEIGHT=78"; NOZZLE_HEIGHT/7*2=19 1/2"; NOZZLE_SIZE=30"; NOZZLE_TOP_OD=45 1/2"; NOZZLE_TOP_RAD=22 3/4"; NOZZLE_WB/4=14 13/16"; NOZZLE_WB_OD=74"; NOZZLE_WB_RAD=37"; NOZZLE_WB_RAD-2"=35"; P=18 1/2"; R=48"; R*1.1=52 13/16"; R+((B/2)+1.5")=77"; R-((B/2)+1.5")=19"; TRANSITION=30 1/16"; TRANSITION/2=15 1/32"; Type Comments=Vari-Plume Laboratory Exhaust Centrifugal Airfoil Class 1 Arr 10
- 490_CAVP-36H_CLASS_1: ((M - (2 * (D - L - K - J))) / 2) + (TRANSITION / 2)=37 3/8"; (B/2)+1.5"=29"; (B/2)-.125"=27 3/8"; (D-J-K-L)*2=2 3/4"; (F-((F-H)/2))/2=27 27/32"; (M - (2 * (D - L - K - J)))/2=19 3/32"; (NOZZLE_HEIGHT - (NOZZLE_HEIGHT / 8 * 2)) / 2=35 5/8"; (NOZZLE_WB_OD - NOZZLE_TOP_OD) / 4=8"; -(F-((F-H)/2))/2=-27 27/32"; A=217 13/16"; A/2=108 29/32"; B=55"; B/2=27 1/2"; B/4=13 3/4"; C=123 1/16"; C/2=61 17/32"; CLASS=1"; D=79 15/16"; D-L-K-J=1 3/8"; D-M=39"; E=102 15/16"; E/2=51 15/32"; E/52*15=29 11/16"; F=59 11/16"; F/2=29 27/32"; H=57 11/16"; H/2=28 27/32"; HEIGHT=92 15/16"; J=13 1/2"; J+K+L=78 9/16"; K=21 7/8"; L=43 3/16"; M=40 15/16"; M-(2*(D-L-K-J))=38 3/16"; N=20 5/8"; N+(H/2)=49 15/32"; NOZZLE_BOTTOM_ID=51 3/4"; NOZZLE_BOTTOM_RAD=25 7/8"; NOZZLE_BOTTOM_RAD-3*2=19 7/8"; NOZZLE_HEIGHT=95"; NOZZLE_HEIGHT/7*2=23 3/4"; NOZZLE_SIZE=36"; NOZZLE_TOP_OD=58"; NOZZLE_TOP_RAD=29"; NOZZLE_WB/4=18"; NOZZLE_WB_OD=90"; NOZZLE_WB_RAD=45"; NOZZLE_WB_RAD-2"=43"; P=18 1/2"; R=48"; R*1.1=52 13/16"; R+((B/2)+1.5")=77"; R-((B/2)+1.5")=19"; TRANSITION=36 19/32"; TRANSITION/2=18 9/32"; Type Comments=Vari-Plume Laboratory Exhaust Centrifugal Airfoil Class 1 Arr 10
- 490_CAVP-36L_CLASS_1: ((M - (2 * (D - L - K - J))) / 2) + (TRANSITION / 2)=37 3/8"; (B/2)+1.5"=29"; (B/2)-.125"=27 3/8"; (D-J-K-L)*2=2 3/4"; (F-((F-H)/2))/2=27 27/32"; (M - (2 * (D - L - K - J)))/2=19 3/32"; (NOZZLE_HEIGHT - (NOZZLE_HEIGHT / 8 * 2)) / 2=35 5/8"; (NOZZLE_WB_OD - NOZZLE_TOP_OD) / 4=8"; -(F-((F-H)/2))/2=-27 27/32"; A=217 13/16"; A/2=108 29/32"; B=55"; B/2=27 1/2"; B/4=13 3/4"; C=123 1/16"; C/2=61 17/32"; CLASS=1"; D=79 15/16"; D-L-K-J=1 3/8"; D-M=39"; E=102 15/16"; E/2=51 15/32"; E/52*15=29 11/16"; F=59 11/16"; F/2=29 27/32"; H=57 11/16"; H/2=28 27/32"; HEIGHT=92 15/16"; J=13 1/2"; J+K+L=78 9/16"; K=21 7/8"; L=43 3/16"; M=40 15/16"; M-(2*(D-L-K-J))=38 3/16"; N=20 5/8"; N+(H/2)=49 15/32"; NOZZLE_BOTTOM_ID=51 3/4"; NOZZLE_BOTTOM_RAD=25 7/8"; NOZZLE_BOTTOM_RAD-3*2=19 7/8"; NOZZLE_HEIGHT=95"; NOZZLE_HEIGHT/7*2=23 3/4"; NOZZLE_SIZE=36"; NOZZLE_TOP_OD=58"; NOZZLE_TOP_RAD=29"; NOZZLE_WB/4=18"; NOZZLE_WB_OD=90"; NOZZLE_WB_RAD=45"; NOZZLE_WB_RAD-2"=43"; P=18 1/2"; R=48"; R*1.1=52 13/16"; R+((B/2)+1.5")=77"; R-((B/2)+1.5")=19"; TRANSITION=36 19/32"; TRANSITION/2=18 9/32"; Type Comments=Vari-Plume Laboratory Exhaust Centrifugal Airfoil Class 1 Arr 10
- 490_CAVP-24H_CLASS_2: ((M - (2 * (D - L - K - J))) / 2) + (TRANSITION / 2)=31 3/8"; (B/2)+1.5"=29"; (B/2)-.125"=27 3/8"; (D-J-K-L)*2=2 3/4"; (F-((F-H)/2))/2=27 27/32"; (M - (2 * (D - L - K - J)))/2=19 3/32"; (NOZZLE_HEIGHT - (NOZZLE_HEIGHT / 8 * 2)) / 2=23 1/4"; (NOZZLE_WB_OD - NOZZLE_TOP_OD) / 4=6 1/8"; -(F-((F-H)/2))/2=-27 27/32"; A=217 13/16"; A/2=108 29/32"; B=55"; B/2=27 1/2"; B/4=13 3/4"; C=123 1/16"; C/2=61 17/32"; CLASS=2"; D=83 15/16"; D-L-K-J=1 3/8"; D-M=43"; E=102 15/16"; E/2=51 15/32"; E/52*15=29 11/16"; F=59 11/16"; F/2=29 27/32"; H=57 11/16"; H/2=28 27/32"; HEIGHT=92 15/16"; J=13 1/2"; J+K+L=82 9/16"; K=25 7/8"; L=43 3/16"; M=40 15/16"; M-(2*(D-L-K-J))=38 3/16"; N=20 5/8"; N+(H/2)=49 15/32"; NOZZLE_BOTTOM_ID=34 3/4"; NOZZLE_BOTTOM_RAD=17 3/8"; NOZZLE_BOTTOM_RAD-3*2=11 3/8"; NOZZLE_HEIGHT=62"; NOZZLE_HEIGHT/7*2=15 1/2"; NOZZLE_SIZE=24"; NOZZLE_TOP_OD=36 1/2"; NOZZLE_TOP_RAD=18 1/4"; NOZZLE_WB/4=12 3/16"; NOZZLE_WB_OD=61"; NOZZLE_WB_RAD=30 1/2"; NOZZLE_WB_RAD-2"=28 1/2"; P=21 7/8"; R=48"; R*1.1=52 13/16"; R+((B/2)+1.5")=77"; R-((B/2)+1.5")=19"; TRANSITION=24 9/16"; TRANSITION/2=12 9/32"; Type Comments=Vari-Plume Laboratory Exhaust Centrifugal Airfoil Class 2 Arr 10
- 490_CAVP-24L_CLASS_2: ((M - (2 * (D - L - K - J))) / 2) + (TRANSITION / 2)=31 3/8"; (B/2)+1.5"=29"; (B/2)-.125"=27 3/8"; (D-J-K-L)*2=2 3/4"; (F-((F-H)/2))/2=27 27/32"; (M - (2 * (D - L - K - J)))/2=19 3/32"; (NOZZLE_HEIGHT - (NOZZLE_HEIGHT / 8 * 2)) / 2=23 1/4"; (NOZZLE_WB_OD - NOZZLE_TOP_OD) / 4=6 1/8"; -(F-((F-H)/2))/2=-27 27/32"; A=217 13/16"; A/2=108 29/32"; B=55"; B/2=27 1/2"; B/4=13 3/4"; C=123 1/16"; C/2=61 17/32"; CLASS=2"; D=83 15/16"; D-L-K-J=1 3/8"; D-M=43"; E=102 15/16"; E/2=51 15/32"; E/52*15=29 11/16"; F=59 11/16"; F/2=29 27/32"; H=57 11/16"; H/2=28 27/32"; HEIGHT=92 15/16"; J=13 1/2"; J+K+L=82 9/16"; K=25 7/8"; L=43 3/16"; M=40 15/16"; M-(2*(D-L-K-J))=38 3/16"; N=20 5/8"; N+(H/2)=49 15/32"; NOZZLE_BOTTOM_ID=34 3/4"; NOZZLE_BOTTOM_RAD=17 3/8"; NOZZLE_BOTTOM_RAD-3*2=11 3/8"; NOZZLE_HEIGHT=62"; NOZZLE_HEIGHT/7*2=15 1/2"; NOZZLE_SIZE=24"; NOZZLE_TOP_OD=36 1/2"; NOZZLE_TOP_RAD=18 1/4"; NOZZLE_WB/4=12 3/16"; NOZZLE_WB_OD=61"; NOZZLE_WB_RAD=30 1/2"; NOZZLE_WB_RAD-2"=28 1/2"; P=21 7/8"; R=48"; R*1.1=52 13/16"; R+((B/2)+1.5")=77"; R-((B/2)+1.5")=19"; TRANSITION=24 9/16"; TRANSITION/2=12 9/32"; Type Comments=Vari-Plume Laboratory Exhaust Centrifugal Airfoil Class 2 Arr 10
- 490_CAVP-30H_CLASS_2: ((M - (2 * (D - L - K - J))) / 2) + (TRANSITION / 2)=34 1/8"; (B/2)+1.5"=29"; (B/2)-.125"=27 3/8"; (D-J-K-L)*2=2 3/4"; (F-((F-H)/2))/2=27 27/32"; (M - (2 * (D - L - K - J)))/2=19 3/32"; (NOZZLE_HEIGHT - (NOZZLE_HEIGHT / 8 * 2)) / 2=29 1/4"; (NOZZLE_WB_OD - NOZZLE_TOP_OD) / 4=7 1/8"; -(F-((F-H)/2))/2=-27 27/32"; A=217 13/16"; A/2=108 29/32"; B=55"; B/2=27 1/2"; B/4=13 3/4"; C=123 1/16"; C/2=61 17/32"; CLASS=2"; D=83 15/16"; D-L-K-J=1 3/8"; D-M=43"; E=102 15/16"; E/2=51 15/32"; E/52*15=29 11/16"; F=59 11/16"; F/2=29 27/32"; H=57 11/16"; H/2=28 27/32"; HEIGHT=92 15/16"; J=13 1/2"; J+K+L=82 9/16"; K=25 7/8"; L=43 3/16"; M=40 15/16"; M-(2*(D-L-K-J))=38 3/16"; N=20 5/8"; N+(H/2)=49 15/32"; NOZZLE_BOTTOM_ID=42 1/2"; NOZZLE_BOTTOM_RAD=21 1/4"; NOZZLE_BOTTOM_RAD-3*2=15 1/4"; NOZZLE_HEIGHT=78"; NOZZLE_HEIGHT/7*2=19 1/2"; NOZZLE_SIZE=30"; NOZZLE_TOP_OD=45 1/2"; NOZZLE_TOP_RAD=22 3/4"; NOZZLE_WB/4=14 13/16"; NOZZLE_WB_OD=74"; NOZZLE_WB_RAD=37"; NOZZLE_WB_RAD-2"=35"; P=21 7/8"; R=48"; R*1.1=52 13/16"; R+((B/2)+1.5")=77"; R-((B/2)+1.5")=19"; TRANSITION=30 1/16"; TRANSITION/2=15 1/32"; Type Comments=Vari-Plume Laboratory Exhaust Centrifugal Airfoil Class 2 Arr 10
- 490_CAVP-30L_CLASS_2: ((M - (2 * (D - L - K - J))) / 2) + (TRANSITION / 2)=34 1/8"; (B/2)+1.5"=29"; (B/2)-.125"=27 3/8"; (D-J-K-L)*2=2 3/4"; (F-((F-H)/2))/2=27 27/32"; (M - (2 * (D - L - K - J)))/2=19 3/32"; (NOZZLE_HEIGHT - (NOZZLE_HEIGHT / 8 * 2)) / 2=29 1/4"; (NOZZLE_WB_OD - NOZZLE_TOP_OD) / 4=7 1/8"; -(F-((F-H)/2))/2=-27 27/32"; A=217 13/16"; A/2=108 29/32"; B=55"; B/2=27 1/2"; B/4=13 3/4"; C=123 1/16"; C/2=61 17/32"; CLASS=2"; D=83 15/16"; D-L-K-J=1 3/8"; D-M=43"; E=102 15/16"; E/2=51 15/32"; E/52*15=29 11/16"; F=59 11/16"; F/2=29 27/32"; H=57 11/16"; H/2=28 27/32"; HEIGHT=92 15/16"; J=13 1/2"; J+K+L=82 9/16"; K=25 7/8"; L=43 3/16"; M=40 15/16"; M-(2*(D-L-K-J))=38 3/16"; N=20 5/8"; N+(H/2)=49 15/32"; NOZZLE_BOTTOM_ID=42 1/2"; NOZZLE_BOTTOM_RAD=21 1/4"; NOZZLE_BOTTOM_RAD-3*2=15 1/4"; NOZZLE_HEIGHT=78"; NOZZLE_HEIGHT/7*2=19 1/2"; NOZZLE_SIZE=30"; NOZZLE_TOP_OD=45 1/2"; NOZZLE_TOP_RAD=22 3/4"; NOZZLE_WB/4=14 13/16"; NOZZLE_WB_OD=74"; NOZZLE_WB_RAD=37"; NOZZLE_WB_RAD-2"=35"; P=21 7/8"; R=48"; R*1.1=52 13/16"; R+((B/2)+1.5")=77"; R-((B/2)+1.5")=19"; TRANSITION=30 1/16"; TRANSITION/2=15 1/32"; Type Comments=Vari-Plume Laboratory Exhaust Centrifugal Airfoil Class 2 Arr 10
- 490_CAVP-36H_CLASS_2: ((M - (2 * (D - L - K - J))) / 2) + (TRANSITION / 2)=37 3/8"; (B/2)+1.5"=29"; (B/2)-.125"=27 3/8"; (D-J-K-L)*2=2 3/4"; (F-((F-H)/2))/2=27 27/32"; (M - (2 * (D - L - K - J)))/2=19 3/32"; (NOZZLE_HEIGHT - (NOZZLE_HEIGHT / 8 * 2)) / 2=35 5/8"; (NOZZLE_WB_OD - NOZZLE_TOP_OD) / 4=8"; -(F-((F-H)/2))/2=-27 27/32"; A=217 13/16"; A/2=108 29/32"; B=55"; B/2=27 1/2"; B/4=13 3/4"; C=123 1/16"; C/2=61 17/32"; CLASS=2"; D=83 15/16"; D-L-K-J=1 3/8"; D-M=43"; E=102 15/16"; E/2=51 15/32"; E/52*15=29 11/16"; F=59 11/16"; F/2=29 27/32"; H=57 11/16"; H/2=28 27/32"; HEIGHT=92 15/16"; J=13 1/2"; J+K+L=82 9/16"; K=25 7/8"; L=43 3/16"; M=40 15/16"; M-(2*(D-L-K-J))=38 3/16"; N=20 5/8"; N+(H/2)=49 15/32"; NOZZLE_BOTTOM_ID=51 3/4"; NOZZLE_BOTTOM_RAD=25 7/8"; NOZZLE_BOTTOM_RAD-3*2=19 7/8"; NOZZLE_HEIGHT=95"; NOZZLE_HEIGHT/7*2=23 3/4"; NOZZLE_SIZE=36"; NOZZLE_TOP_OD=58"; NOZZLE_TOP_RAD=29"; NOZZLE_WB/4=18"; NOZZLE_WB_OD=90"; NOZZLE_WB_RAD=45"; NOZZLE_WB_RAD-2"=43"; P=21 7/8"; R=48"; R*1.1=52 13/16"; R+((B/2)+1.5")=77"; R-((B/2)+1.5")=19"; TRANSITION=36 19/32"; TRANSITION/2=18 9/32"; Type Comments=Vari-Plume Laboratory Exhaust Centrifugal Airfoil Class 2 Arr 10
- 490_CAVP-36L_CLASS_2: ((M - (2 * (D - L - K - J))) / 2) + (TRANSITION / 2)=37 3/8"; (B/2)+1.5"=29"; (B/2)-.125"=27 3/8"; (D-J-K-L)*2=2 3/4"; (F-((F-H)/2))/2=27 27/32"; (M - (2 * (D - L - K - J)))/2=19 3/32"; (NOZZLE_HEIGHT - (NOZZLE_HEIGHT / 8 * 2)) / 2=35 5/8"; (NOZZLE_WB_OD - NOZZLE_TOP_OD) / 4=8"; -(F-((F-H)/2))/2=-27 27/32"; A=217 13/16"; A/2=108 29/32"; B=55"; B/2=27 1/2"; B/4=13 3/4"; C=123 1/16"; C/2=61 17/32"; CLASS=2"; D=83 15/16"; D-L-K-J=1 3/8"; D-M=43"; E=102 15/16"; E/2=51 15/32"; E/52*15=29 11/16"; F=59 11/16"; F/2=29 27/32"; H=57 11/16"; H/2=28 27/32"; HEIGHT=92 15/16"; J=13 1/2"; J+K+L=82 9/16"; K=25 7/8"; L=43 3/16"; M=40 15/16"; M-(2*(D-L-K-J))=38 3/16"; N=20 5/8"; N+(H/2)=49 15/32"; NOZZLE_BOTTOM_ID=51 3/4"; NOZZLE_BOTTOM_RAD=25 7/8"; NOZZLE_BOTTOM_RAD-3*2=19 7/8"; NOZZLE_HEIGHT=95"; NOZZLE_HEIGHT/7*2=23 3/4"; NOZZLE_SIZE=36"; NOZZLE_TOP_OD=58"; NOZZLE_TOP_RAD=29"; NOZZLE_WB/4=18"; NOZZLE_WB_OD=90"; NOZZLE_WB_RAD=45"; NOZZLE_WB_RAD-2"=43"; P=21 7/8"; R=48"; R*1.1=52 13/16"; R+((B/2)+1.5")=77"; R-((B/2)+1.5")=19"; TRANSITION=36 19/32"; TRANSITION/2=18 9/32"; Type Comments=Vari-Plume Laboratory Exhaust Centrifugal Airfoil Class 2 Arr 10
- 540_CAVP-30H_CLASS_1: ((M - (2 * (D - L - K - J))) / 2) + (TRANSITION / 2)=36 1/32"; (B/2)+1.5"=31 1/2"; (B/2)-.125"=29 7/8"; (D-J-K-L)*2=2 3/4"; (F-((F-H)/2))/2=30 11/32"; (M - (2 * (D - L - K - J)))/2=21"; (NOZZLE_HEIGHT - (NOZZLE_HEIGHT / 8 * 2)) / 2=29 1/4"; (NOZZLE_WB_OD - NOZZLE_TOP_OD) / 4=7 1/8"; -(F-((F-H)/2))/2=-30 11/32"; A=231 5/16"; A/2=115 21/32"; B=60"; B/2=30"; B/4=15"; C=136 9/16"; C/2=68 9/32"; CLASS=1"; D=88 1/4"; D-L-K-J=1 3/8"; D-M=43 1/2"; E=113 3/16"; E/2=56 19/32"; E/52*15=32 21/32"; F=64 11/16"; F/2=32 11/32"; H=62 11/16"; H/2=31 11/32"; HEIGHT=102 7/16"; J=14"; J+K+L=86 7/8"; K=25 7/8"; L=47"; M=44 3/4"; M-(2*(D-L-K-J))=42"; N=23 1/4"; N+(H/2)=54 19/32"; NOZZLE_BOTTOM_ID=42 1/2"; NOZZLE_BOTTOM_RAD=21 1/4"; NOZZLE_BOTTOM_RAD-3*2=15 1/4"; NOZZLE_HEIGHT=78"; NOZZLE_HEIGHT/7*2=19 1/2"; NOZZLE_SIZE=30"; NOZZLE_TOP_OD=45 1/2"; NOZZLE_TOP_RAD=22 3/4"; NOZZLE_WB/4=14 13/16"; NOZZLE_WB_OD=74"; NOZZLE_WB_RAD=37"; NOZZLE_WB_RAD-2"=35"; P=18 1/2"; R=53"; R*1.1=58 5/16"; R+((B/2)+1.5")=84 1/2"; R-((B/2)+1.5")=21 1/2"; TRANSITION=30 1/16"; TRANSITION/2=15 1/32"; Type Comments=Vari-Plume Laboratory Exhaust Centrifugal Airfoil Class 1 Arr 10
- 540_CAVP-30L_CLASS_1: ((M - (2 * (D - L - K - J))) / 2) + (TRANSITION / 2)=36 1/32"; (B/2)+1.5"=31 1/2"; (B/2)-.125"=29 7/8"; (D-J-K-L)*2=2 3/4"; (F-((F-H)/2))/2=30 11/32"; (M - (2 * (D - L - K - J)))/2=21"; (NOZZLE_HEIGHT - (NOZZLE_HEIGHT / 8 * 2)) / 2=29 1/4"; (NOZZLE_WB_OD - NOZZLE_TOP_OD) / 4=7 1/8"; -(F-((F-H)/2))/2=-30 11/32"; A=231 5/16"; A/2=115 21/32"; B=60"; B/2=30"; B/4=15"; C=136 9/16"; C/2=68 9/32"; CLASS=1"; D=88 1/4"; D-L-K-J=1 3/8"; D-M=43 1/2"; E=113 3/16"; E/2=56 19/32"; E/52*15=32 21/32"; F=64 11/16"; F/2=32 11/32"; H=62 11/16"; H/2=31 11/32"; HEIGHT=102 7/16"; J=14"; J+K+L=86 7/8"; K=25 7/8"; L=47"; M=44 3/4"; M-(2*(D-L-K-J))=42"; N=23 1/4"; N+(H/2)=54 19/32"; NOZZLE_BOTTOM_ID=42 1/2"; NOZZLE_BOTTOM_RAD=21 1/4"; NOZZLE_BOTTOM_RAD-3*2=15 1/4"; NOZZLE_HEIGHT=78"; NOZZLE_HEIGHT/7*2=19 1/2"; NOZZLE_SIZE=30"; NOZZLE_TOP_OD=45 1/2"; NOZZLE_TOP_RAD=22 3/4"; NOZZLE_WB/4=14 13/16"; NOZZLE_WB_OD=74"; NOZZLE_WB_RAD=37"; NOZZLE_WB_RAD-2"=35"; P=18 1/2"; R=53"; R*1.1=58 5/16"; R+((B/2)+1.5")=84 1/2"; R-((B/2)+1.5")=21 1/2"; TRANSITION=30 1/16"; TRANSITION/2=15 1/32"; Type Comments=Vari-Plume Laboratory Exhaust Centrifugal Airfoil Class 1 Arr 10
- 540_CAVP-36H_CLASS_1: ((M - (2 * (D - L - K - J))) / 2) + (TRANSITION / 2)=39 9/32"; (B/2)+1.5"=31 1/2"; (B/2)-.125"=29 7/8"; (D-J-K-L)*2=2 3/4"; (F-((F-H)/2))/2=30 11/32"; (M - (2 * (D - L - K - J)))/2=21"; (NOZZLE_HEIGHT - (NOZZLE_HEIGHT / 8 * 2)) / 2=35 5/8"; (NOZZLE_WB_OD - NOZZLE_TOP_OD) / 4=8"; -(F-((F-H)/2))/2=-30 11/32"; A=231 5/16"; A/2=115 21/32"; B=60"; B/2=30"; B/4=15"; C=136 9/16"; C/2=68 9/32"; CLASS=1"; D=88 1/4"; D-L-K-J=1 3/8"; D-M=43 1/2"; E=113 3/16"; E/2=56 19/32"; E/52*15=32 21/32"; F=64 11/16"; F/2=32 11/32"; H=62 11/16"; H/2=31 11/32"; HEIGHT=102 7/16"; J=14"; J+K+L=86 7/8"; K=25 7/8"; L=47"; M=44 3/4"; M-(2*(D-L-K-J))=42"; N=23 1/4"; N+(H/2)=54 19/32"; NOZZLE_BOTTOM_ID=51 3/4"; NOZZLE_BOTTOM_RAD=25 7/8"; NOZZLE_BOTTOM_RAD-3*2=19 7/8"; NOZZLE_HEIGHT=95"; NOZZLE_HEIGHT/7*2=23 3/4"; NOZZLE_SIZE=36"; NOZZLE_TOP_OD=58"; NOZZLE_TOP_RAD=29"; NOZZLE_WB/4=18"; NOZZLE_WB_OD=90"; NOZZLE_WB_RAD=45"; NOZZLE_WB_RAD-2"=43"; P=18 1/2"; R=53"; R*1.1=58 5/16"; R+((B/2)+1.5")=84 1/2"; R-((B/2)+1.5")=21 1/2"; TRANSITION=36 19/32"; TRANSITION/2=18 9/32"; Type Comments=Vari-Plume Laboratory Exhaust Centrifugal Airfoil Class 1 Arr 10
- 540_CAVP-36L_CLASS_1: ((M - (2 * (D - L - K - J))) / 2) + (TRANSITION / 2)=39 9/32"; (B/2)+1.5"=31 1/2"; (B/2)-.125"=29 7/8"; (D-J-K-L)*2=2 3/4"; (F-((F-H)/2))/2=30 11/32"; (M - (2 * (D - L - K - J)))/2=21"; (NOZZLE_HEIGHT - (NOZZLE_HEIGHT / 8 * 2)) / 2=35 5/8"; (NOZZLE_WB_OD - NOZZLE_TOP_OD) / 4=8"; -(F-((F-H)/2))/2=-30 11/32"; A=231 5/16"; A/2=115 21/32"; B=60"; B/2=30"; B/4=15"; C=136 9/16"; C/2=68 9/32"; CLASS=1"; D=88 1/4"; D-L-K-J=1 3/8"; D-M=43 1/2"; E=113 3/16"; E/2=56 19/32"; E/52*15=32 21/32"; F=64 11/16"; F/2=32 11/32"; H=62 11/16"; H/2=31 11/32"; HEIGHT=102 7/16"; J=14"; J+K+L=86 7/8"; K=25 7/8"; L=47"; M=44 3/4"; M-(2*(D-L-K-J))=42"; N=23 1/4"; N+(H/2)=54 19/32"; NOZZLE_BOTTOM_ID=51 3/4"; NOZZLE_BOTTOM_RAD=25 7/8"; NOZZLE_BOTTOM_RAD-3*2=19 7/8"; NOZZLE_HEIGHT=95"; NOZZLE_HEIGHT/7*2=23 3/4"; NOZZLE_SIZE=36"; NOZZLE_TOP_OD=58"; NOZZLE_TOP_RAD=29"; NOZZLE_WB/4=18"; NOZZLE_WB_OD=90"; NOZZLE_WB_RAD=45"; NOZZLE_WB_RAD-2"=43"; P=18 1/2"; R=53"; R*1.1=58 5/16"; R+((B/2)+1.5")=84 1/2"; R-((B/2)+1.5")=21 1/2"; TRANSITION=36 19/32"; TRANSITION/2=18 9/32"; Type Comments=Vari-Plume Laboratory Exhaust Centrifugal Airfoil Class 1 Arr 10
- 540_CAVP-30H_CLASS_2: ((M - (2 * (D - L - K - J))) / 2) + (TRANSITION / 2)=36 1/32"; (B/2)+1.5"=31 1/2"; (B/2)-.125"=29 7/8"; (D-J-K-L)*2=2 3/4"; (F-((F-H)/2))/2=30 11/32"; (M - (2 * (D - L - K - J)))/2=21"; (NOZZLE_HEIGHT - (NOZZLE_HEIGHT / 8 * 2)) / 2=29 1/4"; (NOZZLE_WB_OD - NOZZLE_TOP_OD) / 4=7 1/8"; -(F-((F-H)/2))/2=-30 11/32"; A=231 5/16"; A/2=115 21/32"; B=60"; B/2=30"; B/4=15"; C=136 9/16"; C/2=68 9/32"; CLASS=2"; D=92 1/2"; D-L-K-J=1 3/8"; D-M=47 3/4"; E=113 3/16"; E/2=56 19/32"; E/52*15=32 21/32"; F=64 11/16"; F/2=32 11/32"; H=62 11/16"; H/2=31 11/32"; HEIGHT=102 7/16"; J=14"; J+K+L=91 1/8"; K=30 1/8"; L=47"; M=44 3/4"; M-(2*(D-L-K-J))=42"; N=23 1/4"; N+(H/2)=54 19/32"; NOZZLE_BOTTOM_ID=42 1/2"; NOZZLE_BOTTOM_RAD=21 1/4"; NOZZLE_BOTTOM_RAD-3*2=15 1/4"; NOZZLE_HEIGHT=78"; NOZZLE_HEIGHT/7*2=19 1/2"; NOZZLE_SIZE=30"; NOZZLE_TOP_OD=45 1/2"; NOZZLE_TOP_RAD=22 3/4"; NOZZLE_WB/4=14 13/16"; NOZZLE_WB_OD=74"; NOZZLE_WB_RAD=37"; NOZZLE_WB_RAD-2"=35"; P=25 3/4"; R=53"; R*1.1=58 5/16"; R+((B/2)+1.5")=84 1/2"; R-((B/2)+1.5")=21 1/2"; TRANSITION=30 1/16"; TRANSITION/2=15 1/32"; Type Comments=Vari-Plume Laboratory Exhaust Centrifugal Airfoil Class 2 Arr 10
- 540_CAVP-30L_CLASS_2: ((M - (2 * (D - L - K - J))) / 2) + (TRANSITION / 2)=36 1/32"; (B/2)+1.5"=31 1/2"; (B/2)-.125"=29 7/8"; (D-J-K-L)*2=2 3/4"; (F-((F-H)/2))/2=30 11/32"; (M - (2 * (D - L - K - J)))/2=21"; (NOZZLE_HEIGHT - (NOZZLE_HEIGHT / 8 * 2)) / 2=29 1/4"; (NOZZLE_WB_OD - NOZZLE_TOP_OD) / 4=7 1/8"; -(F-((F-H)/2))/2=-30 11/32"; A=231 5/16"; A/2=115 21/32"; B=60"; B/2=30"; B/4=15"; C=136 9/16"; C/2=68 9/32"; CLASS=2"; D=92 1/2"; D-L-K-J=1 3/8"; D-M=47 3/4"; E=113 3/16"; E/2=56 19/32"; E/52*15=32 21/32"; F=64 11/16"; F/2=32 11/32"; H=62 11/16"; H/2=31 11/32"; HEIGHT=102 7/16"; J=14"; J+K+L=91 1/8"; K=30 1/8"; L=47"; M=44 3/4"; M-(2*(D-L-K-J))=42"; N=23 1/4"; N+(H/2)=54 19/32"; NOZZLE_BOTTOM_ID=42 1/2"; NOZZLE_BOTTOM_RAD=21 1/4"; NOZZLE_BOTTOM_RAD-3*2=15 1/4"; NOZZLE_HEIGHT=78"; NOZZLE_HEIGHT/7*2=19 1/2"; NOZZLE_SIZE=30"; NOZZLE_TOP_OD=45 1/2"; NOZZLE_TOP_RAD=22 3/4"; NOZZLE_WB/4=14 13/16"; NOZZLE_WB_OD=74"; NOZZLE_WB_RAD=37"; NOZZLE_WB_RAD-2"=35"; P=25 3/4"; R=53"; R*1.1=58 5/16"; R+((B/2)+1.5")=84 1/2"; R-((B/2)+1.5")=21 1/2"; TRANSITION=30 1/16"; TRANSITION/2=15 1/32"; Type Comments=Vari-Plume Laboratory Exhaust Centrifugal Airfoil Class 2 Arr 10
- 540_CAVP-36H_CLASS_2: ((M - (2 * (D - L - K - J))) / 2) + (TRANSITION / 2)=39 9/32"; (B/2)+1.5"=31 1/2"; (B/2)-.125"=29 7/8"; (D-J-K-L)*2=2 3/4"; (F-((F-H)/2))/2=30 11/32"; (M - (2 * (D - L - K - J)))/2=21"; (NOZZLE_HEIGHT - (NOZZLE_HEIGHT / 8 * 2)) / 2=35 5/8"; (NOZZLE_WB_OD - NOZZLE_TOP_OD) / 4=8"; -(F-((F-H)/2))/2=-30 11/32"; A=231 5/16"; A/2=115 21/32"; B=60"; B/2=30"; B/4=15"; C=136 9/16"; C/2=68 9/32"; CLASS=2"; D=92 1/2"; D-L-K-J=1 3/8"; D-M=47 3/4"; E=113 3/16"; E/2=56 19/32"; E/52*15=32 21/32"; F=64 11/16"; F/2=32 11/32"; H=62 11/16"; H/2=31 11/32"; HEIGHT=102 7/16"; J=14"; J+K+L=91 1/8"; K=30 1/8"; L=47"; M=44 3/4"; M-(2*(D-L-K-J))=42"; N=23 1/4"; N+(H/2)=54 19/32"; NOZZLE_BOTTOM_ID=51 3/4"; NOZZLE_BOTTOM_RAD=25 7/8"; NOZZLE_BOTTOM_RAD-3*2=19 7/8"; NOZZLE_HEIGHT=95"; NOZZLE_HEIGHT/7*2=23 3/4"; NOZZLE_SIZE=36"; NOZZLE_TOP_OD=58"; NOZZLE_TOP_RAD=29"; NOZZLE_WB/4=18"; NOZZLE_WB_OD=90"; NOZZLE_WB_RAD=45"; NOZZLE_WB_RAD-2"=43"; P=25 3/4"; R=53"; R*1.1=58 5/16"; R+((B/2)+1.5")=84 1/2"; R-((B/2)+1.5")=21 1/2"; TRANSITION=36 19/32"; TRANSITION/2=18 9/32"; Type Comments=Vari-Plume Laboratory Exhaust Centrifugal Airfoil Class 2 Arr 10
- 540_CAVP-36L_CLASS_2: ((M - (2 * (D - L - K - J))) / 2) + (TRANSITION / 2)=39 9/32"; (B/2)+1.5"=31 1/2"; (B/2)-.125"=29 7/8"; (D-J-K-L)*2=2 3/4"; (F-((F-H)/2))/2=30 11/32"; (M - (2 * (D - L - K - J)))/2=21"; (NOZZLE_HEIGHT - (NOZZLE_HEIGHT / 8 * 2)) / 2=35 5/8"; (NOZZLE_WB_OD - NOZZLE_TOP_OD) / 4=8"; -(F-((F-H)/2))/2=-30 11/32"; A=231 5/16"; A/2=115 21/32"; B=60"; B/2=30"; B/4=15"; C=136 9/16"; C/2=68 9/32"; CLASS=2"; D=92 1/2"; D-L-K-J=1 3/8"; D-M=47 3/4"; E=113 3/16"; E/2=56 19/32"; E/52*15=32 21/32"; F=64 11/16"; F/2=32 11/32"; H=62 11/16"; H/2=31 11/32"; HEIGHT=102 7/16"; J=14"; J+K+L=91 1/8"; K=30 1/8"; L=47"; M=44 3/4"; M-(2*(D-L-K-J))=42"; N=23 1/4"; N+(H/2)=54 19/32"; NOZZLE_BOTTOM_ID=51 3/4"; NOZZLE_BOTTOM_RAD=25 7/8"; NOZZLE_BOTTOM_RAD-3*2=19 7/8"; NOZZLE_HEIGHT=95"; NOZZLE_HEIGHT/7*2=23 3/4"; NOZZLE_SIZE=36"; NOZZLE_TOP_OD=58"; NOZZLE_TOP_RAD=29"; NOZZLE_WB/4=18"; NOZZLE_WB_OD=90"; NOZZLE_WB_RAD=45"; NOZZLE_WB_RAD-2"=43"; P=25 3/4"; R=53"; R*1.1=58 5/16"; R+((B/2)+1.5")=84 1/2"; R-((B/2)+1.5")=21 1/2"; TRANSITION=36 19/32"; TRANSITION/2=18 9/32"; Type Comments=Vari-Plume Laboratory Exhaust Centrifugal Airfoil Class 2 Arr 10
- 600_CAVP-30L_CLASS_1: ((M - (2 * (D - L - K - J))) / 2) + (TRANSITION / 2)=38 5/16"; (B/2)+1.5"=34 1/2"; (B/2)-.125"=32 7/8"; (D-J-K-L)*2=2 3/4"; (F-((F-H)/2))/2=33 11/32"; (M - (2 * (D - L - K - J)))/2=23 9/32"; (NOZZLE_HEIGHT - (NOZZLE_HEIGHT / 8 * 2)) / 2=29 1/4"; (NOZZLE_WB_OD - NOZZLE_TOP_OD) / 4=7 1/8"; -(F-((F-H)/2))/2=-33 11/32"; A=239 7/16"; A/2=119 23/32"; B=66"; B/2=33"; B/4=16 1/2"; C=144 11/16"; C/2=72 11/32"; CLASS=1"; D=93 3/8"; D-L-K-J=1 3/8"; D-M=44 1/16"; E=125 9/16"; E/2=62 25/32"; E/52*15=36 7/32"; F=70 11/16"; F/2=35 11/32"; H=68 11/16"; H/2=34 11/32"; HEIGHT=113 27/32"; J=14 1/2"; J+K+L=92"; K=25 7/8"; L=51 5/8"; M=49 5/16"; M-(2*(D-L-K-J))=46 9/16"; N=26 7/16"; N+(H/2)=60 25/32"; NOZZLE_BOTTOM_ID=42 1/2"; NOZZLE_BOTTOM_RAD=21 1/4"; NOZZLE_BOTTOM_RAD-3*2=15 1/4"; NOZZLE_HEIGHT=78"; NOZZLE_HEIGHT/7*2=19 1/2"; NOZZLE_SIZE=30"; NOZZLE_TOP_OD=45 1/2"; NOZZLE_TOP_RAD=22 3/4"; NOZZLE_WB/4=14 13/16"; NOZZLE_WB_OD=74"; NOZZLE_WB_RAD=37"; NOZZLE_WB_RAD-2"=35"; P=19 1/2"; R=59"; R*1.1=64 29/32"; R+((B/2)+1.5")=93 1/2"; R-((B/2)+1.5")=24 1/2"; TRANSITION=30 1/16"; TRANSITION/2=15 1/32"; Type Comments=Vari-Plume Laboratory Exhaust Centrifugal Airfoil Class 1 Arr 10
- 600_CAVP-30H_CLASS_1: ((M - (2 * (D - L - K - J))) / 2) + (TRANSITION / 2)=38 5/16"; (B/2)+1.5"=34 1/2"; (B/2)-.125"=32 7/8"; (D-J-K-L)*2=2 3/4"; (F-((F-H)/2))/2=33 11/32"; (M - (2 * (D - L - K - J)))/2=23 9/32"; (NOZZLE_HEIGHT - (NOZZLE_HEIGHT / 8 * 2)) / 2=29 1/4"; (NOZZLE_WB_OD - NOZZLE_TOP_OD) / 4=7 1/8"; -(F-((F-H)/2))/2=-33 11/32"; A=239 7/16"; A/2=119 23/32"; B=66"; B/2=33"; B/4=16 1/2"; C=144 11/16"; C/2=72 11/32"; CLASS=1"; D=93 3/8"; D-L-K-J=1 3/8"; D-M=44 1/16"; E=125 9/16"; E/2=62 25/32"; E/52*15=36 7/32"; F=70 11/16"; F/2=35 11/32"; H=68 11/16"; H/2=34 11/32"; HEIGHT=113 27/32"; J=14 1/2"; J+K+L=92"; K=25 7/8"; L=51 5/8"; M=49 5/16"; M-(2*(D-L-K-J))=46 9/16"; N=26 7/16"; N+(H/2)=60 25/32"; NOZZLE_BOTTOM_ID=42 1/2"; NOZZLE_BOTTOM_RAD=21 1/4"; NOZZLE_BOTTOM_RAD-3*2=15 1/4"; NOZZLE_HEIGHT=78"; NOZZLE_HEIGHT/7*2=19 1/2"; NOZZLE_SIZE=30"; NOZZLE_TOP_OD=45 1/2"; NOZZLE_TOP_RAD=22 3/4"; NOZZLE_WB/4=14 13/16"; NOZZLE_WB_OD=74"; NOZZLE_WB_RAD=37"; NOZZLE_WB_RAD-2"=35"; P=19 1/2"; R=59"; R*1.1=64 29/32"; R+((B/2)+1.5")=93 1/2"; R-((B/2)+1.5")=24 1/2"; TRANSITION=30 1/16"; TRANSITION/2=15 1/32"; Type Comments=Vari-Plume Laboratory Exhaust Centrifugal Airfoil Class 1 Arr 10
- 600_CAVP-36L_CLASS_1: ((M - (2 * (D - L - K - J))) / 2) + (TRANSITION / 2)=41 9/16"; (B/2)+1.5"=34 1/2"; (B/2)-.125"=32 7/8"; (D-J-K-L)*2=2 3/4"; (F-((F-H)/2))/2=33 11/32"; (M - (2 * (D - L - K - J)))/2=23 9/32"; (NOZZLE_HEIGHT - (NOZZLE_HEIGHT / 8 * 2)) / 2=35 5/8"; (NOZZLE_WB_OD - NOZZLE_TOP_OD) / 4=8"; -(F-((F-H)/2))/2=-33 11/32"; A=239 7/16"; A/2=119 23/32"; B=66"; B/2=33"; B/4=16 1/2"; C=144 11/16"; C/2=72 11/32"; CLASS=1"; D=93 3/8"; D-L-K-J=1 3/8"; D-M=44 1/16"; E=125 9/16"; E/2=62 25/32"; E/52*15=36 7/32"; F=70 11/16"; F/2=35 11/32"; H=68 11/16"; H/2=34 11/32"; HEIGHT=113 27/32"; J=14 1/2"; J+K+L=92"; K=25 7/8"; L=51 5/8"; M=49 5/16"; M-(2*(D-L-K-J))=46 9/16"; N=26 7/16"; N+(H/2)=60 25/32"; NOZZLE_BOTTOM_ID=51 3/4"; NOZZLE_BOTTOM_RAD=25 7/8"; NOZZLE_BOTTOM_RAD-3*2=19 7/8"; NOZZLE_HEIGHT=95"; NOZZLE_HEIGHT/7*2=23 3/4"; NOZZLE_SIZE=36"; NOZZLE_TOP_OD=58"; NOZZLE_TOP_RAD=29"; NOZZLE_WB/4=18"; NOZZLE_WB_OD=90"; NOZZLE_WB_RAD=45"; NOZZLE_WB_RAD-2"=43"; P=19 1/2"; R=59"; R*1.1=64 29/32"; R+((B/2)+1.5")=93 1/2"; R-((B/2)+1.5")=24 1/2"; TRANSITION=36 19/32"; TRANSITION/2=18 9/32"; Type Comments=Vari-Plume Laboratory Exhaust Centrifugal Airfoil Class 1 Arr 10
- 600_CAVP-36H_CLASS_1: ((M - (2 * (D - L - K - J))) / 2) + (TRANSITION / 2)=41 9/16"; (B/2)+1.5"=34 1/2"; (B/2)-.125"=32 7/8"; (D-J-K-L)*2=2 3/4"; (F-((F-H)/2))/2=33 11/32"; (M - (2 * (D - L - K - J)))/2=23 9/32"; (NOZZLE_HEIGHT - (NOZZLE_HEIGHT / 8 * 2)) / 2=35 5/8"; (NOZZLE_WB_OD - NOZZLE_TOP_OD) / 4=8"; -(F-((F-H)/2))/2=-33 11/32"; A=239 7/16"; A/2=119 23/32"; B=66"; B/2=33"; B/4=16 1/2"; C=144 11/16"; C/2=72 11/32"; CLASS=1"; D=93 3/8"; D-L-K-J=1 3/8"; D-M=44 1/16"; E=125 9/16"; E/2=62 25/32"; E/52*15=36 7/32"; F=70 11/16"; F/2=35 11/32"; H=68 11/16"; H/2=34 11/32"; HEIGHT=113 27/32"; J=14 1/2"; J+K+L=92"; K=25 7/8"; L=51 5/8"; M=49 5/16"; M-(2*(D-L-K-J))=46 9/16"; N=26 7/16"; N+(H/2)=60 25/32"; NOZZLE_BOTTOM_ID=51 3/4"; NOZZLE_BOTTOM_RAD=25 7/8"; NOZZLE_BOTTOM_RAD-3*2=19 7/8"; NOZZLE_HEIGHT=95"; NOZZLE_HEIGHT/7*2=23 3/4"; NOZZLE_SIZE=36"; NOZZLE_TOP_OD=58"; NOZZLE_TOP_RAD=29"; NOZZLE_WB/4=18"; NOZZLE_WB_OD=90"; NOZZLE_WB_RAD=45"; NOZZLE_WB_RAD-2"=43"; P=19 1/2"; R=59"; R*1.1=64 29/32"; R+((B/2)+1.5")=93 1/2"; R-((B/2)+1.5")=24 1/2"; TRANSITION=36 19/32"; TRANSITION/2=18 9/32"; Type Comments=Vari-Plume Laboratory Exhaust Centrifugal Airfoil Class 1 Arr 10
- 600_CAVP-49L_CLASS_1: ((M - (2 * (D - L - K - J))) / 2) + (TRANSITION / 2)=47 13/16"; (B/2)+1.5"=34 1/2"; (B/2)-.125"=32 7/8"; (D-J-K-L)*2=2 3/4"; (F-((F-H)/2))/2=33 11/32"; (M - (2 * (D - L - K - J)))/2=23 9/32"; (NOZZLE_HEIGHT - (NOZZLE_HEIGHT / 8 * 2)) / 2=41 1/4"; (NOZZLE_WB_OD - NOZZLE_TOP_OD) / 4=6 1/4"; -(F-((F-H)/2))/2=-33 11/32"; A=239 7/16"; A/2=119 23/32"; B=66"; B/2=33"; B/4=16 1/2"; C=144 11/16"; C/2=72 11/32"; CLASS=1"; D=93 3/8"; D-L-K-J=1 3/8"; D-M=44 1/16"; E=125 9/16"; E/2=62 25/32"; E/52*15=36 7/32"; F=70 11/16"; F/2=35 11/32"; H=68 11/16"; H/2=34 11/32"; HEIGHT=113 27/32"; J=14 1/2"; J+K+L=92"; K=25 7/8"; L=51 5/8"; M=49 5/16"; M-(2*(D-L-K-J))=46 9/16"; N=26 7/16"; N+(H/2)=60 25/32"; NOZZLE_BOTTOM_ID=69 3/8"; NOZZLE_BOTTOM_RAD=34 11/16"; NOZZLE_BOTTOM_RAD-3*2=28 11/16"; NOZZLE_HEIGHT=110"; NOZZLE_HEIGHT/7*2=27 1/2"; NOZZLE_SIZE=49"; NOZZLE_TOP_OD=76"; NOZZLE_TOP_RAD=38"; NOZZLE_WB/4=20 3/16"; NOZZLE_WB_OD=101"; NOZZLE_WB_RAD=50 1/2"; NOZZLE_WB_RAD-2"=48 1/2"; P=19 1/2"; R=59"; R*1.1=64 29/32"; R+((B/2)+1.5")=93 1/2"; R-((B/2)+1.5")=24 1/2"; TRANSITION=49 1/16"; TRANSITION/2=24 17/32"; Type Comments=Vari-Plume Laboratory Exhaust Centrifugal Airfoil Class 1 Arr 10
- 600_CAVP-49H_CLASS_1: ((M - (2 * (D - L - K - J))) / 2) + (TRANSITION / 2)=47 13/16"; (B/2)+1.5"=34 1/2"; (B/2)-.125"=32 7/8"; (D-J-K-L)*2=2 3/4"; (F-((F-H)/2))/2=33 11/32"; (M - (2 * (D - L - K - J)))/2=23 9/32"; (NOZZLE_HEIGHT - (NOZZLE_HEIGHT / 8 * 2)) / 2=41 1/4"; (NOZZLE_WB_OD - NOZZLE_TOP_OD) / 4=6 1/4"; -(F-((F-H)/2))/2=-33 11/32"; A=239 7/16"; A/2=119 23/32"; B=66"; B/2=33"; B/4=16 1/2"; C=144 11/16"; C/2=72 11/32"; CLASS=1"; D=93 3/8"; D-L-K-J=1 3/8"; D-M=44 1/16"; E=125 9/16"; E/2=62 25/32"; E/52*15=36 7/32"; F=70 11/16"; F/2=35 11/32"; H=68 11/16"; H/2=34 11/32"; HEIGHT=113 27/32"; J=14 1/2"; J+K+L=92"; K=25 7/8"; L=51 5/8"; M=49 5/16"; M-(2*(D-L-K-J))=46 9/16"; N=26 7/16"; N+(H/2)=60 25/32"; NOZZLE_BOTTOM_ID=69 3/8"; NOZZLE_BOTTOM_RAD=34 11/16"; NOZZLE_BOTTOM_RAD-3*2=28 11/16"; NOZZLE_HEIGHT=110"; NOZZLE_HEIGHT/7*2=27 1/2"; NOZZLE_SIZE=49"; NOZZLE_TOP_OD=76"; NOZZLE_TOP_RAD=38"; NOZZLE_WB/4=20 3/16"; NOZZLE_WB_OD=101"; NOZZLE_WB_RAD=50 1/2"; NOZZLE_WB_RAD-2"=48 1/2"; P=19 1/2"; R=59"; R*1.1=64 29/32"; R+((B/2)+1.5")=93 1/2"; R-((B/2)+1.5")=24 1/2"; TRANSITION=49 1/16"; TRANSITION/2=24 17/32"; Type Comments=Vari-Plume Laboratory Exhaust Centrifugal Airfoil Class 1 Arr 10
- 600_CAVP-30L_CLASS_2: ((M - (2 * (D - L - K - J))) / 2) + (TRANSITION / 2)=38 5/16"; (B/2)+1.5"=34 1/2"; (B/2)-.125"=32 7/8"; (D-J-K-L)*2=2 3/4"; (F-((F-H)/2))/2=33 11/32"; (M - (2 * (D - L - K - J)))/2=23 9/32"; (NOZZLE_HEIGHT - (NOZZLE_HEIGHT / 8 * 2)) / 2=29 1/4"; (NOZZLE_WB_OD - NOZZLE_TOP_OD) / 4=7 1/8"; -(F-((F-H)/2))/2=-33 11/32"; A=239 7/16"; A/2=119 23/32"; B=66"; B/2=33"; B/4=16 1/2"; C=144 11/16"; C/2=72 11/32"; CLASS=2"; D=97 9/16"; D-L-K-J=1 3/8"; D-M=48 1/4"; E=125 9/16"; E/2=62 25/32"; E/52*15=36 7/32"; F=70 11/16"; F/2=35 11/32"; H=68 11/16"; H/2=34 11/32"; HEIGHT=113 27/32"; J=14 1/2"; J+K+L=96 3/16"; K=30 1/8"; L=51 9/16"; M=49 5/16"; M-(2*(D-L-K-J))=46 9/16"; N=26 7/16"; N+(H/2)=60 25/32"; NOZZLE_BOTTOM_ID=42 1/2"; NOZZLE_BOTTOM_RAD=21 1/4"; NOZZLE_BOTTOM_RAD-3*2=15 1/4"; NOZZLE_HEIGHT=78"; NOZZLE_HEIGHT/7*2=19 1/2"; NOZZLE_SIZE=30"; NOZZLE_TOP_OD=45 1/2"; NOZZLE_TOP_RAD=22 3/4"; NOZZLE_WB/4=14 13/16"; NOZZLE_WB_OD=74"; NOZZLE_WB_RAD=37"; NOZZLE_WB_RAD-2"=35"; P=26"; R=59"; R*1.1=64 29/32"; R+((B/2)+1.5")=93 1/2"; R-((B/2)+1.5")=24 1/2"; TRANSITION=30 1/16"; TRANSITION/2=15 1/32"; Type Comments=Vari-Plume Laboratory Exhaust Centrifugal Airfoil Class 2 Arr 10
- 600_CAVP-30H_CLASS_2: ((M - (2 * (D - L - K - J))) / 2) + (TRANSITION / 2)=38 5/16"; (B/2)+1.5"=34 1/2"; (B/2)-.125"=32 7/8"; (D-J-K-L)*2=2 3/4"; (F-((F-H)/2))/2=33 11/32"; (M - (2 * (D - L - K - J)))/2=23 9/32"; (NOZZLE_HEIGHT - (NOZZLE_HEIGHT / 8 * 2)) / 2=29 1/4"; (NOZZLE_WB_OD - NOZZLE_TOP_OD) / 4=7 1/8"; -(F-((F-H)/2))/2=-33 11/32"; A=239 7/16"; A/2=119 23/32"; B=66"; B/2=33"; B/4=16 1/2"; C=144 11/16"; C/2=72 11/32"; CLASS=2"; D=97 9/16"; D-L-K-J=1 3/8"; D-M=48 1/4"; E=125 9/16"; E/2=62 25/32"; E/52*15=36 7/32"; F=70 11/16"; F/2=35 11/32"; H=68 11/16"; H/2=34 11/32"; HEIGHT=113 27/32"; J=14 1/2"; J+K+L=96 3/16"; K=30 1/8"; L=51 9/16"; M=49 5/16"; M-(2*(D-L-K-J))=46 9/16"; N=26 7/16"; N+(H/2)=60 25/32"; NOZZLE_BOTTOM_ID=42 1/2"; NOZZLE_BOTTOM_RAD=21 1/4"; NOZZLE_BOTTOM_RAD-3*2=15 1/4"; NOZZLE_HEIGHT=78"; NOZZLE_HEIGHT/7*2=19 1/2"; NOZZLE_SIZE=30"; NOZZLE_TOP_OD=45 1/2"; NOZZLE_TOP_RAD=22 3/4"; NOZZLE_WB/4=14 13/16"; NOZZLE_WB_OD=74"; NOZZLE_WB_RAD=37"; NOZZLE_WB_RAD-2"=35"; P=26"; R=59"; R*1.1=64 29/32"; R+((B/2)+1.5")=93 1/2"; R-((B/2)+1.5")=24 1/2"; TRANSITION=30 1/16"; TRANSITION/2=15 1/32"; Type Comments=Vari-Plume Laboratory Exhaust Centrifugal Airfoil Class 2 Arr 10
- 600_CAVP-36L_CLASS_2: ((M - (2 * (D - L - K - J))) / 2) + (TRANSITION / 2)=41 9/16"; (B/2)+1.5"=34 1/2"; (B/2)-.125"=32 7/8"; (D-J-K-L)*2=2 3/4"; (F-((F-H)/2))/2=33 11/32"; (M - (2 * (D - L - K - J)))/2=23 9/32"; (NOZZLE_HEIGHT - (NOZZLE_HEIGHT / 8 * 2)) / 2=35 5/8"; (NOZZLE_WB_OD - NOZZLE_TOP_OD) / 4=8"; -(F-((F-H)/2))/2=-33 11/32"; A=239 7/16"; A/2=119 23/32"; B=66"; B/2=33"; B/4=16 1/2"; C=144 11/16"; C/2=72 11/32"; CLASS=2"; D=97 9/16"; D-L-K-J=1 3/8"; D-M=48 1/4"; E=125 9/16"; E/2=62 25/32"; E/52*15=36 7/32"; F=70 11/16"; F/2=35 11/32"; H=68 11/16"; H/2=34 11/32"; HEIGHT=113 27/32"; J=14 1/2"; J+K+L=96 3/16"; K=30 1/8"; L=51 9/16"; M=49 5/16"; M-(2*(D-L-K-J))=46 9/16"; N=26 7/16"; N+(H/2)=60 25/32"; NOZZLE_BOTTOM_ID=51 3/4"; NOZZLE_BOTTOM_RAD=25 7/8"; NOZZLE_BOTTOM_RAD-3*2=19 7/8"; NOZZLE_HEIGHT=95"; NOZZLE_HEIGHT/7*2=23 3/4"; NOZZLE_SIZE=36"; NOZZLE_TOP_OD=58"; NOZZLE_TOP_RAD=29"; NOZZLE_WB/4=18"; NOZZLE_WB_OD=90"; NOZZLE_WB_RAD=45"; NOZZLE_WB_RAD-2"=43"; P=26"; R=59"; R*1.1=64 29/32"; R+((B/2)+1.5")=93 1/2"; R-((B/2)+1.5")=24 1/2"; TRANSITION=36 19/32"; TRANSITION/2=18 9/32"; Type Comments=Vari-Plume Laboratory Exhaust Centrifugal Airfoil Class 2 Arr 10
- 600_CAVP-36H_CLASS_2: ((M - (2 * (D - L - K - J))) / 2) + (TRANSITION / 2)=41 9/16"; (B/2)+1.5"=34 1/2"; (B/2)-.125"=32 7/8"; (D-J-K-L)*2=2 3/4"; (F-((F-H)/2))/2=33 11/32"; (M - (2 * (D - L - K - J)))/2=23 9/32"; (NOZZLE_HEIGHT - (NOZZLE_HEIGHT / 8 * 2)) / 2=35 5/8"; (NOZZLE_WB_OD - NOZZLE_TOP_OD) / 4=8"; -(F-((F-H)/2))/2=-33 11/32"; A=239 7/16"; A/2=119 23/32"; B=66"; B/2=33"; B/4=16 1/2"; C=144 11/16"; C/2=72 11/32"; CLASS=2"; D=97 9/16"; D-L-K-J=1 3/8"; D-M=48 1/4"; E=125 9/16"; E/2=62 25/32"; E/52*15=36 7/32"; F=70 11/16"; F/2=35 11/32"; H=68 11/16"; H/2=34 11/32"; HEIGHT=113 27/32"; J=14 1/2"; J+K+L=96 3/16"; K=30 1/8"; L=51 9/16"; M=49 5/16"; M-(2*(D-L-K-J))=46 9/16"; N=26 7/16"; N+(H/2)=60 25/32"; NOZZLE_BOTTOM_ID=51 3/4"; NOZZLE_BOTTOM_RAD=25 7/8"; NOZZLE_BOTTOM_RAD-3*2=19 7/8"; NOZZLE_HEIGHT=95"; NOZZLE_HEIGHT/7*2=23 3/4"; NOZZLE_SIZE=36"; NOZZLE_TOP_OD=58"; NOZZLE_TOP_RAD=29"; NOZZLE_WB/4=18"; NOZZLE_WB_OD=90"; NOZZLE_WB_RAD=45"; NOZZLE_WB_RAD-2"=43"; P=26"; R=59"; R*1.1=64 29/32"; R+((B/2)+1.5")=93 1/2"; R-((B/2)+1.5")=24 1/2"; TRANSITION=36 19/32"; TRANSITION/2=18 9/32"; Type Comments=Vari-Plume Laboratory Exhaust Centrifugal Airfoil Class 2 Arr 10
- 600_CAVP-49L_CLASS_2: ((M - (2 * (D - L - K - J))) / 2) + (TRANSITION / 2)=47 13/16"; (B/2)+1.5"=34 1/2"; (B/2)-.125"=32 7/8"; (D-J-K-L)*2=2 3/4"; (F-((F-H)/2))/2=33 11/32"; (M - (2 * (D - L - K - J)))/2=23 9/32"; (NOZZLE_HEIGHT - (NOZZLE_HEIGHT / 8 * 2)) / 2=41 1/4"; (NOZZLE_WB_OD - NOZZLE_TOP_OD) / 4=6 1/4"; -(F-((F-H)/2))/2=-33 11/32"; A=239 7/16"; A/2=119 23/32"; B=66"; B/2=33"; B/4=16 1/2"; C=144 11/16"; C/2=72 11/32"; CLASS=2"; D=97 9/16"; D-L-K-J=1 3/8"; D-M=48 1/4"; E=125 9/16"; E/2=62 25/32"; E/52*15=36 7/32"; F=70 11/16"; F/2=35 11/32"; H=68 11/16"; H/2=34 11/32"; HEIGHT=113 27/32"; J=14 1/2"; J+K+L=96 3/16"; K=30 1/8"; L=51 9/16"; M=49 5/16"; M-(2*(D-L-K-J))=46 9/16"; N=26 7/16"; N+(H/2)=60 25/32"; NOZZLE_BOTTOM_ID=69 3/8"; NOZZLE_BOTTOM_RAD=34 11/16"; NOZZLE_BOTTOM_RAD-3*2=28 11/16"; NOZZLE_HEIGHT=110"; NOZZLE_HEIGHT/7*2=27 1/2"; NOZZLE_SIZE=49"; NOZZLE_TOP_OD=76"; NOZZLE_TOP_RAD=38"; NOZZLE_WB/4=20 3/16"; NOZZLE_WB_OD=101"; NOZZLE_WB_RAD=50 1/2"; NOZZLE_WB_RAD-2"=48 1/2"; P=26"; R=59"; R*1.1=64 29/32"; R+((B/2)+1.5")=93 1/2"; R-((B/2)+1.5")=24 1/2"; TRANSITION=49 1/16"; TRANSITION/2=24 17/32"; Type Comments=Vari-Plume Laboratory Exhaust Centrifugal Airfoil Class 2 Arr 10
- 600_CAVP-49H_CLASS_2: ((M - (2 * (D - L - K - J))) / 2) + (TRANSITION / 2)=47 13/16"; (B/2)+1.5"=34 1/2"; (B/2)-.125"=32 7/8"; (D-J-K-L)*2=2 3/4"; (F-((F-H)/2))/2=33 11/32"; (M - (2 * (D - L - K - J)))/2=23 9/32"; (NOZZLE_HEIGHT - (NOZZLE_HEIGHT / 8 * 2)) / 2=41 1/4"; (NOZZLE_WB_OD - NOZZLE_TOP_OD) / 4=6 1/4"; -(F-((F-H)/2))/2=-33 11/32"; A=239 7/16"; A/2=119 23/32"; B=66"; B/2=33"; B/4=16 1/2"; C=144 11/16"; C/2=72 11/32"; CLASS=2"; D=97 9/16"; D-L-K-J=1 3/8"; D-M=48 1/4"; E=125 9/16"; E/2=62 25/32"; E/52*15=36 7/32"; F=70 11/16"; F/2=35 11/32"; H=68 11/16"; H/2=34 11/32"; HEIGHT=113 27/32"; J=14 1/2"; J+K+L=96 3/16"; K=30 1/8"; L=51 9/16"; M=49 5/16"; M-(2*(D-L-K-J))=46 9/16"; N=26 7/16"; N+(H/2)=60 25/32"; NOZZLE_BOTTOM_ID=69 3/8"; NOZZLE_BOTTOM_RAD=34 11/16"; NOZZLE_BOTTOM_RAD-3*2=28 11/16"; NOZZLE_HEIGHT=110"; NOZZLE_HEIGHT/7*2=27 1/2"; NOZZLE_SIZE=49"; NOZZLE_TOP_OD=76"; NOZZLE_TOP_RAD=38"; NOZZLE_WB/4=20 3/16"; NOZZLE_WB_OD=101"; NOZZLE_WB_RAD=50 1/2"; NOZZLE_WB_RAD-2"=48 1/2"; P=26"; R=59"; R*1.1=64 29/32"; R+((B/2)+1.5")=93 1/2"; R-((B/2)+1.5")=24 1/2"; TRANSITION=49 1/16"; TRANSITION/2=24 17/32"; Type Comments=Vari-Plume Laboratory Exhaust Centrifugal Airfoil Class 2 Arr 10
- 660_CAVP-36H_CLASS_1: ((M - (2 * (D - L - K - J))) / 2) + (TRANSITION / 2)=43 7/8"; (B/2)+1.5"=37 1/2"; (B/2)-.125"=35 7/8"; (D-J-K-L)*2=2 3/4"; (F-((F-H)/2))/2=36 11/32"; (M - (2 * (D - L - K - J)))/2=25 19/32"; (NOZZLE_HEIGHT - (NOZZLE_HEIGHT / 8 * 2)) / 2=35 5/8"; (NOZZLE_WB_OD - NOZZLE_TOP_OD) / 4=8"; -(F-((F-H)/2))/2=-36 11/32"; A=270 1/4"; A/2=135 1/8"; B=72"; B/2=36"; B/4=18"; C=160 1/4"; C/2=80 1/8"; CLASS=1"; D=102 1/2"; D-L-K-J=1 3/8"; D-M=48 9/16"; E=137 15/16"; E/2=68 31/32"; E/52*15=39 25/32"; F=76 11/16"; F/2=38 11/32"; H=74 11/16"; H/2=37 11/32"; HEIGHT=125 1/4"; J=15"; J+K+L=101 1/8"; K=29 7/8"; L=56 1/4"; M=53 15/16"; M-(2*(D-L-K-J))=51 3/16"; N=29 5/8"; N+(H/2)=66 31/32"; NOZZLE_BOTTOM_ID=51 3/4"; NOZZLE_BOTTOM_RAD=25 7/8"; NOZZLE_BOTTOM_RAD-3*2=19 7/8"; NOZZLE_HEIGHT=95"; NOZZLE_HEIGHT/7*2=23 3/4"; NOZZLE_SIZE=36"; NOZZLE_TOP_OD=58"; NOZZLE_TOP_RAD=29"; NOZZLE_WB/4=18"; NOZZLE_WB_OD=90"; NOZZLE_WB_RAD=45"; NOZZLE_WB_RAD-2"=43"; P=19 1/2"; R=65"; R*1.1=71 1/2"; R+((B/2)+1.5")=102 1/2"; R-((B/2)+1.5")=27 1/2"; TRANSITION=36 19/32"; TRANSITION/2=18 9/32"; Type Comments=Vari-Plume Laboratory Exhaust Centrifugal Airfoil Class 1 Arr 10
- 660_CAVP-36L_CLASS_1: ((M - (2 * (D - L - K - J))) / 2) + (TRANSITION / 2)=43 7/8"; (B/2)+1.5"=37 1/2"; (B/2)-.125"=35 7/8"; (D-J-K-L)*2=2 3/4"; (F-((F-H)/2))/2=36 11/32"; (M - (2 * (D - L - K - J)))/2=25 19/32"; (NOZZLE_HEIGHT - (NOZZLE_HEIGHT / 8 * 2)) / 2=35 5/8"; (NOZZLE_WB_OD - NOZZLE_TOP_OD) / 4=8"; -(F-((F-H)/2))/2=-36 11/32"; A=270 1/4"; A/2=135 1/8"; B=72"; B/2=36"; B/4=18"; C=160 1/4"; C/2=80 1/8"; CLASS=1"; D=102 1/2"; D-L-K-J=1 3/8"; D-M=48 9/16"; E=137 15/16"; E/2=68 31/32"; E/52*15=39 25/32"; F=76 11/16"; F/2=38 11/32"; H=74 11/16"; H/2=37 11/32"; HEIGHT=125 1/4"; J=15"; J+K+L=101 1/8"; K=29 7/8"; L=56 1/4"; M=53 15/16"; M-(2*(D-L-K-J))=51 3/16"; N=29 5/8"; N+(H/2)=66 31/32"; NOZZLE_BOTTOM_ID=51 3/4"; NOZZLE_BOTTOM_RAD=25 7/8"; NOZZLE_BOTTOM_RAD-3*2=19 7/8"; NOZZLE_HEIGHT=95"; NOZZLE_HEIGHT/7*2=23 3/4"; NOZZLE_SIZE=36"; NOZZLE_TOP_OD=58"; NOZZLE_TOP_RAD=29"; NOZZLE_WB/4=18"; NOZZLE_WB_OD=90"; NOZZLE_WB_RAD=45"; NOZZLE_WB_RAD-2"=43"; P=19 1/2"; R=65"; R*1.1=71 1/2"; R+((B/2)+1.5")=102 1/2"; R-((B/2)+1.5")=27 1/2"; TRANSITION=36 19/32"; TRANSITION/2=18 9/32"; Type Comments=Vari-Plume Laboratory Exhaust Centrifugal Airfoil Class 1 Arr 10
- 660_CAVP-49H_CLASS_1: ((M - (2 * (D - L - K - J))) / 2) + (TRANSITION / 2)=50 1/8"; (B/2)+1.5"=37 1/2"; (B/2)-.125"=35 7/8"; (D-J-K-L)*2=2 3/4"; (F-((F-H)/2))/2=36 11/32"; (M - (2 * (D - L - K - J)))/2=25 19/32"; (NOZZLE_HEIGHT - (NOZZLE_HEIGHT / 8 * 2)) / 2=41 1/4"; (NOZZLE_WB_OD - NOZZLE_TOP_OD) / 4=6 1/4"; -(F-((F-H)/2))/2=-36 11/32"; A=270 1/4"; A/2=135 1/8"; B=72"; B/2=36"; B/4=18"; C=160 1/4"; C/2=80 1/8"; CLASS=1"; D=102 1/2"; D-L-K-J=1 3/8"; D-M=48 9/16"; E=137 15/16"; E/2=68 31/32"; E/52*15=39 25/32"; F=76 11/16"; F/2=38 11/32"; H=74 11/16"; H/2=37 11/32"; HEIGHT=125 1/4"; J=15"; J+K+L=101 1/8"; K=29 7/8"; L=56 1/4"; M=53 15/16"; M-(2*(D-L-K-J))=51 3/16"; N=29 5/8"; N+(H/2)=66 31/32"; NOZZLE_BOTTOM_ID=69 3/8"; NOZZLE_BOTTOM_RAD=34 11/16"; NOZZLE_BOTTOM_RAD-3*2=28 11/16"; NOZZLE_HEIGHT=110"; NOZZLE_HEIGHT/7*2=27 1/2"; NOZZLE_SIZE=49"; NOZZLE_TOP_OD=76"; NOZZLE_TOP_RAD=38"; NOZZLE_WB/4=20 3/16"; NOZZLE_WB_OD=101"; NOZZLE_WB_RAD=50 1/2"; NOZZLE_WB_RAD-2"=48 1/2"; P=19 1/2"; R=65"; R*1.1=71 1/2"; R+((B/2)+1.5")=102 1/2"; R-((B/2)+1.5")=27 1/2"; TRANSITION=49 1/16"; TRANSITION/2=24 17/32"; Type Comments=Vari-Plume Laboratory Exhaust Centrifugal Airfoil Class 1 Arr 10
- 660_CAVP-49L_CLASS_1: ((M - (2 * (D - L - K - J))) / 2) + (TRANSITION / 2)=50 1/8"; (B/2)+1.5"=37 1/2"; (B/2)-.125"=35 7/8"; (D-J-K-L)*2=2 3/4"; (F-((F-H)/2))/2=36 11/32"; (M - (2 * (D - L - K - J)))/2=25 19/32"; (NOZZLE_HEIGHT - (NOZZLE_HEIGHT / 8 * 2)) / 2=41 1/4"; (NOZZLE_WB_OD - NOZZLE_TOP_OD) / 4=6 1/4"; -(F-((F-H)/2))/2=-36 11/32"; A=270 1/4"; A/2=135 1/8"; B=72"; B/2=36"; B/4=18"; C=160 1/4"; C/2=80 1/8"; CLASS=1"; D=102 1/2"; D-L-K-J=1 3/8"; D-M=48 9/16"; E=137 15/16"; E/2=68 31/32"; E/52*15=39 25/32"; F=76 11/16"; F/2=38 11/32"; H=74 11/16"; H/2=37 11/32"; HEIGHT=125 1/4"; J=15"; J+K+L=101 1/8"; K=29 7/8"; L=56 1/4"; M=53 15/16"; M-(2*(D-L-K-J))=51 3/16"; N=29 5/8"; N+(H/2)=66 31/32"; NOZZLE_BOTTOM_ID=69 3/8"; NOZZLE_BOTTOM_RAD=34 11/16"; NOZZLE_BOTTOM_RAD-3*2=28 11/16"; NOZZLE_HEIGHT=110"; NOZZLE_HEIGHT/7*2=27 1/2"; NOZZLE_SIZE=49"; NOZZLE_TOP_OD=76"; NOZZLE_TOP_RAD=38"; NOZZLE_WB/4=20 3/16"; NOZZLE_WB_OD=101"; NOZZLE_WB_RAD=50 1/2"; NOZZLE_WB_RAD-2"=48 1/2"; P=19 1/2"; R=65"; R*1.1=71 1/2"; R+((B/2)+1.5")=102 1/2"; R-((B/2)+1.5")=27 1/2"; TRANSITION=49 1/16"; TRANSITION/2=24 17/32"; Type Comments=Vari-Plume Laboratory Exhaust Centrifugal Airfoil Class 1 Arr 10
- 660_CAVP-36H_CLASS_2: ((M - (2 * (D - L - K - J))) / 2) + (TRANSITION / 2)=43 7/8"; (B/2)+1.5"=37 1/2"; (B/2)-.125"=35 7/8"; (D-J-K-L)*2=2 3/4"; (F-((F-H)/2))/2=36 11/32"; (M - (2 * (D - L - K - J)))/2=25 19/32"; (NOZZLE_HEIGHT - (NOZZLE_HEIGHT / 8 * 2)) / 2=35 5/8"; (NOZZLE_WB_OD - NOZZLE_TOP_OD) / 4=8"; -(F-((F-H)/2))/2=-36 11/32"; A=270 1/4"; A/2=135 1/8"; B=72"; B/2=36"; B/4=18"; C=160 1/4"; C/2=80 1/8"; CLASS=2"; D=111 1/4"; D-L-K-J=1 3/8"; D-M=57 5/16"; E=137 15/16"; E/2=68 31/32"; E/52*15=39 25/32"; F=76 11/16"; F/2=38 11/32"; H=74 11/16"; H/2=37 11/32"; HEIGHT=125 1/4"; J=15"; J+K+L=109 7/8"; K=38 5/8"; L=56 1/4"; M=53 15/16"; M-(2*(D-L-K-J))=51 3/16"; N=29 5/8"; N+(H/2)=66 31/32"; NOZZLE_BOTTOM_ID=51 3/4"; NOZZLE_BOTTOM_RAD=25 7/8"; NOZZLE_BOTTOM_RAD-3*2=19 7/8"; NOZZLE_HEIGHT=95"; NOZZLE_HEIGHT/7*2=23 3/4"; NOZZLE_SIZE=36"; NOZZLE_TOP_OD=58"; NOZZLE_TOP_RAD=29"; NOZZLE_WB/4=18"; NOZZLE_WB_OD=90"; NOZZLE_WB_RAD=45"; NOZZLE_WB_RAD-2"=43"; P=29 1/2"; R=65"; R*1.1=71 1/2"; R+((B/2)+1.5")=102 1/2"; R-((B/2)+1.5")=27 1/2"; TRANSITION=36 19/32"; TRANSITION/2=18 9/32"; Type Comments=Vari-Plume Laboratory Exhaust Centrifugal Airfoil Class 2 Arr 10
- 660_CAVP-36L_CLASS_2: ((M - (2 * (D - L - K - J))) / 2) + (TRANSITION / 2)=43 7/8"; (B/2)+1.5"=37 1/2"; (B/2)-.125"=35 7/8"; (D-J-K-L)*2=2 3/4"; (F-((F-H)/2))/2=36 11/32"; (M - (2 * (D - L - K - J)))/2=25 19/32"; (NOZZLE_HEIGHT - (NOZZLE_HEIGHT / 8 * 2)) / 2=35 5/8"; (NOZZLE_WB_OD - NOZZLE_TOP_OD) / 4=8"; -(F-((F-H)/2))/2=-36 11/32"; A=270 1/4"; A/2=135 1/8"; B=72"; B/2=36"; B/4=18"; C=160 1/4"; C/2=80 1/8"; CLASS=2"; D=111 1/4"; D-L-K-J=1 3/8"; D-M=57 5/16"; E=137 15/16"; E/2=68 31/32"; E/52*15=39 25/32"; F=76 11/16"; F/2=38 11/32"; H=74 11/16"; H/2=37 11/32"; HEIGHT=125 1/4"; J=15"; J+K+L=109 7/8"; K=38 5/8"; L=56 1/4"; M=53 15/16"; M-(2*(D-L-K-J))=51 3/16"; N=29 5/8"; N+(H/2)=66 31/32"; NOZZLE_BOTTOM_ID=51 3/4"; NOZZLE_BOTTOM_RAD=25 7/8"; NOZZLE_BOTTOM_RAD-3*2=19 7/8"; NOZZLE_HEIGHT=95"; NOZZLE_HEIGHT/7*2=23 3/4"; NOZZLE_SIZE=36"; NOZZLE_TOP_OD=58"; NOZZLE_TOP_RAD=29"; NOZZLE_WB/4=18"; NOZZLE_WB_OD=90"; NOZZLE_WB_RAD=45"; NOZZLE_WB_RAD-2"=43"; P=29 1/2"; R=65"; R*1.1=71 1/2"; R+((B/2)+1.5")=102 1/2"; R-((B/2)+1.5")=27 1/2"; TRANSITION=36 19/32"; TRANSITION/2=18 9/32"; Type Comments=Vari-Plume Laboratory Exhaust Centrifugal Airfoil Class 2 Arr 10
- 660_CAVP-49L_CLASS_2: ((M - (2 * (D - L - K - J))) / 2) + (TRANSITION / 2)=50 1/8"; (B/2)+1.5"=37 1/2"; (B/2)-.125"=35 7/8"; (D-J-K-L)*2=2 3/4"; (F-((F-H)/2))/2=36 11/32"; (M - (2 * (D - L - K - J)))/2=25 19/32"; (NOZZLE_HEIGHT - (NOZZLE_HEIGHT / 8 * 2)) / 2=41 1/4"; (NOZZLE_WB_OD - NOZZLE_TOP_OD) / 4=6 1/4"; -(F-((F-H)/2))/2=-36 11/32"; A=270 1/4"; A/2=135 1/8"; B=72"; B/2=36"; B/4=18"; C=160 1/4"; C/2=80 1/8"; CLASS=2"; D=111 1/4"; D-L-K-J=1 3/8"; D-M=57 5/16"; E=137 15/16"; E/2=68 31/32"; E/52*15=39 25/32"; F=76 11/16"; F/2=38 11/32"; H=74 11/16"; H/2=37 11/32"; HEIGHT=125 1/4"; J=15"; J+K+L=109 7/8"; K=38 5/8"; L=56 1/4"; M=53 15/16"; M-(2*(D-L-K-J))=51 3/16"; N=29 5/8"; N+(H/2)=66 31/32"; NOZZLE_BOTTOM_ID=69 3/8"; NOZZLE_BOTTOM_RAD=34 11/16"; NOZZLE_BOTTOM_RAD-3*2=28 11/16"; NOZZLE_HEIGHT=110"; NOZZLE_HEIGHT/7*2=27 1/2"; NOZZLE_SIZE=49"; NOZZLE_TOP_OD=76"; NOZZLE_TOP_RAD=38"; NOZZLE_WB/4=20 3/16"; NOZZLE_WB_OD=101"; NOZZLE_WB_RAD=50 1/2"; NOZZLE_WB_RAD-2"=48 1/2"; P=29 1/2"; R=65"; R*1.1=71 1/2"; R+((B/2)+1.5")=102 1/2"; R-((B/2)+1.5")=27 1/2"; TRANSITION=49 1/16"; TRANSITION/2=24 17/32"; Type Comments=Vari-Plume Laboratory Exhaust Centrifugal Airfoil Class 2 Arr 10
- 730_CAVP-36H_CLASS_1: ((M - (2 * (D - L - K - J))) / 2) + (TRANSITION / 2)=46 17/32"; (B/2)+1.5"=41"; (B/2)-.125"=39 3/8"; (D-J-K-L)*2=2 3/4"; (F-((F-H)/2))/2=39 27/32"; (M - (2 * (D - L - K - J)))/2=28 1/4"; (NOZZLE_HEIGHT - (NOZZLE_HEIGHT / 8 * 2)) / 2=35 5/8"; (NOZZLE_WB_OD - NOZZLE_TOP_OD) / 4=8"; -(F-((F-H)/2))/2=-39 27/32"; A=286 3/8"; A/2=143 3/16"; B=79"; B/2=39 1/2"; B/4=19 3/4"; C=176 3/8"; C/2=88 3/16"; CLASS=1"; D=108 5/16"; D-L-K-J=1 3/8"; D-M=49 1/16"; E=152 3/8"; E/2=76 3/16"; E/52*15=43 31/32"; F=83 11/16"; F/2=41 27/32"; H=81 11/16"; H/2=40 27/32"; HEIGHT=138 17/32"; J=15 1/2"; J+K+L=106 15/16"; K=29 7/8"; L=61 9/16"; M=59 1/4"; M-(2*(D-L-K-J))=56 1/2"; N=33 11/32"; N+(H/2)=74 3/16"; NOZZLE_BOTTOM_ID=51 3/4"; NOZZLE_BOTTOM_RAD=25 7/8"; NOZZLE_BOTTOM_RAD-3*2=19 7/8"; NOZZLE_HEIGHT=95"; NOZZLE_HEIGHT/7*2=23 3/4"; NOZZLE_SIZE=36"; NOZZLE_TOP_OD=58"; NOZZLE_TOP_RAD=29"; NOZZLE_WB/4=18"; NOZZLE_WB_OD=90"; NOZZLE_WB_RAD=45"; NOZZLE_WB_RAD-2"=43"; P=22 1/8"; R=72"; R*1.1=79 3/16"; R+((B/2)+1.5")=113"; R-((B/2)+1.5")=31"; TRANSITION=36 19/32"; TRANSITION/2=18 9/32"; Type Comments=Vari-Plume Laboratory Exhaust Centrifugal Airfoil Class 1 Arr 10
- 730_CAVP-36L_CLASS_1: ((M - (2 * (D - L - K - J))) / 2) + (TRANSITION / 2)=46 17/32"; (B/2)+1.5"=41"; (B/2)-.125"=39 3/8"; (D-J-K-L)*2=2 3/4"; (F-((F-H)/2))/2=39 27/32"; (M - (2 * (D - L - K - J)))/2=28 1/4"; (NOZZLE_HEIGHT - (NOZZLE_HEIGHT / 8 * 2)) / 2=35 5/8"; (NOZZLE_WB_OD - NOZZLE_TOP_OD) / 4=8"; -(F-((F-H)/2))/2=-39 27/32"; A=286 3/8"; A/2=143 3/16"; B=79"; B/2=39 1/2"; B/4=19 3/4"; C=176 3/8"; C/2=88 3/16"; CLASS=1"; D=108 5/16"; D-L-K-J=1 3/8"; D-M=49 1/16"; E=152 3/8"; E/2=76 3/16"; E/52*15=43 31/32"; F=83 11/16"; F/2=41 27/32"; H=81 11/16"; H/2=40 27/32"; HEIGHT=138 17/32"; J=15 1/2"; J+K+L=106 15/16"; K=29 7/8"; L=61 9/16"; M=59 1/4"; M-(2*(D-L-K-J))=56 1/2"; N=33 11/32"; N+(H/2)=74 3/16"; NOZZLE_BOTTOM_ID=51 3/4"; NOZZLE_BOTTOM_RAD=25 7/8"; NOZZLE_BOTTOM_RAD-3*2=19 7/8"; NOZZLE_HEIGHT=95"; NOZZLE_HEIGHT/7*2=23 3/4"; NOZZLE_SIZE=36"; NOZZLE_TOP_OD=58"; NOZZLE_TOP_RAD=29"; NOZZLE_WB/4=18"; NOZZLE_WB_OD=90"; NOZZLE_WB_RAD=45"; NOZZLE_WB_RAD-2"=43"; P=22 1/8"; R=72"; R*1.1=79 3/16"; R+((B/2)+1.5")=113"; R-((B/2)+1.5")=31"; TRANSITION=36 19/32"; TRANSITION/2=18 9/32"; Type Comments=Vari-Plume Laboratory Exhaust Centrifugal Airfoil Class 1 Arr 10
- 730_CAVP-49H_CLASS_1: ((M - (2 * (D - L - K - J))) / 2) + (TRANSITION / 2)=52 25/32"; (B/2)+1.5"=41"; (B/2)-.125"=39 3/8"; (D-J-K-L)*2=2 3/4"; (F-((F-H)/2))/2=39 27/32"; (M - (2 * (D - L - K - J)))/2=28 1/4"; (NOZZLE_HEIGHT - (NOZZLE_HEIGHT / 8 * 2)) / 2=41 1/4"; (NOZZLE_WB_OD - NOZZLE_TOP_OD) / 4=6 1/4"; -(F-((F-H)/2))/2=-39 27/32"; A=286 3/8"; A/2=143 3/16"; B=79"; B/2=39 1/2"; B/4=19 3/4"; C=176 3/8"; C/2=88 3/16"; CLASS=1"; D=108 5/16"; D-L-K-J=1 3/8"; D-M=49 1/16"; E=152 3/8"; E/2=76 3/16"; E/52*15=43 31/32"; F=83 11/16"; F/2=41 27/32"; H=81 11/16"; H/2=40 27/32"; HEIGHT=138 17/32"; J=15 1/2"; J+K+L=106 15/16"; K=29 7/8"; L=61 9/16"; M=59 1/4"; M-(2*(D-L-K-J))=56 1/2"; N=33 11/32"; N+(H/2)=74 3/16"; NOZZLE_BOTTOM_ID=69 3/8"; NOZZLE_BOTTOM_RAD=34 11/16"; NOZZLE_BOTTOM_RAD-3*2=28 11/16"; NOZZLE_HEIGHT=110"; NOZZLE_HEIGHT/7*2=27 1/2"; NOZZLE_SIZE=49"; NOZZLE_TOP_OD=76"; NOZZLE_TOP_RAD=38"; NOZZLE_WB/4=20 3/16"; NOZZLE_WB_OD=101"; NOZZLE_WB_RAD=50 1/2"; NOZZLE_WB_RAD-2"=48 1/2"; P=22 1/8"; R=72"; R*1.1=79 3/16"; R+((B/2)+1.5")=113"; R-((B/2)+1.5")=31"; TRANSITION=49 1/16"; TRANSITION/2=24 17/32"; Type Comments=Vari-Plume Laboratory Exhaust Centrifugal Airfoil Class 1 Arr 10
- 730_CAVP-49L_CLASS_1: ((M - (2 * (D - L - K - J))) / 2) + (TRANSITION / 2)=52 25/32"; (B/2)+1.5"=41"; (B/2)-.125"=39 3/8"; (D-J-K-L)*2=2 3/4"; (F-((F-H)/2))/2=39 27/32"; (M - (2 * (D - L - K - J)))/2=28 1/4"; (NOZZLE_HEIGHT - (NOZZLE_HEIGHT / 8 * 2)) / 2=41 1/4"; (NOZZLE_WB_OD - NOZZLE_TOP_OD) / 4=6 1/4"; -(F-((F-H)/2))/2=-39 27/32"; A=286 3/8"; A/2=143 3/16"; B=79"; B/2=39 1/2"; B/4=19 3/4"; C=176 3/8"; C/2=88 3/16"; CLASS=1"; D=108 5/16"; D-L-K-J=1 3/8"; D-M=49 1/16"; E=152 3/8"; E/2=76 3/16"; E/52*15=43 31/32"; F=83 11/16"; F/2=41 27/32"; H=81 11/16"; H/2=40 27/32"; HEIGHT=138 17/32"; J=15 1/2"; J+K+L=106 15/16"; K=29 7/8"; L=61 9/16"; M=59 1/4"; M-(2*(D-L-K-J))=56 1/2"; N=33 11/32"; N+(H/2)=74 3/16"; NOZZLE_BOTTOM_ID=69 3/8"; NOZZLE_BOTTOM_RAD=34 11/16"; NOZZLE_BOTTOM_RAD-3*2=28 11/16"; NOZZLE_HEIGHT=110"; NOZZLE_HEIGHT/7*2=27 1/2"; NOZZLE_SIZE=49"; NOZZLE_TOP_OD=76"; NOZZLE_TOP_RAD=38"; NOZZLE_WB/4=20 3/16"; NOZZLE_WB_OD=101"; NOZZLE_WB_RAD=50 1/2"; NOZZLE_WB_RAD-2"=48 1/2"; P=22 1/8"; R=72"; R*1.1=79 3/16"; R+((B/2)+1.5")=113"; R-((B/2)+1.5")=31"; TRANSITION=49 1/16"; TRANSITION/2=24 17/32"; Type Comments=Vari-Plume Laboratory Exhaust Centrifugal Airfoil Class 1 Arr 10
- 730_CAVP-36H_CLASS_2: ((M - (2 * (D - L - K - J))) / 2) + (TRANSITION / 2)=46 17/32"; (B/2)+1.5"=41"; (B/2)-.125"=39 3/8"; (D-J-K-L)*2=2 3/4"; (F-((F-H)/2))/2=39 27/32"; (M - (2 * (D - L - K - J)))/2=28 1/4"; (NOZZLE_HEIGHT - (NOZZLE_HEIGHT / 8 * 2)) / 2=35 5/8"; (NOZZLE_WB_OD - NOZZLE_TOP_OD) / 4=8"; -(F-((F-H)/2))/2=-39 27/32"; A=286 3/8"; A/2=143 3/16"; B=79"; B/2=39 1/2"; B/4=19 3/4"; C=176 3/8"; C/2=88 3/16"; CLASS=2"; D=117"; D-L-K-J=1 3/8"; D-M=57 3/4"; E=152 3/8"; E/2=76 3/16"; E/52*15=43 31/32"; F=83 11/16"; F/2=41 27/32"; H=81 11/16"; H/2=40 27/32"; HEIGHT=138 17/32"; J=15 1/2"; J+K+L=115 5/8"; K=38 5/8"; L=61 1/2"; M=59 1/4"; M-(2*(D-L-K-J))=56 1/2"; N=33 11/32"; N+(H/2)=74 3/16"; NOZZLE_BOTTOM_ID=51 3/4"; NOZZLE_BOTTOM_RAD=25 7/8"; NOZZLE_BOTTOM_RAD-3*2=19 7/8"; NOZZLE_HEIGHT=95"; NOZZLE_HEIGHT/7*2=23 3/4"; NOZZLE_SIZE=36"; NOZZLE_TOP_OD=58"; NOZZLE_TOP_RAD=29"; NOZZLE_WB/4=18"; NOZZLE_WB_OD=90"; NOZZLE_WB_RAD=45"; NOZZLE_WB_RAD-2"=43"; P=29 1/2"; R=72"; R*1.1=79 3/16"; R+((B/2)+1.5")=113"; R-((B/2)+1.5")=31"; TRANSITION=36 19/32"; TRANSITION/2=18 9/32"; Type Comments=Vari-Plume Laboratory Exhaust Centrifugal Airfoil Class 2 Arr 10
- 730_CAVP-36L_CLASS_2: ((M - (2 * (D - L - K - J))) / 2) + (TRANSITION / 2)=46 17/32"; (B/2)+1.5"=41"; (B/2)-.125"=39 3/8"; (D-J-K-L)*2=2 3/4"; (F-((F-H)/2))/2=39 27/32"; (M - (2 * (D - L - K - J)))/2=28 1/4"; (NOZZLE_HEIGHT - (NOZZLE_HEIGHT / 8 * 2)) / 2=35 5/8"; (NOZZLE_WB_OD - NOZZLE_TOP_OD) / 4=8"; -(F-((F-H)/2))/2=-39 27/32"; A=286 3/8"; A/2=143 3/16"; B=79"; B/2=39 1/2"; B/4=19 3/4"; C=176 3/8"; C/2=88 3/16"; CLASS=2"; D=117"; D-L-K-J=1 3/8"; D-M=57 3/4"; E=152 3/8"; E/2=76 3/16"; E/52*15=43 31/32"; F=83 11/16"; F/2=41 27/32"; H=81 11/16"; H/2=40 27/32"; HEIGHT=138 17/32"; J=15 1/2"; J+K+L=115 5/8"; K=38 5/8"; L=61 1/2"; M=59 1/4"; M-(2*(D-L-K-J))=56 1/2"; N=33 11/32"; N+(H/2)=74 3/16"; NOZZLE_BOTTOM_ID=51 3/4"; NOZZLE_BOTTOM_RAD=25 7/8"; NOZZLE_BOTTOM_RAD-3*2=19 7/8"; NOZZLE_HEIGHT=95"; NOZZLE_HEIGHT/7*2=23 3/4"; NOZZLE_SIZE=36"; NOZZLE_TOP_OD=58"; NOZZLE_TOP_RAD=29"; NOZZLE_WB/4=18"; NOZZLE_WB_OD=90"; NOZZLE_WB_RAD=45"; NOZZLE_WB_RAD-2"=43"; P=29 1/2"; R=72"; R*1.1=79 3/16"; R+((B/2)+1.5")=113"; R-((B/2)+1.5")=31"; TRANSITION=36 19/32"; TRANSITION/2=18 9/32"; Type Comments=Vari-Plume Laboratory Exhaust Centrifugal Airfoil Class 2 Arr 10
- 730_CAVP-49H_CLASS_2: ((M - (2 * (D - L - K - J))) / 2) + (TRANSITION / 2)=52 25/32"; (B/2)+1.5"=41"; (B/2)-.125"=39 3/8"; (D-J-K-L)*2=2 3/4"; (F-((F-H)/2))/2=39 27/32"; (M - (2 * (D - L - K - J)))/2=28 1/4"; (NOZZLE_HEIGHT - (NOZZLE_HEIGHT / 8 * 2)) / 2=41 1/4"; (NOZZLE_WB_OD - NOZZLE_TOP_OD) / 4=6 1/4"; -(F-((F-H)/2))/2=-39 27/32"; A=286 3/8"; A/2=143 3/16"; B=79"; B/2=39 1/2"; B/4=19 3/4"; C=176 3/8"; C/2=88 3/16"; CLASS=2"; D=117"; D-L-K-J=1 3/8"; D-M=57 3/4"; E=152 3/8"; E/2=76 3/16"; E/52*15=43 31/32"; F=83 11/16"; F/2=41 27/32"; H=81 11/16"; H/2=40 27/32"; HEIGHT=138 17/32"; J=15 1/2"; J+K+L=115 5/8"; K=38 5/8"; L=61 1/2"; M=59 1/4"; M-(2*(D-L-K-J))=56 1/2"; N=33 11/32"; N+(H/2)=74 3/16"; NOZZLE_BOTTOM_ID=69 3/8"; NOZZLE_BOTTOM_RAD=34 11/16"; NOZZLE_BOTTOM_RAD-3*2=28 11/16"; NOZZLE_HEIGHT=110"; NOZZLE_HEIGHT/7*2=27 1/2"; NOZZLE_SIZE=49"; NOZZLE_TOP_OD=76"; NOZZLE_TOP_RAD=38"; NOZZLE_WB/4=20 3/16"; NOZZLE_WB_OD=101"; NOZZLE_WB_RAD=50 1/2"; NOZZLE_WB_RAD-2"=48 1/2"; P=29 1/2"; R=72"; R*1.1=79 3/16"; R+((B/2)+1.5")=113"; R-((B/2)+1.5")=31"; TRANSITION=49 1/16"; TRANSITION/2=24 17/32"; Type Comments=Vari-Plume Laboratory Exhaust Centrifugal Airfoil Class 2 Arr 10
- 730_CAVP-49L_CLASS_2: ((M - (2 * (D - L - K - J))) / 2) + (TRANSITION / 2)=52 25/32"; (B/2)+1.5"=41"; (B/2)-.125"=39 3/8"; (D-J-K-L)*2=2 3/4"; (F-((F-H)/2))/2=39 27/32"; (M - (2 * (D - L - K - J)))/2=28 1/4"; (NOZZLE_HEIGHT - (NOZZLE_HEIGHT / 8 * 2)) / 2=41 1/4"; (NOZZLE_WB_OD - NOZZLE_TOP_OD) / 4=6 1/4"; -(F-((F-H)/2))/2=-39 27/32"; A=286 3/8"; A/2=143 3/16"; B=79"; B/2=39 1/2"; B/4=19 3/4"; C=176 3/8"; C/2=88 3/16"; CLASS=2"; D=117"; D-L-K-J=1 3/8"; D-M=57 3/4"; E=152 3/8"; E/2=76 3/16"; E/52*15=43 31/32"; F=83 11/16"; F/2=41 27/32"; H=81 11/16"; H/2=40 27/32"; HEIGHT=138 17/32"; J=15 1/2"; J+K+L=115 5/8"; K=38 5/8"; L=61 1/2"; M=59 1/4"; M-(2*(D-L-K-J))=56 1/2"; N=33 11/32"; N+(H/2)=74 3/16"; NOZZLE_BOTTOM_ID=69 3/8"; NOZZLE_BOTTOM_RAD=34 11/16"; NOZZLE_BOTTOM_RAD-3*2=28 11/16"; NOZZLE_HEIGHT=110"; NOZZLE_HEIGHT/7*2=27 1/2"; NOZZLE_SIZE=49"; NOZZLE_TOP_OD=76"; NOZZLE_TOP_RAD=38"; NOZZLE_WB/4=20 3/16"; NOZZLE_WB_OD=101"; NOZZLE_WB_RAD=50 1/2"; NOZZLE_WB_RAD-2"=48 1/2"; P=29 1/2"; R=72"; R*1.1=79 3/16"; R+((B/2)+1.5")=113"; R-((B/2)+1.5")=31"; TRANSITION=49 1/16"; TRANSITION/2=24 17/32"; Type Comments=Vari-Plume Laboratory Exhaust Centrifugal Airfoil Class 2 Arr 10
- 225_CAVP-15H_CLASS_1: ((M - (2 * (D - L - K - J))) / 2) + (TRANSITION / 2)=16 9/32"; (B/2)+1.5"=15 7/32"; (B/2)-.125"=13 19/32"; (D-J-K-L)*2=2"; (F-((F-H)/2))/2=12 13/16"; (M - (2 * (D - L - K - J)))/2=8 23/32"; (NOZZLE_HEIGHT - (NOZZLE_HEIGHT / 8 * 2)) / 2=16 1/8"; (NOZZLE_WB_OD - NOZZLE_TOP_OD) / 4=3 1/4"; -(F-((F-H)/2))/2=-12 13/16"; A=106 11/16"; A/2=53 11/32"; B=27 7/16"; B/2=13 23/32"; B/4=6 7/8"; C=59 3/16"; C/2=29 19/32"; CLASS=1"; D=46 1/16"; D-L-K-J=1"; D-M=26 5/8"; E=48 5/16"; E/2=24 5/32"; E/52*15=13 15/16"; F=29 5/8"; F/2=14 13/16"; H=27 5/8"; H/2=13 13/16"; HEIGHT=45 11/32"; J=8 1/2"; J+K+L=45 1/16"; K=15 1/8"; L=21 7/16"; M=19 7/16"; M-(2*(D-L-K-J))=17 7/16"; N=8 11/32"; N+(H/2)=22 5/32"; NOZZLE_BOTTOM_ID=21 3/8"; NOZZLE_BOTTOM_RAD=10 11/16"; NOZZLE_BOTTOM_RAD-3*2=4 11/16"; NOZZLE_HEIGHT=43"; NOZZLE_HEIGHT/7*2=10 3/4"; NOZZLE_SIZE=15"; NOZZLE_TOP_OD=23"; NOZZLE_TOP_RAD=11 1/2"; NOZZLE_WB/4=7 3/16"; NOZZLE_WB_OD=36"; NOZZLE_WB_RAD=18"; NOZZLE_WB_RAD-2"=16"; P=60"; R=24 1/4"; R*1.1=26 11/16"; R+((B/2)+1.5")=39 15/32"; R-((B/2)+1.5")=9 1/32"; TRANSITION=15 1/8"; TRANSITION/2=7 9/16"; Type Comments=Vari-Plume Laboratory Exhaust Centrifugal Airfoil Class 1 Arr 10
- 270_CAVP-21H_CLASS_1: ((M - (2 * (D - L - K - J))) / 2) + (TRANSITION / 2)=20 19/32"; (B/2)+1.5"=17 15/32"; (B/2)-.125"=15 27/32"; (D-J-K-L)*2=2"; (F-((F-H)/2))/2=15 3/16"; (M - (2 * (D - L - K - J)))/2=10 7/16"; (NOZZLE_HEIGHT - (NOZZLE_HEIGHT / 8 * 2)) / 2=19 25/32"; (NOZZLE_WB_OD - NOZZLE_TOP_OD) / 4=4 9/16"; -(F-((F-H)/2))/2=-15 3/16"; A=116 7/16"; A/2=58 7/32"; B=31 15/16"; B/2=15 31/32"; B/4=8"; C=68 15/16"; C/2=34 15/32"; CLASS=1"; D=54 1/2"; D-L-K-J=1"; D-M=31 5/8"; E=57 9/16"; E/2=28 25/32"; E/52*15=16 19/32"; F=34 3/8"; F/2=17 3/16"; H=32 3/8"; H/2=16 3/16"; HEIGHT=52 1/8"; J=9 1/2"; J+K+L=53 1/2"; K=19 1/8"; L=24 7/8"; M=22 7/8"; M-(2*(D-L-K-J))=20 7/8"; N=10 19/32"; N+(H/2)=26 25/32"; NOZZLE_BOTTOM_ID=28 3/4"; NOZZLE_BOTTOM_RAD=14 3/8"; NOZZLE_BOTTOM_RAD-3*2=8 3/8"; NOZZLE_HEIGHT=52 3/4"; NOZZLE_HEIGHT/7*2=13 3/16"; NOZZLE_SIZE=21"; NOZZLE_TOP_OD=30 3/4"; NOZZLE_TOP_RAD=15 3/8"; NOZZLE_WB/4=9 13/16"; NOZZLE_WB_OD=49"; NOZZLE_WB_RAD=24 1/2"; NOZZLE_WB_RAD-2"=22 1/2"; P=60"; R=27"; R*1.1=29 11/16"; R+((B/2)+1.5")=44 15/32"; R-((B/2)+1.5")=9 17/32"; TRANSITION=20 11/32"; TRANSITION/2=10 5/32"; Type Comments=Vari-Plume Laboratory Exhaust Centrifugal Airfoil Class 1 Arr 10
- 270_CAVP-21L_CLASS_1: ((M - (2 * (D - L - K - J))) / 2) + (TRANSITION / 2)=20 19/32"; (B/2)+1.5"=17 15/32"; (B/2)-.125"=15 27/32"; (D-J-K-L)*2=2"; (F-((F-H)/2))/2=15 3/16"; (M - (2 * (D - L - K - J)))/2=10 7/16"; (NOZZLE_HEIGHT - (NOZZLE_HEIGHT / 8 * 2)) / 2=19 25/32"; (NOZZLE_WB_OD - NOZZLE_TOP_OD) / 4=4 9/16"; -(F-((F-H)/2))/2=-15 3/16"; A=116 7/16"; A/2=58 7/32"; B=31 15/16"; B/2=15 31/32"; B/4=8"; C=68 15/16"; C/2=34 15/32"; CLASS=1"; D=54 1/2"; D-L-K-J=1"; D-M=31 5/8"; E=57 9/16"; E/2=28 25/32"; E/52*15=16 19/32"; F=34 3/8"; F/2=17 3/16"; H=32 3/8"; H/2=16 3/16"; HEIGHT=52 1/8"; J=9 1/2"; J+K+L=53 1/2"; K=19 1/8"; L=24 7/8"; M=22 7/8"; M-(2*(D-L-K-J))=20 7/8"; N=10 19/32"; N+(H/2)=26 25/32"; NOZZLE_BOTTOM_ID=28 3/4"; NOZZLE_BOTTOM_RAD=14 3/8"; NOZZLE_BOTTOM_RAD-3*2=8 3/8"; NOZZLE_HEIGHT=52 3/4"; NOZZLE_HEIGHT/7*2=13 3/16"; NOZZLE_SIZE=21"; NOZZLE_TOP_OD=30 3/4"; NOZZLE_TOP_RAD=15 3/8"; NOZZLE_WB/4=9 13/16"; NOZZLE_WB_OD=49"; NOZZLE_WB_RAD=24 1/2"; NOZZLE_WB_RAD-2"=22 1/2"; P=60"; R=27"; R*1.1=29 11/16"; R+((B/2)+1.5")=44 15/32"; R-((B/2)+1.5")=9 17/32"; TRANSITION=20 11/32"; TRANSITION/2=10 5/32"; Type Comments=Vari-Plume Laboratory Exhaust Centrifugal Airfoil Class 1 Arr 10
- 270_CAVP-21H_CLASS_2: ((M - (2 * (D - L - K - J))) / 2) + (TRANSITION / 2)=20 19/32"; (B/2)+1.5"=17 15/32"; (B/2)-.125"=15 27/32"; (D-J-K-L)*2=2"; (F-((F-H)/2))/2=15 3/16"; (M - (2 * (D - L - K - J)))/2=10 7/16"; (NOZZLE_HEIGHT - (NOZZLE_HEIGHT / 8 * 2)) / 2=19 25/32"; (NOZZLE_WB_OD - NOZZLE_TOP_OD) / 4=4 9/16"; -(F-((F-H)/2))/2=-15 3/16"; A=116 7/16"; A/2=58 7/32"; B=31 15/16"; B/2=15 31/32"; B/4=8"; C=68 15/16"; C/2=34 15/32"; CLASS=2"; D=56 1/2"; D-L-K-J=1"; D-M=33 5/8"; E=57 9/16"; E/2=28 25/32"; E/52*15=16 19/32"; F=34 3/8"; F/2=17 3/16"; H=32 3/8"; H/2=16 3/16"; HEIGHT=52 1/8"; J=9 1/4"; J+K+L=55 1/2"; K=21 3/8"; L=24 7/8"; M=22 7/8"; M-(2*(D-L-K-J))=20 7/8"; N=10"; N+(H/2)=26 3/16"; NOZZLE_BOTTOM_ID=28 3/4"; NOZZLE_BOTTOM_RAD=14 3/8"; NOZZLE_BOTTOM_RAD-3*2=8 3/8"; NOZZLE_HEIGHT=52 3/4"; NOZZLE_HEIGHT/7*2=13 3/16"; NOZZLE_SIZE=21"; NOZZLE_TOP_OD=30 3/4"; NOZZLE_TOP_RAD=15 3/8"; NOZZLE_WB/4=9 13/16"; NOZZLE_WB_OD=49"; NOZZLE_WB_RAD=24 1/2"; NOZZLE_WB_RAD-2"=22 1/2"; P=60"; R=27"; R*1.1=29 11/16"; R+((B/2)+1.5")=44 15/32"; R-((B/2)+1.5")=9 17/32"; TRANSITION=20 11/32"; TRANSITION/2=10 5/32"; Type Comments=Vari-Plume Laboratory Exhaust Centrifugal Airfoil Class 2 Arr 10
- 270_CAVP-21L_CLASS_2: ((M - (2 * (D - L - K - J))) / 2) + (TRANSITION / 2)=20 19/32"; (B/2)+1.5"=17 15/32"; (B/2)-.125"=15 27/32"; (D-J-K-L)*2=2"; (F-((F-H)/2))/2=15 3/16"; (M - (2 * (D - L - K - J)))/2=10 7/16"; (NOZZLE_HEIGHT - (NOZZLE_HEIGHT / 8 * 2)) / 2=19 25/32"; (NOZZLE_WB_OD - NOZZLE_TOP_OD) / 4=4 9/16"; -(F-((F-H)/2))/2=-15 3/16"; A=116 7/16"; A/2=58 7/32"; B=31 15/16"; B/2=15 31/32"; B/4=8"; C=68 15/16"; C/2=34 15/32"; CLASS=2"; D=56 1/2"; D-L-K-J=1"; D-M=33 5/8"; E=57 9/16"; E/2=28 25/32"; E/52*15=16 19/32"; F=34 3/8"; F/2=17 3/16"; H=32 3/8"; H/2=16 3/16"; HEIGHT=52 1/8"; J=9 1/4"; J+K+L=55 1/2"; K=21 3/8"; L=24 7/8"; M=22 7/8"; M-(2*(D-L-K-J))=20 7/8"; N=10"; N+(H/2)=26 3/16"; NOZZLE_BOTTOM_ID=28 3/4"; NOZZLE_BOTTOM_RAD=14 3/8"; NOZZLE_BOTTOM_RAD-3*2=8 3/8"; NOZZLE_HEIGHT=52 3/4"; NOZZLE_HEIGHT/7*2=13 3/16"; NOZZLE_SIZE=21"; NOZZLE_TOP_OD=30 3/4"; NOZZLE_TOP_RAD=15 3/8"; NOZZLE_WB/4=9 13/16"; NOZZLE_WB_OD=49"; NOZZLE_WB_RAD=24 1/2"; NOZZLE_WB_RAD-2"=22 1/2"; P=60"; R=27"; R*1.1=29 11/16"; R+((B/2)+1.5")=44 15/32"; R-((B/2)+1.5")=9 17/32"; TRANSITION=20 11/32"; TRANSITION/2=10 5/32"; Type Comments=Vari-Plume Laboratory Exhaust Centrifugal Airfoil Class 2 Arr 10
- 300_CAVP-21H_CLASS_1: ((M - (2 * (D - L - K - J))) / 2) + (TRANSITION / 2)=21 3/4"; (B/2)+1.5"=18 31/32"; (B/2)-.125"=17 11/32"; (D-J-K-L)*2=2"; (F-((F-H)/2))/2=16 11/16"; (M - (2 * (D - L - K - J)))/2=11 19/32"; (NOZZLE_HEIGHT - (NOZZLE_HEIGHT / 8 * 2)) / 2=19 25/32"; (NOZZLE_WB_OD - NOZZLE_TOP_OD) / 4=4 9/16"; -(F-((F-H)/2))/2=-16 11/16"; A=122 7/16"; A/2=61 7/32"; B=34 15/16"; B/2=17 15/32"; B/4=8 3/4"; C=74 15/16"; C/2=37 15/32"; CLASS=1"; D=57 5/16"; D-L-K-J=1"; D-M=32 1/8"; E=63 3/4"; E/2=31 7/8"; E/52*15=18 3/8"; F=37 3/8"; F/2=18 11/16"; H=35 3/8"; H/2=17 11/16"; HEIGHT=57 27/32"; J=10"; J+K+L=56 5/16"; K=19 1/8"; L=27 3/16"; M=25 3/16"; M-(2*(D-L-K-J))=23 3/16"; N=12 3/16"; N+(H/2)=29 7/8"; NOZZLE_BOTTOM_ID=28 3/4"; NOZZLE_BOTTOM_RAD=14 3/8"; NOZZLE_BOTTOM_RAD-3*2=8 3/8"; NOZZLE_HEIGHT=52 3/4"; NOZZLE_HEIGHT/7*2=13 3/16"; NOZZLE_SIZE=21"; NOZZLE_TOP_OD=30 3/4"; NOZZLE_TOP_RAD=15 3/8"; NOZZLE_WB/4=9 13/16"; NOZZLE_WB_OD=49"; NOZZLE_WB_RAD=24 1/2"; NOZZLE_WB_RAD-2"=22 1/2"; P=60"; R=30"; R*1.1=33"; R+((B/2)+1.5")=48 31/32"; R-((B/2)+1.5")=11 1/32"; TRANSITION=20 11/32"; TRANSITION/2=10 5/32"; Type Comments=Vari-Plume Laboratory Exhaust Centrifugal Airfoil Class 1 Arr 10
- 300_CAVP-21L_CLASS_1: ((M - (2 * (D - L - K - J))) / 2) + (TRANSITION / 2)=21 3/4"; (B/2)+1.5"=18 31/32"; (B/2)-.125"=17 11/32"; (D-J-K-L)*2=2"; (F-((F-H)/2))/2=16 11/16"; (M - (2 * (D - L - K - J)))/2=11 19/32"; (NOZZLE_HEIGHT - (NOZZLE_HEIGHT / 8 * 2)) / 2=19 25/32"; (NOZZLE_WB_OD - NOZZLE_TOP_OD) / 4=4 9/16"; -(F-((F-H)/2))/2=-16 11/16"; A=122 7/16"; A/2=61 7/32"; B=34 15/16"; B/2=17 15/32"; B/4=8 3/4"; C=74 15/16"; C/2=37 15/32"; CLASS=1"; D=57 5/16"; D-L-K-J=1"; D-M=32 1/8"; E=63 3/4"; E/2=31 7/8"; E/52*15=18 3/8"; F=37 3/8"; F/2=18 11/16"; H=35 3/8"; H/2=17 11/16"; HEIGHT=57 27/32"; J=10"; J+K+L=56 5/16"; K=19 1/8"; L=27 3/16"; M=25 3/16"; M-(2*(D-L-K-J))=23 3/16"; N=12 3/16"; N+(H/2)=29 7/8"; NOZZLE_BOTTOM_ID=28 3/4"; NOZZLE_BOTTOM_RAD=14 3/8"; NOZZLE_BOTTOM_RAD-3*2=8 3/8"; NOZZLE_HEIGHT=52 3/4"; NOZZLE_HEIGHT/7*2=13 3/16"; NOZZLE_SIZE=21"; NOZZLE_TOP_OD=30 3/4"; NOZZLE_TOP_RAD=15 3/8"; NOZZLE_WB/4=9 13/16"; NOZZLE_WB_OD=49"; NOZZLE_WB_RAD=24 1/2"; NOZZLE_WB_RAD-2"=22 1/2"; P=60"; R=30"; R*1.1=33"; R+((B/2)+1.5")=48 31/32"; R-((B/2)+1.5")=11 1/32"; TRANSITION=20 11/32"; TRANSITION/2=10 5/32"; Type Comments=Vari-Plume Laboratory Exhaust Centrifugal Airfoil Class 1 Arr 10
- 300_CAVP-21H_CLASS_2: ((M - (2 * (D - L - K - J))) / 2) + (TRANSITION / 2)=21 3/4"; (B/2)+1.5"=18 31/32"; (B/2)-.125"=17 11/32"; (D-J-K-L)*2=2"; (F-((F-H)/2))/2=16 11/16"; (M - (2 * (D - L - K - J)))/2=11 19/32"; (NOZZLE_HEIGHT - (NOZZLE_HEIGHT / 8 * 2)) / 2=19 25/32"; (NOZZLE_WB_OD - NOZZLE_TOP_OD) / 4=4 9/16"; -(F-((F-H)/2))/2=-16 11/16"; A=122 7/16"; A/2=61 7/32"; B=34 15/16"; B/2=17 15/32"; B/4=8 3/4"; C=74 15/16"; C/2=37 15/32"; CLASS=2"; D=61 3/16"; D-L-K-J=1"; D-M=36"; E=63 3/4"; E/2=31 7/8"; E/52*15=18 3/8"; F=37 3/8"; F/2=18 11/16"; H=35 3/8"; H/2=17 11/16"; HEIGHT=57 27/32"; J=10"; J+K+L=60 3/16"; K=23"; L=27 3/16"; M=25 3/16"; M-(2*(D-L-K-J))=23 3/16"; N=12 3/16"; N+(H/2)=29 7/8"; NOZZLE_BOTTOM_ID=28 3/4"; NOZZLE_BOTTOM_RAD=14 3/8"; NOZZLE_BOTTOM_RAD-3*2=8 3/8"; NOZZLE_HEIGHT=52 3/4"; NOZZLE_HEIGHT/7*2=13 3/16"; NOZZLE_SIZE=21"; NOZZLE_TOP_OD=30 3/4"; NOZZLE_TOP_RAD=15 3/8"; NOZZLE_WB/4=9 13/16"; NOZZLE_WB_OD=49"; NOZZLE_WB_RAD=24 1/2"; NOZZLE_WB_RAD-2"=22 1/2"; P=18 1/4"; R=30"; R*1.1=33"; R+((B/2)+1.5")=48 31/32"; R-((B/2)+1.5")=11 1/32"; TRANSITION=20 11/32"; TRANSITION/2=10 5/32"; Type Comments=Vari-Plume Laboratory Exhaust Centrifugal Airfoil Class 2 Arr 10
- 300_CAVP-21L_CLASS_2: ((M - (2 * (D - L - K - J))) / 2) + (TRANSITION / 2)=21 3/4"; (B/2)+1.5"=18 31/32"; (B/2)-.125"=17 11/32"; (D-J-K-L)*2=2"; (F-((F-H)/2))/2=16 11/16"; (M - (2 * (D - L - K - J)))/2=11 19/32"; (NOZZLE_HEIGHT - (NOZZLE_HEIGHT / 8 * 2)) / 2=19 25/32"; (NOZZLE_WB_OD - NOZZLE_TOP_OD) / 4=4 9/16"; -(F-((F-H)/2))/2=-16 11/16"; A=122 7/16"; A/2=61 7/32"; B=34 15/16"; B/2=17 15/32"; B/4=8 3/4"; C=74 15/16"; C/2=37 15/32"; CLASS=2"; D=61 3/16"; D-L-K-J=1"; D-M=36"; E=63 3/4"; E/2=31 7/8"; E/52*15=18 3/8"; F=37 3/8"; F/2=18 11/16"; H=35 3/8"; H/2=17 11/16"; HEIGHT=57 27/32"; J=10"; J+K+L=60 3/16"; K=23"; L=27 3/16"; M=25 3/16"; M-(2*(D-L-K-J))=23 3/16"; N=12 3/16"; N+(H/2)=29 7/8"; NOZZLE_BOTTOM_ID=28 3/4"; NOZZLE_BOTTOM_RAD=14 3/8"; NOZZLE_BOTTOM_RAD-3*2=8 3/8"; NOZZLE_HEIGHT=52 3/4"; NOZZLE_HEIGHT/7*2=13 3/16"; NOZZLE_SIZE=21"; NOZZLE_TOP_OD=30 3/4"; NOZZLE_TOP_RAD=15 3/8"; NOZZLE_WB/4=9 13/16"; NOZZLE_WB_OD=49"; NOZZLE_WB_RAD=24 1/2"; NOZZLE_WB_RAD-2"=22 1/2"; P=18 1/4"; R=30"; R*1.1=33"; R+((B/2)+1.5")=48 31/32"; R-((B/2)+1.5")=11 1/32"; TRANSITION=20 11/32"; TRANSITION/2=10 5/32"; Type Comments=Vari-Plume Laboratory Exhaust Centrifugal Airfoil Class 2 Arr 10
- 330_CAVP-21H_CLASS_1: ((M - (2 * (D - L - K - J))) / 2) + (TRANSITION / 2)=22 29/32"; (B/2)+1.5"=20 15/32"; (B/2)-.125"=18 27/32"; (D-J-K-L)*2=2"; (F-((F-H)/2))/2=18 3/16"; (M - (2 * (D - L - K - J)))/2=12 3/4"; (NOZZLE_HEIGHT - (NOZZLE_HEIGHT / 8 * 2)) / 2=19 25/32"; (NOZZLE_WB_OD - NOZZLE_TOP_OD) / 4=4 9/16"; -(F-((F-H)/2))/2=-18 3/16"; A=144 7/16"; A/2=72 7/32"; B=37 15/16"; B/2=18 31/32"; B/4=9 1/2"; C=82 13/16"; C/2=41 13/32"; CLASS=1"; D=60 1/4"; D-L-K-J=1"; D-M=32 3/4"; E=69 15/16"; E/2=34 31/32"; E/52*15=20 3/16"; F=40 3/8"; F/2=20 3/16"; H=38 3/8"; H/2=19 3/16"; HEIGHT=63 17/32"; J=10 1/2"; J+K+L=59 1/4"; K=19 1/4"; L=29 1/2"; M=27 1/2"; M-(2*(D-L-K-J))=25 1/2"; N=13 25/32"; N+(H/2)=32 31/32"; NOZZLE_BOTTOM_ID=28 3/4"; NOZZLE_BOTTOM_RAD=14 3/8"; NOZZLE_BOTTOM_RAD-3*2=8 3/8"; NOZZLE_HEIGHT=52 3/4"; NOZZLE_HEIGHT/7*2=13 3/16"; NOZZLE_SIZE=21"; NOZZLE_TOP_OD=30 3/4"; NOZZLE_TOP_RAD=15 3/8"; NOZZLE_WB/4=9 13/16"; NOZZLE_WB_OD=49"; NOZZLE_WB_RAD=24 1/2"; NOZZLE_WB_RAD-2"=22 1/2"; P=60"; R=33"; R*1.1=36 5/16"; R+((B/2)+1.5")=53 15/32"; R-((B/2)+1.5")=12 17/32"; TRANSITION=20 11/32"; TRANSITION/2=10 5/32"; Type Comments=Vari-Plume Laboratory Exhaust Centrifugal Airfoil Class 1 Arr 10
- 330_CAVP-21L_CLASS_1: ((M - (2 * (D - L - K - J))) / 2) + (TRANSITION / 2)=22 29/32"; (B/2)+1.5"=20 15/32"; (B/2)-.125"=18 27/32"; (D-J-K-L)*2=2"; (F-((F-H)/2))/2=18 3/16"; (M - (2 * (D - L - K - J)))/2=12 3/4"; (NOZZLE_HEIGHT - (NOZZLE_HEIGHT / 8 * 2)) / 2=19 25/32"; (NOZZLE_WB_OD - NOZZLE_TOP_OD) / 4=4 9/16"; -(F-((F-H)/2))/2=-18 3/16"; A=144 7/16"; A/2=72 7/32"; B=37 15/16"; B/2=18 31/32"; B/4=9 1/2"; C=82 13/16"; C/2=41 13/32"; CLASS=1"; D=60 1/4"; D-L-K-J=1"; D-M=32 3/4"; E=69 15/16"; E/2=34 31/32"; E/52*15=20 3/16"; F=40 3/8"; F/2=20 3/16"; H=38 3/8"; H/2=19 3/16"; HEIGHT=63 17/32"; J=10 1/2"; J+K+L=59 1/4"; K=19 1/4"; L=29 1/2"; M=27 1/2"; M-(2*(D-L-K-J))=25 1/2"; N=13 25/32"; N+(H/2)=32 31/32"; NOZZLE_BOTTOM_ID=28 3/4"; NOZZLE_BOTTOM_RAD=14 3/8"; NOZZLE_BOTTOM_RAD-3*2=8 3/8"; NOZZLE_HEIGHT=52 3/4"; NOZZLE_HEIGHT/7*2=13 3/16"; NOZZLE_SIZE=21"; NOZZLE_TOP_OD=30 3/4"; NOZZLE_TOP_RAD=15 3/8"; NOZZLE_WB/4=9 13/16"; NOZZLE_WB_OD=49"; NOZZLE_WB_RAD=24 1/2"; NOZZLE_WB_RAD-2"=22 1/2"; P=60"; R=33"; R*1.1=36 5/16"; R+((B/2)+1.5")=53 15/32"; R-((B/2)+1.5")=12 17/32"; TRANSITION=20 11/32"; TRANSITION/2=10 5/32"; Type Comments=Vari-Plume Laboratory Exhaust Centrifugal Airfoil Class 1 Arr 10
- 330_CAVP-21L_CLASS_2: ((M - (2 * (D - L - K - J))) / 2) + (TRANSITION / 2)=22 29/32"; (B/2)+1.5"=20 15/32"; (B/2)-.125"=18 27/32"; (D-J-K-L)*2=2"; (F-((F-H)/2))/2=18 3/16"; (M - (2 * (D - L - K - J)))/2=12 3/4"; (NOZZLE_HEIGHT - (NOZZLE_HEIGHT / 8 * 2)) / 2=19 25/32"; (NOZZLE_WB_OD - NOZZLE_TOP_OD) / 4=4 9/16"; -(F-((F-H)/2))/2=-18 3/16"; A=144 7/16"; A/2=72 7/32"; B=37 15/16"; B/2=18 31/32"; B/4=9 1/2"; C=82 13/16"; C/2=41 13/32"; CLASS=2"; D=64"; D-L-K-J=1"; D-M=36 1/2"; E=69 15/16"; E/2=34 31/32"; E/52*15=20 3/16"; F=40 3/8"; F/2=20 3/16"; H=38 3/8"; H/2=19 3/16"; HEIGHT=63 17/32"; J=10 1/2"; J+K+L=63"; K=23"; L=29 1/2"; M=27 1/2"; M-(2*(D-L-K-J))=25 1/2"; N=13 25/32"; N+(H/2)=32 31/32"; NOZZLE_BOTTOM_ID=28 3/4"; NOZZLE_BOTTOM_RAD=14 3/8"; NOZZLE_BOTTOM_RAD-3*2=8 3/8"; NOZZLE_HEIGHT=52 3/4"; NOZZLE_HEIGHT/7*2=13 3/16"; NOZZLE_SIZE=21"; NOZZLE_TOP_OD=30 3/4"; NOZZLE_TOP_RAD=15 3/8"; NOZZLE_WB/4=9 13/16"; NOZZLE_WB_OD=49"; NOZZLE_WB_RAD=24 1/2"; NOZZLE_WB_RAD-2"=22 1/2"; P=60"; R=33"; R*1.1=36 5/16"; R+((B/2)+1.5")=53 15/32"; R-((B/2)+1.5")=12 17/32"; TRANSITION=20 11/32"; TRANSITION/2=10 5/32"; Type Comments=Vari-Plume Laboratory Exhaust Centrifugal Airfoil Class 2 Arr 10
- 330_CAVP-21H_CLASS_2: ((M - (2 * (D - L - K - J))) / 2) + (TRANSITION / 2)=22 29/32"; (B/2)+1.5"=20 15/32"; (B/2)-.125"=18 27/32"; (D-J-K-L)*2=2"; (F-((F-H)/2))/2=18 3/16"; (M - (2 * (D - L - K - J)))/2=12 3/4"; (NOZZLE_HEIGHT - (NOZZLE_HEIGHT / 8 * 2)) / 2=19 25/32"; (NOZZLE_WB_OD - NOZZLE_TOP_OD) / 4=4 9/16"; -(F-((F-H)/2))/2=-18 3/16"; A=144 7/16"; A/2=72 7/32"; B=37 15/16"; B/2=18 31/32"; B/4=9 1/2"; C=82 13/16"; C/2=41 13/32"; CLASS=2"; D=64"; D-L-K-J=1"; D-M=36 1/2"; E=69 15/16"; E/2=34 31/32"; E/52*15=20 3/16"; F=40 3/8"; F/2=20 3/16"; H=38 3/8"; H/2=19 3/16"; HEIGHT=63 17/32"; J=10 1/2"; J+K+L=63"; K=23"; L=29 1/2"; M=27 1/2"; M-(2*(D-L-K-J))=25 1/2"; N=13 25/32"; N+(H/2)=32 31/32"; NOZZLE_BOTTOM_ID=28 3/4"; NOZZLE_BOTTOM_RAD=14 3/8"; NOZZLE_BOTTOM_RAD-3*2=8 3/8"; NOZZLE_HEIGHT=52 3/4"; NOZZLE_HEIGHT/7*2=13 3/16"; NOZZLE_SIZE=21"; NOZZLE_TOP_OD=30 3/4"; NOZZLE_TOP_RAD=15 3/8"; NOZZLE_WB/4=9 13/16"; NOZZLE_WB_OD=49"; NOZZLE_WB_RAD=24 1/2"; NOZZLE_WB_RAD-2"=22 1/2"; P=60"; R=33"; R*1.1=36 5/16"; R+((B/2)+1.5")=53 15/32"; R-((B/2)+1.5")=12 17/32"; TRANSITION=20 11/32"; TRANSITION/2=10 5/32"; Type Comments=Vari-Plume Laboratory Exhaust Centrifugal Airfoil Class 2 Arr 10
- 365_CAVP-21H_CLASS_1: ((M - (2 * (D - L - K - J))) / 2) + (TRANSITION / 2)=24 7/32"; (B/2)+1.5"=22 23/32"; (B/2)-.125"=21 3/32"; (D-J-K-L)*2=2"; (F-((F-H)/2))/2=20 7/16"; (M - (2 * (D - L - K - J)))/2=14 1/16"; (NOZZLE_HEIGHT - (NOZZLE_HEIGHT / 8 * 2)) / 2=19 25/32"; (NOZZLE_WB_OD - NOZZLE_TOP_OD) / 4=4 9/16"; -(F-((F-H)/2))/2=-20 7/16"; A=153 13/16"; A/2=76 29/32"; B=42 7/16"; B/2=21 7/32"; B/4=10 5/8"; C=92 3/16"; C/2=46 3/32"; CLASS=1"; D=66 7/8"; D-L-K-J=1"; D-M=36 3/4"; E=77 5/16"; E/2=38 21/32"; E/52*15=22 5/16"; F=44 7/8"; F/2=22 7/16"; H=42 7/8"; H/2=21 7/16"; HEIGHT=69 3/4"; J=11"; J+K+L=65 7/8"; K=22 3/4"; L=32 1/8"; M=30 1/8"; M-(2*(D-L-K-J))=28 1/8"; N=15 7/32"; N+(H/2)=36 21/32"; NOZZLE_BOTTOM_ID=28 3/4"; NOZZLE_BOTTOM_RAD=14 3/8"; NOZZLE_BOTTOM_RAD-3*2=8 3/8"; NOZZLE_HEIGHT=52 3/4"; NOZZLE_HEIGHT/7*2=13 3/16"; NOZZLE_SIZE=21"; NOZZLE_TOP_OD=30 3/4"; NOZZLE_TOP_RAD=15 3/8"; NOZZLE_WB/4=9 13/16"; NOZZLE_WB_OD=49"; NOZZLE_WB_RAD=24 1/2"; NOZZLE_WB_RAD-2"=22 1/2"; P=18 1/4"; R=36"; R*1.1=39 19/32"; R+((B/2)+1.5")=58 23/32"; R-((B/2)+1.5")=13 9/32"; TRANSITION=20 11/32"; TRANSITION/2=10 5/32"; Type Comments=Vari-Plume Laboratory Exhaust Centrifugal Airfoil Class 1 Arr 10
- 365_CAVP-21L_CLASS_1: ((M - (2 * (D - L - K - J))) / 2) + (TRANSITION / 2)=24 7/32"; (B/2)+1.5"=22 23/32"; (B/2)-.125"=21 3/32"; (D-J-K-L)*2=2"; (F-((F-H)/2))/2=20 7/16"; (M - (2 * (D - L - K - J)))/2=14 1/16"; (NOZZLE_HEIGHT - (NOZZLE_HEIGHT / 8 * 2)) / 2=19 25/32"; (NOZZLE_WB_OD - NOZZLE_TOP_OD) / 4=4 9/16"; -(F-((F-H)/2))/2=-20 7/16"; A=153 13/16"; A/2=76 29/32"; B=42 7/16"; B/2=21 7/32"; B/4=10 5/8"; C=92 3/16"; C/2=46 3/32"; CLASS=1"; D=66 7/8"; D-L-K-J=1"; D-M=36 3/4"; E=77 5/16"; E/2=38 21/32"; E/52*15=22 5/16"; F=44 7/8"; F/2=22 7/16"; H=42 7/8"; H/2=21 7/16"; HEIGHT=69 3/4"; J=11"; J+K+L=65 7/8"; K=22 3/4"; L=32 1/8"; M=30 1/8"; M-(2*(D-L-K-J))=28 1/8"; N=15 7/32"; N+(H/2)=36 21/32"; NOZZLE_BOTTOM_ID=28 3/4"; NOZZLE_BOTTOM_RAD=14 3/8"; NOZZLE_BOTTOM_RAD-3*2=8 3/8"; NOZZLE_HEIGHT=52 3/4"; NOZZLE_HEIGHT/7*2=13 3/16"; NOZZLE_SIZE=21"; NOZZLE_TOP_OD=30 3/4"; NOZZLE_TOP_RAD=15 3/8"; NOZZLE_WB/4=9 13/16"; NOZZLE_WB_OD=49"; NOZZLE_WB_RAD=24 1/2"; NOZZLE_WB_RAD-2"=22 1/2"; P=18 1/4"; R=36"; R*1.1=39 19/32"; R+((B/2)+1.5")=58 23/32"; R-((B/2)+1.5")=13 9/32"; TRANSITION=20 11/32"; TRANSITION/2=10 5/32"; Type Comments=Vari-Plume Laboratory Exhaust Centrifugal Airfoil Class 1 Arr 10
- 365_CAVP-21H_CLASS_2: ((M - (2 * (D - L - K - J))) / 2) + (TRANSITION / 2)=24 7/32"; (B/2)+1.5"=22 23/32"; (B/2)-.125"=21 3/32"; (D-J-K-L)*2=2"; (F-((F-H)/2))/2=20 7/16"; (M - (2 * (D - L - K - J)))/2=14 1/16"; (NOZZLE_HEIGHT - (NOZZLE_HEIGHT / 8 * 2)) / 2=19 25/32"; (NOZZLE_WB_OD - NOZZLE_TOP_OD) / 4=4 9/16"; -(F-((F-H)/2))/2=-20 7/16"; A=153 13/16"; A/2=76 29/32"; B=42 7/16"; B/2=21 7/32"; B/4=10 5/8"; C=92 3/16"; C/2=46 3/32"; CLASS=2"; D=67 1/8"; D-L-K-J=1"; D-M=37"; E=77 5/16"; E/2=38 21/32"; E/52*15=22 5/16"; F=44 7/8"; F/2=22 7/16"; H=42 7/8"; H/2=21 7/16"; HEIGHT=69 3/4"; J=11"; J+K+L=66 1/8"; K=23"; L=32 1/8"; M=30 1/8"; M-(2*(D-L-K-J))=28 1/8"; N=15 7/32"; N+(H/2)=36 21/32"; NOZZLE_BOTTOM_ID=28 3/4"; NOZZLE_BOTTOM_RAD=14 3/8"; NOZZLE_BOTTOM_RAD-3*2=8 3/8"; NOZZLE_HEIGHT=52 3/4"; NOZZLE_HEIGHT/7*2=13 3/16"; NOZZLE_SIZE=21"; NOZZLE_TOP_OD=30 3/4"; NOZZLE_TOP_RAD=15 3/8"; NOZZLE_WB/4=9 13/16"; NOZZLE_WB_OD=49"; NOZZLE_WB_RAD=24 1/2"; NOZZLE_WB_RAD-2"=22 1/2"; P=18 1/2"; R=36"; R*1.1=39 19/32"; R+((B/2)+1.5")=58 23/32"; R-((B/2)+1.5")=13 9/32"; TRANSITION=20 11/32"; TRANSITION/2=10 5/32"; Type Comments=Vari-Plume Laboratory Exhaust Centrifugal Airfoil Class 2 Arr 10
- 365_CAVP-21L_CLASS_2: ((M - (2 * (D - L - K - J))) / 2) + (TRANSITION / 2)=24 7/32"; (B/2)+1.5"=22 23/32"; (B/2)-.125"=21 3/32"; (D-J-K-L)*2=2"; (F-((F-H)/2))/2=20 7/16"; (M - (2 * (D - L - K - J)))/2=14 1/16"; (NOZZLE_HEIGHT - (NOZZLE_HEIGHT / 8 * 2)) / 2=19 25/32"; (NOZZLE_WB_OD - NOZZLE_TOP_OD) / 4=4 9/16"; -(F-((F-H)/2))/2=-20 7/16"; A=153 13/16"; A/2=76 29/32"; B=42 7/16"; B/2=21 7/32"; B/4=10 5/8"; C=92 3/16"; C/2=46 3/32"; CLASS=2"; D=67 1/8"; D-L-K-J=1"; D-M=37"; E=77 5/16"; E/2=38 21/32"; E/52*15=22 5/16"; F=44 7/8"; F/2=22 7/16"; H=42 7/8"; H/2=21 7/16"; HEIGHT=69 3/4"; J=11"; J+K+L=66 1/8"; K=23"; L=32 1/8"; M=30 1/8"; M-(2*(D-L-K-J))=28 1/8"; N=15 7/32"; N+(H/2)=36 21/32"; NOZZLE_BOTTOM_ID=28 3/4"; NOZZLE_BOTTOM_RAD=14 3/8"; NOZZLE_BOTTOM_RAD-3*2=8 3/8"; NOZZLE_HEIGHT=52 3/4"; NOZZLE_HEIGHT/7*2=13 3/16"; NOZZLE_SIZE=21"; NOZZLE_TOP_OD=30 3/4"; NOZZLE_TOP_RAD=15 3/8"; NOZZLE_WB/4=9 13/16"; NOZZLE_WB_OD=49"; NOZZLE_WB_RAD=24 1/2"; NOZZLE_WB_RAD-2"=22 1/2"; P=18 1/2"; R=36"; R*1.1=39 19/32"; R+((B/2)+1.5")=58 23/32"; R-((B/2)+1.5")=13 9/32"; TRANSITION=20 11/32"; TRANSITION/2=10 5/32"; Type Comments=Vari-Plume Laboratory Exhaust Centrifugal Airfoil Class 2 Arr 10
- 402_CAVP-21H_CLASS_1: ((M - (2 * (D - L - K - J))) / 2) + (TRANSITION / 2)=25 29/32"; (B/2)+1.5"=24 3/32"; (B/2)-.125"=22 15/32"; (D-J-K-L)*2=2 3/4"; (F-((F-H)/2))/2=22 3/8"; (M - (2 * (D - L - K - J)))/2=15 3/4"; (NOZZLE_HEIGHT - (NOZZLE_HEIGHT / 8 * 2)) / 2=19 25/32"; (NOZZLE_WB_OD - NOZZLE_TOP_OD) / 4=4 9/16"; -(F-((F-H)/2))/2=-22 3/8"; A=178 3/4"; A/2=89 3/8"; B=45 3/16"; B/2=22 19/32"; B/4=11 5/16"; C=100 3/4"; C/2=50 3/8"; CLASS=1"; D=72 1/4"; D-L-K-J=1 3/8"; D-M=38"; E=84 15/16"; E/2=42 15/32"; E/52*15=24 1/2"; F=48 3/4"; F/2=24 3/8"; H=46 3/4"; H/2=23 3/8"; HEIGHT=77 3/32"; J=12 1/2"; J+K+L=70 7/8"; K=21 7/8"; L=36 1/2"; M=34 1/4"; M-(2*(D-L-K-J))=31 1/2"; N=17 3/32"; N+(H/2)=40 15/32"; NOZZLE_BOTTOM_ID=28 3/4"; NOZZLE_BOTTOM_RAD=14 3/8"; NOZZLE_BOTTOM_RAD-3*2=8 3/8"; NOZZLE_HEIGHT=52 3/4"; NOZZLE_HEIGHT/7*2=13 3/16"; NOZZLE_SIZE=21"; NOZZLE_TOP_OD=30 3/4"; NOZZLE_TOP_RAD=15 3/8"; NOZZLE_WB/4=9 13/16"; NOZZLE_WB_OD=49"; NOZZLE_WB_RAD=24 1/2"; NOZZLE_WB_RAD-2"=22 1/2"; P=18 1/4"; R=40"; R*1.1=44"; R+((B/2)+1.5")=64 3/32"; R-((B/2)+1.5")=15 29/32"; TRANSITION=20 11/32"; TRANSITION/2=10 5/32"; Type Comments=Vari-Plume Laboratory Exhaust Centrifugal Airfoil Class 1 Arr 10
- 402_CAVP-21L_CLASS_1: ((M - (2 * (D - L - K - J))) / 2) + (TRANSITION / 2)=25 29/32"; (B/2)+1.5"=24 3/32"; (B/2)-.125"=22 15/32"; (D-J-K-L)*2=2 3/4"; (F-((F-H)/2))/2=22 3/8"; (M - (2 * (D - L - K - J)))/2=15 3/4"; (NOZZLE_HEIGHT - (NOZZLE_HEIGHT / 8 * 2)) / 2=19 25/32"; (NOZZLE_WB_OD - NOZZLE_TOP_OD) / 4=4 9/16"; -(F-((F-H)/2))/2=-22 3/8"; A=178 3/4"; A/2=89 3/8"; B=45 3/16"; B/2=22 19/32"; B/4=11 5/16"; C=100 3/4"; C/2=50 3/8"; CLASS=1"; D=72 1/4"; D-L-K-J=1 3/8"; D-M=38"; E=84 15/16"; E/2=42 15/32"; E/52*15=24 1/2"; F=48 3/4"; F/2=24 3/8"; H=46 3/4"; H/2=23 3/8"; HEIGHT=77 3/32"; J=12 1/2"; J+K+L=70 7/8"; K=21 7/8"; L=36 1/2"; M=34 1/4"; M-(2*(D-L-K-J))=31 1/2"; N=17 3/32"; N+(H/2)=40 15/32"; NOZZLE_BOTTOM_ID=28 3/4"; NOZZLE_BOTTOM_RAD=14 3/8"; NOZZLE_BOTTOM_RAD-3*2=8 3/8"; NOZZLE_HEIGHT=52 3/4"; NOZZLE_HEIGHT/7*2=13 3/16"; NOZZLE_SIZE=21"; NOZZLE_TOP_OD=30 3/4"; NOZZLE_TOP_RAD=15 3/8"; NOZZLE_WB/4=9 13/16"; NOZZLE_WB_OD=49"; NOZZLE_WB_RAD=24 1/2"; NOZZLE_WB_RAD-2"=22 1/2"; P=18 1/4"; R=40"; R*1.1=44"; R+((B/2)+1.5")=64 3/32"; R-((B/2)+1.5")=15 29/32"; TRANSITION=20 11/32"; TRANSITION/2=10 5/32"; Type Comments=Vari-Plume Laboratory Exhaust Centrifugal Airfoil Class 1 Arr 10
- 402_CAVP-21H_CLASS_2: ((M - (2 * (D - L - K - J))) / 2) + (TRANSITION / 2)=25 29/32"; (B/2)+1.5"=24 3/32"; (B/2)-.125"=22 15/32"; (D-J-K-L)*2=2 3/4"; (F-((F-H)/2))/2=22 3/8"; (M - (2 * (D - L - K - J)))/2=15 3/4"; (NOZZLE_HEIGHT - (NOZZLE_HEIGHT / 8 * 2)) / 2=19 25/32"; (NOZZLE_WB_OD - NOZZLE_TOP_OD) / 4=4 9/16"; -(F-((F-H)/2))/2=-22 3/8"; A=178 3/4"; A/2=89 3/8"; B=45 3/16"; B/2=22 19/32"; B/4=11 5/16"; C=100 3/4"; C/2=50 3/8"; CLASS=2"; D=72 1/4"; D-L-K-J=1 3/8"; D-M=38"; E=84 15/16"; E/2=42 15/32"; E/52*15=24 1/2"; F=48 3/4"; F/2=24 3/8"; H=46 3/4"; H/2=23 3/8"; HEIGHT=77 3/32"; J=12 1/2"; J+K+L=70 7/8"; K=21 7/8"; L=36 1/2"; M=34 1/4"; M-(2*(D-L-K-J))=31 1/2"; N=17 3/32"; N+(H/2)=40 15/32"; NOZZLE_BOTTOM_ID=28 3/4"; NOZZLE_BOTTOM_RAD=14 3/8"; NOZZLE_BOTTOM_RAD-3*2=8 3/8"; NOZZLE_HEIGHT=52 3/4"; NOZZLE_HEIGHT/7*2=13 3/16"; NOZZLE_SIZE=21"; NOZZLE_TOP_OD=30 3/4"; NOZZLE_TOP_RAD=15 3/8"; NOZZLE_WB/4=9 13/16"; NOZZLE_WB_OD=49"; NOZZLE_WB_RAD=24 1/2"; NOZZLE_WB_RAD-2"=22 1/2"; P=19 1/2"; R=40"; R*1.1=44"; R+((B/2)+1.5")=64 3/32"; R-((B/2)+1.5")=15 29/32"; TRANSITION=20 11/32"; TRANSITION/2=10 5/32"; Type Comments=Vari-Plume Laboratory Exhaust Centrifugal Airfoil Class 2 Arr 10
- 402_CAVP-21L_CLASS_2: ((M - (2 * (D - L - K - J))) / 2) + (TRANSITION / 2)=25 29/32"; (B/2)+1.5"=24 3/32"; (B/2)-.125"=22 15/32"; (D-J-K-L)*2=2 3/4"; (F-((F-H)/2))/2=22 3/8"; (M - (2 * (D - L - K - J)))/2=15 3/4"; (NOZZLE_HEIGHT - (NOZZLE_HEIGHT / 8 * 2)) / 2=19 25/32"; (NOZZLE_WB_OD - NOZZLE_TOP_OD) / 4=4 9/16"; -(F-((F-H)/2))/2=-22 3/8"; A=178 3/4"; A/2=89 3/8"; B=45 3/16"; B/2=22 19/32"; B/4=11 5/16"; C=100 3/4"; C/2=50 3/8"; CLASS=2"; D=72 1/4"; D-L-K-J=1 3/8"; D-M=38"; E=84 15/16"; E/2=42 15/32"; E/52*15=24 1/2"; F=48 3/4"; F/2=24 3/8"; H=46 3/4"; H/2=23 3/8"; HEIGHT=77 3/32"; J=12 1/2"; J+K+L=70 7/8"; K=21 7/8"; L=36 1/2"; M=34 1/4"; M-(2*(D-L-K-J))=31 1/2"; N=17 3/32"; N+(H/2)=40 15/32"; NOZZLE_BOTTOM_ID=28 3/4"; NOZZLE_BOTTOM_RAD=14 3/8"; NOZZLE_BOTTOM_RAD-3*2=8 3/8"; NOZZLE_HEIGHT=52 3/4"; NOZZLE_HEIGHT/7*2=13 3/16"; NOZZLE_SIZE=21"; NOZZLE_TOP_OD=30 3/4"; NOZZLE_TOP_RAD=15 3/8"; NOZZLE_WB/4=9 13/16"; NOZZLE_WB_OD=49"; NOZZLE_WB_RAD=24 1/2"; NOZZLE_WB_RAD-2"=22 1/2"; P=19 1/2"; R=40"; R*1.1=44"; R+((B/2)+1.5")=64 3/32"; R-((B/2)+1.5")=15 29/32"; TRANSITION=20 11/32"; TRANSITION/2=10 5/32"; Type Comments=Vari-Plume Laboratory Exhaust Centrifugal Airfoil Class 2 Arr 10
- 365_CAVP-27H_CLASS_1: ((M - (2 * (D - L - K - J))) / 2) + (TRANSITION / 2)=27 19/32"; (B/2)+1.5"=22 23/32"; (B/2)-.125"=21 3/32"; (D-J-K-L)*2=2"; (F-((F-H)/2))/2=20 7/16"; (M - (2 * (D - L - K - J)))/2=14 1/16"; (NOZZLE_HEIGHT - (NOZZLE_HEIGHT / 8 * 2)) / 2=22 3/4"; (NOZZLE_WB_OD - NOZZLE_TOP_OD) / 4=5 11/32"; -(F-((F-H)/2))/2=-20 7/16"; A=153 13/16"; A/2=76 29/32"; B=42 7/16"; B/2=21 7/32"; B/4=10 5/8"; C=92 3/16"; C/2=46 3/32"; CLASS=1"; D=66 7/8"; D-L-K-J=1"; D-M=36 3/4"; E=77 5/16"; E/2=38 21/32"; E/52*15=22 5/16"; F=44 7/8"; F/2=22 7/16"; H=42 7/8"; H/2=21 7/16"; HEIGHT=69 3/4"; J=11"; J+K+L=65 7/8"; K=22 3/4"; L=32 1/8"; M=30 1/8"; M-(2*(D-L-K-J))=28 1/8"; N=15 7/32"; N+(H/2)=36 21/32"; NOZZLE_BOTTOM_ID=38 5/16"; NOZZLE_BOTTOM_RAD=19 5/32"; NOZZLE_BOTTOM_RAD-3*2=13 5/32"; NOZZLE_HEIGHT=60 5/8"; NOZZLE_HEIGHT/7*2=15 5/32"; NOZZLE_SIZE=27"; NOZZLE_TOP_OD=39 11/16"; NOZZLE_TOP_RAD=19 27/32"; NOZZLE_WB/4=12 3/16"; NOZZLE_WB_OD=61"; NOZZLE_WB_RAD=30 1/2"; NOZZLE_WB_RAD-2"=28 1/2"; P=18 1/4"; R=36"; R*1.1=39 19/32"; R+((B/2)+1.5")=58 23/32"; R-((B/2)+1.5")=13 9/32"; TRANSITION=27 3/32"; TRANSITION/2=13 17/32"; Type Comments=Vari-Plume Laboratory Exhaust Centrifugal Airfoil Class 1 Arr 10
- 365_CAVP-27L_CLASS_1: ((M - (2 * (D - L - K - J))) / 2) + (TRANSITION / 2)=27 19/32"; (B/2)+1.5"=22 23/32"; (B/2)-.125"=21 3/32"; (D-J-K-L)*2=2"; (F-((F-H)/2))/2=20 7/16"; (M - (2 * (D - L - K - J)))/2=14 1/16"; (NOZZLE_HEIGHT - (NOZZLE_HEIGHT / 8 * 2)) / 2=22 3/4"; (NOZZLE_WB_OD - NOZZLE_TOP_OD) / 4=5 11/32"; -(F-((F-H)/2))/2=-20 7/16"; A=153 13/16"; A/2=76 29/32"; B=42 7/16"; B/2=21 7/32"; B/4=10 5/8"; C=92 3/16"; C/2=46 3/32"; CLASS=1"; D=66 7/8"; D-L-K-J=1"; D-M=36 3/4"; E=77 5/16"; E/2=38 21/32"; E/52*15=22 5/16"; F=44 7/8"; F/2=22 7/16"; H=42 7/8"; H/2=21 7/16"; HEIGHT=69 3/4"; J=11"; J+K+L=65 7/8"; K=22 3/4"; L=32 1/8"; M=30 1/8"; M-(2*(D-L-K-J))=28 1/8"; N=15 7/32"; N+(H/2)=36 21/32"; NOZZLE_BOTTOM_ID=38 5/16"; NOZZLE_BOTTOM_RAD=19 5/32"; NOZZLE_BOTTOM_RAD-3*2=13 5/32"; NOZZLE_HEIGHT=60 5/8"; NOZZLE_HEIGHT/7*2=15 5/32"; NOZZLE_SIZE=27"; NOZZLE_TOP_OD=39 11/16"; NOZZLE_TOP_RAD=19 27/32"; NOZZLE_WB/4=12 3/16"; NOZZLE_WB_OD=61"; NOZZLE_WB_RAD=30 1/2"; NOZZLE_WB_RAD-2"=28 1/2"; P=18 1/4"; R=36"; R*1.1=39 19/32"; R+((B/2)+1.5")=58 23/32"; R-((B/2)+1.5")=13 9/32"; TRANSITION=27 3/32"; TRANSITION/2=13 17/32"; Type Comments=Vari-Plume Laboratory Exhaust Centrifugal Airfoil Class 1 Arr 10
- 365_CAVP-27H_CLASS_2: ((M - (2 * (D - L - K - J))) / 2) + (TRANSITION / 2)=27 19/32"; (B/2)+1.5"=22 23/32"; (B/2)-.125"=21 3/32"; (D-J-K-L)*2=2"; (F-((F-H)/2))/2=20 7/16"; (M - (2 * (D - L - K - J)))/2=14 1/16"; (NOZZLE_HEIGHT - (NOZZLE_HEIGHT / 8 * 2)) / 2=22 3/4"; (NOZZLE_WB_OD - NOZZLE_TOP_OD) / 4=5 11/32"; -(F-((F-H)/2))/2=-20 7/16"; A=153 13/16"; A/2=76 29/32"; B=42 7/16"; B/2=21 7/32"; B/4=10 5/8"; C=92 3/16"; C/2=46 3/32"; CLASS=2"; D=67 1/8"; D-L-K-J=1"; D-M=37"; E=77 5/16"; E/2=38 21/32"; E/52*15=22 5/16"; F=44 7/8"; F/2=22 7/16"; H=42 7/8"; H/2=21 7/16"; HEIGHT=69 3/4"; J=11"; J+K+L=66 1/8"; K=23"; L=32 1/8"; M=30 1/8"; M-(2*(D-L-K-J))=28 1/8"; N=15 7/32"; N+(H/2)=36 21/32"; NOZZLE_BOTTOM_ID=38 5/16"; NOZZLE_BOTTOM_RAD=19 5/32"; NOZZLE_BOTTOM_RAD-3*2=13 5/32"; NOZZLE_HEIGHT=60 5/8"; NOZZLE_HEIGHT/7*2=15 5/32"; NOZZLE_SIZE=27"; NOZZLE_TOP_OD=39 11/16"; NOZZLE_TOP_RAD=19 27/32"; NOZZLE_WB/4=12 3/16"; NOZZLE_WB_OD=61"; NOZZLE_WB_RAD=30 1/2"; NOZZLE_WB_RAD-2"=28 1/2"; P=18 1/2"; R=36"; R*1.1=39 19/32"; R+((B/2)+1.5")=58 23/32"; R-((B/2)+1.5")=13 9/32"; TRANSITION=27 3/32"; TRANSITION/2=13 17/32"; Type Comments=Vari-Plume Laboratory Exhaust Centrifugal Airfoil Class 2 Arr 10
- 365_CAVP-27L_CLASS_2: ((M - (2 * (D - L - K - J))) / 2) + (TRANSITION / 2)=27 19/32"; (B/2)+1.5"=22 23/32"; (B/2)-.125"=21 3/32"; (D-J-K-L)*2=2"; (F-((F-H)/2))/2=20 7/16"; (M - (2 * (D - L - K - J)))/2=14 1/16"; (NOZZLE_HEIGHT - (NOZZLE_HEIGHT / 8 * 2)) / 2=22 3/4"; (NOZZLE_WB_OD - NOZZLE_TOP_OD) / 4=5 11/32"; -(F-((F-H)/2))/2=-20 7/16"; A=153 13/16"; A/2=76 29/32"; B=42 7/16"; B/2=21 7/32"; B/4=10 5/8"; C=92 3/16"; C/2=46 3/32"; CLASS=2"; D=67 1/8"; D-L-K-J=1"; D-M=37"; E=77 5/16"; E/2=38 21/32"; E/52*15=22 5/16"; F=44 7/8"; F/2=22 7/16"; H=42 7/8"; H/2=21 7/16"; HEIGHT=69 3/4"; J=11"; J+K+L=66 1/8"; K=23"; L=32 1/8"; M=30 1/8"; M-(2*(D-L-K-J))=28 1/8"; N=15 7/32"; N+(H/2)=36 21/32"; NOZZLE_BOTTOM_ID=38 5/16"; NOZZLE_BOTTOM_RAD=19 5/32"; NOZZLE_BOTTOM_RAD-3*2=13 5/32"; NOZZLE_HEIGHT=60 5/8"; NOZZLE_HEIGHT/7*2=15 5/32"; NOZZLE_SIZE=27"; NOZZLE_TOP_OD=39 11/16"; NOZZLE_TOP_RAD=19 27/32"; NOZZLE_WB/4=12 3/16"; NOZZLE_WB_OD=61"; NOZZLE_WB_RAD=30 1/2"; NOZZLE_WB_RAD-2"=28 1/2"; P=18 1/2"; R=36"; R*1.1=39 19/32"; R+((B/2)+1.5")=58 23/32"; R-((B/2)+1.5")=13 9/32"; TRANSITION=27 3/32"; TRANSITION/2=13 17/32"; Type Comments=Vari-Plume Laboratory Exhaust Centrifugal Airfoil Class 2 Arr 10
- 402_CAVP-27H_CLASS_1: ((M - (2 * (D - L - K - J))) / 2) + (TRANSITION / 2)=29 9/32"; (B/2)+1.5"=24 3/32"; (B/2)-.125"=22 15/32"; (D-J-K-L)*2=2 3/4"; (F-((F-H)/2))/2=22 3/8"; (M - (2 * (D - L - K - J)))/2=15 3/4"; (NOZZLE_HEIGHT - (NOZZLE_HEIGHT / 8 * 2)) / 2=22 3/4"; (NOZZLE_WB_OD - NOZZLE_TOP_OD) / 4=5 11/32"; -(F-((F-H)/2))/2=-22 3/8"; A=178 3/4"; A/2=89 3/8"; B=45 3/16"; B/2=22 19/32"; B/4=11 5/16"; C=100 3/4"; C/2=50 3/8"; CLASS=1"; D=72 1/4"; D-L-K-J=1 3/8"; D-M=38"; E=84 15/16"; E/2=42 15/32"; E/52*15=24 1/2"; F=48 3/4"; F/2=24 3/8"; H=46 3/4"; H/2=23 3/8"; HEIGHT=77 3/32"; J=12 1/2"; J+K+L=70 7/8"; K=21 7/8"; L=36 1/2"; M=34 1/4"; M-(2*(D-L-K-J))=31 1/2"; N=17 3/32"; N+(H/2)=40 15/32"; NOZZLE_BOTTOM_ID=38 5/16"; NOZZLE_BOTTOM_RAD=19 5/32"; NOZZLE_BOTTOM_RAD-3*2=13 5/32"; NOZZLE_HEIGHT=60 5/8"; NOZZLE_HEIGHT/7*2=15 5/32"; NOZZLE_SIZE=27"; NOZZLE_TOP_OD=39 11/16"; NOZZLE_TOP_RAD=19 27/32"; NOZZLE_WB/4=12 3/16"; NOZZLE_WB_OD=61"; NOZZLE_WB_RAD=30 1/2"; NOZZLE_WB_RAD-2"=28 1/2"; P=18 1/4"; R=40"; R*1.1=44"; R+((B/2)+1.5")=64 3/32"; R-((B/2)+1.5")=15 29/32"; TRANSITION=27 3/32"; TRANSITION/2=13 17/32"; Type Comments=Vari-Plume Laboratory Exhaust Centrifugal Airfoil Class 1 Arr 10
- 402_CAVP-27L_CLASS_1: ((M - (2 * (D - L - K - J))) / 2) + (TRANSITION / 2)=29 9/32"; (B/2)+1.5"=24 3/32"; (B/2)-.125"=22 15/32"; (D-J-K-L)*2=2 3/4"; (F-((F-H)/2))/2=22 3/8"; (M - (2 * (D - L - K - J)))/2=15 3/4"; (NOZZLE_HEIGHT - (NOZZLE_HEIGHT / 8 * 2)) / 2=22 3/4"; (NOZZLE_WB_OD - NOZZLE_TOP_OD) / 4=5 11/32"; -(F-((F-H)/2))/2=-22 3/8"; A=178 3/4"; A/2=89 3/8"; B=45 3/16"; B/2=22 19/32"; B/4=11 5/16"; C=100 3/4"; C/2=50 3/8"; CLASS=1"; D=72 1/4"; D-L-K-J=1 3/8"; D-M=38"; E=84 15/16"; E/2=42 15/32"; E/52*15=24 1/2"; F=48 3/4"; F/2=24 3/8"; H=46 3/4"; H/2=23 3/8"; HEIGHT=77 3/32"; J=12 1/2"; J+K+L=70 7/8"; K=21 7/8"; L=36 1/2"; M=34 1/4"; M-(2*(D-L-K-J))=31 1/2"; N=17 3/32"; N+(H/2)=40 15/32"; NOZZLE_BOTTOM_ID=38 5/16"; NOZZLE_BOTTOM_RAD=19 5/32"; NOZZLE_BOTTOM_RAD-3*2=13 5/32"; NOZZLE_HEIGHT=60 5/8"; NOZZLE_HEIGHT/7*2=15 5/32"; NOZZLE_SIZE=27"; NOZZLE_TOP_OD=39 11/16"; NOZZLE_TOP_RAD=19 27/32"; NOZZLE_WB/4=12 3/16"; NOZZLE_WB_OD=61"; NOZZLE_WB_RAD=30 1/2"; NOZZLE_WB_RAD-2"=28 1/2"; P=18 1/4"; R=40"; R*1.1=44"; R+((B/2)+1.5")=64 3/32"; R-((B/2)+1.5")=15 29/32"; TRANSITION=27 3/32"; TRANSITION/2=13 17/32"; Type Comments=Vari-Plume Laboratory Exhaust Centrifugal Airfoil Class 1 Arr 10
- 402_CAVP-27H_CLASS_2: ((M - (2 * (D - L - K - J))) / 2) + (TRANSITION / 2)=29 9/32"; (B/2)+1.5"=24 3/32"; (B/2)-.125"=22 15/32"; (D-J-K-L)*2=2 3/4"; (F-((F-H)/2))/2=22 3/8"; (M - (2 * (D - L - K - J)))/2=15 3/4"; (NOZZLE_HEIGHT - (NOZZLE_HEIGHT / 8 * 2)) / 2=22 3/4"; (NOZZLE_WB_OD - NOZZLE_TOP_OD) / 4=5 11/32"; -(F-((F-H)/2))/2=-22 3/8"; A=178 3/4"; A/2=89 3/8"; B=45 3/16"; B/2=22 19/32"; B/4=11 5/16"; C=100 3/4"; C/2=50 3/8"; CLASS=2"; D=72 1/4"; D-L-K-J=1 3/8"; D-M=38"; E=84 15/16"; E/2=42 15/32"; E/52*15=24 1/2"; F=48 3/4"; F/2=24 3/8"; H=46 3/4"; H/2=23 3/8"; HEIGHT=77 3/32"; J=12 1/2"; J+K+L=70 7/8"; K=21 7/8"; L=36 1/2"; M=34 1/4"; M-(2*(D-L-K-J))=31 1/2"; N=17 3/32"; N+(H/2)=40 15/32"; NOZZLE_BOTTOM_ID=38 5/16"; NOZZLE_BOTTOM_RAD=19 5/32"; NOZZLE_BOTTOM_RAD-3*2=13 5/32"; NOZZLE_HEIGHT=60 5/8"; NOZZLE_HEIGHT/7*2=15 5/32"; NOZZLE_SIZE=27"; NOZZLE_TOP_OD=39 11/16"; NOZZLE_TOP_RAD=19 27/32"; NOZZLE_WB/4=12 3/16"; NOZZLE_WB_OD=61"; NOZZLE_WB_RAD=30 1/2"; NOZZLE_WB_RAD-2"=28 1/2"; P=19 1/2"; R=40"; R*1.1=44"; R+((B/2)+1.5")=64 3/32"; R-((B/2)+1.5")=15 29/32"; TRANSITION=27 3/32"; TRANSITION/2=13 17/32"; Type Comments=Vari-Plume Laboratory Exhaust Centrifugal Airfoil Class 2 Arr 10
- 402_CAVP-27L_CLASS_2: ((M - (2 * (D - L - K - J))) / 2) + (TRANSITION / 2)=29 9/32"; (B/2)+1.5"=24 3/32"; (B/2)-.125"=22 15/32"; (D-J-K-L)*2=2 3/4"; (F-((F-H)/2))/2=22 3/8"; (M - (2 * (D - L - K - J)))/2=15 3/4"; (NOZZLE_HEIGHT - (NOZZLE_HEIGHT / 8 * 2)) / 2=22 3/4"; (NOZZLE_WB_OD - NOZZLE_TOP_OD) / 4=5 11/32"; -(F-((F-H)/2))/2=-22 3/8"; A=178 3/4"; A/2=89 3/8"; B=45 3/16"; B/2=22 19/32"; B/4=11 5/16"; C=100 3/4"; C/2=50 3/8"; CLASS=2"; D=72 1/4"; D-L-K-J=1 3/8"; D-M=38"; E=84 15/16"; E/2=42 15/32"; E/52*15=24 1/2"; F=48 3/4"; F/2=24 3/8"; H=46 3/4"; H/2=23 3/8"; HEIGHT=77 3/32"; J=12 1/2"; J+K+L=70 7/8"; K=21 7/8"; L=36 1/2"; M=34 1/4"; M-(2*(D-L-K-J))=31 1/2"; N=17 3/32"; N+(H/2)=40 15/32"; NOZZLE_BOTTOM_ID=38 5/16"; NOZZLE_BOTTOM_RAD=19 5/32"; NOZZLE_BOTTOM_RAD-3*2=13 5/32"; NOZZLE_HEIGHT=60 5/8"; NOZZLE_HEIGHT/7*2=15 5/32"; NOZZLE_SIZE=27"; NOZZLE_TOP_OD=39 11/16"; NOZZLE_TOP_RAD=19 27/32"; NOZZLE_WB/4=12 3/16"; NOZZLE_WB_OD=61"; NOZZLE_WB_RAD=30 1/2"; NOZZLE_WB_RAD-2"=28 1/2"; P=19 1/2"; R=40"; R*1.1=44"; R+((B/2)+1.5")=64 3/32"; R-((B/2)+1.5")=15 29/32"; TRANSITION=27 3/32"; TRANSITION/2=13 17/32"; Type Comments=Vari-Plume Laboratory Exhaust Centrifugal Airfoil Class 2 Arr 10
- 445_CAVP-27H_CLASS_1: ((M - (2 * (D - L - K - J))) / 2) + (TRANSITION / 2)=30 29/32"; (B/2)+1.5"=26 7/32"; (B/2)-.125"=24 19/32"; (D-J-K-L)*2=2 3/4"; (F-((F-H)/2))/2=24 3/8"; (M - (2 * (D - L - K - J)))/2=17 3/8"; (NOZZLE_HEIGHT - (NOZZLE_HEIGHT / 8 * 2)) / 2=22 3/4"; (NOZZLE_WB_OD - NOZZLE_TOP_OD) / 4=5 11/32"; -(F-((F-H)/2))/2=-24 3/8"; A=190 7/8"; A/2=95 7/16"; B=49 7/16"; B/2=24 23/32"; B/4=12 3/8"; C=112 7/8"; C/2=56 7/16"; CLASS=1"; D=80"; D-L-K-J=1 3/8"; D-M=42 1/2"; E=93 11/16"; E/2=46 27/32"; E/52*15=27 1/32"; F=52 3/4"; F/2=26 3/8"; H=50 3/4"; H/2=25 3/8"; HEIGHT=84 29/32"; J=13"; J+K+L=78 5/8"; K=25 7/8"; L=39 3/4"; M=37 1/2"; M-(2*(D-L-K-J))=34 3/4"; N=19 15/32"; N+(H/2)=44 27/32"; NOZZLE_BOTTOM_ID=38 5/16"; NOZZLE_BOTTOM_RAD=19 5/32"; NOZZLE_BOTTOM_RAD-3*2=13 5/32"; NOZZLE_HEIGHT=60 5/8"; NOZZLE_HEIGHT/7*2=15 5/32"; NOZZLE_SIZE=27"; NOZZLE_TOP_OD=39 11/16"; NOZZLE_TOP_RAD=19 27/32"; NOZZLE_WB/4=12 3/16"; NOZZLE_WB_OD=61"; NOZZLE_WB_RAD=30 1/2"; NOZZLE_WB_RAD-2"=28 1/2"; P=18 1/4"; R=44"; R*1.1=48 13/32"; R+((B/2)+1.5")=70 7/32"; R-((B/2)+1.5")=17 25/32"; TRANSITION=27 3/32"; TRANSITION/2=13 17/32"; Type Comments=Vari-Plume Laboratory Exhaust Centrifugal Airfoil Class 1 Arr 10
- 445_CAVP-27L_CLASS_1: ((M - (2 * (D - L - K - J))) / 2) + (TRANSITION / 2)=30 29/32"; (B/2)+1.5"=26 7/32"; (B/2)-.125"=24 19/32"; (D-J-K-L)*2=2 3/4"; (F-((F-H)/2))/2=24 3/8"; (M - (2 * (D - L - K - J)))/2=17 3/8"; (NOZZLE_HEIGHT - (NOZZLE_HEIGHT / 8 * 2)) / 2=22 3/4"; (NOZZLE_WB_OD - NOZZLE_TOP_OD) / 4=5 11/32"; -(F-((F-H)/2))/2=-24 3/8"; A=190 7/8"; A/2=95 7/16"; B=49 7/16"; B/2=24 23/32"; B/4=12 3/8"; C=112 7/8"; C/2=56 7/16"; CLASS=1"; D=80"; D-L-K-J=1 3/8"; D-M=42 1/2"; E=93 11/16"; E/2=46 27/32"; E/52*15=27 1/32"; F=52 3/4"; F/2=26 3/8"; H=50 3/4"; H/2=25 3/8"; HEIGHT=84 29/32"; J=13"; J+K+L=78 5/8"; K=25 7/8"; L=39 3/4"; M=37 1/2"; M-(2*(D-L-K-J))=34 3/4"; N=19 15/32"; N+(H/2)=44 27/32"; NOZZLE_BOTTOM_ID=38 5/16"; NOZZLE_BOTTOM_RAD=19 5/32"; NOZZLE_BOTTOM_RAD-3*2=13 5/32"; NOZZLE_HEIGHT=60 5/8"; NOZZLE_HEIGHT/7*2=15 5/32"; NOZZLE_SIZE=27"; NOZZLE_TOP_OD=39 11/16"; NOZZLE_TOP_RAD=19 27/32"; NOZZLE_WB/4=12 3/16"; NOZZLE_WB_OD=61"; NOZZLE_WB_RAD=30 1/2"; NOZZLE_WB_RAD-2"=28 1/2"; P=18 1/4"; R=44"; R*1.1=48 13/32"; R+((B/2)+1.5")=70 7/32"; R-((B/2)+1.5")=17 25/32"; TRANSITION=27 3/32"; TRANSITION/2=13 17/32"; Type Comments=Vari-Plume Laboratory Exhaust Centrifugal Airfoil Class 1 Arr 10
- 445_CAVP-27H_CLASS_2: ((M - (2 * (D - L - K - J))) / 2) + (TRANSITION / 2)=30 29/32"; (B/2)+1.5"=26 7/32"; (B/2)-.125"=24 19/32"; (D-J-K-L)*2=2 3/4"; (F-((F-H)/2))/2=24 3/8"; (M - (2 * (D - L - K - J)))/2=17 3/8"; (NOZZLE_HEIGHT - (NOZZLE_HEIGHT / 8 * 2)) / 2=22 3/4"; (NOZZLE_WB_OD - NOZZLE_TOP_OD) / 4=5 11/32"; -(F-((F-H)/2))/2=-24 3/8"; A=190 7/8"; A/2=95 7/16"; B=49 7/16"; B/2=24 23/32"; B/4=12 3/8"; C=112 7/8"; C/2=56 7/16"; CLASS=2"; D=80"; D-L-K-J=1 3/8"; D-M=42 1/2"; E=93 11/16"; E/2=46 27/32"; E/52*15=27 1/32"; F=52 3/4"; F/2=26 3/8"; H=50 3/4"; H/2=25 3/8"; HEIGHT=84 29/32"; J=13"; J+K+L=78 5/8"; K=25 7/8"; L=39 3/4"; M=37 1/2"; M-(2*(D-L-K-J))=34 3/4"; N=19 15/32"; N+(H/2)=44 27/32"; NOZZLE_BOTTOM_ID=38 5/16"; NOZZLE_BOTTOM_RAD=19 5/32"; NOZZLE_BOTTOM_RAD-3*2=13 5/32"; NOZZLE_HEIGHT=60 5/8"; NOZZLE_HEIGHT/7*2=15 5/32"; NOZZLE_SIZE=27"; NOZZLE_TOP_OD=39 11/16"; NOZZLE_TOP_RAD=19 27/32"; NOZZLE_WB/4=12 3/16"; NOZZLE_WB_OD=61"; NOZZLE_WB_RAD=30 1/2"; NOZZLE_WB_RAD-2"=28 1/2"; P=19 1/2"; R=44"; R*1.1=48 13/32"; R+((B/2)+1.5")=70 7/32"; R-((B/2)+1.5")=17 25/32"; TRANSITION=27 3/32"; TRANSITION/2=13 17/32"; Type Comments=Vari-Plume Laboratory Exhaust Centrifugal Airfoil Class 2 Arr 10
- 445_CAVP-27L_CLASS_2: ((M - (2 * (D - L - K - J))) / 2) + (TRANSITION / 2)=30 29/32"; (B/2)+1.5"=26 7/32"; (B/2)-.125"=24 19/32"; (D-J-K-L)*2=2 3/4"; (F-((F-H)/2))/2=24 3/8"; (M - (2 * (D - L - K - J)))/2=17 3/8"; (NOZZLE_HEIGHT - (NOZZLE_HEIGHT / 8 * 2)) / 2=22 3/4"; (NOZZLE_WB_OD - NOZZLE_TOP_OD) / 4=5 11/32"; -(F-((F-H)/2))/2=-24 3/8"; A=190 7/8"; A/2=95 7/16"; B=49 7/16"; B/2=24 23/32"; B/4=12 3/8"; C=112 7/8"; C/2=56 7/16"; CLASS=2"; D=80"; D-L-K-J=1 3/8"; D-M=42 1/2"; E=93 11/16"; E/2=46 27/32"; E/52*15=27 1/32"; F=52 3/4"; F/2=26 3/8"; H=50 3/4"; H/2=25 3/8"; HEIGHT=84 29/32"; J=13"; J+K+L=78 5/8"; K=25 7/8"; L=39 3/4"; M=37 1/2"; M-(2*(D-L-K-J))=34 3/4"; N=19 15/32"; N+(H/2)=44 27/32"; NOZZLE_BOTTOM_ID=38 5/16"; NOZZLE_BOTTOM_RAD=19 5/32"; NOZZLE_BOTTOM_RAD-3*2=13 5/32"; NOZZLE_HEIGHT=60 5/8"; NOZZLE_HEIGHT/7*2=15 5/32"; NOZZLE_SIZE=27"; NOZZLE_TOP_OD=39 11/16"; NOZZLE_TOP_RAD=19 27/32"; NOZZLE_WB/4=12 3/16"; NOZZLE_WB_OD=61"; NOZZLE_WB_RAD=30 1/2"; NOZZLE_WB_RAD-2"=28 1/2"; P=19 1/2"; R=44"; R*1.1=48 13/32"; R+((B/2)+1.5")=70 7/32"; R-((B/2)+1.5")=17 25/32"; TRANSITION=27 3/32"; TRANSITION/2=13 17/32"; Type Comments=Vari-Plume Laboratory Exhaust Centrifugal Airfoil Class 2 Arr 10
- 490_CAVP-27H_CLASS_1: ((M - (2 * (D - L - K - J))) / 2) + (TRANSITION / 2)=32 5/8"; (B/2)+1.5"=29"; (B/2)-.125"=27 3/8"; (D-J-K-L)*2=2 3/4"; (F-((F-H)/2))/2=27 27/32"; (M - (2 * (D - L - K - J)))/2=19 3/32"; (NOZZLE_HEIGHT - (NOZZLE_HEIGHT / 8 * 2)) / 2=22 3/4"; (NOZZLE_WB_OD - NOZZLE_TOP_OD) / 4=5 11/32"; -(F-((F-H)/2))/2=-27 27/32"; A=217 13/16"; A/2=108 29/32"; B=55"; B/2=27 1/2"; B/4=13 3/4"; C=123 1/16"; C/2=61 17/32"; CLASS=1"; D=79 15/16"; D-L-K-J=1 3/8"; D-M=39"; E=102 15/16"; E/2=51 15/32"; E/52*15=29 11/16"; F=59 11/16"; F/2=29 27/32"; H=57 11/16"; H/2=28 27/32"; HEIGHT=92 15/16"; J=13 1/2"; J+K+L=78 9/16"; K=21 7/8"; L=43 3/16"; M=40 15/16"; M-(2*(D-L-K-J))=38 3/16"; N=20 5/8"; N+(H/2)=49 15/32"; NOZZLE_BOTTOM_ID=38 5/16"; NOZZLE_BOTTOM_RAD=19 5/32"; NOZZLE_BOTTOM_RAD-3*2=13 5/32"; NOZZLE_HEIGHT=60 5/8"; NOZZLE_HEIGHT/7*2=15 5/32"; NOZZLE_SIZE=27"; NOZZLE_TOP_OD=39 11/16"; NOZZLE_TOP_RAD=19 27/32"; NOZZLE_WB/4=12 3/16"; NOZZLE_WB_OD=61"; NOZZLE_WB_RAD=30 1/2"; NOZZLE_WB_RAD-2"=28 1/2"; P=18 1/2"; R=48"; R*1.1=52 13/16"; R+((B/2)+1.5")=77"; R-((B/2)+1.5")=19"; TRANSITION=27 3/32"; TRANSITION/2=13 17/32"; Type Comments=Vari-Plume Laboratory Exhaust Centrifugal Airfoil Class 1 Arr 10
- 490_CAVP-27L_CLASS_1: ((M - (2 * (D - L - K - J))) / 2) + (TRANSITION / 2)=32 5/8"; (B/2)+1.5"=29"; (B/2)-.125"=27 3/8"; (D-J-K-L)*2=2 3/4"; (F-((F-H)/2))/2=27 27/32"; (M - (2 * (D - L - K - J)))/2=19 3/32"; (NOZZLE_HEIGHT - (NOZZLE_HEIGHT / 8 * 2)) / 2=22 3/4"; (NOZZLE_WB_OD - NOZZLE_TOP_OD) / 4=5 11/32"; -(F-((F-H)/2))/2=-27 27/32"; A=217 13/16"; A/2=108 29/32"; B=55"; B/2=27 1/2"; B/4=13 3/4"; C=123 1/16"; C/2=61 17/32"; CLASS=1"; D=79 15/16"; D-L-K-J=1 3/8"; D-M=39"; E=102 15/16"; E/2=51 15/32"; E/52*15=29 11/16"; F=59 11/16"; F/2=29 27/32"; H=57 11/16"; H/2=28 27/32"; HEIGHT=92 15/16"; J=13 1/2"; J+K+L=78 9/16"; K=21 7/8"; L=43 3/16"; M=40 15/16"; M-(2*(D-L-K-J))=38 3/16"; N=20 5/8"; N+(H/2)=49 15/32"; NOZZLE_BOTTOM_ID=38 5/16"; NOZZLE_BOTTOM_RAD=19 5/32"; NOZZLE_BOTTOM_RAD-3*2=13 5/32"; NOZZLE_HEIGHT=60 5/8"; NOZZLE_HEIGHT/7*2=15 5/32"; NOZZLE_SIZE=27"; NOZZLE_TOP_OD=39 11/16"; NOZZLE_TOP_RAD=19 27/32"; NOZZLE_WB/4=12 3/16"; NOZZLE_WB_OD=61"; NOZZLE_WB_RAD=30 1/2"; NOZZLE_WB_RAD-2"=28 1/2"; P=18 1/2"; R=48"; R*1.1=52 13/16"; R+((B/2)+1.5")=77"; R-((B/2)+1.5")=19"; TRANSITION=27 3/32"; TRANSITION/2=13 17/32"; Type Comments=Vari-Plume Laboratory Exhaust Centrifugal Airfoil Class 1 Arr 10
- 490_CAVP-27H_CLASS_2: ((M - (2 * (D - L - K - J))) / 2) + (TRANSITION / 2)=32 5/8"; (B/2)+1.5"=29"; (B/2)-.125"=27 3/8"; (D-J-K-L)*2=2 3/4"; (F-((F-H)/2))/2=27 27/32"; (M - (2 * (D - L - K - J)))/2=19 3/32"; (NOZZLE_HEIGHT - (NOZZLE_HEIGHT / 8 * 2)) / 2=22 3/4"; (NOZZLE_WB_OD - NOZZLE_TOP_OD) / 4=5 11/32"; -(F-((F-H)/2))/2=-27 27/32"; A=217 13/16"; A/2=108 29/32"; B=55"; B/2=27 1/2"; B/4=13 3/4"; C=123 1/16"; C/2=61 17/32"; CLASS=2"; D=83 15/16"; D-L-K-J=1 3/8"; D-M=43"; E=102 15/16"; E/2=51 15/32"; E/52*15=29 11/16"; F=59 11/16"; F/2=29 27/32"; H=57 11/16"; H/2=28 27/32"; HEIGHT=92 15/16"; J=13 1/2"; J+K+L=82 9/16"; K=25 7/8"; L=43 3/16"; M=40 15/16"; M-(2*(D-L-K-J))=38 3/16"; N=20 5/8"; N+(H/2)=49 15/32"; NOZZLE_BOTTOM_ID=38 5/16"; NOZZLE_BOTTOM_RAD=19 5/32"; NOZZLE_BOTTOM_RAD-3*2=13 5/32"; NOZZLE_HEIGHT=60 5/8"; NOZZLE_HEIGHT/7*2=15 5/32"; NOZZLE_SIZE=27"; NOZZLE_TOP_OD=39 11/16"; NOZZLE_TOP_RAD=19 27/32"; NOZZLE_WB/4=12 3/16"; NOZZLE_WB_OD=61"; NOZZLE_WB_RAD=30 1/2"; NOZZLE_WB_RAD-2"=28 1/2"; P=21 7/8"; R=48"; R*1.1=52 13/16"; R+((B/2)+1.5")=77"; R-((B/2)+1.5")=19"; TRANSITION=27 3/32"; TRANSITION/2=13 17/32"; Type Comments=Vari-Plume Laboratory Exhaust Centrifugal Airfoil Class 2 Arr 10
- 490_CAVP-27L_CLASS_2: ((M - (2 * (D - L - K - J))) / 2) + (TRANSITION / 2)=32 5/8"; (B/2)+1.5"=29"; (B/2)-.125"=27 3/8"; (D-J-K-L)*2=2 3/4"; (F-((F-H)/2))/2=27 27/32"; (M - (2 * (D - L - K - J)))/2=19 3/32"; (NOZZLE_HEIGHT - (NOZZLE_HEIGHT / 8 * 2)) / 2=22 3/4"; (NOZZLE_WB_OD - NOZZLE_TOP_OD) / 4=5 11/32"; -(F-((F-H)/2))/2=-27 27/32"; A=217 13/16"; A/2=108 29/32"; B=55"; B/2=27 1/2"; B/4=13 3/4"; C=123 1/16"; C/2=61 17/32"; CLASS=2"; D=83 15/16"; D-L-K-J=1 3/8"; D-M=43"; E=102 15/16"; E/2=51 15/32"; E/52*15=29 11/16"; F=59 11/16"; F/2=29 27/32"; H=57 11/16"; H/2=28 27/32"; HEIGHT=92 15/16"; J=13 1/2"; J+K+L=82 9/16"; K=25 7/8"; L=43 3/16"; M=40 15/16"; M-(2*(D-L-K-J))=38 3/16"; N=20 5/8"; N+(H/2)=49 15/32"; NOZZLE_BOTTOM_ID=38 5/16"; NOZZLE_BOTTOM_RAD=19 5/32"; NOZZLE_BOTTOM_RAD-3*2=13 5/32"; NOZZLE_HEIGHT=60 5/8"; NOZZLE_HEIGHT/7*2=15 5/32"; NOZZLE_SIZE=27"; NOZZLE_TOP_OD=39 11/16"; NOZZLE_TOP_RAD=19 27/32"; NOZZLE_WB/4=12 3/16"; NOZZLE_WB_OD=61"; NOZZLE_WB_RAD=30 1/2"; NOZZLE_WB_RAD-2"=28 1/2"; P=21 7/8"; R=48"; R*1.1=52 13/16"; R+((B/2)+1.5")=77"; R-((B/2)+1.5")=19"; TRANSITION=27 3/32"; TRANSITION/2=13 17/32"; Type Comments=Vari-Plume Laboratory Exhaust Centrifugal Airfoil Class 2 Arr 10

## geometry (parser evidence)
native form markers: Sweep x3
no freeform markers — native parametric forms only
